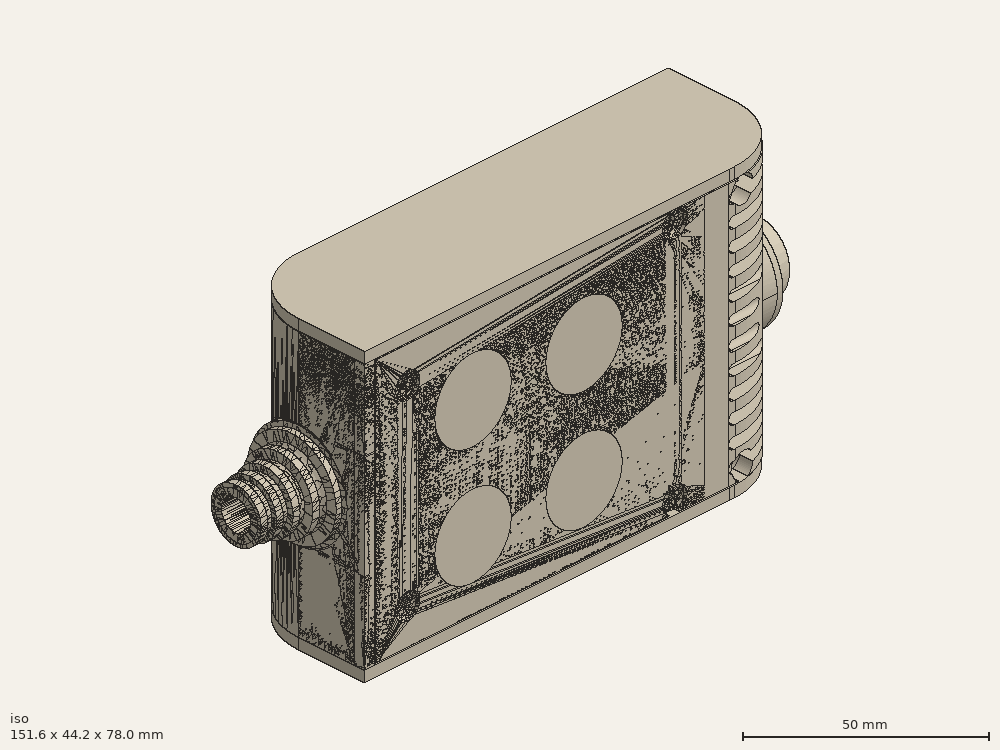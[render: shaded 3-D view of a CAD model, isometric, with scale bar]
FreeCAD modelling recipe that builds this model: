
FCSTD DOCUMENT  (FreeCAD 0.19R0.19.2)
Label: enclosure_203FCStd
License: All rights reserved
LicenseURL: http://en.wikipedia.org/wiki/All_rights_reserved
objects: Part::Revolution×152, Part::MultiFuse×146, Part::Feature×146, Sketcher::SketchObject×84, Part::Cut×70, Part::Cylinder×70, Part::Extrusion×67, Part::Fillet×58, Part::Box×36, App::MeasureDistance×4, PartDesign::Body×2, Image::ImagePlane×1
note: 831 computed .brp shape members not serialized (recipe doc carries the construction recipe); baked Part::Feature solids carry a one-line shape summary decoded from their .brp

FEATURE [Sketcher::SketchObject] Sketch  label="topSketch"
  FullyConstrained = true
  sketch-geometry (20):
    g0: LineSegment StartX=5.21097e-06 StartY=3 StartZ=0 EndX=5.21097e-06 EndY=19 EndZ=0
    g1: ArcOfCircle CenterX=19 CenterY=19 CenterZ=0 NormalX=0 NormalY=0 NormalZ=1 AngleXU=0 Radius=19 StartAngle=1.5708 EndAngle=3.14159
    g2: ArcOfCircle CenterX=19 CenterY=19 CenterZ=0 NormalX=0 NormalY=0 NormalZ=1 AngleXU=0 Radius=16 StartAngle=1.5708 EndAngle=3.14159
    g3: LineSegment StartX=114 StartY=35 StartZ=0 EndX=19 EndY=35 EndZ=0
    g4: LineSegment StartX=5.21097e-06 StartY=3 StartZ=0 EndX=5.21097e-06 EndY=0 EndZ=0
    g5: LineSegment StartX=3 StartY=0 StartZ=0 EndX=5.21097e-06 EndY=0 EndZ=0
    g6: LineSegment StartX=3 StartY=19 StartZ=0 EndX=3 EndY=0 EndZ=0
    g7: LineSegment StartX=19 StartY=38 StartZ=0 EndX=124 EndY=38 EndZ=0
    g8: Circle CenterX=119 CenterY=35 CenterZ=0 NormalX=0 NormalY=0 NormalZ=1 AngleXU=0 Radius=1
    g9: Circle CenterX=121 CenterY=35 CenterZ=0 NormalX=0 NormalY=0 NormalZ=1 AngleXU=0 Radius=1
    g10: Circle CenterX=121 CenterY=33 CenterZ=0 NormalX=0 NormalY=0 NormalZ=1 AngleXU=0 Radius=1
    g11: BSplineCurve PolesCount=3 KnotsCount=2 Degree=2 IsPeriodic=0
    g12: GeomPoint X=119 Y=35 Z=0
    g13: GeomPoint X=121 Y=33 Z=0
    g14: LineSegment StartX=119 StartY=35 StartZ=0 EndX=114 EndY=35 EndZ=0
    g15: ArcOfCircle CenterX=105 CenterY=19 CenterZ=0 NormalX=0 NormalY=0 NormalZ=1 AngleXU=0 Radius=19 StartAngle=5.7297 EndAngle=6.28319
    g16: ArcOfCircle CenterX=105 CenterY=19 CenterZ=0 NormalX=0 NormalY=0 NormalZ=1 AngleXU=0 Radius=16 StartAngle=5.60905 EndAngle=6.28319
    g17: LineSegment StartX=121 StartY=33 StartZ=0 EndX=121 EndY=19 EndZ=0
    g18: LineSegment StartX=124 StartY=38 StartZ=0 EndX=124 EndY=19 EndZ=0
    g19: LineSegment StartX=117.5 StartY=9.01251 StartZ=0 EndX=121.163 EndY=9.0125 EndZ=0
  constraints (46):
    c: Vertical(g0)
    c: Block(g0)
    c: Coincident(g1,g0)
    c: Block(g1)
    c: Coincident(g2,g1)
    c: Block(g2)
    c: Coincident(g3,g2)
    c: Horizontal(g3)
    c: Tangent(g3,g2)
    c: Coincident(g4,g0)
    c: Distance(g4) = 3
    c: Vertical(g4)
    c: Coincident(g5,g4)
    c: Horizontal(g5)
    c: Coincident(g6,g2)
    c: Coincident(g6,g5)
    c: Vertical(g6)
    c: Horizontal(g7)
    c: Distance(g7) = 105
    c: Coincident(g7,g1)
    c: Block(g3)
    c: Weight(g8) = 1
    c: Equal(g8,g9)
    c: Equal(g8,g10)
    c: InternalAlignment(g8,g11)
    c: InternalAlignment(g9,g11)
    c: InternalAlignment(g10,g11)
    c: InternalAlignment(g12,g11)
    c: InternalAlignment(g13,g11)
    c: Block(g11)
    c: Coincident(g14,g11)
    c: Coincident(g14,g3)
    c: Horizontal(g14)
    c: Block(g15)
    c: Coincident(g16,g15)
    c: Block(g16)
    c: Coincident(g17,g11)
    c: Coincident(g17,g16)
    c: Vertical(g17)
    c: Distance(g17) = 14
    c: Coincident(g18,g7)
    c: Coincident(g18,g15)
    c: Vertical(g18)
    c: Distance(g18) = 19
    c: Coincident(g19,g16)
    c: Coincident(g19,g15)
FEATURE [Sketcher::SketchObject] Sketch001  label="bottomSketch"
  FullyConstrained = true
  sketch-geometry (32):
    g0: LineSegment StartX=3.3 StartY=-6.03275e-07 StartZ=0 EndX=98 EndY=-6.03275e-07 EndZ=0
    g1: ArcOfCircle CenterX=98 CenterY=19 CenterZ=0 NormalX=0 NormalY=0 NormalZ=1 AngleXU=0 Radius=19 StartAngle=4.71239 EndAngle=5.71103
    g2: LineSegment StartX=6.3 StartY=8 StartZ=0 EndX=3.3 EndY=8 EndZ=0
    g3: LineSegment StartX=3.3 StartY=8 StartZ=0 EndX=3.3 EndY=-6.03275e-07 EndZ=0
    g4: ArcOfCircle CenterX=8.3 CenterY=5 CenterZ=0 NormalX=0 NormalY=0 NormalZ=1 AngleXU=0 Radius=2 StartAngle=3.14159 EndAngle=4.71239
    g5: LineSegment StartX=6.3 StartY=8 StartZ=0 EndX=6.3 EndY=5 EndZ=0
    g6: ArcOfCircle CenterX=98 CenterY=19 CenterZ=0 NormalX=0 NormalY=0 NormalZ=1 AngleXU=0 Radius=12.7 StartAngle=4.71239 EndAngle=6.28319
    g7: LineSegment StartX=94.7 StartY=3 StartZ=0 EndX=8.3 EndY=3 EndZ=0
    g8-g12: Circle x5 (B-spline internal-alignment scaffolding for g13; pole/knot coordinates omitted)
    g13: BSplineCurve PolesCount=5 KnotsCount=3 Degree=3 IsPeriodic=0
    g14: GeomPoint X=98 Y=6.3 Z=0
    g15: GeomPoint X=96.3938 Y=4.71946 Z=0
    g16: GeomPoint X=94.7 Y=3 Z=0
    g17-g23: Circle x7 (B-spline internal-alignment scaffolding for g24; pole/knot coordinates omitted)
    g24: BSplineCurve PolesCount=7 KnotsCount=5 Degree=3 IsPeriodic=0
    g25-g29: GeomPoint x5 (B-spline internal-alignment scaffolding for g24; pole/knot coordinates omitted)
    g30: ArcOfCircle CenterX=98 CenterY=19 CenterZ=0 NormalX=0 NormalY=0 NormalZ=1 AngleXU=0 Radius=15.7 StartAngle=5.81226 EndAngle=6.28319
    g31: LineSegment StartX=110.7 StartY=19 StartZ=0 EndX=113.7 EndY=19 EndZ=0
  constraints (41):
    c: Horizontal(g0)
    c: Coincident(g1,g0)
    c: Block(g1)
    c: Horizontal(g2)
    c: Distance(g2) = 3
    c: Coincident(g3,g2)
    c: Vertical(g3)
    c: Coincident(g3,g0)
    c: Block(g4)
    c: Block(g2)
    c: Coincident(g5,g2)
    c: Coincident(g5,g4)
    c: Vertical(g5)
    c: Coincident(g6,g1)
    c: Block(g6)
    c: Coincident(g7,g4)
    c: Horizontal(g7)
    c: Block(g0)
    c: Block(g7)
    c: Block(g3)
    c: Coincident(g13,g6)
    c: Weight(g8) = 1
    c: Equal(g8, g9-g12) x4
    c: Coincident(g13,g7)
    c: InternalAlignment(g8-g12 -> g13) x5
    c: InternalAlignment(g14,g13)
    c: InternalAlignment(g15,g13)
    c: InternalAlignment(g16,g13)
    c: Block(g13)
    c: Weight(g17) = 1
    c: Equal(g17, g18-g23) x6
    c: Coincident(g24,g1)
    c: InternalAlignment(g17-g23 -> g24) x7
    c: InternalAlignment(g25-g29 -> g24) x5
    c: Block(g24)
    c: Coincident(g30,g24)
    c: Coincident(g31,g6)
    c: Coincident(g31,g30)
    c: Horizontal(g31)
    c: Block(g31)
    c: Block(g30)
FEATURE [Part::Extrusion] Extrude  label="top"
  Base = -> Sketch
  Dir = (0,0,1)
  DirMode = 2
  FaceMakerClass = Part::FaceMakerBullseye
  LengthFwd = 72
  LengthRev = 0
  Solid = true
  Symmetric = false
FEATURE [Part::Extrusion] Extrude001  label="bottom"
  Base = -> Sketch001
  Dir = (0,0,1)
  DirMode = 2
  FaceMakerClass = Part::FaceMakerBullseye
  LengthFwd = 71.4
  LengthRev = 0
  Placement = pos=(0,0,0.3) rot=(0,0,1;0rad)
  Solid = true
  Symmetric = false
FEATURE [Sketcher::SketchObject] Sketch002  label="topSketch001"
  FullyConstrained = true
  sketch-geometry (8):
    g0: ArcOfCircle CenterX=19 CenterY=19.0975 CenterZ=0 NormalX=0 NormalY=0 NormalZ=1 AngleXU=0 Radius=18.9025 StartAngle=1.5708 EndAngle=3.14674
    g1: LineSegment StartX=0.0977805 StartY=19.0003 StartZ=0 EndX=0.0977805 EndY=0.000251602 EndZ=0
    g2: LineSegment StartX=19 StartY=38 StartZ=0 EndX=124 EndY=38 EndZ=0
    g3: LineSegment StartX=0.0977805 StartY=0.000251602 StartZ=0 EndX=105.098 EndY=0.000251602 EndZ=0
    g4: LineSegment StartX=124 StartY=38 StartZ=0 EndX=125.616 EndY=38 EndZ=0
    g5: LineSegment StartX=105.098 StartY=0.000251602 StartZ=0 EndX=106.713 EndY=0.000251602 EndZ=0
    g6: ArcOfCircle CenterX=106.616 CenterY=19 CenterZ=0 NormalX=0 NormalY=0 NormalZ=1 AngleXU=0 Radius=19 StartAngle=4.71754 EndAngle=6.28319
    g7: LineSegment StartX=125.616 StartY=38 StartZ=0 EndX=125.616 EndY=19 EndZ=0
  constraints (21):
    c: Block(g0)
    c: Coincident(g1,g0)
    c: Vertical(g1)
    c: Horizontal(g2)
    c: Distance(g2) = 105
    c: Coincident(g2,g0)
    c: Distance(g1) = 19
    c: Coincident(g3,g1)
    c: Horizontal(g3)
    c: Distance(g3) = 105
    c: Coincident(g4,g2)
    c: Horizontal(g4)
    c: Distance(g4) = 1.61553
    c: Horizontal(g5)
    c: Equal(g4,g5) = 1.61553
    c: Coincident(g5,g3)
    c: Block(g6)
    c: Coincident(g6,g5)
    c: Coincident(g7,g4)
    c: Coincident(g7,g6)
    c: Vertical(g7)
FEATURE [Part::Extrusion] Extrude002  label="sideA"
  Base = -> Sketch002
  Dir = (0,0,1)
  DirMode = 2
  FaceMakerClass = Part::FaceMakerBullseye
  LengthFwd = 3
  LengthRev = 0
  Placement = pos=(0,0,-3) rot=(0,0,1;0rad)
  Solid = true
  Symmetric = false
FEATURE [Sketcher::SketchObject] Sketch003  label="topSketch002"
  FullyConstrained = true
  sketch-geometry (6):
    g0: LineSegment StartX=19 StartY=38 StartZ=0 EndX=117 EndY=38 EndZ=0
    g1: ArcOfCircle CenterX=19 CenterY=19 CenterZ=0 NormalX=0 NormalY=0 NormalZ=1 AngleXU=0 Radius=19 StartAngle=1.5708 EndAngle=3.14159
    g2: LineSegment StartX=117 StartY=38 StartZ=0 EndX=117 EndY=19 EndZ=0
    g3: LineSegment StartX=98 StartY=1.0161e-12 StartZ=0 EndX=5.22862e-06 EndY=1.0161e-12 EndZ=0
    g4: LineSegment StartX=5.22862e-06 StartY=19 StartZ=0 EndX=5.22862e-06 EndY=1.0161e-12 EndZ=0
    g5: ArcOfCircle CenterX=98 CenterY=19 CenterZ=0 NormalX=0 NormalY=0 NormalZ=1 AngleXU=0 Radius=19 StartAngle=4.71239 EndAngle=6.28319
  constraints (16):
    c: Horizontal(g0)
    c: Distance(g0) = 98
    c: Coincident(g1,g0)
    c: Block(g1)
    c: Coincident(g2,g0)
    c: Vertical(g2)
    c: Distance(g2) = 19
    c: Horizontal(g3)
    c: Coincident(g4,g1)
    c: Vertical(g4)
    c: Coincident(g3,g4)
    c: Block(g3)
    c: Coincident(g5,g2)
    c: Coincident(g5,g3)
    c: Block(g0)
    c: Block(g5)
FEATURE [Sketcher::SketchObject] Sketch004
  FullyConstrained = true
  MapMode = 3
  Placement = pos=(0,0,0) rot=(1,0,0;1.5708rad)
  Support = -> [Extrude]
  sketch-geometry (8):
    g0: Circle CenterX=80.351 CenterY=-67.6202 CenterZ=0 NormalX=0 NormalY=0 NormalZ=1 AngleXU=0 Radius=2
    g1: Circle CenterX=80.351 CenterY=-67.6202 CenterZ=0 NormalX=0 NormalY=0 NormalZ=1 AngleXU=0 Radius=3
    g2: Circle CenterX=80.351 CenterY=-4.92017 CenterZ=0 NormalX=0 NormalY=0 NormalZ=1 AngleXU=0 Radius=2
    g3: Circle CenterX=80.351 CenterY=-4.92017 CenterZ=0 NormalX=0 NormalY=0 NormalZ=1 AngleXU=0 Radius=3
    g4: Circle CenterX=23.851 CenterY=-4.92017 CenterZ=0 NormalX=0 NormalY=0 NormalZ=1 AngleXU=0 Radius=2
    g5: Circle CenterX=23.851 CenterY=-4.92017 CenterZ=0 NormalX=0 NormalY=0 NormalZ=1 AngleXU=0 Radius=3
    g6: Circle CenterX=23.851 CenterY=-67.6202 CenterZ=0 NormalX=0 NormalY=0 NormalZ=1 AngleXU=0 Radius=2
    g7: Circle CenterX=23.851 CenterY=-67.6202 CenterZ=0 NormalX=0 NormalY=0 NormalZ=1 AngleXU=0 Radius=3
  constraints (8):
    c: Block(g3)
    c: Block(g2)
    c: Block(g1)
    c: Block(g0)
    c: Block(g6)
    c: Block(g7)
    c: Block(g4)
    c: Block(g5)
FEATURE [Part::Extrusion] Extrude004
  Base = -> Sketch004
  Dir = (0,-1,2e-16)
  DirMode = 2
  FaceMakerClass = Part::FaceMakerBullseye
  LengthFwd = 6
  LengthRev = 0
  Placement = pos=(0,9,0) rot=(0,0,1;0rad)
  Solid = true
  Symmetric = false
FEATURE [Sketcher::SketchObject] Sketch005
  FullyConstrained = true
  MapMode = 3
  Placement = pos=(0,0,0) rot=(1,0,0;1.5708rad)
  Support = -> [Extrude]
  sketch-geometry (8):
    g0: Circle CenterX=80.351 CenterY=-67.6202 CenterZ=0 NormalX=0 NormalY=0 NormalZ=1 AngleXU=0 Radius=3
    g1: Circle CenterX=80.351 CenterY=-4.92017 CenterZ=0 NormalX=0 NormalY=0 NormalZ=1 AngleXU=0 Radius=3
    g2: Circle CenterX=23.851 CenterY=-4.92017 CenterZ=0 NormalX=0 NormalY=0 NormalZ=1 AngleXU=0 Radius=3
    g3: Circle CenterX=23.851 CenterY=-67.6202 CenterZ=0 NormalX=0 NormalY=0 NormalZ=1 AngleXU=0 Radius=3
    g4: Circle CenterX=23.851 CenterY=-67.6202 CenterZ=0 NormalX=0 NormalY=0 NormalZ=1 AngleXU=0 Radius=5
    g5: Circle CenterX=80.351 CenterY=-67.6202 CenterZ=0 NormalX=0 NormalY=0 NormalZ=1 AngleXU=0 Radius=5
    g6: Circle CenterX=23.851 CenterY=-4.92017 CenterZ=0 NormalX=0 NormalY=0 NormalZ=1 AngleXU=0 Radius=5
    g7: Circle CenterX=80.351 CenterY=-4.92017 CenterZ=0 NormalX=0 NormalY=0 NormalZ=1 AngleXU=0 Radius=5
  constraints (8):
    c: Block(g1)
    c: Block(g0)
    c: Block(g3)
    c: Block(g2)
    c: Block(g5)
    c: Block(g4)
    c: Block(g6)
    c: Block(g7)
FEATURE [Part::Extrusion] Extrude005
  Base = -> Sketch005
  Dir = (0,-1,2e-16)
  DirMode = 2
  FaceMakerClass = Part::FaceMakerBullseye
  LengthFwd = 2
  LengthRev = 0
  Solid = true
  Symmetric = false
FEATURE [Sketcher::SketchObject] Sketch006
  FullyConstrained = true
  MapMode = 3
  Placement = pos=(0,0,0) rot=(1,0,0;1.5708rad)
  sketch-geometry (8):
    g0: Circle CenterX=80.351 CenterY=-67.6202 CenterZ=0 NormalX=0 NormalY=0 NormalZ=1 AngleXU=0 Radius=3
    g1: Circle CenterX=80.351 CenterY=-4.92017 CenterZ=0 NormalX=0 NormalY=0 NormalZ=1 AngleXU=0 Radius=3
    g2: Circle CenterX=23.851 CenterY=-4.92017 CenterZ=0 NormalX=0 NormalY=0 NormalZ=1 AngleXU=0 Radius=3
    g3: Circle CenterX=23.851 CenterY=-67.6202 CenterZ=0 NormalX=0 NormalY=0 NormalZ=1 AngleXU=0 Radius=3
    g4: Circle CenterX=23.851 CenterY=-67.6202 CenterZ=0 NormalX=0 NormalY=0 NormalZ=1 AngleXU=0 Radius=5
    g5: Circle CenterX=80.351 CenterY=-67.6202 CenterZ=0 NormalX=0 NormalY=0 NormalZ=1 AngleXU=0 Radius=5
    g6: Circle CenterX=23.851 CenterY=-4.92017 CenterZ=0 NormalX=0 NormalY=0 NormalZ=1 AngleXU=0 Radius=5
    g7: Circle CenterX=80.351 CenterY=-4.92017 CenterZ=0 NormalX=0 NormalY=0 NormalZ=1 AngleXU=0 Radius=5
  constraints (8):
    c: Block(g1)
    c: Block(g0)
    c: Block(g3)
    c: Block(g2)
    c: Block(g5)
    c: Block(g4)
    c: Block(g6)
    c: Block(g7)
FEATURE [Part::Extrusion] Extrude007
  Base = -> Sketch006
  Dir = (0,-1,2e-16)
  DirMode = 2
  FaceMakerClass = Part::FaceMakerBullseye
  LengthFwd = 2
  LengthRev = 0
  Solid = true
  Symmetric = false
FEATURE [Part::Fillet] Fillet
  Base = -> Extrude007
  Edges = 4 edges r=1.99: [Edge6,Edge12,Edge18,Edge24]
FEATURE [Part::Cut] Cut
  Base = -> Extrude005
  Placement = pos=(0,5,0) rot=(0,0,1;0rad)
  Tool = -> Fillet
FEATURE [Part::MultiFuse] Fusion  label="pCBScrews"
  Placement = pos=(-2.5,0,72.3) rot=(0,0,1;0rad)
  Shapes = -> [Extrude004,Cut]
FEATURE [App::MeasureDistance] Distance  label="Distance: 0.69 mm"
  Distance = 0.685967
  P1 = (24.0138,2.9647,0.3)
  P2 = (23.8901,3,-0.373787)
FEATURE [App::MeasureDistance] Distance001  label="Distance: 0.53 mm"
  Distance = 0.533607
  P1 = (80.2939,3,72.2334)
  P2 = (80.281,2.99661,71.7)
FEATURE [Part::Fillet] Fillet001
  Base = -> Extrude001
  Edges = 1 edges r=2.4: [Edge17]
FEATURE [Part::Fillet] Fillet002  label="bottom001"
  Base = -> Fillet001
  Edges = 1 edges r=2.4: [Edge36]
FEATURE [Part::Fillet] Fillet003  label="top001"
  Base = -> Extrude
  Edges = 1 edges r=2: [Edge1]
FEATURE [Sketcher::SketchObject] Sketch007
  FullyConstrained = true
  sketch-geometry (16):
    g0: LineSegment StartX=4 StartY=0 StartZ=0 EndX=4 EndY=2.4 EndZ=0
    g1: LineSegment StartX=4 StartY=2.4 StartZ=0 EndX=7 EndY=2.4 EndZ=0
    g2: LineSegment StartX=4 StartY=0 StartZ=0 EndX=5.7 EndY=0 EndZ=0
    g3: LineSegment StartX=5.7 StartY=0 StartZ=0 EndX=5.7 EndY=-5.6 EndZ=0
    g4-g8: Circle x5 (B-spline internal-alignment scaffolding for g9; pole/knot coordinates omitted)
    g9: BSplineCurve PolesCount=5 KnotsCount=3 Degree=3 IsPeriodic=0
    g10: GeomPoint X=7 Y=2.4 Z=0
    g11: GeomPoint X=10.4582 Y=-1.55472 Z=0
    g12: GeomPoint X=14 Y=-5.6 Z=0
    g13: LineSegment StartX=14 StartY=-5.6 StartZ=0 EndX=14 EndY=-14.1 EndZ=0
    g14: LineSegment StartX=14 StartY=-14.1 StartZ=0 EndX=6.5 EndY=-14.1 EndZ=0
    g15: LineSegment StartX=5.7 StartY=-5.6 StartZ=0 EndX=6.5 EndY=-14.1 EndZ=0
  constraints (28):
    c: Distance(g0) = 2.4
    c: Vertical(g0)
    c: Block(g0)
    c: Coincident(g1,g0)
    c: Horizontal(g1)
    c: Distance(g1) = 3
    c: Coincident(g2,g0)
    c: Horizontal(g2)
    c: Distance(g2) = 1.7
    c: Coincident(g3,g2)
    c: Vertical(g3)
    c: Distance(g3) = 5.6
    c: Coincident(g9,g1)
    c: Weight(g4) = 1
    c: Equal(g4, g5-g8) x4
    c: InternalAlignment(g4-g8 -> g9) x5
    c: InternalAlignment(g10,g9)
    c: InternalAlignment(g11,g9)
    c: InternalAlignment(g12,g9)
    c: Block(g9)
    c: Coincident(g13,g9)
    c: Vertical(g13)
    c: Distance(g13) = 8.5
    c: Coincident(g14,g13)
    c: Horizontal(g14)
    c: Distance(g14) = 7.5
    c: Coincident(g15,g3)
    c: Coincident(g15,g14)
FEATURE [Part::Feature] Face
  shape: bbox 10 x 16.5 x 2e-07 mm, 1 faces, 0 solids (baked)
FEATURE [Part::Revolution] Revolve  label="plugHousing"
  Angle = 360
  Axis = (0,1,0)
  Base = (0,0,0)
  FaceMakerClass = Part::FaceMakerBullseye
  Placement = pos=(0,0,36.15) rot=(0,0,1;0rad)
  Solid = false
  Source = -> Face
  Symmetric = false
FEATURE [Part::Feature] Face001
  shape: bbox 10 x 16.5 x 2e-07 mm, 1 faces, 0 solids (baked)
FEATURE [Part::Revolution] Revolve001  label="plugHousing001"
  Angle = 360
  Axis = (0,1,0)
  Base = (0,0,0)
  FaceMakerClass = Part::FaceMakerBullseye
  Placement = pos=(0,0,36.15) rot=(0,0,1;0rad)
  Solid = false
  Source = -> Face001
  Symmetric = false
FEATURE [Part::MultiFuse] Fusion001  label="plugHousing002"
  Placement = pos=(0,0,0) rot=(0,0,1;1.5708rad)
  Shapes = -> [Revolve001,Revolve]
FEATURE [Part::Feature] Face002
  shape: bbox 10 x 16.5 x 2e-07 mm, 1 faces, 0 solids (baked)
FEATURE [Part::Revolution] Revolve003  label="plugHousing005"
  Angle = 360
  Axis = (0,1,0)
  Base = (0,0,0)
  FaceMakerClass = Part::FaceMakerBullseye
  Placement = pos=(0,0,36.15) rot=(0,0,1;0rad)
  Solid = false
  Source = -> Face002
  Symmetric = false
FEATURE [Part::Feature] Face003
  shape: bbox 10 x 16.5 x 2e-07 mm, 1 faces, 0 solids (baked)
FEATURE [Part::Revolution] Revolve002  label="plugHousing003"
  Angle = 360
  Axis = (0,1,0)
  Base = (0,0,0)
  FaceMakerClass = Part::FaceMakerBullseye
  Placement = pos=(0,0,36.15) rot=(0,0,1;0rad)
  Solid = false
  Source = -> Face003
  Symmetric = false
FEATURE [Part::MultiFuse] Fusion002  label="plugHousing004"
  Placement = pos=(0,0,0) rot=(0,0,1;1.5708rad)
  Shapes = -> [Revolve002,Revolve003]
FEATURE [Part::MultiFuse] Fusion003  label="plugHousing006"
  Placement = pos=(0,19,0) rot=(0,0,1;3.14159rad)
  Shapes = -> [Fusion002,Fusion001]
FEATURE [Part::Feature] Face004
  shape: bbox 10 x 16.5 x 2e-07 mm, 1 faces, 0 solids (baked)
FEATURE [Part::Revolution] Revolve006  label="plugHousing010"
  Angle = 360
  Axis = (0,1,0)
  Base = (0,0,0)
  FaceMakerClass = Part::FaceMakerBullseye
  Placement = pos=(0,0,36.15) rot=(0,0,1;0rad)
  Solid = false
  Source = -> Face004
  Symmetric = false
FEATURE [Part::Feature] Face005
  shape: bbox 10 x 16.5 x 2e-07 mm, 1 faces, 0 solids (baked)
FEATURE [Part::Revolution] Revolve007  label="plugHousing011"
  Angle = 360
  Axis = (0,1,0)
  Base = (0,0,0)
  FaceMakerClass = Part::FaceMakerBullseye
  Placement = pos=(0,0,36.15) rot=(0,0,1;0rad)
  Solid = false
  Source = -> Face005
  Symmetric = false
FEATURE [Part::Feature] Face006
  shape: bbox 10 x 16.5 x 2e-07 mm, 1 faces, 0 solids (baked)
FEATURE [Part::Revolution] Revolve004  label="plugHousing007"
  Angle = 360
  Axis = (0,1,0)
  Base = (0,0,0)
  FaceMakerClass = Part::FaceMakerBullseye
  Placement = pos=(0,0,36.15) rot=(0,0,1;0rad)
  Solid = false
  Source = -> Face006
  Symmetric = false
FEATURE [Part::MultiFuse] Fusion004  label="plugHousing009"
  Placement = pos=(0,0,0) rot=(0,0,1;1.5708rad)
  Shapes = -> [Revolve004,Revolve007]
FEATURE [Part::Feature] Face007
  shape: bbox 10 x 16.5 x 2e-07 mm, 1 faces, 0 solids (baked)
FEATURE [Part::Revolution] Revolve005  label="plugHousing008"
  Angle = 360
  Axis = (0,1,0)
  Base = (0,0,0)
  FaceMakerClass = Part::FaceMakerBullseye
  Placement = pos=(0,0,36.15) rot=(0,0,1;0rad)
  Solid = false
  Source = -> Face007
  Symmetric = false
FEATURE [Part::MultiFuse] Fusion005  label="plugHousing012"
  Placement = pos=(0,0,0) rot=(0,0,1;1.5708rad)
  Shapes = -> [Revolve006,Revolve005]
FEATURE [Part::MultiFuse] Fusion006  label="plugHousing013"
  Placement = pos=(0,19,0) rot=(0,0,1;3.14159rad)
  Shapes = -> [Fusion005,Fusion004]
FEATURE [Part::MultiFuse] Fusion007  label="plugHousing014"
  Placement = pos=(122.621,0,-0.15) rot=(0,0,1;0rad)
  Shapes = -> [Fusion003,Fusion006]
FEATURE [Part::Cylinder] Cylinder002
  Angle = 360
  AttacherType = Attacher::AttachEngine3D
  Height = 20
  Placement = pos=(0,0,36.15) rot=(0,0,1;0rad)
  Radius = 4
FEATURE [Part::Cylinder] Cylinder003
  Angle = 360
  AttacherType = Attacher::AttachEngine3D
  Height = 10
  Placement = pos=(0,0,36.15) rot=(0,0,1;0rad)
  Radius = 4
FEATURE [Part::MultiFuse] Fusion009  label="removeToCreateHoleForPlugHousing"
  Placement = pos=(70,19,36.15) rot=(0,1,0;1.5708rad)
  Shapes = -> [Cylinder002,Cylinder003]
FEATURE [Part::Cylinder] Cylinder004
  Angle = 360
  AttacherType = Attacher::AttachEngine3D
  Height = 20
  Placement = pos=(0,0,36.15) rot=(0,0,1;0rad)
  Radius = 4
FEATURE [Part::Cylinder] Cylinder005
  Angle = 360
  AttacherType = Attacher::AttachEngine3D
  Height = 10
  Placement = pos=(0,0,36.15) rot=(0,0,1;0rad)
  Radius = 4
FEATURE [Part::MultiFuse] Fusion010  label="removeToCreateHoleForPlugHousing001"
  Placement = pos=(70,19,36.15) rot=(0,1,0;1.5708rad)
  Shapes = -> [Cylinder004,Cylinder005]
FEATURE [Part::Cut] Cut001
  Base = -> Fillet003
  Tool = -> Fusion010
FEATURE [Part::Cut] Cut002  label="Bottom"
  Base = -> Fillet002
  Tool = -> Fusion009
FEATURE [Part::Feature] Face008
  shape: bbox 10 x 16.5 x 2e-07 mm, 1 faces, 0 solids (baked)
FEATURE [Part::Revolution] Revolve011  label="plugHousing021"
  Angle = 360
  Axis = (0,1,0)
  Base = (0,0,0)
  FaceMakerClass = Part::FaceMakerBullseye
  Placement = pos=(0,0,36.15) rot=(0,0,1;0rad)
  Solid = false
  Source = -> Face008
  Symmetric = false
FEATURE [Part::Feature] Face009
  shape: bbox 10 x 16.5 x 2e-07 mm, 1 faces, 0 solids (baked)
FEATURE [Part::Revolution] Revolve012  label="plugHousing022"
  Angle = 360
  Axis = (0,1,0)
  Base = (0,0,0)
  FaceMakerClass = Part::FaceMakerBullseye
  Placement = pos=(0,0,36.15) rot=(0,0,1;0rad)
  Solid = false
  Source = -> Face009
  Symmetric = false
FEATURE [Part::Feature] Face010 .. Face013  x4 (patterned run collapsed; names and placements below)
  shape: bbox 10 x 16.5 x 2e-07 mm, 1 faces, 0 solids (baked)
FEATURE [Part::Revolution] Revolve015  label="plugHousing027"
  Angle = 360
  Axis = (0,1,0)
  Base = (0,0,0)
  FaceMakerClass = Part::FaceMakerBullseye
  Placement = pos=(0,0,36.15) rot=(0,0,1;0rad)
  Solid = false
  Source = -> Face013
  Symmetric = false
FEATURE [Part::Feature] Face014
  shape: bbox 10 x 16.5 x 2e-07 mm, 1 faces, 0 solids (baked)
FEATURE [Part::Feature] Face015
  shape: bbox 10 x 16.5 x 2e-07 mm, 1 faces, 0 solids (baked)
FEATURE [Part::Feature] Face016
  shape: bbox 10 x 16.5 x 2e-07 mm, 1 faces, 0 solids (baked)
FEATURE [Part::Revolution] Revolve019  label="plugHousing033"
  Angle = 360
  Axis = (0,1,0)
  Base = (0,0,0)
  FaceMakerClass = Part::FaceMakerBullseye
  Placement = pos=(0,0,36.15) rot=(0,0,1;0rad)
  Solid = false
  Source = -> Face016
  Symmetric = false
FEATURE [Part::Feature] Face017
  shape: bbox 10 x 16.5 x 2e-07 mm, 1 faces, 0 solids (baked)
FEATURE [Part::Revolution] Revolve020  label="plugHousing034"
  Angle = 360
  Axis = (0,1,0)
  Base = (0,0,0)
  FaceMakerClass = Part::FaceMakerBullseye
  Placement = pos=(0,0,36.15) rot=(0,0,1;0rad)
  Solid = false
  Source = -> Face017
  Symmetric = false
FEATURE [Part::Feature] Face018
  shape: bbox 10 x 16.5 x 2e-07 mm, 1 faces, 0 solids (baked)
FEATURE [Part::Revolution] Revolve016  label="plugHousing030"
  Angle = 360
  Axis = (0,1,0)
  Base = (0,0,0)
  FaceMakerClass = Part::FaceMakerBullseye
  Placement = pos=(0,0,36.15) rot=(0,0,1;0rad)
  Solid = false
  Source = -> Face018
  Symmetric = false
FEATURE [Part::MultiFuse] Fusion020  label="plugHousing038"
  Placement = pos=(0,0,0) rot=(0,0,1;1.5708rad)
  Shapes = -> [Revolve016,Revolve020]
FEATURE [Part::Feature] Face019
  shape: bbox 10 x 16.5 x 2e-07 mm, 1 faces, 0 solids (baked)
FEATURE [Part::Feature] Face020
  shape: bbox 10 x 16.5 x 2e-07 mm, 1 faces, 0 solids (baked)
FEATURE [Part::Revolution] Revolve017  label="plugHousing031"
  Angle = 360
  Axis = (0,1,0)
  Base = (0,0,0)
  FaceMakerClass = Part::FaceMakerBullseye
  Placement = pos=(0,0,36.15) rot=(0,0,1;0rad)
  Solid = false
  Source = -> Face020
  Symmetric = false
FEATURE [Part::MultiFuse] Fusion021  label="plugHousing039"
  Placement = pos=(0,0,0) rot=(0,0,1;1.5708rad)
  Shapes = -> [Revolve019,Revolve017]
FEATURE [Part::MultiFuse] Fusion023  label="plugHousing041"
  Placement = pos=(0,19,0) rot=(0,0,1;3.14159rad)
  Shapes = -> [Fusion021,Fusion020]
FEATURE [Part::Revolution] Revolve022  label="plugHousing043"
  Angle = 360
  Axis = (0,1,0)
  Base = (0,0,0)
  FaceMakerClass = Part::FaceMakerBullseye
  Placement = pos=(0,0,36.15) rot=(0,0,1;0rad)
  Solid = false
  Source = -> Face019
  Symmetric = false
FEATURE [Part::Feature] Face021
  shape: bbox 10 x 16.5 x 2e-07 mm, 1 faces, 0 solids (baked)
FEATURE [Part::Revolution] Revolve023  label="plugHousing044"
  Angle = 360
  Axis = (0,1,0)
  Base = (0,0,0)
  FaceMakerClass = Part::FaceMakerBullseye
  Placement = pos=(0,0,36.15) rot=(0,0,1;0rad)
  Solid = false
  Source = -> Face021
  Symmetric = false
FEATURE [Part::Feature] Face022
  shape: bbox 10 x 16.5 x 2e-07 mm, 1 faces, 0 solids (baked)
FEATURE [Part::Revolution] Revolve018  label="plugHousing032"
  Angle = 360
  Axis = (0,1,0)
  Base = (0,0,0)
  FaceMakerClass = Part::FaceMakerBullseye
  Placement = pos=(0,0,36.15) rot=(0,0,1;0rad)
  Solid = false
  Source = -> Face022
  Symmetric = false
FEATURE [Part::MultiFuse] Fusion022  label="plugHousing040"
  Placement = pos=(0,0,0) rot=(0,0,1;1.5708rad)
  Shapes = -> [Revolve018,Revolve023]
FEATURE [Part::Feature] Face023
  shape: bbox 10 x 16.5 x 2e-07 mm, 1 faces, 0 solids (baked)
FEATURE [Part::Revolution] Revolve021  label="plugHousing035"
  Angle = 360
  Axis = (0,1,0)
  Base = (0,0,0)
  FaceMakerClass = Part::FaceMakerBullseye
  Placement = pos=(0,0,36.15) rot=(0,0,1;0rad)
  Solid = false
  Source = -> Face023
  Symmetric = false
FEATURE [Part::MultiFuse] Fusion018  label="plugHousing036"
  Placement = pos=(0,0,0) rot=(0,0,1;1.5708rad)
  Shapes = -> [Revolve022,Revolve021]
FEATURE [Part::MultiFuse] Fusion019  label="plugHousing037"
  Placement = pos=(0,19,0) rot=(0,0,1;3.14159rad)
  Shapes = -> [Fusion018,Fusion022]
FEATURE [Part::MultiFuse] Fusion024  label="plugHousing042"
  Placement = pos=(122.621,0,-0.15) rot=(0,0,1;0rad)
  Shapes = -> [Fusion023,Fusion019]
FEATURE [Part::Cylinder] Cylinder006
  Angle = 360
  AttacherType = Attacher::AttachEngine3D
  Height = 20
  Placement = pos=(0,0,36.15) rot=(0,0,1;0rad)
  Radius = 14.3
FEATURE [Part::Cylinder] Cylinder007
  Angle = 360
  AttacherType = Attacher::AttachEngine3D
  Height = 10
  Placement = pos=(0,0,36.15) rot=(0,0,1;0rad)
  Radius = 4
FEATURE [Part::MultiFuse] Fusion026  label="removeToCreteHoleForPlugHousing"
  Placement = pos=(70,19,36) rot=(0,1,0;1.5708rad)
  Shapes = -> [Cylinder006,Cylinder007]
FEATURE [Part::Box] Box001  label="Cube001"
  AttacherType = Attacher::AttachEngine3D
  Height = 28
  Length = 3
  Placement = pos=(110.7,19,22) rot=(0,0,1;0rad)
  Width = 15.7
FEATURE [Part::Cut] Cut003  label="top002"
  Base = -> Cut001
  Tool = -> Fusion007
FEATURE [Part::Revolution] Revolve008  label="plugHousing015"
  Angle = 360
  Axis = (0,1,0)
  Base = (0,0,0)
  FaceMakerClass = Part::FaceMakerBullseye
  Placement = pos=(0,0,36.15) rot=(0,0,1;0rad)
  Solid = false
  Source = -> Face010
  Symmetric = false
FEATURE [Part::MultiFuse] Fusion013  label="plugHousing020"
  Placement = pos=(0,0,0) rot=(0,0,1;1.5708rad)
  Shapes = -> [Revolve008,Revolve012]
FEATURE [Part::Cut] Cut004  label="top003"
  Base = -> Cut003
  Placement = pos=(1,0,0) rot=(0,0,1;0rad)
  Tool = -> Fusion026
FEATURE [Part::Cylinder] Cylinder008
  Angle = 360
  AttacherType = Attacher::AttachEngine3D
  Height = 20
  Placement = pos=(0,0,36.15) rot=(0,0,1;0rad)
  Radius = 10.3
FEATURE [Part::Cylinder] Cylinder009
  Angle = 360
  AttacherType = Attacher::AttachEngine3D
  Height = 10
  Placement = pos=(0,0,36.15) rot=(0,0,1;0rad)
  Radius = 4
FEATURE [Part::MultiFuse] Fusion027  label="removeToCreteHoleForPlugHousing001"
  Placement = pos=(70,19,36) rot=(0,1,0;1.5708rad)
  Shapes = -> [Cylinder008,Cylinder009]
FEATURE [Part::Cut] Cut005  label="plugHousingTab"
  Base = -> Box001
  Tool = -> Fusion027
FEATURE [Part::MultiFuse] Fusion028  label="plugHousing045"
  Shapes = -> [Fusion024,Cut005]
FEATURE [Part::Box] Box002  label="Cube002"
  AttacherType = Attacher::AttachEngine3D
  Height = 28.8
  Length = 3
  Placement = pos=(107.3,28,21.6) rot=(0,0,1;0rad)
  Width = 7
FEATURE [Part::Box] Box003  label="Cube003"
  AttacherType = Attacher::AttachEngine3D
  Height = 3
  Length = 6.4
  Placement = pos=(107.3,28,18.6) rot=(0,0,1;0rad)
  Width = 7
FEATURE [Part::Box] Box004  label="Cube004"
  AttacherType = Attacher::AttachEngine3D
  Height = 3
  Length = 6.4
  Placement = pos=(107.3,28,50.4) rot=(0,0,1;0rad)
  Width = 7
FEATURE [Part::MultiFuse] Fusion029  label="plugHousingBracketHolder"
  Shapes = -> [Box004,Box002,Box003]
FEATURE [Part::Cylinder] Cylinder010
  Angle = 360
  AttacherType = Attacher::AttachEngine3D
  Height = 20
  Placement = pos=(0,0,36.15) rot=(0,0,1;0rad)
  Radius = 14.3
FEATURE [Part::Cylinder] Cylinder011
  Angle = 360
  AttacherType = Attacher::AttachEngine3D
  Height = 10
  Placement = pos=(0,0,36.15) rot=(0,0,1;0rad)
  Radius = 4
FEATURE [Part::MultiFuse] Fusion030  label="removeToCreteHoleForPlugHousing002"
  Placement = pos=(70,19,36) rot=(0,1,0;1.5708rad)
  Shapes = -> [Cylinder010,Cylinder011]
FEATURE [Part::Cut] Cut006  label="plugHousingBracketHolder001"
  Base = -> Fusion029
  Tool = -> Fusion030
FEATURE [Part::Cylinder] Cylinder012
  Angle = 360
  AttacherType = Attacher::AttachEngine3D
  Height = 20
  Placement = pos=(0,0,36.15) rot=(0,0,1;0rad)
  Radius = 7
FEATURE [Part::Cylinder] Cylinder013
  Angle = 360
  AttacherType = Attacher::AttachEngine3D
  Height = 10
  Placement = pos=(0,0,36.15) rot=(0,0,1;0rad)
  Radius = 4
FEATURE [Part::MultiFuse] Fusion032  label="removeToCreteHoleForPlugHousing003"
  Placement = pos=(70,19,36) rot=(0,1,0;1.5708rad)
  Shapes = -> [Cylinder012,Cylinder013]
FEATURE [Part::Cut] Cut007  label="bottom002"
  Base = -> Cut002
  Tool = -> Fusion032
FEATURE [Sketcher::SketchObject] Sketch008
  FullyConstrained = true
  sketch-geometry (54):
    g0: LineSegment StartX=-4.2 StartY=0 StartZ=0 EndX=-6.2 EndY=0 EndZ=0
    g1: LineSegment StartX=-14 StartY=-18 StartZ=0 EndX=-14 EndY=-26.5 EndZ=0
    g2: LineSegment StartX=-4.2 StartY=0 StartZ=0 EndX=-4.2 EndY=-13.4877 EndZ=0
    g3: Circle CenterX=-4.2 CenterY=-13.4877 CenterZ=0 NormalX=0 NormalY=0 NormalZ=1 AngleXU=0 Radius=1
    g4: Circle CenterX=-4.2 CenterY=-26.5 CenterZ=0 NormalX=0 NormalY=0 NormalZ=1 AngleXU=0 Radius=1
    g5: Circle CenterX=-8.2 CenterY=-26.5 CenterZ=0 NormalX=0 NormalY=0 NormalZ=1 AngleXU=0 Radius=1
    g6: BSplineCurve PolesCount=3 KnotsCount=2 Degree=2 IsPeriodic=0
    g7: GeomPoint X=-4.2 Y=-13.4877 Z=0
    g8: GeomPoint X=-8.2 Y=-26.5 Z=0
    g9: LineSegment StartX=-14 StartY=-26.5 StartZ=0 EndX=-8.2 EndY=-26.5 EndZ=0
    g10: LineSegment StartX=-10.15 StartY=-12 StartZ=0 EndX=-10.15 EndY=-14 EndZ=0
    g11: LineSegment StartX=-12.8401 StartY=-16 StartZ=0 EndX=-10.1571 EndY=-16 EndZ=0
    g12: LineSegment StartX=-10.15 StartY=-14 StartZ=0 EndX=-8.70761 EndY=-14 EndZ=0
    g13: LineSegment StartX=-12.8401 StartY=-16 StartZ=0 EndX=-12.8401 EndY=-17.6958 EndZ=0
    g14: LineSegment StartX=-10.15 StartY=-12 StartZ=0 EndX=-7.79258 EndY=-12 EndZ=0
    g15: Circle CenterX=-6.2215 CenterY=-2 CenterZ=0 NormalX=0 NormalY=0 NormalZ=1 AngleXU=0 Radius=1
    g16: Circle CenterX=-6.22762 CenterY=-2.58724 CenterZ=0 NormalX=0 NormalY=0 NormalZ=1 AngleXU=0 Radius=1
    g17: Circle CenterX=-6.32538 CenterY=-4 CenterZ=0 NormalX=0 NormalY=0 NormalZ=1 AngleXU=0 Radius=1
    g18: BSplineCurve PolesCount=3 KnotsCount=2 Degree=2 IsPeriodic=0
    g19: GeomPoint X=-6.2215 Y=-2 Z=0
    g20: GeomPoint X=-6.32538 Y=-4 Z=0
    g21: Circle CenterX=-6.48644 CenterY=-5.99526 CenterZ=0 NormalX=0 NormalY=0 NormalZ=1 AngleXU=0 Radius=1
    g22: Circle CenterX=-6.58486 CenterY=-6.99526 CenterZ=0 NormalX=0 NormalY=0 NormalZ=1 AngleXU=0 Radius=1
    g23: Circle CenterX=-6.77343 CenterY=-8 CenterZ=0 NormalX=0 NormalY=0 NormalZ=1 AngleXU=0 Radius=1
    g24: BSplineCurve PolesCount=3 KnotsCount=2 Degree=2 IsPeriodic=0
    g25: GeomPoint X=-6.48644 Y=-5.99526 Z=0
    g26: GeomPoint X=-6.77343 Y=-8 Z=0
    g27: Circle CenterX=-7.19003 CenterY=-10 CenterZ=0 NormalX=0 NormalY=0 NormalZ=1 AngleXU=0 Radius=1
    g28: Circle CenterX=-7.44407 CenterY=-11.0915 CenterZ=0 NormalX=0 NormalY=0 NormalZ=1 AngleXU=0 Radius=1
    g29: Circle CenterX=-7.79258 CenterY=-12 CenterZ=0 NormalX=0 NormalY=0 NormalZ=1 AngleXU=0 Radius=1
    g30: BSplineCurve PolesCount=3 KnotsCount=2 Degree=2 IsPeriodic=0
    g31: GeomPoint X=-7.19003 Y=-10 Z=0
    g32: GeomPoint X=-7.79258 Y=-12 Z=0
    g33: Circle CenterX=-8.70761 CenterY=-14 CenterZ=0 NormalX=0 NormalY=0 NormalZ=1 AngleXU=0 Radius=1
    g34: Circle CenterX=-9.33087 CenterY=-15.1837 CenterZ=0 NormalX=0 NormalY=0 NormalZ=1 AngleXU=0 Radius=1
    g35: Circle CenterX=-10.1571 CenterY=-16 CenterZ=0 NormalX=0 NormalY=0 NormalZ=1 AngleXU=0 Radius=1
    g36: BSplineCurve PolesCount=3 KnotsCount=2 Degree=2 IsPeriodic=0
    g37: GeomPoint X=-8.70761 Y=-14 Z=0
    g38: GeomPoint X=-10.1571 Y=-16 Z=0
    g39: Circle CenterX=-12.8401 CenterY=-17.6958 CenterZ=0 NormalX=0 NormalY=0 NormalZ=1 AngleXU=0 Radius=1
    g40: Circle CenterX=-13.3521 CenterY=-17.9027 CenterZ=0 NormalX=0 NormalY=0 NormalZ=1 AngleXU=0 Radius=1
    g41: Circle CenterX=-14 CenterY=-18 CenterZ=0 NormalX=0 NormalY=0 NormalZ=1 AngleXU=0 Radius=1
    g42: BSplineCurve PolesCount=3 KnotsCount=2 Degree=2 IsPeriodic=0
    g43: GeomPoint X=-12.8401 Y=-17.6958 Z=0
    g44: GeomPoint X=-14 Y=-18 Z=0
    g45: LineSegment StartX=-6.2 StartY=0 StartZ=0 EndX=-7.2 EndY=0 EndZ=0
    g46: LineSegment StartX=-7.2 StartY=0 StartZ=0 EndX=-7.2 EndY=-2 EndZ=0
    g47: LineSegment StartX=-7.2 StartY=-2 StartZ=0 EndX=-6.2215 EndY=-2 EndZ=0
    g48: LineSegment StartX=-6.32538 StartY=-4 StartZ=0 EndX=-7.65538 EndY=-4 EndZ=0
    g49: LineSegment StartX=-7.65538 StartY=-4 StartZ=0 EndX=-7.65538 EndY=-5.99526 EndZ=0
    g50: LineSegment StartX=-7.65538 StartY=-5.99526 StartZ=0 EndX=-6.48644 EndY=-5.99526 EndZ=0
    g51: LineSegment StartX=-6.77343 StartY=-8 StartZ=0 EndX=-8.43343 EndY=-8 EndZ=0
    g52: LineSegment StartX=-8.43343 StartY=-8 StartZ=0 EndX=-8.43343 EndY=-10 EndZ=0
    g53: LineSegment StartX=-8.43343 StartY=-10 StartZ=0 EndX=-7.19003 EndY=-10 EndZ=0
  constraints (112):
    c: Horizontal(g0)
    c: Distance(g0) = 2
    c: Block(g0)
    c: Vertical(g1)
    c: Coincident(g2,g0)
    c: Vertical(g2)
    c: Block(g2)
    c: Coincident(g6,g2)
    c: Weight(g3) = 1
    c: Equal(g3,g4)
    c: Equal(g3,g5)
    c: InternalAlignment(g3,g6)
    c: InternalAlignment(g4,g6)
    c: InternalAlignment(g5,g6)
    c: InternalAlignment(g7,g6)
    c: InternalAlignment(g8,g6)
    c: Block(g6)
    c: Coincident(g9,g1)
    c: Coincident(g9,g6)
    c: Horizontal(g9)
    c: Vertical(g10)
    c: Block(g10)
    c: Horizontal(g11)
    c: Block(g11)
    c: Coincident(g12,g10)
    c: Horizontal(g12)
    c: Block(g12)
    c: Coincident(g13,g11)
    c: Vertical(g13)
    c: Block(g13)
    c: Coincident(g14,g10)
    c: Horizontal(g14)
    c: Block(g14)
    c: Block(g9)
    c: Block(g1)
    c: Weight(g15) = 1
    c: Equal(g15,g16)
    c: Equal(g15,g17)
    c: InternalAlignment(g15,g18)
    c: InternalAlignment(g16,g18)
    c: InternalAlignment(g17,g18)
    c: InternalAlignment(g19,g18)
    c: InternalAlignment(g20,g18)
    c: Weight(g21) = 1
    c: Equal(g21,g22)
    c: Equal(g21,g23)
    c: InternalAlignment(g21,g24)
    c: InternalAlignment(g22,g24)
    c: InternalAlignment(g23,g24)
    c: InternalAlignment(g25,g24)
    c: InternalAlignment(g26,g24)
    c: Weight(g27) = 1
    c: Equal(g27,g28)
    c: Equal(g27,g29)
    c: Coincident(g30,g14)
    c: InternalAlignment(g27,g30)
    c: InternalAlignment(g28,g30)
    c: InternalAlignment(g29,g30)
    c: InternalAlignment(g31,g30)
    c: InternalAlignment(g32,g30)
    c: Coincident(g36,g12)
    c: Weight(g33) = 1
    c: Equal(g33,g34)
    c: Equal(g33,g35)
    c: Coincident(g36,g11)
    c: InternalAlignment(g33,g36)
    c: InternalAlignment(g34,g36)
    c: InternalAlignment(g35,g36)
    c: InternalAlignment(g37,g36)
    c: InternalAlignment(g38,g36)
    c: Coincident(g42,g13)
    c: Weight(g39) = 1
    c: Equal(g39,g40)
    c: Equal(g39,g41)
    c: Coincident(g42,g1)
    c: InternalAlignment(g39,g42)
    c: InternalAlignment(g40,g42)
    c: InternalAlignment(g41,g42)
    c: InternalAlignment(g43,g42)
    c: InternalAlignment(g44,g42)
    c: Block(g18)
    c: Block(g24)
    c: Block(g30)
    c: Block(g36)
    c: Block(g42)
    c: Horizontal(g45)
    c: Coincident(g45,g0)
    c: Vertical(g46)
    c: Coincident(g46,g45)
    c: Coincident(g47,g46)
    c: Coincident(g47,g18)
    c: Horizontal(g47)
    c: Block(g46)
    c: Coincident(g48,g18)
    c: Horizontal(g48)
    c: Distance(g48) = 1.33
    c: Vertical(g49)
    c: Coincident(g49,g48)
    c: Coincident(g50,g49)
    c: Coincident(g50,g24)
    c: Horizontal(g50)
    c: Tangent(g50,g22)
    c: Horizontal(g51)
    c: Coincident(g51,g24)
    c: Block(g51)
    c: Vertical(g52)
    c: Block(g52)
    c: Coincident(g52,g51)
    c: Coincident(g53,g52)
    c: Coincident(g53,g30)
    c: Horizontal(g53)
    c: Distance(g1) = 8.5
FEATURE [Part::Feature] Face024
  shape: bbox 9.8 x 26.5 x 2e-07 mm, 1 faces, 0 solids (baked)
FEATURE [Part::Revolution] Revolve024
  Angle = 360
  Axis = (0,1,0)
  Base = (0,0,0)
  FaceMakerClass = Part::FaceMakerBullseye
  Placement = pos=(0,0,0) rot=(0,0,1;1.5708rad)
  Solid = false
  Source = -> Face024
  Symmetric = false
FEATURE [Part::Feature] Face025
  shape: bbox 9.8 x 26.5 x 2e-07 mm, 1 faces, 0 solids (baked)
FEATURE [Part::Revolution] Revolve025
  Angle = 360
  Axis = (0,1,0)
  Base = (0,0,0)
  FaceMakerClass = Part::FaceMakerBullseye
  Placement = pos=(0,0,0) rot=(0,0,1;1.5708rad)
  Solid = false
  Source = -> Face025
  Symmetric = false
FEATURE [Part::MultiFuse] Fusion033
  Placement = pos=(-18,19,36) rot=(0,0,1;0rad)
  Shapes = -> [Revolve025,Revolve024]
FEATURE [Part::Cylinder] Cylinder014
  Angle = 360
  AttacherType = Attacher::AttachEngine3D
  Height = 20
  Placement = pos=(0,0,36.15) rot=(0,0,1;0rad)
  Radius = 14.3
FEATURE [Part::Cylinder] Cylinder015
  Angle = 360
  AttacherType = Attacher::AttachEngine3D
  Height = 10
  Placement = pos=(0,0,36.15) rot=(0,0,1;0rad)
  Radius = 4
FEATURE [Part::MultiFuse] Fusion034  label="removeToCreteHoleForPlugHousing004"
  Placement = pos=(-42,19,36) rot=(0,1,0;1.5708rad)
  Shapes = -> [Cylinder014,Cylinder015]
FEATURE [Part::Cut] Cut008  label="top004"
  Base = -> Cut004
  Placement = pos=(-1,0,0) rot=(0,0,1;0rad)
  Tool = -> Fusion034
FEATURE [Part::Box] Box005  label="Cube005"
  AttacherType = Attacher::AttachEngine3D
  Height = 28
  Length = 3
  Placement = pos=(110.7,19,22) rot=(0,0,1;0rad)
  Width = 15.7
FEATURE [Part::Cylinder] Cylinder016
  Angle = 360
  AttacherType = Attacher::AttachEngine3D
  Height = 10
  Placement = pos=(0,0,36.15) rot=(0,0,1;0rad)
  Radius = 4
FEATURE [Part::Cylinder] Cylinder017
  Angle = 360
  AttacherType = Attacher::AttachEngine3D
  Height = 20
  Placement = pos=(0,0,36.15) rot=(0,0,1;0rad)
  Radius = 10.3
FEATURE [Part::MultiFuse] Fusion035  label="removeToCreteHoleForPlugHousing005"
  Placement = pos=(70,19,36) rot=(0,1,0;1.5708rad)
  Shapes = -> [Cylinder017,Cylinder016]
FEATURE [Part::Cut] Cut009  label="plugHousingTab001"
  Base = -> Box005
  Placement = pos=(-107.4,-14,0) rot=(0,0,1;0rad)
  Tool = -> Fusion035
FEATURE [Part::Box] Box006  label="Cube006"
  AttacherType = Attacher::AttachEngine3D
  Height = 28
  Length = 3
  Placement = pos=(110.7,19,22) rot=(0,0,1;0rad)
  Width = 15.7
FEATURE [Part::Cylinder] Cylinder018
  Angle = 360
  AttacherType = Attacher::AttachEngine3D
  Height = 10
  Placement = pos=(0,0,36.15) rot=(0,0,1;0rad)
  Radius = 4
FEATURE [Part::Cylinder] Cylinder019
  Angle = 360
  AttacherType = Attacher::AttachEngine3D
  Height = 20
  Placement = pos=(0,0,36.15) rot=(0,0,1;0rad)
  Radius = 10.3
FEATURE [Part::MultiFuse] Fusion036  label="removeToCreteHoleForPlugHousing006"
  Placement = pos=(70,19,36) rot=(0,1,0;1.5708rad)
  Shapes = -> [Cylinder019,Cylinder018]
FEATURE [Part::Cut] Cut010  label="plugHousingTab002"
  Base = -> Box006
  Placement = pos=(-107.4,-14,0) rot=(0,0,1;0rad)
  Tool = -> Fusion036
FEATURE [Part::MultiFuse] Fusion037
  Placement = pos=(9.6,23,0) rot=(0,0,1;3.14159rad)
  Shapes = -> [Cut009,Cut010]
FEATURE [Part::Box] Box  label="Cube"
  AttacherType = Attacher::AttachEngine3D
  Height = 10
  Length = 3
  Placement = pos=(3.3,4,12) rot=(0,0,1;0rad)
  Width = 10
FEATURE [Part::Fillet] Fillet004
  Base = -> Fusion028
  Edges = 1 edges r=2: [Edge25]
FEATURE [Part::Fillet] Fillet005  label="plugHousing046"
  Base = -> Fillet004
  Edges = 1 edges r=2: [Edge8]
FEATURE [Part::Fillet] Fillet006
  Base = -> Box
  Edges = 1 edges r=2: [Edge11]
FEATURE [Part::Box] Box007  label="Cube007"
  AttacherType = Attacher::AttachEngine3D
  Height = 10
  Length = 3
  Placement = pos=(3.3,4,50) rot=(0,0,1;0rad)
  Width = 10
FEATURE [Part::Fillet] Fillet007
  Base = -> Box007
  Edges = 1 edges r=2: [Edge12]
FEATURE [Part::Box] Box008  label="Cube008"
  AttacherType = Attacher::AttachEngine3D
  Height = 28
  Length = 4
  Placement = pos=(5,0,22) rot=(0,0,1;0rad)
  Width = 10
FEATURE [Part::Fillet] Fillet008
  Base = -> Box008
  Edges = 1 edges r=1: [Edge7]
FEATURE [Part::Fillet] Fillet009
  Base = -> Fillet008
  Edges = 1 edges r=2: [Edge5]
FEATURE [Part::Fillet] Fillet010
  Base = -> Fillet009
  Edges = 1 edges r=2: [Edge2]
FEATURE [Sketcher::SketchObject] Sketch009  label="topSketch003"
  FullyConstrained = true
  sketch-geometry (4):
    g0: LineSegment StartX=16.8446 StartY=31.512 StartZ=0 EndX=16.3251 EndY=34.4666 EndZ=0
    g1: ArcOfCircle CenterX=19 CenterY=19.2524 CenterZ=0 NormalX=0 NormalY=0 NormalZ=1 AngleXU=0 Radius=15.4476 StartAngle=1.74483 EndAngle=2.72717
    g2: ArcOfCircle CenterX=19 CenterY=19.2524 CenterZ=0 NormalX=0 NormalY=0 NormalZ=1 AngleXU=0 Radius=12.4476 StartAngle=1.74483 EndAngle=2.73189
    g3: LineSegment StartX=4.86004 StartY=25.4725 StartZ=0 EndX=7.58253 EndY=24.2107 EndZ=0
  constraints (7):
    c: Block(g0)
    c: Coincident(g1,g0)
    c: Coincident(g2,g0)
    c: Coincident(g3,g1)
    c: Coincident(g3,g2)
    c: Block(g1)
    c: Block(g2)
FEATURE [Part::Extrusion] Extrude008
  Base = -> Sketch009
  Dir = (0,0,1)
  DirMode = 2
  FaceMakerClass = Part::FaceMakerBullseye
  LengthFwd = 10
  LengthRev = 0
  Placement = pos=(0,0,31) rot=(0,0,1;0rad)
  Solid = true
  Symmetric = false
FEATURE [Part::Cylinder] Cylinder020
  Angle = 360
  AttacherType = Attacher::AttachEngine3D
  Height = 20
  Placement = pos=(0,0,36.15) rot=(0,0,1;0rad)
  Radius = 8.2
FEATURE [Part::Cylinder] Cylinder021
  Angle = 360
  AttacherType = Attacher::AttachEngine3D
  Height = 10
  Placement = pos=(0,0,36.15) rot=(0,0,1;0rad)
  Radius = 4
FEATURE [Part::MultiFuse] Fusion038  label="removeToCreteHoleForPlugHousing007"
  Placement = pos=(-42,19,36) rot=(0,1,0;1.5708rad)
  Shapes = -> [Cylinder020,Cylinder021]
FEATURE [Part::Cut] Cut011
  Base = -> Extrude008
  Tool = -> Fusion038
FEATURE [Part::Fillet] Fillet011
  Base = -> Cut011
  Edges = 1 edges r=2: [Edge1]
FEATURE [Part::Fillet] Fillet012
  Base = -> Fillet011
  Edges = 1 edges r=2.5: [Edge1]
FEATURE [Part::Fillet] Fillet013
  Base = -> Fillet012
  Edges = 1 edges r=2.5: [Edge2]
FEATURE [Part::Box] Box010  label="Cube010"
  AttacherType = Attacher::AttachEngine3D
  Height = 16
  Length = 8
  Placement = pos=(12.7,31.52,28) rot=(0,0,1;0rad)
  Width = 4
FEATURE [Sketcher::SketchObject] Sketch010  label="topSketch004"
  FullyConstrained = true
  sketch-geometry (4):
    g0: LineSegment StartX=16.8446 StartY=31.512 StartZ=0 EndX=16.3251 EndY=34.4666 EndZ=0
    g1: ArcOfCircle CenterX=19 CenterY=19.2524 CenterZ=0 NormalX=0 NormalY=0 NormalZ=1 AngleXU=0 Radius=15.4476 StartAngle=1.74483 EndAngle=2.72717
    g2: ArcOfCircle CenterX=19 CenterY=19.2524 CenterZ=0 NormalX=0 NormalY=0 NormalZ=1 AngleXU=0 Radius=12.4476 StartAngle=1.74483 EndAngle=2.73189
    g3: LineSegment StartX=4.86004 StartY=25.4725 StartZ=0 EndX=7.58253 EndY=24.2107 EndZ=0
  constraints (7):
    c: Block(g0)
    c: Coincident(g1,g0)
    c: Coincident(g2,g0)
    c: Coincident(g3,g1)
    c: Coincident(g3,g2)
    c: Block(g1)
    c: Block(g2)
FEATURE [Part::Cylinder] Cylinder022
  Angle = 360
  AttacherType = Attacher::AttachEngine3D
  Height = 10
  Placement = pos=(0,0,36.15) rot=(0,0,1;0rad)
  Radius = 4
FEATURE [Sketcher::SketchObject] Sketch011  label="topSketch005"
  FullyConstrained = true
  sketch-geometry (4):
    g0: LineSegment StartX=16.8446 StartY=31.512 StartZ=0 EndX=16.3251 EndY=34.4666 EndZ=0
    g1: ArcOfCircle CenterX=19 CenterY=19.2524 CenterZ=0 NormalX=0 NormalY=0 NormalZ=1 AngleXU=0 Radius=15.4476 StartAngle=1.74483 EndAngle=2.72717
    g2: ArcOfCircle CenterX=19 CenterY=19.2524 CenterZ=0 NormalX=0 NormalY=0 NormalZ=1 AngleXU=0 Radius=12.4476 StartAngle=1.74483 EndAngle=2.73189
    g3: LineSegment StartX=4.86004 StartY=25.4725 StartZ=0 EndX=7.58253 EndY=24.2107 EndZ=0
  constraints (7):
    c: Block(g0)
    c: Coincident(g1,g0)
    c: Coincident(g2,g0)
    c: Coincident(g3,g1)
    c: Coincident(g3,g2)
    c: Block(g1)
    c: Block(g2)
FEATURE [Part::Extrusion] Extrude010
  Base = -> Sketch011
  Dir = (0,0,1)
  DirMode = 2
  FaceMakerClass = Part::FaceMakerBullseye
  LengthFwd = 10.6
  LengthRev = 0
  Placement = pos=(0,0,31) rot=(0,0,1;0rad)
  Solid = true
  Symmetric = false
FEATURE [Part::Cylinder] Cylinder023
  Angle = 360
  AttacherType = Attacher::AttachEngine3D
  Height = 20
  Placement = pos=(0,0,36.15) rot=(0,0,1;0rad)
  Radius = 8.2
FEATURE [Part::MultiFuse] Fusion039  label="removeToCreteHoleForPlugHousing008"
  Placement = pos=(-42,19,36) rot=(0,1,0;1.5708rad)
  Shapes = -> [Cylinder023,Cylinder022]
FEATURE [Part::Cut] Cut012
  Base = -> Extrude010
  Placement = pos=(0,0,-0.3) rot=(0,0,1;0rad)
  Tool = -> Fusion039
FEATURE [Part::Cut] Cut013
  Base = -> Box010
  Tool = -> Cut012
FEATURE [Part::Fillet] Fillet014
  Base = -> Cut013
  Edges = 1 edges r=0.7: [Edge13]
FEATURE [Part::Fillet] Fillet015
  Base = -> Fillet014
  Edges = 1 edges r=0.7: [Edge13]
FEATURE [Part::Fillet] Fillet016
  Base = -> Fillet015
  Edges = 1 edges r=0.7: [Edge16]
FEATURE [Part::Fillet] Fillet017
  Base = -> Fillet016
  Edges = 1 edges r=0.7: [Edge11]
FEATURE [Part::Fillet] Fillet018
  Base = -> Fillet017
  Edges = 1 edges r=0.7: [Edge10]
FEATURE [Part::Fillet] Fillet019
  Base = -> Fillet018
  Edges = 1 edges r=1.2: [Edge5]
FEATURE [Part::Fillet] Fillet020
  Base = -> Fillet019
  Edges = 1 edges r=1.2: [Edge12]
FEATURE [Part::Fillet] Fillet021
  Base = -> Fillet020
  Edges = 1 edges r=2: [Edge1]
  Placement = pos=(0.3,0,0) rot=(0,0,1;0rad)
FEATURE [Part::MultiFuse] Fusion040  label="top005"
  Shapes = -> [Cut008,Fillet021]
FEATURE [Part::MultiFuse] Fusion041  label="wireHolder"
  Shapes = -> [Fusion033,Fillet013]
FEATURE [Part::MultiFuse] Fusion042
  Shapes = -> [Fillet007,Fusion041]
FEATURE [Part::MultiFuse] Fusion043  label="wireHolder001"
  Shapes = -> [Fusion042,Fillet010]
FEATURE [Part::MultiFuse] Fusion044  label="wireHolder002"
  Shapes = -> [Fillet006,Fusion037,Fusion043]
FEATURE [Part::Feature] Face026
  shape: bbox 11 x 6 x 2e-07 mm, 1 faces, 0 solids (baked)
FEATURE [Part::Revolution] Revolve026
  Angle = 360
  Axis = (0,1,0)
  Base = (0,0,0)
  FaceMakerClass = Part::FaceMakerBullseye
  Placement = pos=(30.3,-1,19.7) rot=(0,0,1;0rad)
  Solid = false
  Source = -> Face026
  Symmetric = false
FEATURE [Sketcher::SketchObject] Sketch013  label="topSketch006"
  FullyConstrained = true
  sketch-geometry (13):
    g0: LineSegment StartX=117 StartY=19 StartZ=0 EndX=117 EndY=38 EndZ=0
    g1: ArcOfCircle CenterX=98 CenterY=19 CenterZ=0 NormalX=0 NormalY=0 NormalZ=1 AngleXU=0 Radius=19 StartAngle=5.7297 EndAngle=6.28319
    g2: LineSegment StartX=0 StartY=3 StartZ=0 EndX=0 EndY=19 EndZ=0
    g3: LineSegment StartX=19 StartY=38 StartZ=0 EndX=117 EndY=38 EndZ=0
    g4: ArcOfCircle CenterX=19 CenterY=19 CenterZ=0 NormalX=0 NormalY=0 NormalZ=1 AngleXU=0 Radius=19 StartAngle=1.5708 EndAngle=3.14159
    g5: ArcOfCircle CenterX=19 CenterY=19 CenterZ=0 NormalX=0 NormalY=0 NormalZ=1 AngleXU=0 Radius=16 StartAngle=1.5708 EndAngle=3.14159
    g6: ArcOfCircle CenterX=98 CenterY=19 CenterZ=0 NormalX=0 NormalY=0 NormalZ=1 AngleXU=0 Radius=16 StartAngle=5.60905 EndAngle=6.28319
    g7: LineSegment StartX=114 StartY=19 StartZ=0 EndX=114 EndY=35 EndZ=0
    g8: LineSegment StartX=110.5 StartY=9.01251 StartZ=0 EndX=114.163 EndY=9.01251 EndZ=0
    g9: LineSegment StartX=114 StartY=35 StartZ=0 EndX=19 EndY=35 EndZ=0
    g10: LineSegment StartX=0 StartY=3 StartZ=0 EndX=0 EndY=0 EndZ=0
    g11: LineSegment StartX=3 StartY=0 StartZ=0 EndX=0 EndY=0 EndZ=0
    g12: LineSegment StartX=3 StartY=19 StartZ=0 EndX=3 EndY=0 EndZ=0
  constraints (33):
    c: Vertical(g0)
    c: Distance(g0) = 19
    c: Block(g0)
    c: Coincident(g1,g0)
    c: Block(g1)
    c: Vertical(g2)
    c: Block(g2)
    c: Coincident(g3,g0)
    c: Horizontal(g3)
    c: Distance(g3) = 98
    c: Coincident(g4,g3)
    c: Coincident(g4,g2)
    c: Block(g4)
    c: Coincident(g5,g4)
    c: Coincident(g6,g1)
    c: Block(g6)
    c: Block(g5)
    c: Coincident(g7,g6)
    c: Vertical(g7)
    c: Coincident(g8,g6)
    c: Coincident(g8,g1)
    c: Coincident(g9,g7)
    c: Coincident(g9,g5)
    c: Horizontal(g9)
    c: Tangent(g9,g5)
    c: Coincident(g10,g2)
    c: Distance(g10) = 3
    c: Vertical(g10)
    c: Coincident(g11,g10)
    c: Horizontal(g11)
    c: Coincident(g12,g5)
    c: Coincident(g12,g11)
    c: Vertical(g12)
FEATURE [Part::Extrusion] Extrude011  label="top006"
  Base = -> Sketch013
  Dir = (0,0,1)
  DirMode = 2
  FaceMakerClass = Part::FaceMakerBullseye
  LengthFwd = 72
  LengthRev = 0
  Solid = true
  Symmetric = false
FEATURE [Sketcher::SketchObject] Sketch014
  FullyConstrained = true
  MapMode = 3
  Placement = pos=(0,0,0) rot=(1,0,0;1.5708rad)
  Support = -> [Extrude011]
  sketch-geometry (8):
    g0: Circle CenterX=80.351 CenterY=-67.6202 CenterZ=0 NormalX=0 NormalY=0 NormalZ=1 AngleXU=0 Radius=2
    g1: Circle CenterX=80.351 CenterY=-67.6202 CenterZ=0 NormalX=0 NormalY=0 NormalZ=1 AngleXU=0 Radius=3
    g2: Circle CenterX=80.351 CenterY=-4.92017 CenterZ=0 NormalX=0 NormalY=0 NormalZ=1 AngleXU=0 Radius=2
    g3: Circle CenterX=80.351 CenterY=-4.92017 CenterZ=0 NormalX=0 NormalY=0 NormalZ=1 AngleXU=0 Radius=3
    g4: Circle CenterX=23.851 CenterY=-4.92017 CenterZ=0 NormalX=0 NormalY=0 NormalZ=1 AngleXU=0 Radius=2
    g5: Circle CenterX=23.851 CenterY=-4.92017 CenterZ=0 NormalX=0 NormalY=0 NormalZ=1 AngleXU=0 Radius=3
    g6: Circle CenterX=23.851 CenterY=-67.6202 CenterZ=0 NormalX=0 NormalY=0 NormalZ=1 AngleXU=0 Radius=2
    g7: Circle CenterX=23.851 CenterY=-67.6202 CenterZ=0 NormalX=0 NormalY=0 NormalZ=1 AngleXU=0 Radius=3
  constraints (8):
    c: Block(g3)
    c: Block(g2)
    c: Block(g1)
    c: Block(g0)
    c: Block(g6)
    c: Block(g7)
    c: Block(g4)
    c: Block(g5)
FEATURE [Part::Feature] Face027
  shape: bbox 11 x 6 x 2e-07 mm, 1 faces, 0 solids (baked)
FEATURE [Part::Revolution] Revolve027
  Angle = 360
  Axis = (0,1,0)
  Base = (0,0,0)
  FaceMakerClass = Part::FaceMakerBullseye
  Placement = pos=(30.3,-1,51.7) rot=(0,0,1;0rad)
  Solid = false
  Source = -> Face027
  Symmetric = false
FEATURE [Part::Feature] Face028
  shape: bbox 11 x 6 x 2e-07 mm, 1 faces, 0 solids (baked)
FEATURE [Part::Revolution] Revolve028
  Angle = 360
  Axis = (0,1,0)
  Base = (0,0,0)
  FaceMakerClass = Part::FaceMakerBullseye
  Placement = pos=(62.3,-1,19.7) rot=(0,0,1;0rad)
  Solid = false
  Source = -> Face028
  Symmetric = false
FEATURE [Part::Feature] Face029
  shape: bbox 11 x 6 x 2e-07 mm, 1 faces, 0 solids (baked)
FEATURE [Part::Revolution] Revolve029
  Angle = 360
  Axis = (0,1,0)
  Base = (0,0,0)
  FaceMakerClass = Part::FaceMakerBullseye
  Placement = pos=(62.3,-1,51.7) rot=(0,0,1;0rad)
  Solid = false
  Source = -> Face029
  Symmetric = false
FEATURE [Part::Feature] Wire
  shape: bbox 11 x 5.2 x 2e-07 mm, 0 faces, 0 solids (baked)
FEATURE [Part::Revolution] Revolve030
  Angle = 360
  Axis = (0,1,0)
  Base = (0,0,0)
  FaceMakerClass = Part::FaceMakerBullseye
  Placement = pos=(30.3,38,19.7) rot=(0,0,1;0rad)
  Solid = true
  Source = -> Wire
  Symmetric = false
FEATURE [Part::Feature] Wire001
  shape: bbox 11 x 5.2 x 2e-07 mm, 0 faces, 0 solids (baked)
FEATURE [Part::Revolution] Revolve031
  Angle = 360
  Axis = (0,1,0)
  Base = (0,0,0)
  FaceMakerClass = Part::FaceMakerBullseye
  Placement = pos=(30.3,38,51.7) rot=(0,0,1;0rad)
  Solid = true
  Source = -> Wire001
  Symmetric = false
FEATURE [Part::Feature] Wire002
  shape: bbox 11 x 5.2 x 2e-07 mm, 0 faces, 0 solids (baked)
FEATURE [Part::Revolution] Revolve032
  Angle = 360
  Axis = (0,1,0)
  Base = (0,0,0)
  FaceMakerClass = Part::FaceMakerBullseye
  Placement = pos=(62.3,38,51.7) rot=(0,0,1;0rad)
  Solid = true
  Source = -> Wire002
  Symmetric = false
FEATURE [Part::Feature] Wire003
  shape: bbox 11 x 5.2 x 2e-07 mm, 0 faces, 0 solids (baked)
FEATURE [Part::Revolution] Revolve033
  Angle = 360
  Axis = (0,1,0)
  Base = (0,0,0)
  FaceMakerClass = Part::FaceMakerBullseye
  Placement = pos=(62.3,38,19.7) rot=(0,0,1;0rad)
  Solid = true
  Source = -> Wire003
  Symmetric = false
FEATURE [Part::MultiFuse] Fusion045  label="altRandScrewHousing"
  Shapes = -> [Revolve029,Revolve027,Revolve028,Revolve026]
FEATURE [Part::MultiFuse] Fusion046  label="fanScrewHousing"
  Shapes = -> [Revolve033,Revolve032,Revolve031,Revolve030]
FEATURE [Sketcher::SketchObject] Sketch015
  FullyConstrained = true
  sketch-geometry (17):
    g0: Circle CenterX=-3.5 CenterY=23.5 CenterZ=0 NormalX=0 NormalY=0 NormalZ=1 AngleXU=0 Radius=1
    g1: Circle CenterX=-1 CenterY=15.25 CenterZ=0 NormalX=0 NormalY=0 NormalZ=1 AngleXU=0 Radius=1
    g2: Circle CenterX=-3.5 CenterY=7 CenterZ=0 NormalX=0 NormalY=0 NormalZ=1 AngleXU=0 Radius=1
    g3: BSplineCurve PolesCount=3 KnotsCount=2 Degree=2 IsPeriodic=0
    g4: GeomPoint X=-3.5 Y=23.5 Z=0
    g5: GeomPoint X=-3.5 Y=7 Z=0
    g6: Circle CenterX=-4.8 CenterY=30.5 CenterZ=0 NormalX=0 NormalY=0 NormalZ=1 AngleXU=0 Radius=1
    g7: Circle CenterX=-3.5 CenterY=30.5 CenterZ=0 NormalX=0 NormalY=0 NormalZ=1 AngleXU=0 Radius=1
    g8: Circle CenterX=-3.5 CenterY=29.2 CenterZ=0 NormalX=0 NormalY=0 NormalZ=1 AngleXU=0 Radius=1
    g9: BSplineCurve PolesCount=3 KnotsCount=2 Degree=2 IsPeriodic=0
    g10: GeomPoint X=-4.8 Y=30.5 Z=0
    g11: GeomPoint X=-3.5 Y=29.2 Z=0
    g12: LineSegment StartX=-3.5 StartY=29.2 StartZ=0 EndX=-3.5 EndY=23.5 EndZ=0
    g13: LineSegment StartX=-4.8 StartY=30.5 StartZ=0 EndX=0 EndY=30.5 EndZ=0
    g14: LineSegment StartX=-3.5 StartY=0.3 StartZ=0 EndX=0 EndY=0.3 EndZ=0
    g15: LineSegment StartX=-3.5 StartY=0.3 StartZ=0 EndX=-3.5 EndY=7 EndZ=0
    g16: LineSegment StartX=0 StartY=0.3 StartZ=0 EndX=0 EndY=30.5 EndZ=0
  constraints (33):
    c: Weight(g0) = 1
    c: Equal(g0,g1)
    c: Equal(g0,g2)
    c: InternalAlignment(g0,g3)
    c: InternalAlignment(g1,g3)
    c: InternalAlignment(g2,g3)
    c: InternalAlignment(g4,g3)
    c: InternalAlignment(g5,g3)
    c: Block(g3)
    c: Weight(g6) = 1
    c: Equal(g6,g7)
    c: Equal(g6,g8)
    c: InternalAlignment(g6,g9)
    c: InternalAlignment(g7,g9)
    c: InternalAlignment(g8,g9)
    c: InternalAlignment(g10,g9)
    c: InternalAlignment(g11,g9)
    c: Block(g9)
    c: Coincident(g12,g9)
    c: Coincident(g12,g3)
    c: Vertical(g12)
    c: Coincident(g13,g9)
    c: Horizontal(g13)
    c: Distance(g13) = 4.8
    c: Horizontal(g14)
    c: Block(g14)
    c: Coincident(g15,g14)
    c: Coincident(g15,g3)
    c: Vertical(g15)
    c: Coincident(g16,g14)
    c: Coincident(g16,g13)
    c: Vertical(g16)
    c: Tangent(g16,g1)
FEATURE [Sketcher::SketchObject] Sketch016
  FullyConstrained = true
  sketch-geometry (16):
    g0: Circle CenterX=-3.5 CenterY=23.5 CenterZ=0 NormalX=0 NormalY=0 NormalZ=1 AngleXU=0 Radius=1
    g1: Circle CenterX=-1 CenterY=15.25 CenterZ=0 NormalX=0 NormalY=0 NormalZ=1 AngleXU=0 Radius=1
    g2: Circle CenterX=-3.5 CenterY=7 CenterZ=0 NormalX=0 NormalY=0 NormalZ=1 AngleXU=0 Radius=1
    g3: BSplineCurve PolesCount=3 KnotsCount=2 Degree=2 IsPeriodic=0
    g4: GeomPoint X=-3.5 Y=23.5 Z=0
    g5: GeomPoint X=-3.5 Y=7 Z=0
    g6: LineSegment StartX=-3.5 StartY=28.2 StartZ=0 EndX=-3.5 EndY=23.5 EndZ=0
    g7: LineSegment StartX=0 StartY=29.5 StartZ=0 EndX=0 EndY=30 EndZ=0
    g8: LineSegment StartX=-3.5 StartY=28.2 StartZ=0 EndX=-3.5 EndY=30 EndZ=0
    g9: LineSegment StartX=0 StartY=30 StartZ=0 EndX=0 EndY=30.5 EndZ=0
    g10: LineSegment StartX=0 StartY=30.5 StartZ=0 EndX=-3.5 EndY=30.5 EndZ=0
    g11: LineSegment StartX=-3.5 StartY=30.5 StartZ=0 EndX=-3.5 EndY=30 EndZ=0
    g12: LineSegment StartX=0 StartY=29.5 StartZ=0 EndX=0 EndY=5 EndZ=0
    g13: LineSegment StartX=-3.5 StartY=0.3 StartZ=0 EndX=-3.5 EndY=7 EndZ=0
    g14: LineSegment StartX=-3.5 StartY=0.3 StartZ=0 EndX=0 EndY=0.3 EndZ=0
    g15: LineSegment StartX=0 StartY=5 StartZ=0 EndX=0 EndY=0.3 EndZ=0
  constraints (39):
    c: Weight(g0) = 1
    c: Equal(g0,g1)
    c: Equal(g0,g2)
    c: InternalAlignment(g0,g3)
    c: InternalAlignment(g1,g3)
    c: InternalAlignment(g2,g3)
    c: InternalAlignment(g4,g3)
    c: InternalAlignment(g5,g3)
    c: Block(g3)
    c: Coincident(g6,g3)
    c: Vertical(g6)
    c: Vertical(g7)
    c: Distance(g7) = 0.5
    c: Coincident(g8,g6)
    c: Vertical(g8)
    c: Block(g6)
    c: Block(g7)
    c: Vertical(g9)
    c: Equal(g7,g9) = 0.5
    c: Block(g9)
    c: Coincident(g9,g7)
    c: Horizontal(g10)
    c: Coincident(g10,g9)
    c: Coincident(g11,g10)
    c: Coincident(g11,g8)
    c: Vertical(g11)
    c: Block(g11)
    c: Coincident(g12,g7)
    c: Vertical(g12)
    c: Coincident(g13,g3)
    c: Vertical(g13)
    c: Distance(g13) = 6.7
    c: Coincident(g14,g13)
    c: Horizontal(g14)
    c: Block(g14)
    c: Coincident(g15,g12)
    c: Coincident(g15,g14)
    c: Vertical(g15)
    c: Block(g15)
FEATURE [Sketcher::SketchObject] Sketch017
  FullyConstrained = true
  sketch-geometry (11):
    g0: LineSegment StartX=-3.5 StartY=1e-16 StartZ=0 EndX=-1.6 EndY=1e-16 EndZ=0
    g1: LineSegment StartX=-1.6 StartY=1e-16 StartZ=0 EndX=-1.6 EndY=1.5 EndZ=0
    g2: LineSegment StartX=-3.5 StartY=1.5 StartZ=0 EndX=-1.6 EndY=1.5 EndZ=0
    g3: LineSegment StartX=-3.5 StartY=1e-16 StartZ=0 EndX=-4.8 EndY=1e-16 EndZ=0
    g4: Circle CenterX=-3.5 CenterY=1.3 CenterZ=0 NormalX=0 NormalY=0 NormalZ=1 AngleXU=0 Radius=1
    g5: Circle CenterX=-3.5 CenterY=1e-16 CenterZ=0 NormalX=0 NormalY=0 NormalZ=1 AngleXU=0 Radius=1
    g6: Circle CenterX=-4.8 CenterY=1e-16 CenterZ=0 NormalX=0 NormalY=0 NormalZ=1 AngleXU=0 Radius=1
    g7: BSplineCurve PolesCount=3 KnotsCount=2 Degree=2 IsPeriodic=0
    g8: GeomPoint X=-3.5 Y=1.3 Z=0
    g9: GeomPoint X=-4.8 Y=1e-16 Z=0
    g10: LineSegment StartX=-3.5 StartY=1.3 StartZ=0 EndX=-3.5 EndY=1.5 EndZ=0
  constraints (24):
    c: Horizontal(g0)
    c: Distance(g0) = 1.9
    c: Block(g0)
    c: Coincident(g1,g0)
    c: Vertical(g1)
    c: Coincident(g2,g1)
    c: Horizontal(g2)
    c: Coincident(g3,g0)
    c: Horizontal(g3)
    c: Distance(g3) = 1.3
    c: Weight(g4) = 1
    c: Equal(g4,g5)
    c: Coincident(g5,g0)
    c: Equal(g4,g6)
    c: Coincident(g7,g3)
    c: InternalAlignment(g4,g7)
    c: InternalAlignment(g5,g7)
    c: InternalAlignment(g6,g7)
    c: InternalAlignment(g8,g7)
    c: InternalAlignment(g9,g7)
    c: Coincident(g10,g7)
    c: Coincident(g10,g2)
    c: Vertical(g10)
    c: Block(g10)
FEATURE [Part::Feature] Face035
  shape: bbox 3.2 x 1.5 x 2e-07 mm, 1 faces, 0 solids (baked)
FEATURE [Part::Revolution] Revolve039  label="backCaseScrewRetainer"
  Angle = 360
  Axis = (0,1,0)
  Base = (0,0,0)
  FaceMakerClass = Part::FaceMakerBullseye
  Placement = pos=(12.5,3,62) rot=(0,0,1;0rad)
  Solid = false
  Source = -> Face035
  Symmetric = false
FEATURE [Part::Feature] Face036
  shape: bbox 3.2 x 1.5 x 2e-07 mm, 1 faces, 0 solids (baked)
FEATURE [Part::Feature] Face039
  shape: bbox 4.8 x 30.2 x 2e-07 mm, 1 faces, 0 solids (baked)
FEATURE [Part::Revolution] Revolve043  label="frontCaseScrewPost002"
  Angle = 360
  Axis = (0,1,0)
  Base = (0,0,0)
  FaceMakerClass = Part::FaceMakerBullseye
  Placement = pos=(89.5,4.5,3.5) rot=(0,0,1;0rad)
  Solid = false
  Source = -> Face039
  Symmetric = false
FEATURE [Part::Feature] Face042
  shape: bbox 4.8 x 30.2 x 2e-07 mm, 1 faces, 0 solids (baked)
FEATURE [Part::Revolution] Revolve046  label="frontCaseScrewPost003"
  Angle = 360
  Axis = (0,1,0)
  Base = (0,0,0)
  FaceMakerClass = Part::FaceMakerBullseye
  Placement = pos=(89.5,4.5,68.5) rot=(0,0,1;0rad)
  Solid = false
  Source = -> Face042
  Symmetric = false
FEATURE [Part::Feature] Face043
  shape: bbox 3.2 x 1.5 x 2e-07 mm, 1 faces, 0 solids (baked)
FEATURE [Part::Revolution] Revolve047  label="frontCaseScrewRetainer002"
  Angle = 360
  Axis = (0,1,0)
  Base = (0,0,0)
  FaceMakerClass = Part::FaceMakerBullseye
  Placement = pos=(89.5,3,68.5) rot=(0,0,1;0rad)
  Solid = false
  Source = -> Face043
  Symmetric = false
FEATURE [Part::Feature] Face044
  shape: bbox 3.2 x 1.5 x 2e-07 mm, 1 faces, 0 solids (baked)
FEATURE [Part::Revolution] Revolve048  label="frontCaseScrewRetainer003"
  Angle = 360
  Axis = (0,1,0)
  Base = (0,0,0)
  FaceMakerClass = Part::FaceMakerBullseye
  Placement = pos=(89.5,3,3.5) rot=(0,0,1;0rad)
  Solid = false
  Source = -> Face044
  Symmetric = false
FEATURE [App::MeasureDistance] Distance002  label="Distance: 1.67 mm"
  Distance = 1.66921
  P1 = (99.2361,4.7524,71.7)
  P2 = (99.2347,6.42161,71.7)
FEATURE [Sketcher::SketchObject] Sketch018
  FullyConstrained = true
  sketch-geometry (7):
    g0: LineSegment StartX=0 StartY=0 StartZ=0 EndX=0 EndY=6 EndZ=0
    g1: Circle CenterX=0 CenterY=0 CenterZ=0 NormalX=0 NormalY=0 NormalZ=1 AngleXU=0 Radius=1
    g2: Circle CenterX=8 CenterY=6 CenterZ=0 NormalX=0 NormalY=0 NormalZ=1 AngleXU=0 Radius=1
    g3: BSplineCurve PolesCount=3 KnotsCount=2 Degree=2 IsPeriodic=0
    g4: GeomPoint X=0 Y=0 Z=0
    g5: GeomPoint X=8 Y=6 Z=0
    g6: LineSegment StartX=0 StartY=6 StartZ=0 EndX=8 EndY=6 EndZ=0
  constraints (14):
    c: Coincident(g0,g-1)
    c: Distance(g0) = 6
    c: Vertical(g0)
    c: Coincident(g3,g0)
    c: Weight(g1) = 1
    c: Equal(g1,g2)
    c: InternalAlignment(g1,g3)
    c: InternalAlignment(g2,g3)
    c: InternalAlignment(g4,g3)
    c: InternalAlignment(g5,g3)
    c: Block(g3)
    c: Coincident(g6,g0)
    c: Coincident(g6,g3)
    c: Horizontal(g6)
FEATURE [Part::Extrusion] Extrude012  label="caseScrewPillarBracket"
  Base = -> Sketch018
  Dir = (0,0,1)
  DirMode = 2
  FaceMakerClass = Part::FaceMakerBullseye
  LengthFwd = 2.4
  LengthRev = 0
  Placement = pos=(15.76,29,8.8) rot=(0,1,0;0rad)
  Solid = true
  Symmetric = false
FEATURE [Sketcher::SketchObject] Sketch019
  FullyConstrained = true
  sketch-geometry (7):
    g0: LineSegment StartX=0 StartY=0 StartZ=0 EndX=0 EndY=6 EndZ=0
    g1: Circle CenterX=0 CenterY=0 CenterZ=0 NormalX=0 NormalY=0 NormalZ=1 AngleXU=0 Radius=1
    g2: Circle CenterX=8 CenterY=6 CenterZ=0 NormalX=0 NormalY=0 NormalZ=1 AngleXU=0 Radius=1
    g3: BSplineCurve PolesCount=3 KnotsCount=2 Degree=2 IsPeriodic=0
    g4: GeomPoint X=0 Y=0 Z=0
    g5: GeomPoint X=8 Y=6 Z=0
    g6: LineSegment StartX=0 StartY=6 StartZ=0 EndX=8 EndY=6 EndZ=0
  constraints (14):
    c: Coincident(g0,g-1)
    c: Distance(g0) = 6
    c: Vertical(g0)
    c: Coincident(g3,g0)
    c: Weight(g1) = 1
    c: Equal(g1,g2)
    c: InternalAlignment(g1,g3)
    c: InternalAlignment(g2,g3)
    c: InternalAlignment(g4,g3)
    c: InternalAlignment(g5,g3)
    c: Block(g3)
    c: Coincident(g6,g0)
    c: Coincident(g6,g3)
    c: Horizontal(g6)
FEATURE [Part::Extrusion] Extrude013  label="caseScrewPillarBracket001"
  Base = -> Sketch019
  Dir = (0,0,1)
  DirMode = 2
  FaceMakerClass = Part::FaceMakerBullseye
  LengthFwd = 2.4
  LengthRev = 0
  Placement = pos=(15.76,29,60.8) rot=(0,0,1;0rad)
  Solid = true
  Symmetric = false
FEATURE [Sketcher::SketchObject] Sketch020
  FullyConstrained = true
  sketch-geometry (7):
    g0: LineSegment StartX=0 StartY=0 StartZ=0 EndX=0 EndY=6 EndZ=0
    g1: Circle CenterX=0 CenterY=0 CenterZ=0 NormalX=0 NormalY=0 NormalZ=1 AngleXU=0 Radius=1
    g2: Circle CenterX=8 CenterY=6 CenterZ=0 NormalX=0 NormalY=0 NormalZ=1 AngleXU=0 Radius=1
    g3: BSplineCurve PolesCount=3 KnotsCount=2 Degree=2 IsPeriodic=0
    g4: GeomPoint X=0 Y=0 Z=0
    g5: GeomPoint X=8 Y=6 Z=0
    g6: LineSegment StartX=0 StartY=6 StartZ=0 EndX=8 EndY=6 EndZ=0
  constraints (14):
    c: Coincident(g0,g-1)
    c: Distance(g0) = 6
    c: Vertical(g0)
    c: Coincident(g3,g0)
    c: Weight(g1) = 1
    c: Equal(g1,g2)
    c: InternalAlignment(g1,g3)
    c: InternalAlignment(g2,g3)
    c: InternalAlignment(g4,g3)
    c: InternalAlignment(g5,g3)
    c: Block(g3)
    c: Coincident(g6,g0)
    c: Coincident(g6,g3)
    c: Horizontal(g6)
FEATURE [Part::Extrusion] Extrude014  label="caseScrewPillarBracket002"
  Base = -> Sketch020
  Dir = (0,0,1)
  DirMode = 2
  FaceMakerClass = Part::FaceMakerBullseye
  LengthFwd = 2.4
  LengthRev = 0
  Placement = pos=(13.7,29,13.26) rot=(0,-1,0;1.5708rad)
  Solid = true
  Symmetric = false
FEATURE [Sketcher::SketchObject] Sketch021
  FullyConstrained = true
  sketch-geometry (7):
    g0: LineSegment StartX=0 StartY=0 StartZ=0 EndX=0 EndY=6 EndZ=0
    g1: Circle CenterX=0 CenterY=0 CenterZ=0 NormalX=0 NormalY=0 NormalZ=1 AngleXU=0 Radius=1
    g2: Circle CenterX=8 CenterY=6 CenterZ=0 NormalX=0 NormalY=0 NormalZ=1 AngleXU=0 Radius=1
    g3: BSplineCurve PolesCount=3 KnotsCount=2 Degree=2 IsPeriodic=0
    g4: GeomPoint X=0 Y=0 Z=0
    g5: GeomPoint X=8 Y=6 Z=0
    g6: LineSegment StartX=0 StartY=6 StartZ=0 EndX=8 EndY=6 EndZ=0
  constraints (14):
    c: Coincident(g0,g-1)
    c: Distance(g0) = 6
    c: Vertical(g0)
    c: Coincident(g3,g0)
    c: Weight(g1) = 1
    c: Equal(g1,g2)
    c: InternalAlignment(g1,g3)
    c: InternalAlignment(g2,g3)
    c: InternalAlignment(g4,g3)
    c: InternalAlignment(g5,g3)
    c: Block(g3)
    c: Coincident(g6,g0)
    c: Coincident(g6,g3)
    c: Horizontal(g6)
FEATURE [Part::Extrusion] Extrude015  label="caseScrewPillarBracket003"
  Base = -> Sketch021
  Dir = (0,0,1)
  DirMode = 2
  FaceMakerClass = Part::FaceMakerBullseye
  LengthFwd = 2.4
  LengthRev = 0
  Placement = pos=(11.3,29,58.74) rot=(0,1,0;1.5708rad)
  Solid = true
  Symmetric = false
FEATURE [Sketcher::SketchObject] Sketch022
  FullyConstrained = true
  sketch-geometry (7):
    g0: LineSegment StartX=0 StartY=0 StartZ=0 EndX=0 EndY=6 EndZ=0
    g1: Circle CenterX=0 CenterY=0 CenterZ=0 NormalX=0 NormalY=0 NormalZ=1 AngleXU=0 Radius=1
    g2: Circle CenterX=8 CenterY=6 CenterZ=0 NormalX=0 NormalY=0 NormalZ=1 AngleXU=0 Radius=1
    g3: BSplineCurve PolesCount=3 KnotsCount=2 Degree=2 IsPeriodic=0
    g4: GeomPoint X=0 Y=0 Z=0
    g5: GeomPoint X=8 Y=6 Z=0
    g6: LineSegment StartX=0 StartY=6 StartZ=0 EndX=8 EndY=6 EndZ=0
  constraints (14):
    c: Coincident(g0,g-1)
    c: Distance(g0) = 6
    c: Vertical(g0)
    c: Coincident(g3,g0)
    c: Weight(g1) = 1
    c: Equal(g1,g2)
    c: InternalAlignment(g1,g3)
    c: InternalAlignment(g2,g3)
    c: InternalAlignment(g4,g3)
    c: InternalAlignment(g5,g3)
    c: Block(g3)
    c: Coincident(g6,g0)
    c: Coincident(g6,g3)
    c: Horizontal(g6)
FEATURE [Part::Extrusion] Extrude016  label="caseScrewPillarBracket004"
  Base = -> Sketch022
  Dir = (0,0,1)
  DirMode = 2
  FaceMakerClass = Part::FaceMakerBullseye
  LengthFwd = 2.4
  LengthRev = 0
  Placement = pos=(88.3,29,65.23) rot=(0,1,0;1.5708rad)
  Solid = true
  Symmetric = false
FEATURE [Sketcher::SketchObject] Sketch023
  FullyConstrained = true
  sketch-geometry (7):
    g0: LineSegment StartX=0 StartY=0 StartZ=0 EndX=0 EndY=6 EndZ=0
    g1: Circle CenterX=0 CenterY=0 CenterZ=0 NormalX=0 NormalY=0 NormalZ=1 AngleXU=0 Radius=1
    g2: Circle CenterX=8 CenterY=6 CenterZ=0 NormalX=0 NormalY=0 NormalZ=1 AngleXU=0 Radius=1
    g3: BSplineCurve PolesCount=3 KnotsCount=2 Degree=2 IsPeriodic=0
    g4: GeomPoint X=0 Y=0 Z=0
    g5: GeomPoint X=8 Y=6 Z=0
    g6: LineSegment StartX=0 StartY=6 StartZ=0 EndX=8 EndY=6 EndZ=0
  constraints (14):
    c: Coincident(g0,g-1)
    c: Distance(g0) = 6
    c: Vertical(g0)
    c: Coincident(g3,g0)
    c: Weight(g1) = 1
    c: Equal(g1,g2)
    c: InternalAlignment(g1,g3)
    c: InternalAlignment(g2,g3)
    c: InternalAlignment(g4,g3)
    c: InternalAlignment(g5,g3)
    c: Block(g3)
    c: Coincident(g6,g0)
    c: Coincident(g6,g3)
    c: Horizontal(g6)
FEATURE [Part::Extrusion] Extrude017  label="caseScrewPillarBracket005"
  Base = -> Sketch023
  Dir = (0,0,1)
  DirMode = 2
  FaceMakerClass = Part::FaceMakerBullseye
  LengthFwd = 2.4
  LengthRev = 0
  Placement = pos=(90.7,29,6.77) rot=(0,-1,0;1.5708rad)
  Solid = true
  Symmetric = false
FEATURE [Sketcher::SketchObject] Sketch024
  FullyConstrained = true
  sketch-geometry (7):
    g0: LineSegment StartX=0 StartY=0 StartZ=0 EndX=0 EndY=6 EndZ=0
    g1: Circle CenterX=0 CenterY=0 CenterZ=0 NormalX=0 NormalY=0 NormalZ=1 AngleXU=0 Radius=1
    g2: Circle CenterX=8 CenterY=6 CenterZ=0 NormalX=0 NormalY=0 NormalZ=1 AngleXU=0 Radius=1
    g3: BSplineCurve PolesCount=3 KnotsCount=2 Degree=2 IsPeriodic=0
    g4: GeomPoint X=0 Y=0 Z=0
    g5: GeomPoint X=8 Y=6 Z=0
    g6: LineSegment StartX=0 StartY=6 StartZ=0 EndX=8 EndY=6 EndZ=0
  constraints (14):
    c: Coincident(g0,g-1)
    c: Distance(g0) = 6
    c: Vertical(g0)
    c: Coincident(g3,g0)
    c: Weight(g1) = 1
    c: Equal(g1,g2)
    c: InternalAlignment(g1,g3)
    c: InternalAlignment(g2,g3)
    c: InternalAlignment(g4,g3)
    c: InternalAlignment(g5,g3)
    c: Block(g3)
    c: Coincident(g6,g0)
    c: Coincident(g6,g3)
    c: Horizontal(g6)
FEATURE [Part::Extrusion] Extrude018  label="caseScrewPillarBracket006"
  Base = -> Sketch024
  Dir = (0,0,1)
  DirMode = 2
  FaceMakerClass = Part::FaceMakerBullseye
  LengthFwd = 2.4
  LengthRev = 0
  Placement = pos=(103.7,29,6.77) rot=(0,-1,0;1.5708rad)
  Solid = true
  Symmetric = false
FEATURE [Sketcher::SketchObject] Sketch025
  FullyConstrained = true
  sketch-geometry (7):
    g0: LineSegment StartX=0 StartY=0 StartZ=0 EndX=0 EndY=6 EndZ=0
    g1: Circle CenterX=0 CenterY=0 CenterZ=0 NormalX=0 NormalY=0 NormalZ=1 AngleXU=0 Radius=1
    g2: Circle CenterX=8 CenterY=6 CenterZ=0 NormalX=0 NormalY=0 NormalZ=1 AngleXU=0 Radius=1
    g3: BSplineCurve PolesCount=3 KnotsCount=2 Degree=2 IsPeriodic=0
    g4: GeomPoint X=0 Y=0 Z=0
    g5: GeomPoint X=8 Y=6 Z=0
    g6: LineSegment StartX=0 StartY=6 StartZ=0 EndX=8 EndY=6 EndZ=0
  constraints (14):
    c: Coincident(g0,g-1)
    c: Distance(g0) = 6
    c: Vertical(g0)
    c: Coincident(g3,g0)
    c: Weight(g1) = 1
    c: Equal(g1,g2)
    c: InternalAlignment(g1,g3)
    c: InternalAlignment(g2,g3)
    c: InternalAlignment(g4,g3)
    c: InternalAlignment(g5,g3)
    c: Block(g3)
    c: Coincident(g6,g0)
    c: Coincident(g6,g3)
    c: Horizontal(g6)
FEATURE [Part::Extrusion] Extrude019  label="caseScrewPillarBracket007"
  Base = -> Sketch025
  Dir = (0,0,1)
  DirMode = 2
  FaceMakerClass = Part::FaceMakerBullseye
  LengthFwd = 2.4
  LengthRev = 0
  Placement = pos=(101.3,29,65.23) rot=(0,1,0;1.5708rad)
  Solid = true
  Symmetric = false
FEATURE [Part::Box] Box011  label="frontCaseScrewPillarBracket"
  AttacherType = Attacher::AttachEngine3D
  Height = 2.4
  Length = 16
  Placement = pos=(87,28,2.3) rot=(0,0,1;0rad)
  Width = 7
FEATURE [Part::Box] Box012  label="frontCaseScrewPillarBracket001"
  AttacherType = Attacher::AttachEngine3D
  Height = 2.4
  Length = 16
  Placement = pos=(87,28,67.3) rot=(0,0,1;0rad)
  Width = 7
FEATURE [Sketcher::SketchObject] Sketch026
  FullyConstrained = true
  sketch-geometry (17):
    g0: Circle CenterX=-3.5 CenterY=23.5 CenterZ=0 NormalX=0 NormalY=0 NormalZ=1 AngleXU=0 Radius=1
    g1: Circle CenterX=-1 CenterY=15.25 CenterZ=0 NormalX=0 NormalY=0 NormalZ=1 AngleXU=0 Radius=1
    g2: Circle CenterX=-3.5 CenterY=7 CenterZ=0 NormalX=0 NormalY=0 NormalZ=1 AngleXU=0 Radius=1
    g3: BSplineCurve PolesCount=3 KnotsCount=2 Degree=2 IsPeriodic=0
    g4: GeomPoint X=-3.5 Y=23.5 Z=0
    g5: GeomPoint X=-3.5 Y=7 Z=0
    g6: Circle CenterX=-4.8 CenterY=30.5 CenterZ=0 NormalX=0 NormalY=0 NormalZ=1 AngleXU=0 Radius=1
    g7: Circle CenterX=-3.5 CenterY=30.5 CenterZ=0 NormalX=0 NormalY=0 NormalZ=1 AngleXU=0 Radius=1
    g8: Circle CenterX=-3.5 CenterY=29.2 CenterZ=0 NormalX=0 NormalY=0 NormalZ=1 AngleXU=0 Radius=1
    g9: BSplineCurve PolesCount=3 KnotsCount=2 Degree=2 IsPeriodic=0
    g10: GeomPoint X=-4.8 Y=30.5 Z=0
    g11: GeomPoint X=-3.5 Y=29.2 Z=0
    g12: LineSegment StartX=-3.5 StartY=29.2 StartZ=0 EndX=-3.5 EndY=23.5 EndZ=0
    g13: LineSegment StartX=-4.8 StartY=30.5 StartZ=0 EndX=0 EndY=30.5 EndZ=0
    g14: LineSegment StartX=-3.5 StartY=5 StartZ=0 EndX=-3.5 EndY=7 EndZ=0
    g15: LineSegment StartX=0 StartY=5 StartZ=0 EndX=0 EndY=30.5 EndZ=0
    g16: LineSegment StartX=-3.5 StartY=5 StartZ=0 EndX=0 EndY=5 EndZ=0
  constraints (33):
    c: Weight(g0) = 1
    c: Equal(g0,g1)
    c: Equal(g0,g2)
    c: InternalAlignment(g0,g3)
    c: InternalAlignment(g1,g3)
    c: InternalAlignment(g2,g3)
    c: InternalAlignment(g4,g3)
    c: InternalAlignment(g5,g3)
    c: Block(g3)
    c: Weight(g6) = 1
    c: Equal(g6,g7)
    c: Equal(g6,g8)
    c: InternalAlignment(g6,g9)
    c: InternalAlignment(g7,g9)
    c: InternalAlignment(g8,g9)
    c: InternalAlignment(g10,g9)
    c: InternalAlignment(g11,g9)
    c: Block(g9)
    c: Coincident(g12,g9)
    c: Coincident(g12,g3)
    c: Vertical(g12)
    c: Coincident(g13,g9)
    c: Horizontal(g13)
    c: Distance(g13) = 4.8
    c: Coincident(g14,g3)
    c: Vertical(g14)
    c: Coincident(g15,g13)
    c: Vertical(g15)
    c: Tangent(g15,g1)
    c: Distance(g14) = 2
    c: Coincident(g16,g14)
    c: Horizontal(g16)
    c: Coincident(g15,g16)
FEATURE [Part::Feature] Face050
  shape: bbox 4.8 x 25.5 x 2e-07 mm, 1 faces, 0 solids (baked)
FEATURE [Part::Revolution] Revolve054  label="moreFrontCaseScrewPost001"
  Angle = 360
  Axis = (0,1,0)
  Base = (0,0,0)
  FaceMakerClass = Part::FaceMakerBullseye
  Placement = pos=(102.5,4.5,3.5) rot=(0,0,1;0rad)
  Solid = false
  Source = -> Face050
  Symmetric = false
FEATURE [Part::Feature] Face051
  shape: bbox 4.8 x 25.5 x 2e-07 mm, 1 faces, 0 solids (baked)
FEATURE [Part::Revolution] Revolve055  label="moreFrontCaseScrewPost002"
  Angle = 360
  Axis = (0,1,0)
  Base = (0,0,0)
  FaceMakerClass = Part::FaceMakerBullseye
  Placement = pos=(102.5,4.5,68.5) rot=(0,0,1;0rad)
  Solid = false
  Source = -> Face051
  Symmetric = false
FEATURE [Sketcher::SketchObject] Sketch027
  FullyConstrained = true
  sketch-geometry (10):
    g0: LineSegment StartX=-1.6 StartY=4.7 StartZ=0 EndX=-1.6 EndY=1.7 EndZ=0
    g1: LineSegment StartX=-3.5 StartY=4.7 StartZ=0 EndX=-1.6 EndY=4.7 EndZ=0
    g2: LineSegment StartX=-1.6 StartY=1.7 StartZ=0 EndX=-1.6 EndY=1.5 EndZ=0
    g3: LineSegment StartX=-1.6 StartY=1.5 StartZ=0 EndX=-5.2 EndY=1.5 EndZ=0
    g4: Circle CenterX=-3.5 CenterY=4.7 CenterZ=0 NormalX=0 NormalY=0 NormalZ=1 AngleXU=0 Radius=1
    g5: Circle CenterX=-3.59627 CenterY=2.99743 CenterZ=0 NormalX=0 NormalY=0 NormalZ=1 AngleXU=0 Radius=1
    g6: Circle CenterX=-5.2 CenterY=1.5 CenterZ=0 NormalX=0 NormalY=0 NormalZ=1 AngleXU=0 Radius=1
    g7: BSplineCurve PolesCount=3 KnotsCount=2 Degree=2 IsPeriodic=0
    g8: GeomPoint X=-3.5 Y=4.7 Z=0
    g9: GeomPoint X=-5.2 Y=1.5 Z=0
  constraints (23):
    c: Vertical(g0)
    c: Distance(g0) = 3
    c: Coincident(g1,g0)
    c: Horizontal(g1)
    c: Block(g0)
    c: Block(g1)
    c: Coincident(g2,g0)
    c: Vertical(g2)
    c: Distance(g2) = 0.2
    c: Coincident(g3,g2)
    c: Horizontal(g3)
    c: Block(g3)
    c: Coincident(g7,g1)
    c: Weight(g4) = 1
    c: Equal(g4,g5)
    c: Equal(g4,g6)
    c: Coincident(g7,g3)
    c: InternalAlignment(g4,g7)
    c: InternalAlignment(g5,g7)
    c: InternalAlignment(g6,g7)
    c: InternalAlignment(g8,g7)
    c: InternalAlignment(g9,g7)
    c: Block(g7)
FEATURE [Sketcher::SketchObject] Sketch028
  FullyConstrained = true
  sketch-geometry (18):
    g0: LineSegment StartX=0 StartY=3e-16 StartZ=0 EndX=0 EndY=1.7 EndZ=0
    g1: LineSegment StartX=-3.5 StartY=0 StartZ=0 EndX=-3.5 EndY=0.9 EndZ=0
    g2: Circle CenterX=-2.7 CenterY=1.7 CenterZ=0 NormalX=0 NormalY=0 NormalZ=1 AngleXU=0 Radius=1
    g3: Circle CenterX=-3.5 CenterY=1.7 CenterZ=0 NormalX=0 NormalY=0 NormalZ=1 AngleXU=0 Radius=1
    g4: Circle CenterX=-3.5 CenterY=0.9 CenterZ=0 NormalX=0 NormalY=0 NormalZ=1 AngleXU=0 Radius=1
    g5: BSplineCurve PolesCount=3 KnotsCount=2 Degree=2 IsPeriodic=0
    g6: GeomPoint X=-2.7 Y=1.7 Z=0
    g7: GeomPoint X=-3.5 Y=0.9 Z=0
    g8: LineSegment StartX=-3.5 StartY=0 StartZ=0 EndX=-3.5 EndY=-7 EndZ=0
    g9: LineSegment StartX=0 StartY=3e-16 StartZ=0 EndX=0 EndY=-7 EndZ=0
    g10: LineSegment StartX=-3.5 StartY=-7 StartZ=0 EndX=0 EndY=-7 EndZ=0
    g11: LineSegment StartX=-2.7 StartY=1.7 StartZ=0 EndX=-1.6 EndY=1.7 EndZ=0
    g12: LineSegment StartX=0 StartY=1.7 StartZ=0 EndX=0 EndY=4.5 EndZ=0
    g13: LineSegment StartX=0 StartY=4.5 StartZ=0 EndX=0 EndY=10.8 EndZ=0
    g14: LineSegment StartX=0 StartY=10.8 StartZ=0 EndX=-2 EndY=10.8 EndZ=0
    g15: LineSegment StartX=-1.6 StartY=4.7 StartZ=0 EndX=-1.6 EndY=1.7 EndZ=0
    g16: LineSegment StartX=-1.6 StartY=4.7 StartZ=0 EndX=-2 EndY=4.7 EndZ=0
    g17: LineSegment StartX=-2 StartY=4.7 StartZ=0 EndX=-2 EndY=10.8 EndZ=0
  constraints (44):
    c: Vertical(g0)
    c: Vertical(g1)
    c: Distance(g1) = 0.9
    c: Block(g0)
    c: Distance(g0) = 1.7
    c: Weight(g2) = 1
    c: Equal(g2,g3)
    c: Equal(g2,g4)
    c: Coincident(g5,g1)
    c: InternalAlignment(g2,g5)
    c: InternalAlignment(g3,g5)
    c: InternalAlignment(g4,g5)
    c: InternalAlignment(g6,g5)
    c: InternalAlignment(g7,g5)
    c: Block(g5)
    c: Coincident(g8,g1)
    c: Vertical(g8)
    c: Distance(g8) = 7
    c: Vertical(g9)
    c: Equal(g8,g9) = 7
    c: Coincident(g9,g0)
    c: Coincident(g10,g8)
    c: Coincident(g10,g9)
    c: Horizontal(g10)
    c: Coincident(g11,g5)
    c: Horizontal(g11)
    c: Coincident(g12,g0)
    c: Vertical(g12)
    c: Distance(g12) = 2.8
    c: Coincident(g13,g12)
    c: Vertical(g13)
    c: Distance(g13) = 6.3
    c: Coincident(g14,g13)
    c: Horizontal(g14)
    c: Distance(g14) = 2
    c: Vertical(g15)
    c: Distance(g15) = 3
    c: Block(g11)
    c: Coincident(g15,g11)
    c: Coincident(g16,g15)
    c: Horizontal(g16)
    c: Coincident(g17,g16)
    c: Coincident(g17,g14)
    c: Vertical(g17)
FEATURE [Part::Revolution] Revolve040  label="backCaseScrewRetainer001"
  Angle = 360
  Axis = (0,1,0)
  Base = (0,0,0)
  FaceMakerClass = Part::FaceMakerBullseye
  Placement = pos=(12.5,3,10) rot=(0,0,1;0rad)
  Solid = false
  Source = -> Face036
  Symmetric = false
FEATURE [Part::Feature] Face055
  shape: bbox 3.5 x 30.2 x 2e-07 mm, 1 faces, 0 solids (baked)
FEATURE [Part::Revolution] Revolve059  label="backCaseScrewPost"
  Angle = 360
  Axis = (0,1,0)
  Base = (0,0,0)
  FaceMakerClass = Part::FaceMakerBullseye
  Placement = pos=(12.5,4.5,10) rot=(0,0,1;0rad)
  Solid = false
  Source = -> Face055
  Symmetric = false
FEATURE [Part::Feature] Face056
  shape: bbox 3.5 x 30.2 x 2e-07 mm, 1 faces, 0 solids (baked)
FEATURE [Part::Revolution] Revolve060  label="backCaseScrewPost001"
  Angle = 360
  Axis = (0,1,0)
  Base = (0,0,0)
  FaceMakerClass = Part::FaceMakerBullseye
  Placement = pos=(12.5,4.5,62) rot=(0,0,1;0rad)
  Solid = false
  Source = -> Face056
  Symmetric = false
FEATURE [Part::Feature] Face057
  shape: bbox 3.5 x 17.8 x 2e-07 mm, 1 faces, 0 solids (baked)
FEATURE [Part::Revolution] Revolve061  label="removeToCreateScrewAndThreadedInsertHole"
  Angle = 360
  Axis = (0,1,0)
  Base = (0,0,0)
  FaceMakerClass = Part::FaceMakerBullseye
  Placement = pos=(12.5,0,10) rot=(0,0,1;0rad)
  Solid = false
  Source = -> Face057
  Symmetric = false
FEATURE [Part::Feature] Face058
  shape: bbox 3.5 x 17.8 x 2e-07 mm, 1 faces, 0 solids (baked)
FEATURE [Part::Revolution] Revolve062  label="removeToCreateScrewAndThreadedInsertHole001"
  Angle = 360
  Axis = (0,1,0)
  Base = (0,0,0)
  FaceMakerClass = Part::FaceMakerBullseye
  Placement = pos=(12.5,0,62) rot=(0,0,1;0rad)
  Solid = false
  Source = -> Face058
  Symmetric = false
FEATURE [Part::Feature] Face059
  shape: bbox 3.5 x 17.8 x 2e-07 mm, 1 faces, 0 solids (baked)
FEATURE [Part::Revolution] Revolve063  label="removeToCreateScrewAndThreadedInsertHole002"
  Angle = 360
  Axis = (0,1,0)
  Base = (0,0,0)
  FaceMakerClass = Part::FaceMakerBullseye
  Placement = pos=(89.5,0,68.5) rot=(0,0,1;0rad)
  Solid = false
  Source = -> Face059
  Symmetric = false
FEATURE [Part::Feature] Face060
  shape: bbox 3.5 x 17.8 x 2e-07 mm, 1 faces, 0 solids (baked)
FEATURE [Part::Revolution] Revolve064  label="removeToCreateScrewAndThreadedInsertHole003"
  Angle = 360
  Axis = (0,1,0)
  Base = (0,0,0)
  FaceMakerClass = Part::FaceMakerBullseye
  Placement = pos=(89.5,0,3.5) rot=(0,0,1;0rad)
  Solid = false
  Source = -> Face060
  Symmetric = false
FEATURE [Part::Feature] Face061
  shape: bbox 3.5 x 17.8 x 2e-07 mm, 1 faces, 0 solids (baked)
FEATURE [Part::Revolution] Revolve065  label="removeToCreateScrewAndThreadedInsertHole004"
  Angle = 360
  Axis = (0,1,0)
  Base = (0,0,0)
  FaceMakerClass = Part::FaceMakerBullseye
  Placement = pos=(102.5,4.7,3.5) rot=(0,0,1;0rad)
  Solid = false
  Source = -> Face061
  Symmetric = false
FEATURE [Part::Feature] Face062
  shape: bbox 3.5 x 17.8 x 2e-07 mm, 1 faces, 0 solids (baked)
FEATURE [Part::Revolution] Revolve066  label="removeToCreateScrewAndThreadedInsertHole005"
  Angle = 360
  Axis = (0,1,0)
  Base = (0,0,0)
  FaceMakerClass = Part::FaceMakerBullseye
  Placement = pos=(102.5,4.7,68.5) rot=(0,0,1;0rad)
  Solid = false
  Source = -> Face062
  Symmetric = false
FEATURE [Part::MultiFuse] Fusion047  label="makeHoles"
  Shapes = -> [Revolve066,Revolve065,Revolve064,Revolve063,Revolve062,Revolve061]
FEATURE [Part::Feature] Face063
  shape: bbox 3.6 x 3.2 x 2e-07 mm, 1 faces, 0 solids (baked)
FEATURE [Part::Revolution] Revolve067  label="moreFrontCaseScrewRetainer002"
  Angle = 360
  Axis = (0,1,0)
  Base = (0,0,0)
  FaceMakerClass = Part::FaceMakerBullseye
  Placement = pos=(102.5,4.5,68.5) rot=(0,0,1;0rad)
  Solid = false
  Source = -> Face063
  Symmetric = false
FEATURE [Part::Feature] Face064
  shape: bbox 3.6 x 3.2 x 2e-07 mm, 1 faces, 0 solids (baked)
FEATURE [Part::Revolution] Revolve068  label="moreFrontCaseScrewRetainer003"
  Angle = 360
  Axis = (0,1,0)
  Base = (0,0,0)
  FaceMakerClass = Part::FaceMakerBullseye
  Placement = pos=(102.5,4.5,3.5) rot=(0,0,1;0rad)
  Solid = false
  Source = -> Face064
  Symmetric = false
FEATURE [Part::Feature] Face065
  shape: bbox 3.5 x 17.8 x 2e-07 mm, 1 faces, 0 solids (baked)
FEATURE [Part::Revolution] Revolve069  label="removeToCreateScrewAndThreadedInsertHole006"
  Angle = 360
  Axis = (0,1,0)
  Base = (0,0,0)
  FaceMakerClass = Part::FaceMakerBullseye
  Placement = pos=(12.5,0,10) rot=(0,0,1;0rad)
  Solid = false
  Source = -> Face065
  Symmetric = false
FEATURE [Part::Feature] Face066
  shape: bbox 3.5 x 17.8 x 2e-07 mm, 1 faces, 0 solids (baked)
FEATURE [Part::Revolution] Revolve070  label="removeToCreateScrewAndThreadedInsertHole007"
  Angle = 360
  Axis = (0,1,0)
  Base = (0,0,0)
  FaceMakerClass = Part::FaceMakerBullseye
  Placement = pos=(12.5,0,62) rot=(0,0,1;0rad)
  Solid = false
  Source = -> Face066
  Symmetric = false
FEATURE [Part::Feature] Face067
  shape: bbox 3.5 x 17.8 x 2e-07 mm, 1 faces, 0 solids (baked)
FEATURE [Part::Revolution] Revolve071  label="removeToCreateScrewAndThreadedInsertHole008"
  Angle = 360
  Axis = (0,1,0)
  Base = (0,0,0)
  FaceMakerClass = Part::FaceMakerBullseye
  Placement = pos=(89.5,0,68.5) rot=(0,0,1;0rad)
  Solid = false
  Source = -> Face067
  Symmetric = false
FEATURE [Part::Feature] Face068
  shape: bbox 3.5 x 17.8 x 2e-07 mm, 1 faces, 0 solids (baked)
FEATURE [Part::Revolution] Revolve072  label="removeToCreateScrewAndThreadedInsertHole009"
  Angle = 360
  Axis = (0,1,0)
  Base = (0,0,0)
  FaceMakerClass = Part::FaceMakerBullseye
  Placement = pos=(89.5,0,3.5) rot=(0,0,1;0rad)
  Solid = false
  Source = -> Face068
  Symmetric = false
FEATURE [Part::Feature] Face069
  shape: bbox 3.5 x 17.8 x 2e-07 mm, 1 faces, 0 solids (baked)
FEATURE [Part::Feature] Face070
  shape: bbox 3.5 x 17.8 x 2e-07 mm, 1 faces, 0 solids (baked)
FEATURE [Part::Revolution] Revolve073  label="removeToCreateScrewAndThreadedInsertHole010"
  Angle = 360
  Axis = (0,1,0)
  Base = (0,0,0)
  FaceMakerClass = Part::FaceMakerBullseye
  Placement = pos=(102.5,4.7,3.5) rot=(0,0,1;0rad)
  Solid = false
  Source = -> Face069
  Symmetric = false
FEATURE [Part::Revolution] Revolve074  label="removeToCreateScrewAndThreadedInsertHole011"
  Angle = 360
  Axis = (0,1,0)
  Base = (0,0,0)
  FaceMakerClass = Part::FaceMakerBullseye
  Placement = pos=(102.5,4.7,68.5) rot=(0,0,1;0rad)
  Solid = false
  Source = -> Face070
  Symmetric = false
FEATURE [Part::MultiFuse] Fusion048  label="makeHoles001"
  Shapes = -> [Revolve074,Revolve073,Revolve072,Revolve071,Revolve070,Revolve069]
FEATURE [Part::MultiFuse] Fusion049  label="caseScrewRetainers"
  Shapes = -> [Revolve067,Revolve068,Revolve048,Revolve047,Revolve039,Revolve040]
FEATURE [Part::Cut] Cut015  label="caseScrewRetainers001"
  Base = -> Fusion049
  Tool = -> Fusion048
FEATURE [Part::MultiFuse] Fusion050  label="casePillars"
  Shapes = -> [Revolve055,Revolve054,Revolve043,Revolve046,Revolve059,Revolve060]
FEATURE [Part::Feature] Face071 .. Face076  x6 (patterned run collapsed; names and placements below)
  shape: bbox 3.5 x 17.8 x 2e-07 mm, 1 faces, 0 solids (baked)
FEATURE [Part::Revolution] Revolve075  label="removeToCreateScrewAndThreadedInsertHole012"
  Angle = 360
  Axis = (0,1,0)
  Base = (0,0,0)
  FaceMakerClass = Part::FaceMakerBullseye
  Placement = pos=(12.5,0,10) rot=(0,0,1;0rad)
  Solid = false
  Source = -> Face071
  Symmetric = false
FEATURE [Part::Revolution] Revolve076  label="removeToCreateScrewAndThreadedInsertHole013"
  Angle = 360
  Axis = (0,1,0)
  Base = (0,0,0)
  FaceMakerClass = Part::FaceMakerBullseye
  Placement = pos=(12.5,0,62) rot=(0,0,1;0rad)
  Solid = false
  Source = -> Face072
  Symmetric = false
FEATURE [Part::Revolution] Revolve077  label="removeToCreateScrewAndThreadedInsertHole014"
  Angle = 360
  Axis = (0,1,0)
  Base = (0,0,0)
  FaceMakerClass = Part::FaceMakerBullseye
  Placement = pos=(89.5,0,68.5) rot=(0,0,1;0rad)
  Solid = false
  Source = -> Face073
  Symmetric = false
FEATURE [Part::Revolution] Revolve078  label="removeToCreateScrewAndThreadedInsertHole015"
  Angle = 360
  Axis = (0,1,0)
  Base = (0,0,0)
  FaceMakerClass = Part::FaceMakerBullseye
  Placement = pos=(89.5,0,3.5) rot=(0,0,1;0rad)
  Solid = false
  Source = -> Face074
  Symmetric = false
FEATURE [Part::Revolution] Revolve079  label="removeToCreateScrewAndThreadedInsertHole016"
  Angle = 360
  Axis = (0,1,0)
  Base = (0,0,0)
  FaceMakerClass = Part::FaceMakerBullseye
  Placement = pos=(102.5,4.7,3.5) rot=(0,0,1;0rad)
  Solid = false
  Source = -> Face075
  Symmetric = false
FEATURE [Part::Revolution] Revolve080  label="removeToCreateScrewAndThreadedInsertHole017"
  Angle = 360
  Axis = (0,1,0)
  Base = (0,0,0)
  FaceMakerClass = Part::FaceMakerBullseye
  Placement = pos=(102.5,4.7,68.5) rot=(0,0,1;0rad)
  Solid = false
  Source = -> Face076
  Symmetric = false
FEATURE [Part::MultiFuse] Fusion051  label="makeHoles002"
  Shapes = -> [Revolve080,Revolve079,Revolve078,Revolve077,Revolve076,Revolve075]
FEATURE [Part::Cut] Cut016  label="caesPillars"
  Base = -> Fusion050
  Tool = -> Fusion051
FEATURE [Part::Revolution] Revolve009  label="plugHousing016"
  Angle = 360
  Axis = (0,1,0)
  Base = (0,0,0)
  FaceMakerClass = Part::FaceMakerBullseye
  Placement = pos=(0,0,36.15) rot=(0,0,1;0rad)
  Solid = false
  Source = -> Face012
  Symmetric = false
FEATURE [Part::MultiFuse] Fusion014  label="plugHousing023"
  Placement = pos=(0,0,0) rot=(0,0,1;1.5708rad)
  Shapes = -> [Revolve011,Revolve009]
FEATURE [Part::Revolution] Revolve010  label="plugHousing017"
  Angle = 360
  Axis = (0,1,0)
  Base = (0,0,0)
  FaceMakerClass = Part::FaceMakerBullseye
  Placement = pos=(0,0,36.15) rot=(0,0,1;0rad)
  Solid = false
  Source = -> Face014
  Symmetric = false
FEATURE [Part::MultiFuse] Fusion015  label="plugHousing024"
  Placement = pos=(0,0,0) rot=(0,0,1;1.5708rad)
  Shapes = -> [Revolve010,Revolve015]
FEATURE [Part::Revolution] Revolve014  label="plugHousing026"
  Angle = 360
  Axis = (0,1,0)
  Base = (0,0,0)
  FaceMakerClass = Part::FaceMakerBullseye
  Placement = pos=(0,0,36.15) rot=(0,0,1;0rad)
  Solid = false
  Source = -> Face011
  Symmetric = false
FEATURE [Part::Revolution] Revolve013  label="plugHousing025"
  Angle = 360
  Axis = (0,1,0)
  Base = (0,0,0)
  FaceMakerClass = Part::FaceMakerBullseye
  Placement = pos=(0,0,36.15) rot=(0,0,1;0rad)
  Solid = false
  Source = -> Face015
  Symmetric = false
FEATURE [Part::MultiFuse] Fusion016  label="plugHousing028"
  Placement = pos=(0,19,0) rot=(0,0,1;3.14159rad)
  Shapes = -> [Fusion014,Fusion013]
FEATURE [Part::MultiFuse] Fusion011  label="plugHousing018"
  Placement = pos=(0,0,0) rot=(0,0,1;1.5708rad)
  Shapes = -> [Revolve014,Revolve013]
FEATURE [Part::MultiFuse] Fusion012  label="plugHousing019"
  Placement = pos=(0,19,0) rot=(0,0,1;3.14159rad)
  Shapes = -> [Fusion011,Fusion015]
FEATURE [Part::MultiFuse] Fusion017  label="plugHousing029"
  Placement = pos=(122.621,0,-0.15) rot=(0,0,1;0rad)
  Shapes = -> [Fusion016,Fusion012]
FEATURE [Part::MultiFuse] Fusion052  label="casePillarRetainers"
  Shapes = -> [Extrude012,Extrude013,Extrude014,Extrude015,Extrude016,Extrude017,Extrude018,Extrude019,Box011,Box012]
FEATURE [Part::Feature] Face077
  shape: bbox 3.5 x 17.8 x 2e-07 mm, 1 faces, 0 solids (baked)
FEATURE [Part::Revolution] Revolve081  label="removeToCreateScrewAndThreadedInsertHole018"
  Angle = 360
  Axis = (0,1,0)
  Base = (0,0,0)
  FaceMakerClass = Part::FaceMakerBullseye
  Placement = pos=(62.3,30.3,19.7) rot=(0,0,1;0rad)
  Solid = false
  Source = -> Face077
  Symmetric = false
FEATURE [Part::Feature] Face078
  shape: bbox 3.5 x 17.8 x 2e-07 mm, 1 faces, 0 solids (baked)
FEATURE [Part::Revolution] Revolve082  label="removeToCreateScrewAndThreadedInsertHole019"
  Angle = 360
  Axis = (0,1,0)
  Base = (0,0,0)
  FaceMakerClass = Part::FaceMakerBullseye
  Placement = pos=(62.3,30.3,51.7) rot=(0,0,1;0rad)
  Solid = false
  Source = -> Face078
  Symmetric = false
FEATURE [Part::Feature] Face079
  shape: bbox 3.5 x 17.8 x 2e-07 mm, 1 faces, 0 solids (baked)
FEATURE [Part::Revolution] Revolve083  label="removeToCreateScrewAndThreadedInsertHole020"
  Angle = 360
  Axis = (0,1,0)
  Base = (0,0,0)
  FaceMakerClass = Part::FaceMakerBullseye
  Placement = pos=(30.3,30.3,19.7) rot=(0,0,1;0rad)
  Solid = false
  Source = -> Face079
  Symmetric = false
FEATURE [Part::Feature] Face080
  shape: bbox 3.5 x 17.8 x 2e-07 mm, 1 faces, 0 solids (baked)
FEATURE [Part::Revolution] Revolve084  label="removeToCreateScrewAndThreadedInsertHole021"
  Angle = 360
  Axis = (0,1,0)
  Base = (0,0,0)
  FaceMakerClass = Part::FaceMakerBullseye
  Placement = pos=(30.3,30.3,51.7) rot=(0,0,1;0rad)
  Solid = false
  Source = -> Face080
  Symmetric = false
FEATURE [Part::MultiFuse] Fusion053  label="createThreadedInsertHolesForFan"
  Shapes = -> [Revolve081,Revolve082,Revolve083,Revolve084]
FEATURE [Part::Cut] Cut017  label="fanScrewHousing001"
  Base = -> Fusion046
  Tool = -> Fusion053
FEATURE [Part::Feature] Face081
  shape: bbox 3.5 x 17.8 x 2e-07 mm, 1 faces, 0 solids (baked)
FEATURE [Part::Revolution] Revolve085  label="removeToCreateScrewAndThreadedInsertHole022"
  Angle = 360
  Axis = (0,1,0)
  Base = (0,0,0)
  FaceMakerClass = Part::FaceMakerBullseye
  Placement = pos=(62.3,30.3,19.7) rot=(0,0,1;0rad)
  Solid = false
  Source = -> Face081
  Symmetric = false
FEATURE [Part::Feature] Face082
  shape: bbox 3.5 x 17.8 x 2e-07 mm, 1 faces, 0 solids (baked)
FEATURE [Part::Revolution] Revolve086  label="removeToCreateScrewAndThreadedInsertHole023"
  Angle = 360
  Axis = (0,1,0)
  Base = (0,0,0)
  FaceMakerClass = Part::FaceMakerBullseye
  Placement = pos=(62.3,30.3,51.7) rot=(0,0,1;0rad)
  Solid = false
  Source = -> Face082
  Symmetric = false
FEATURE [Part::Feature] Face083
  shape: bbox 3.5 x 17.8 x 2e-07 mm, 1 faces, 0 solids (baked)
FEATURE [Part::Revolution] Revolve087  label="removeToCreateScrewAndThreadedInsertHole024"
  Angle = 360
  Axis = (0,1,0)
  Base = (0,0,0)
  FaceMakerClass = Part::FaceMakerBullseye
  Placement = pos=(30.3,30.3,19.7) rot=(0,0,1;0rad)
  Solid = false
  Source = -> Face083
  Symmetric = false
FEATURE [Part::Feature] Face084
  shape: bbox 3.5 x 17.8 x 2e-07 mm, 1 faces, 0 solids (baked)
FEATURE [Part::Revolution] Revolve088  label="removeToCreateScrewAndThreadedInsertHole025"
  Angle = 360
  Axis = (0,1,0)
  Base = (0,0,0)
  FaceMakerClass = Part::FaceMakerBullseye
  Placement = pos=(30.3,30.3,51.7) rot=(0,0,1;0rad)
  Solid = false
  Source = -> Face084
  Symmetric = false
FEATURE [Part::MultiFuse] Fusion054  label="createThreadedInsertHolesForFan001"
  Shapes = -> [Revolve085,Revolve086,Revolve087,Revolve088]
FEATURE [Part::Cut] Cut018  label="top007"
  Base = -> Fusion040
  Tool = -> Fusion054
FEATURE [Sketcher::SketchObject] Sketch029
  FullyConstrained = false
  Placement = pos=(0,0,0) rot=(1,0,0;1.5708rad)
  sketch-geometry (24):
    g0: ArcOfCircle CenterX=-4 CenterY=-10.5 CenterZ=0 NormalX=0 NormalY=0 NormalZ=1 AngleXU=0 Radius=1.5 StartAngle=6e-16 EndAngle=3.14159
    g1: ArcOfCircle CenterX=-34.2 CenterY=-10.5 CenterZ=0 NormalX=0 NormalY=0 NormalZ=1 AngleXU=0 Radius=1.5 StartAngle=0 EndAngle=3.14159
    g2: ArcOfCircle CenterX=-34.2 CenterY=-27.7 CenterZ=0 NormalX=0 NormalY=0 NormalZ=1 AngleXU=0 Radius=1.5 StartAngle=3.14159 EndAngle=6.28319
    g3: ArcOfCircle CenterX=-4 CenterY=-27.7 CenterZ=0 NormalX=0 NormalY=0 NormalZ=1 AngleXU=0 Radius=1.5 StartAngle=3.1416 EndAngle=6.28319
    g4: ArcOfCircle CenterX=-10 CenterY=-4.3 CenterZ=0 NormalX=0 NormalY=0 NormalZ=1 AngleXU=0 Radius=1.5 StartAngle=2e-16 EndAngle=3.14159
    g5: ArcOfCircle CenterX=-16.1 CenterY=-1.8 CenterZ=0 NormalX=0 NormalY=0 NormalZ=1 AngleXU=0 Radius=1.5 StartAngle=5e-16 EndAngle=3.14159
    g6: ArcOfCircle CenterX=-22.1 CenterY=-1.8 CenterZ=0 NormalX=0 NormalY=0 NormalZ=1 AngleXU=0 Radius=1.5 StartAngle=5e-16 EndAngle=3.14159
    g7: ArcOfCircle CenterX=-28.2 CenterY=-4.3 CenterZ=0 NormalX=0 NormalY=0 NormalZ=1 AngleXU=0 Radius=1.5 StartAngle=2e-16 EndAngle=3.14159
    g8: ArcOfCircle CenterX=-10 CenterY=-33.9 CenterZ=0 NormalX=0 NormalY=0 NormalZ=1 AngleXU=0 Radius=1.5 StartAngle=3.14159 EndAngle=6.28319
    g9: ArcOfCircle CenterX=-16.1 CenterY=-36.4 CenterZ=0 NormalX=0 NormalY=0 NormalZ=1 AngleXU=0 Radius=1.5 StartAngle=3.14159 EndAngle=6.28319
    g10: ArcOfCircle CenterX=-22.1 CenterY=-36.4 CenterZ=0 NormalX=0 NormalY=0 NormalZ=1 AngleXU=0 Radius=1.5 StartAngle=3.14159 EndAngle=6.28319
    g11: ArcOfCircle CenterX=-28.2 CenterY=-33.9 CenterZ=0 NormalX=0 NormalY=0 NormalZ=1 AngleXU=0 Radius=1.5 StartAngle=3.14159 EndAngle=6.28319
    g12: LineSegment StartX=-35.7 StartY=-10.5 StartZ=0 EndX=-35.7 EndY=-27.7 EndZ=0
    g13: LineSegment StartX=-32.7 StartY=-10.5 StartZ=0 EndX=-32.7 EndY=-27.7 EndZ=0
    g14: LineSegment StartX=-29.7 StartY=-33.9 StartZ=0 EndX=-29.7 EndY=-4.3 EndZ=0
    g15: LineSegment StartX=-26.7 StartY=-33.9 StartZ=0 EndX=-26.7 EndY=-4.3 EndZ=0
    g16: LineSegment StartX=-2.5 StartY=-10.5 StartZ=0 EndX=-2.5 EndY=-27.7 EndZ=0
    g17: LineSegment StartX=-8.5 StartY=-4.3 StartZ=0 EndX=-8.5 EndY=-33.9 EndZ=0
    g18: LineSegment StartX=-5.5 StartY=-10.5 StartZ=0 EndX=-5.5 EndY=-27.7 EndZ=0
    g19: LineSegment StartX=-11.5 StartY=-4.3 StartZ=0 EndX=-11.5 EndY=-33.9 EndZ=0
    g20: LineSegment StartX=-14.6 StartY=-1.8 StartZ=0 EndX=-14.6 EndY=-36.4 EndZ=0
    g21: LineSegment StartX=-17.6 StartY=-1.8 StartZ=0 EndX=-17.6 EndY=-36.4 EndZ=0
    g22: LineSegment StartX=-20.6 StartY=-36.4 StartZ=0 EndX=-20.6 EndY=-1.8 EndZ=0
    g23: LineSegment StartX=-23.6 StartY=-1.8 StartZ=0 EndX=-23.6 EndY=-36.4 EndZ=0
  constraints (48):
    c: Block(g0)
    c: Block(g1)
    c: Block(g2)
    c: Block(g3)
    c: Block(g4)
    c: Block(g5)
    c: Block(g6)
    c: Block(g7)
    c: Block(g8)
    c: Block(g9)
    c: Block(g10)
    c: Block(g11)
    c: Coincident(g12,g1)
    c: Coincident(g12,g2)
    c: Vertical(g12)
    c: Coincident(g13,g1)
    c: Coincident(g13,g2)
    c: Vertical(g13)
    c: Coincident(g14,g11)
    c: Coincident(g14,g7)
    c: Vertical(g14)
    c: Coincident(g15,g11)
    c: Coincident(g15,g7)
    c: Vertical(g15)
    c: Coincident(g16,g0)
    c: Coincident(g16,g3)
    c: Vertical(g16)
    c: Coincident(g17,g4)
    c: Coincident(g17,g8)
    c: Vertical(g17)
    c: Coincident(g18,g0)
    c: Coincident(g18,g3)
    c: Vertical(g18)
    c: Coincident(g19,g4)
    c: Coincident(g19,g8)
    c: Vertical(g19)
    c: Coincident(g20,g5)
    c: Coincident(g20,g9)
    c: Vertical(g20)
    c: Coincident(g21,g5)
    c: Coincident(g21,g9)
    c: Vertical(g21)
    c: Coincident(g22,g10)
    c: Coincident(g22,g6)
    c: Vertical(g22)
    c: Coincident(g23,g6)
    c: Coincident(g23,g10)
    c: Vertical(g23)
FEATURE [Part::Extrusion] Extrude020  label="removeToCreateFanGrillHoles"
  Base = -> Sketch029
  Dir = (0,-1,6e-16)
  DirMode = 2
  FaceMakerClass = Part::FaceMakerBullseye
  LengthFwd = 10
  LengthRev = 0
  Placement = pos=(65.4,44,54.82) rot=(0,0,1;0rad)
  Solid = true
  Symmetric = false
FEATURE [Part::MultiFuse] Fusion055  label="top008"
  Shapes = -> [Cut017,Cut018]
FEATURE [Part::Cut] Cut019  label="top009"
  Base = -> Fusion055
  Tool = -> Extrude020
FEATURE [App::MeasureDistance] Distance003  label="Distance: 71.95 mm"
  Distance = 71.9513
  P1 = (117,38,72)
  P2 = (117,38,0.0487319)
FEATURE [Sketcher::SketchObject] Sketch030
  FullyConstrained = true
  Placement = pos=(117,19,0) rot=(0.57735,0.57735,0.57735;2.0944rad)
  sketch-geometry (48):
    g0: LineSegment StartX=-49.19 StartY=69.25 StartZ=0 EndX=-49.19 EndY=66.25 EndZ=0
    g1: LineSegment StartX=-49.19 StartY=63.5 StartZ=0 EndX=-49.19 EndY=60.5 EndZ=0
    g2: LineSegment StartX=-49.19 StartY=57.75 StartZ=0 EndX=-49.19 EndY=54.75 EndZ=0
    g3: LineSegment StartX=-49.19 StartY=52 StartZ=0 EndX=-49.19 EndY=49 EndZ=0
    g4: LineSegment StartX=-49.19 StartY=46.25 StartZ=0 EndX=-49.19 EndY=43.25 EndZ=0
    g5: LineSegment StartX=-49.19 StartY=40.5 StartZ=0 EndX=-49.19 EndY=37.5 EndZ=0
    g6: LineSegment StartX=-49.19 StartY=34.5 StartZ=0 EndX=-49.19 EndY=31.5 EndZ=0
    g7: LineSegment StartX=-49.19 StartY=28.75 StartZ=0 EndX=-49.19 EndY=25.75 EndZ=0
    g8: LineSegment StartX=-49.19 StartY=23 StartZ=0 EndX=-49.19 EndY=20 EndZ=0
    g9: LineSegment StartX=-49.19 StartY=17.25 StartZ=0 EndX=-49.19 EndY=14.25 EndZ=0
    g10: LineSegment StartX=-49.19 StartY=11.5 StartZ=0 EndX=-49.19 EndY=8.5 EndZ=0
    g11: LineSegment StartX=-49.19 StartY=5.75 StartZ=0 EndX=-49.19 EndY=2.75 EndZ=0
    g12: ArcOfCircle CenterX=-1.5 CenterY=67.75 CenterZ=0 NormalX=0 NormalY=0 NormalZ=1 AngleXU=0 Radius=1.5 StartAngle=4.71239 EndAngle=7.85398
    g13: ArcOfCircle CenterX=-1.5 CenterY=62 CenterZ=0 NormalX=0 NormalY=0 NormalZ=1 AngleXU=0 Radius=1.5 StartAngle=4.71239 EndAngle=7.85398
    g14: ArcOfCircle CenterX=-1.5 CenterY=56.25 CenterZ=0 NormalX=0 NormalY=0 NormalZ=1 AngleXU=0 Radius=1.5 StartAngle=4.71239 EndAngle=7.85398
    g15: ArcOfCircle CenterX=-11.49 CenterY=50.5 CenterZ=0 NormalX=0 NormalY=0 NormalZ=1 AngleXU=0 Radius=1.5 StartAngle=4.71239 EndAngle=7.85398
    g16: ArcOfCircle CenterX=-16.28 CenterY=44.75 CenterZ=0 NormalX=0 NormalY=0 NormalZ=1 AngleXU=0 Radius=1.5 StartAngle=4.71239 EndAngle=7.85398
    g17: ArcOfCircle CenterX=-18.2337 CenterY=39 CenterZ=0 NormalX=0 NormalY=0 NormalZ=1 AngleXU=0 Radius=1.5 StartAngle=4.71485 EndAngle=7.85398
    g18: ArcOfCircle CenterX=-16.2837 CenterY=27.25 CenterZ=0 NormalX=0 NormalY=0 NormalZ=1 AngleXU=0 Radius=1.5 StartAngle=4.71485 EndAngle=7.85398
    g19: ArcOfCircle CenterX=-18.2337 CenterY=33 CenterZ=0 NormalX=0 NormalY=0 NormalZ=1 AngleXU=0 Radius=1.5 StartAngle=4.71485 EndAngle=7.85398
    g20: ArcOfCircle CenterX=-11.49 CenterY=21.5 CenterZ=0 NormalX=0 NormalY=0 NormalZ=1 AngleXU=0 Radius=1.5 StartAngle=4.71239 EndAngle=7.85398
    g21: ArcOfCircle CenterX=-1.5 CenterY=4.25 CenterZ=0 NormalX=0 NormalY=0 NormalZ=1 AngleXU=0 Radius=1.5 StartAngle=4.71239 EndAngle=7.85398
    g22: ArcOfCircle CenterX=-1.5 CenterY=10 CenterZ=0 NormalX=0 NormalY=0 NormalZ=1 AngleXU=0 Radius=1.5 StartAngle=4.71239 EndAngle=7.85398
    g23: ArcOfCircle CenterX=-1.5 CenterY=15.75 CenterZ=0 NormalX=0 NormalY=0 NormalZ=1 AngleXU=0 Radius=1.5 StartAngle=4.71239 EndAngle=7.85398
    g24: LineSegment StartX=-49.19 StartY=69.25 StartZ=0 EndX=-1.5 EndY=69.25 EndZ=0
    g25: LineSegment StartX=-49.19 StartY=66.25 StartZ=0 EndX=-1.5 EndY=66.25 EndZ=0
    g26: LineSegment StartX=-49.19 StartY=63.5 StartZ=0 EndX=-1.5 EndY=63.5 EndZ=0
    g27: LineSegment StartX=-49.19 StartY=60.5 StartZ=0 EndX=-1.5 EndY=60.5 EndZ=0
    g28: LineSegment StartX=-49.19 StartY=57.75 StartZ=0 EndX=-1.5 EndY=57.75 EndZ=0
    g29: LineSegment StartX=-49.19 StartY=54.75 StartZ=0 EndX=-1.5 EndY=54.75 EndZ=0
    g30: LineSegment StartX=-49.19 StartY=52 StartZ=0 EndX=-11.49 EndY=52 EndZ=0
    g31: LineSegment StartX=-49.19 StartY=49 StartZ=0 EndX=-11.49 EndY=49 EndZ=0
    g32: LineSegment StartX=-49.19 StartY=46.25 StartZ=0 EndX=-16.28 EndY=46.25 EndZ=0
    g33: LineSegment StartX=-49.19 StartY=43.25 StartZ=0 EndX=-16.28 EndY=43.25 EndZ=0
    g34: LineSegment StartX=-49.19 StartY=40.5 StartZ=0 EndX=-18.2337 EndY=40.5 EndZ=0
    g35: LineSegment StartX=-49.19 StartY=37.5 StartZ=0 EndX=-18.23 EndY=37.5 EndZ=0
    g36: LineSegment StartX=-49.19 StartY=34.5 StartZ=0 EndX=-18.2337 EndY=34.5 EndZ=0
    g37: LineSegment StartX=-49.19 StartY=31.5 StartZ=0 EndX=-18.23 EndY=31.5 EndZ=0
    g38: LineSegment StartX=-49.19 StartY=28.75 StartZ=0 EndX=-16.2837 EndY=28.75 EndZ=0
    g39: LineSegment StartX=-49.19 StartY=25.75 StartZ=0 EndX=-16.28 EndY=25.75 EndZ=0
    g40: LineSegment StartX=-49.19 StartY=23 StartZ=0 EndX=-11.49 EndY=23 EndZ=0
    g41: LineSegment StartX=-49.19 StartY=20 StartZ=0 EndX=-11.49 EndY=20 EndZ=0
    g42: LineSegment StartX=-49.19 StartY=17.25 StartZ=0 EndX=-1.5 EndY=17.25 EndZ=0
    g43: LineSegment StartX=-49.19 StartY=14.25 StartZ=0 EndX=-1.5 EndY=14.25 EndZ=0
    g44: LineSegment StartX=-49.19 StartY=11.5 StartZ=0 EndX=-1.5 EndY=11.5 EndZ=0
    g45: LineSegment StartX=-49.19 StartY=8.5 StartZ=0 EndX=-1.5 EndY=8.5 EndZ=0
    g46: LineSegment StartX=-49.19 StartY=5.75 StartZ=0 EndX=-1.5 EndY=5.75 EndZ=0
    g47: LineSegment StartX=-49.19 StartY=2.75 StartZ=0 EndX=-1.5 EndY=2.75 EndZ=0
  constraints (120):
    c: Vertical(g0)
    c: Distance(g0) = 3
    c: Block(g0)
    c: Vertical(g1)
    c: Distance(g1) = 3
    c: Vertical(g2)
    c: Equal(g0,g2) = 3
    c: Block(g2)
    c: Vertical(g3)
    c: Equal(g1,g3) = 3
    c: Vertical(g4)
    c: Equal(g0,g4) = 3
    c: Block(g4)
    c: Vertical(g5)
    c: Equal(g1,g5) = 3
    c: Vertical(g6)
    c: Equal(g0,g6) = 3
    c: Block(g6)
    c: Vertical(g7)
    c: Equal(g1,g7) = 3
    c: Vertical(g8)
    c: Equal(g0,g8) = 3
    c: Block(g8)
    c: Vertical(g9)
    c: Equal(g1,g9) = 3
    c: Vertical(g10)
    c: Equal(g0,g10) = 3
    c: Block(g10)
    c: Vertical(g11)
    c: Equal(g1,g11) = 3
    c: Block(g12)
    c: Block(g13)
    c: Block(g14)
    c: Block(g15)
    c: Block(g16)
    c: Block(g17)
    c: Block(g18)
    c: Block(g19)
    c: Block(g20)
    c: Block(g21)
    c: Block(g22)
    c: Block(g23)
    c: Block(g11)
    c: Block(g9)
    c: Block(g7)
    c: Block(g5)
    c: Block(g3)
    c: Block(g1)
    c: Coincident(g24,g0)
    c: Coincident(g24,g12)
    c: Horizontal(g24)
    c: Coincident(g25,g0)
    c: Coincident(g25,g12)
    c: Horizontal(g25)
    c: Coincident(g26,g1)
    c: Coincident(g26,g13)
    c: Horizontal(g26)
    c: Coincident(g27,g1)
    c: Coincident(g27,g13)
    c: Horizontal(g27)
    c: Coincident(g28,g2)
    c: Coincident(g28,g14)
    c: Horizontal(g28)
    c: Coincident(g29,g2)
    c: Coincident(g29,g14)
    c: Horizontal(g29)
    c: Coincident(g30,g3)
    c: Coincident(g30,g15)
    c: Horizontal(g30)
    c: Coincident(g31,g3)
    c: Coincident(g31,g15)
    c: Horizontal(g31)
    c: Coincident(g32,g4)
    c: Coincident(g32,g16)
    c: Horizontal(g32)
    c: Coincident(g33,g4)
    c: Coincident(g33,g16)
    c: Horizontal(g33)
    c: Coincident(g34,g5)
    c: Coincident(g34,g17)
    c: Horizontal(g34)
    c: Coincident(g35,g5)
    c: Coincident(g35,g17)
    c: Horizontal(g35)
    c: Coincident(g36,g6)
    c: Coincident(g36,g19)
    c: Horizontal(g36)
    c: Coincident(g37,g6)
    c: Coincident(g37,g19)
    c: Horizontal(g37)
    c: Coincident(g38,g7)
    c: Coincident(g38,g18)
    c: Horizontal(g38)
    c: Coincident(g39,g7)
    c: Coincident(g39,g18)
    c: Horizontal(g39)
    c: Coincident(g40,g8)
    c: Coincident(g40,g20)
    c: Horizontal(g40)
    c: Coincident(g41,g8)
    c: Coincident(g41,g20)
    c: Horizontal(g41)
    c: Coincident(g42,g9)
    c: Coincident(g42,g23)
    c: Horizontal(g42)
    c: Coincident(g43,g9)
    c: Coincident(g43,g23)
    c: Horizontal(g43)
    c: Coincident(g44,g10)
    c: Coincident(g44,g22)
    c: Horizontal(g44)
    c: Coincident(g45,g10)
    c: Coincident(g45,g22)
    c: Horizontal(g45)
    c: Coincident(g46,g11)
    c: Coincident(g46,g21)
    c: Horizontal(g46)
    c: Coincident(g47,g11)
    c: Coincident(g47,g21)
    c: Horizontal(g47)
FEATURE [Sketcher::SketchObject] Sketch031
  FullyConstrained = true
  Placement = pos=(117,19,0) rot=(0.57735,0.57735,0.57735;2.0944rad)
  sketch-geometry (24):
    g0: ArcOfCircle CenterX=-49.19 CenterY=67.75 CenterZ=0 NormalX=0 NormalY=0 NormalZ=1 AngleXU=0 Radius=1.5 StartAngle=1.5708 EndAngle=4.71239
    g1: ArcOfCircle CenterX=-49.19 CenterY=62 CenterZ=0 NormalX=0 NormalY=0 NormalZ=1 AngleXU=0 Radius=1.5 StartAngle=1.5708 EndAngle=4.71239
    g2: ArcOfCircle CenterX=-49.19 CenterY=56.25 CenterZ=0 NormalX=0 NormalY=0 NormalZ=1 AngleXU=0 Radius=1.5 StartAngle=1.5708 EndAngle=4.71239
    g3: ArcOfCircle CenterX=-49.19 CenterY=50.5 CenterZ=0 NormalX=0 NormalY=0 NormalZ=1 AngleXU=0 Radius=1.5 StartAngle=1.5708 EndAngle=4.71239
    g4: ArcOfCircle CenterX=-49.19 CenterY=44.75 CenterZ=0 NormalX=0 NormalY=0 NormalZ=1 AngleXU=0 Radius=1.5 StartAngle=1.5708 EndAngle=4.71239
    g5: ArcOfCircle CenterX=-49.19 CenterY=39 CenterZ=0 NormalX=0 NormalY=0 NormalZ=1 AngleXU=0 Radius=1.5 StartAngle=1.5708 EndAngle=4.71239
    g6: ArcOfCircle CenterX=-49.19 CenterY=33 CenterZ=0 NormalX=0 NormalY=0 NormalZ=1 AngleXU=0 Radius=1.5 StartAngle=1.5708 EndAngle=4.71239
    g7: ArcOfCircle CenterX=-49.19 CenterY=27.25 CenterZ=0 NormalX=0 NormalY=0 NormalZ=1 AngleXU=0 Radius=1.5 StartAngle=1.5708 EndAngle=4.71239
    g8: ArcOfCircle CenterX=-49.19 CenterY=21.5 CenterZ=0 NormalX=0 NormalY=0 NormalZ=1 AngleXU=0 Radius=1.5 StartAngle=1.5708 EndAngle=4.71239
    g9: ArcOfCircle CenterX=-49.19 CenterY=15.75 CenterZ=0 NormalX=0 NormalY=0 NormalZ=1 AngleXU=0 Radius=1.5 StartAngle=1.5708 EndAngle=4.71239
    g10: ArcOfCircle CenterX=-49.19 CenterY=10 CenterZ=0 NormalX=0 NormalY=0 NormalZ=1 AngleXU=0 Radius=1.5 StartAngle=1.5708 EndAngle=4.71239
    g11: ArcOfCircle CenterX=-49.19 CenterY=4.25 CenterZ=0 NormalX=0 NormalY=0 NormalZ=1 AngleXU=0 Radius=1.5 StartAngle=1.5708 EndAngle=4.71239
    g12: LineSegment StartX=-49.19 StartY=69.25 StartZ=0 EndX=-49.19 EndY=66.25 EndZ=0
    g13: LineSegment StartX=-49.19 StartY=63.5 StartZ=0 EndX=-49.19 EndY=60.5 EndZ=0
    g14: LineSegment StartX=-49.19 StartY=57.75 StartZ=0 EndX=-49.19 EndY=54.75 EndZ=0
    g15: LineSegment StartX=-49.19 StartY=52 StartZ=0 EndX=-49.19 EndY=49 EndZ=0
    g16: LineSegment StartX=-49.19 StartY=46.25 StartZ=0 EndX=-49.19 EndY=43.25 EndZ=0
    g17: LineSegment StartX=-49.19 StartY=40.5 StartZ=0 EndX=-49.19 EndY=37.5 EndZ=0
    g18: LineSegment StartX=-49.19 StartY=34.5 StartZ=0 EndX=-49.19 EndY=31.5 EndZ=0
    g19: LineSegment StartX=-49.19 StartY=28.75 StartZ=0 EndX=-49.19 EndY=25.75 EndZ=0
    g20: LineSegment StartX=-49.19 StartY=23 StartZ=0 EndX=-49.19 EndY=20 EndZ=0
    g21: LineSegment StartX=-49.19 StartY=17.25 StartZ=0 EndX=-49.19 EndY=14.25 EndZ=0
    g22: LineSegment StartX=-49.19 StartY=11.5 StartZ=0 EndX=-49.19 EndY=8.5 EndZ=0
    g23: LineSegment StartX=-49.19 StartY=5.75 StartZ=0 EndX=-49.19 EndY=2.75 EndZ=0
  constraints (48):
    c: Block(g0)
    c: Block(g1)
    c: Block(g2)
    c: Block(g3)
    c: Block(g4)
    c: Block(g5)
    c: Block(g6)
    c: Block(g7)
    c: Block(g8)
    c: Block(g9)
    c: Block(g10)
    c: Block(g11)
    c: Coincident(g12,g0)
    c: Coincident(g12,g0)
    c: Vertical(g12)
    c: Vertical(g13)
    c: Coincident(g13,g1)
    c: Vertical(g14)
    c: Coincident(g14,g2)
    c: Vertical(g15)
    c: Coincident(g15,g3)
    c: Vertical(g16)
    c: Coincident(g16,g4)
    c: Vertical(g17)
    c: Coincident(g17,g5)
    c: Vertical(g18)
    c: Coincident(g18,g6)
    c: Vertical(g19)
    c: Coincident(g19,g7)
    c: Vertical(g20)
    c: Coincident(g20,g8)
    c: Vertical(g21)
    c: Coincident(g21,g9)
    c: Vertical(g22)
    c: Coincident(g22,g10)
    c: Vertical(g23)
    c: Coincident(g23,g11)
    c: Block(g23)
    c: Block(g22)
    c: Block(g21)
    c: Block(g20)
    c: Block(g13)
    c: Block(g14)
    c: Block(g15)
    c: Block(g16)
    c: Block(g17)
    c: Block(g18)
    c: Block(g19)
FEATURE [Part::Extrusion] Extrude022
  Base = -> Sketch030
  Dir = (1,-2e-16,2e-16)
  DirMode = 2
  FaceMakerClass = Part::FaceMakerBullseye
  LengthFwd = 19
  LengthRev = 0
  Placement = pos=(-19,0,0) rot=(0,0,1;0rad)
  Solid = true
  Symmetric = false
FEATURE [Part::Fillet] Fillet022
  Base = -> Extrude022
  Edges = 24 edges r=1.49: [Edge6,Edge11,Edge18,Edge23,Edge30,Edge35,Edge42,Edge47,Edge54,Edge59,Edge66,Edge71,Edge78,Edge83,Edge90,Edge95,Edge102,Edge107,Edge114,Edge119,Edge126,Edge131,Edge138,Edge143]
FEATURE [Part::Cut] Cut020  label="top010"
  Base = -> Cut019
  Tool = -> Fillet022
FEATURE [Sketcher::SketchObject] Sketch032
  FullyConstrained = true
  Placement = pos=(117,19,0) rot=(0.57735,0.57735,0.57735;2.0944rad)
  sketch-geometry (48):
    g0: LineSegment StartX=-49.19 StartY=69.25 StartZ=0 EndX=-49.19 EndY=66.25 EndZ=0
    g1: LineSegment StartX=-49.19 StartY=63.5 StartZ=0 EndX=-49.19 EndY=60.5 EndZ=0
    g2: LineSegment StartX=-49.19 StartY=57.75 StartZ=0 EndX=-49.19 EndY=54.75 EndZ=0
    g3: LineSegment StartX=-49.19 StartY=52 StartZ=0 EndX=-49.19 EndY=49 EndZ=0
    g4: LineSegment StartX=-49.19 StartY=46.25 StartZ=0 EndX=-49.19 EndY=43.25 EndZ=0
    g5: LineSegment StartX=-49.19 StartY=40.5 StartZ=0 EndX=-49.19 EndY=37.5 EndZ=0
    g6: LineSegment StartX=-49.19 StartY=34.5 StartZ=0 EndX=-49.19 EndY=31.5 EndZ=0
    g7: LineSegment StartX=-49.19 StartY=28.75 StartZ=0 EndX=-49.19 EndY=25.75 EndZ=0
    g8: LineSegment StartX=-49.19 StartY=23 StartZ=0 EndX=-49.19 EndY=20 EndZ=0
    g9: LineSegment StartX=-49.19 StartY=17.25 StartZ=0 EndX=-49.19 EndY=14.25 EndZ=0
    g10: LineSegment StartX=-49.19 StartY=11.5 StartZ=0 EndX=-49.19 EndY=8.5 EndZ=0
    g11: LineSegment StartX=-49.19 StartY=5.75 StartZ=0 EndX=-49.19 EndY=2.75 EndZ=0
    g12: ArcOfCircle CenterX=-1.5 CenterY=67.75 CenterZ=0 NormalX=0 NormalY=0 NormalZ=1 AngleXU=0 Radius=1.5 StartAngle=4.71239 EndAngle=7.85398
    g13: ArcOfCircle CenterX=-1.5 CenterY=62 CenterZ=0 NormalX=0 NormalY=0 NormalZ=1 AngleXU=0 Radius=1.5 StartAngle=4.71239 EndAngle=7.85398
    g14: ArcOfCircle CenterX=-1.5 CenterY=56.25 CenterZ=0 NormalX=0 NormalY=0 NormalZ=1 AngleXU=0 Radius=1.5 StartAngle=4.71239 EndAngle=7.85398
    g15: ArcOfCircle CenterX=-11.49 CenterY=50.5 CenterZ=0 NormalX=0 NormalY=0 NormalZ=1 AngleXU=0 Radius=1.5 StartAngle=4.71239 EndAngle=7.85398
    g16: ArcOfCircle CenterX=-16.28 CenterY=44.75 CenterZ=0 NormalX=0 NormalY=0 NormalZ=1 AngleXU=0 Radius=1.5 StartAngle=4.71239 EndAngle=7.85398
    g17: ArcOfCircle CenterX=-18.2337 CenterY=39 CenterZ=0 NormalX=0 NormalY=0 NormalZ=1 AngleXU=0 Radius=1.5 StartAngle=4.71485 EndAngle=7.85398
    g18: ArcOfCircle CenterX=-16.2837 CenterY=27.25 CenterZ=0 NormalX=0 NormalY=0 NormalZ=1 AngleXU=0 Radius=1.5 StartAngle=4.71485 EndAngle=7.85398
    g19: ArcOfCircle CenterX=-18.2337 CenterY=33 CenterZ=0 NormalX=0 NormalY=0 NormalZ=1 AngleXU=0 Radius=1.5 StartAngle=4.71485 EndAngle=7.85398
    g20: ArcOfCircle CenterX=-11.49 CenterY=21.5 CenterZ=0 NormalX=0 NormalY=0 NormalZ=1 AngleXU=0 Radius=1.5 StartAngle=4.71239 EndAngle=7.85398
    g21: ArcOfCircle CenterX=-1.5 CenterY=4.25 CenterZ=0 NormalX=0 NormalY=0 NormalZ=1 AngleXU=0 Radius=1.5 StartAngle=4.71239 EndAngle=7.85398
    g22: ArcOfCircle CenterX=-1.5 CenterY=10 CenterZ=0 NormalX=0 NormalY=0 NormalZ=1 AngleXU=0 Radius=1.5 StartAngle=4.71239 EndAngle=7.85398
    g23: ArcOfCircle CenterX=-1.5 CenterY=15.75 CenterZ=0 NormalX=0 NormalY=0 NormalZ=1 AngleXU=0 Radius=1.5 StartAngle=4.71239 EndAngle=7.85398
    g24: LineSegment StartX=-49.19 StartY=69.25 StartZ=0 EndX=-1.5 EndY=69.25 EndZ=0
    g25: LineSegment StartX=-49.19 StartY=66.25 StartZ=0 EndX=-1.5 EndY=66.25 EndZ=0
    g26: LineSegment StartX=-49.19 StartY=63.5 StartZ=0 EndX=-1.5 EndY=63.5 EndZ=0
    g27: LineSegment StartX=-49.19 StartY=60.5 StartZ=0 EndX=-1.5 EndY=60.5 EndZ=0
    g28: LineSegment StartX=-49.19 StartY=57.75 StartZ=0 EndX=-1.5 EndY=57.75 EndZ=0
    g29: LineSegment StartX=-49.19 StartY=54.75 StartZ=0 EndX=-1.5 EndY=54.75 EndZ=0
    g30: LineSegment StartX=-49.19 StartY=52 StartZ=0 EndX=-11.49 EndY=52 EndZ=0
    g31: LineSegment StartX=-49.19 StartY=49 StartZ=0 EndX=-11.49 EndY=49 EndZ=0
    g32: LineSegment StartX=-49.19 StartY=46.25 StartZ=0 EndX=-16.28 EndY=46.25 EndZ=0
    g33: LineSegment StartX=-49.19 StartY=43.25 StartZ=0 EndX=-16.28 EndY=43.25 EndZ=0
    g34: LineSegment StartX=-49.19 StartY=40.5 StartZ=0 EndX=-18.2337 EndY=40.5 EndZ=0
    g35: LineSegment StartX=-49.19 StartY=37.5 StartZ=0 EndX=-18.23 EndY=37.5 EndZ=0
    g36: LineSegment StartX=-49.19 StartY=34.5 StartZ=0 EndX=-18.2337 EndY=34.5 EndZ=0
    g37: LineSegment StartX=-49.19 StartY=31.5 StartZ=0 EndX=-18.23 EndY=31.5 EndZ=0
    g38: LineSegment StartX=-49.19 StartY=28.75 StartZ=0 EndX=-16.2837 EndY=28.75 EndZ=0
    g39: LineSegment StartX=-49.19 StartY=25.75 StartZ=0 EndX=-16.28 EndY=25.75 EndZ=0
    g40: LineSegment StartX=-49.19 StartY=23 StartZ=0 EndX=-11.49 EndY=23 EndZ=0
    g41: LineSegment StartX=-49.19 StartY=20 StartZ=0 EndX=-11.49 EndY=20 EndZ=0
    g42: LineSegment StartX=-49.19 StartY=17.25 StartZ=0 EndX=-1.5 EndY=17.25 EndZ=0
    g43: LineSegment StartX=-49.19 StartY=14.25 StartZ=0 EndX=-1.5 EndY=14.25 EndZ=0
    g44: LineSegment StartX=-49.19 StartY=11.5 StartZ=0 EndX=-1.5 EndY=11.5 EndZ=0
    g45: LineSegment StartX=-49.19 StartY=8.5 StartZ=0 EndX=-1.5 EndY=8.5 EndZ=0
    g46: LineSegment StartX=-49.19 StartY=5.75 StartZ=0 EndX=-1.5 EndY=5.75 EndZ=0
    g47: LineSegment StartX=-49.19 StartY=2.75 StartZ=0 EndX=-1.5 EndY=2.75 EndZ=0
  constraints (120):
    c: Vertical(g0)
    c: Distance(g0) = 3
    c: Block(g0)
    c: Vertical(g1)
    c: Distance(g1) = 3
    c: Vertical(g2)
    c: Equal(g0,g2) = 3
    c: Block(g2)
    c: Vertical(g3)
    c: Equal(g1,g3) = 3
    c: Vertical(g4)
    c: Equal(g0,g4) = 3
    c: Block(g4)
    c: Vertical(g5)
    c: Equal(g1,g5) = 3
    c: Vertical(g6)
    c: Equal(g0,g6) = 3
    c: Block(g6)
    c: Vertical(g7)
    c: Equal(g1,g7) = 3
    c: Vertical(g8)
    c: Equal(g0,g8) = 3
    c: Block(g8)
    c: Vertical(g9)
    c: Equal(g1,g9) = 3
    c: Vertical(g10)
    c: Equal(g0,g10) = 3
    c: Block(g10)
    c: Vertical(g11)
    c: Equal(g1,g11) = 3
    c: Block(g12)
    c: Block(g13)
    c: Block(g14)
    c: Block(g15)
    c: Block(g16)
    c: Block(g17)
    c: Block(g18)
    c: Block(g19)
    c: Block(g20)
    c: Block(g21)
    c: Block(g22)
    c: Block(g23)
    c: Block(g11)
    c: Block(g9)
    c: Block(g7)
    c: Block(g5)
    c: Block(g3)
    c: Block(g1)
    c: Coincident(g24,g0)
    c: Coincident(g24,g12)
    c: Horizontal(g24)
    c: Coincident(g25,g0)
    c: Coincident(g25,g12)
    c: Horizontal(g25)
    c: Coincident(g26,g1)
    c: Coincident(g26,g13)
    c: Horizontal(g26)
    c: Coincident(g27,g1)
    c: Coincident(g27,g13)
    c: Horizontal(g27)
    c: Coincident(g28,g2)
    c: Coincident(g28,g14)
    c: Horizontal(g28)
    c: Coincident(g29,g2)
    c: Coincident(g29,g14)
    c: Horizontal(g29)
    c: Coincident(g30,g3)
    c: Coincident(g30,g15)
    c: Horizontal(g30)
    c: Coincident(g31,g3)
    c: Coincident(g31,g15)
    c: Horizontal(g31)
    c: Coincident(g32,g4)
    c: Coincident(g32,g16)
    c: Horizontal(g32)
    c: Coincident(g33,g4)
    c: Coincident(g33,g16)
    c: Horizontal(g33)
    c: Coincident(g34,g5)
    c: Coincident(g34,g17)
    c: Horizontal(g34)
    c: Coincident(g35,g5)
    c: Coincident(g35,g17)
    c: Horizontal(g35)
    c: Coincident(g36,g6)
    c: Coincident(g36,g19)
    c: Horizontal(g36)
    c: Coincident(g37,g6)
    c: Coincident(g37,g19)
    c: Horizontal(g37)
    c: Coincident(g38,g7)
    c: Coincident(g38,g18)
    c: Horizontal(g38)
    c: Coincident(g39,g7)
    c: Coincident(g39,g18)
    c: Horizontal(g39)
    c: Coincident(g40,g8)
    c: Coincident(g40,g20)
    c: Horizontal(g40)
    c: Coincident(g41,g8)
    c: Coincident(g41,g20)
    c: Horizontal(g41)
    c: Coincident(g42,g9)
    c: Coincident(g42,g23)
    c: Horizontal(g42)
    c: Coincident(g43,g9)
    c: Coincident(g43,g23)
    c: Horizontal(g43)
    c: Coincident(g44,g10)
    c: Coincident(g44,g22)
    c: Horizontal(g44)
    c: Coincident(g45,g10)
    c: Coincident(g45,g22)
    c: Horizontal(g45)
    c: Coincident(g46,g11)
    c: Coincident(g46,g21)
    c: Horizontal(g46)
    c: Coincident(g47,g11)
    c: Coincident(g47,g21)
    c: Horizontal(g47)
FEATURE [Part::Extrusion] Extrude023
  Base = -> Sketch032
  Dir = (1,-2e-16,2e-16)
  DirMode = 2
  FaceMakerClass = Part::FaceMakerBullseye
  LengthFwd = 19
  LengthRev = 0
  Placement = pos=(-19,0,0) rot=(0,0,1;0rad)
  Solid = true
  Symmetric = false
FEATURE [Part::Fillet] Fillet023
  Base = -> Extrude023
  Edges = <same value as first occurrence — deduplicated (x6 in doc)>
  Placement = pos=(0,0.05,0) rot=(0,0,1;0rad)
FEATURE [Part::Cut] Cut014  label="bottom003"
  Base = -> Cut007
  Tool = -> Fusion047
FEATURE [Part::Cut] Cut021  label="bottom004"
  Base = -> Cut014
  Tool = -> Fillet023
FEATURE [Sketcher::SketchObject] Sketch033
  FullyConstrained = true
  Placement = pos=(117,19,0) rot=(0.57735,0.57735,0.57735;2.0944rad)
  sketch-geometry (8):
    g0: LineSegment StartX=-49.19 StartY=69.25 StartZ=0 EndX=-49.19 EndY=66.25 EndZ=0
    g1: LineSegment StartX=-49.19 StartY=5.75 StartZ=0 EndX=-49.19 EndY=2.75 EndZ=0
    g2: ArcOfCircle CenterX=-1.5 CenterY=67.75 CenterZ=0 NormalX=0 NormalY=0 NormalZ=1 AngleXU=0 Radius=1.5 StartAngle=4.71239 EndAngle=7.85398
    g3: ArcOfCircle CenterX=-1.5 CenterY=4.25 CenterZ=0 NormalX=0 NormalY=0 NormalZ=1 AngleXU=0 Radius=1.5 StartAngle=4.71239 EndAngle=7.85398
    g4: LineSegment StartX=-49.19 StartY=69.25 StartZ=0 EndX=-1.5 EndY=69.25 EndZ=0
    g5: LineSegment StartX=-49.19 StartY=66.25 StartZ=0 EndX=-1.5 EndY=66.25 EndZ=0
    g6: LineSegment StartX=-49.19 StartY=5.75 StartZ=0 EndX=-1.5 EndY=5.75 EndZ=0
    g7: LineSegment StartX=-49.19 StartY=2.75 StartZ=0 EndX=-1.5 EndY=2.75 EndZ=0
  constraints (19):
    c: Vertical(g0)
    c: Distance(g0) = 3
    c: Block(g0)
    c: Vertical(g1)
    c: Block(g2)
    c: Block(g3)
    c: Block(g1)
    c: Coincident(g4,g0)
    c: Coincident(g4,g2)
    c: Horizontal(g4)
    c: Coincident(g5,g0)
    c: Coincident(g5,g2)
    c: Horizontal(g5)
    c: Coincident(g6,g1)
    c: Coincident(g6,g3)
    c: Horizontal(g6)
    c: Coincident(g7,g1)
    c: Coincident(g7,g3)
    c: Horizontal(g7)
FEATURE [Sketcher::SketchObject] Sketch034
  FullyConstrained = true
  Placement = pos=(117,19,0) rot=(0.57735,0.57735,0.57735;2.0944rad)
  sketch-geometry (8):
    g0: LineSegment StartX=-49.19 StartY=63.5 StartZ=0 EndX=-49.19 EndY=60.5 EndZ=0
    g1: LineSegment StartX=-49.19 StartY=11.5 StartZ=0 EndX=-49.19 EndY=8.5 EndZ=0
    g2: ArcOfCircle CenterX=-1.5 CenterY=62 CenterZ=0 NormalX=0 NormalY=0 NormalZ=1 AngleXU=0 Radius=1.5 StartAngle=4.71239 EndAngle=7.85398
    g3: ArcOfCircle CenterX=-1.5 CenterY=10 CenterZ=0 NormalX=0 NormalY=0 NormalZ=1 AngleXU=0 Radius=1.5 StartAngle=4.71239 EndAngle=7.85398
    g4: LineSegment StartX=-49.19 StartY=63.5 StartZ=0 EndX=-1.5 EndY=63.5 EndZ=0
    g5: LineSegment StartX=-49.19 StartY=60.5 StartZ=0 EndX=-1.5 EndY=60.5 EndZ=0
    g6: LineSegment StartX=-49.19 StartY=11.5 StartZ=0 EndX=-1.5 EndY=11.5 EndZ=0
    g7: LineSegment StartX=-49.19 StartY=8.5 StartZ=0 EndX=-1.5 EndY=8.5 EndZ=0
  constraints (19):
    c: Vertical(g0)
    c: Distance(g0) = 3
    c: Vertical(g1)
    c: Block(g1)
    c: Block(g2)
    c: Block(g3)
    c: Block(g0)
    c: Coincident(g4,g0)
    c: Coincident(g4,g2)
    c: Horizontal(g4)
    c: Coincident(g5,g0)
    c: Coincident(g5,g2)
    c: Horizontal(g5)
    c: Coincident(g6,g1)
    c: Coincident(g6,g3)
    c: Horizontal(g6)
    c: Coincident(g7,g1)
    c: Coincident(g7,g3)
    c: Horizontal(g7)
FEATURE [Part::Extrusion] Extrude024
  Base = -> Sketch033
  Dir = (1,0,0)
  DirMode = 2
  FaceMakerClass = Part::FaceMakerBullseye
  LengthFwd = 10
  LengthRev = 0
  Solid = true
  Symmetric = false
FEATURE [Part::Extrusion] Extrude025
  Base = -> Sketch034
  Dir = (1,0,0)
  DirMode = 2
  FaceMakerClass = Part::FaceMakerBullseye
  LengthFwd = 10
  LengthRev = 0
  Solid = true
  Symmetric = false
FEATURE [Part::Fillet] Fillet024  label="removeFromtMoreFrontCaseScrewRetainers"
  Base = -> Extrude024
  Edges = 4 edges r=1.49: [Edge6,Edge11,Edge18,Edge23]
  Placement = pos=(-11,0,0) rot=(0,0,1;0rad)
FEATURE [Part::Fillet] Fillet025  label="removeFromtMoreFrontCaseScrewRetainers001"
  Base = -> Extrude025
  Edges = 4 edges r=1.49: [Edge6,Edge11,Edge18,Edge23]
  Placement = pos=(-19,0,0) rot=(0,0,1;0rad)
FEATURE [Part::Cut] Cut022
  Base = -> Cut015
  Tool = -> Fillet025
FEATURE [Part::Cut] Cut023  label="screwRetainers"
  Base = -> Cut022
  Tool = -> Fillet024
FEATURE [Part::MultiFuse] Fusion056  label="bottom005"
  Shapes = -> [Fusion044,Cut021]
FEATURE [Part::MultiFuse] Fusion057  label="casePillars001"
  Shapes = -> [Cut016,Fusion052]
FEATURE [Part::MultiFuse] Fusion058  label="bottom006"
  Shapes = -> [Fusion056,Cut023]
FEATURE [Part::MultiFuse] Fusion059  label="bottom007"
  Shapes = -> [Fusion058,Fillet005]
FEATURE [Part::MultiFuse] Fusion060  label="bottom008"
  Shapes = -> [Fusion059,Fusion]
FEATURE [Part::MultiFuse] Fusion061  label="top011"
  Shapes = -> [Cut006,Cut020]
FEATURE [Part::MultiFuse] Fusion062  label="top012"
  Shapes = -> [Fusion057,Fusion061]
FEATURE [Sketcher::SketchObject] Sketch035  label="topSketch007"
  FullyConstrained = true
  sketch-geometry (6):
    g0: LineSegment StartX=19 StartY=38 StartZ=0 EndX=117 EndY=38 EndZ=0
    g1: ArcOfCircle CenterX=19 CenterY=19 CenterZ=0 NormalX=0 NormalY=0 NormalZ=1 AngleXU=0 Radius=19 StartAngle=1.5708 EndAngle=3.14159
    g2: LineSegment StartX=117 StartY=38 StartZ=0 EndX=117 EndY=19 EndZ=0
    g3: LineSegment StartX=98 StartY=1.0161e-12 StartZ=0 EndX=5.22862e-06 EndY=1.0161e-12 EndZ=0
    g4: LineSegment StartX=5.22862e-06 StartY=19 StartZ=0 EndX=5.22862e-06 EndY=1.0161e-12 EndZ=0
    g5: ArcOfCircle CenterX=98 CenterY=19 CenterZ=0 NormalX=0 NormalY=0 NormalZ=1 AngleXU=0 Radius=19 StartAngle=4.71239 EndAngle=6.28319
  constraints (16):
    c: Horizontal(g0)
    c: Distance(g0) = 98
    c: Coincident(g1,g0)
    c: Block(g1)
    c: Coincident(g2,g0)
    c: Vertical(g2)
    c: Distance(g2) = 19
    c: Horizontal(g3)
    c: Coincident(g4,g1)
    c: Vertical(g4)
    c: Coincident(g3,g4)
    c: Block(g3)
    c: Coincident(g5,g2)
    c: Coincident(g5,g3)
    c: Block(g0)
    c: Block(g5)
FEATURE [Part::Extrusion] Extrude026  label="sideA001"
  Base = -> Sketch035
  Dir = (0,0,1)
  DirMode = 2
  FaceMakerClass = Part::FaceMakerBullseye
  LengthFwd = 3
  LengthRev = 0
  Placement = pos=(0,0,-2.7) rot=(0,0,1;0rad)
  Solid = true
  Symmetric = false
FEATURE [Sketcher::SketchObject] Sketch036  label="topSketch008"
  FullyConstrained = true
  sketch-geometry (6):
    g0: LineSegment StartX=19 StartY=38 StartZ=0 EndX=117 EndY=38 EndZ=0
    g1: ArcOfCircle CenterX=19 CenterY=19 CenterZ=0 NormalX=0 NormalY=0 NormalZ=1 AngleXU=0 Radius=19 StartAngle=1.5708 EndAngle=3.14159
    g2: LineSegment StartX=117 StartY=38 StartZ=0 EndX=117 EndY=19 EndZ=0
    g3: LineSegment StartX=98 StartY=1.0161e-12 StartZ=0 EndX=5.22862e-06 EndY=1.0161e-12 EndZ=0
    g4: LineSegment StartX=5.22862e-06 StartY=19 StartZ=0 EndX=5.22862e-06 EndY=1.0161e-12 EndZ=0
    g5: ArcOfCircle CenterX=98 CenterY=19 CenterZ=0 NormalX=0 NormalY=0 NormalZ=1 AngleXU=0 Radius=19 StartAngle=4.71239 EndAngle=6.28319
  constraints (16):
    c: Horizontal(g0)
    c: Distance(g0) = 98
    c: Coincident(g1,g0)
    c: Block(g1)
    c: Coincident(g2,g0)
    c: Vertical(g2)
    c: Distance(g2) = 19
    c: Horizontal(g3)
    c: Coincident(g4,g1)
    c: Vertical(g4)
    c: Coincident(g3,g4)
    c: Block(g3)
    c: Coincident(g5,g2)
    c: Coincident(g5,g3)
    c: Block(g0)
    c: Block(g5)
FEATURE [Part::Extrusion] Extrude027  label="sideB001"
  Base = -> Sketch036
  Dir = (0,0,1)
  DirMode = 2
  FaceMakerClass = Part::FaceMakerBullseye
  LengthFwd = 3
  LengthRev = 0
  Placement = pos=(0,0,71.7) rot=(0,0,1;0rad)
  Solid = true
  Symmetric = false
FEATURE [Part::MultiFuse] Fusion064  label="removeFromBottom"
  Shapes = -> [Extrude026,Extrude027]
FEATURE [Part::Cut] Cut024  label="bottom009"
  Base = -> Fusion060
  Tool = -> Fusion064
FEATURE [Sketcher::SketchObject] Sketch037  label="topSketch009"
  FullyConstrained = true
  sketch-geometry (8):
    g0: ArcOfCircle CenterX=19 CenterY=19.1201 CenterZ=0 NormalX=0 NormalY=0 NormalZ=1 AngleXU=0 Radius=18.8799 StartAngle=1.5708 EndAngle=3.14793
    g1: LineSegment StartX=0.120501 StartY=19.0004 StartZ=0 EndX=0.120501 EndY=0.000382114 EndZ=0
    g2: LineSegment StartX=19 StartY=38 StartZ=0 EndX=124 EndY=38 EndZ=0
    g3: LineSegment StartX=0.120501 StartY=0.000382114 StartZ=0 EndX=105.121 EndY=0.000382114 EndZ=0
    g4: LineSegment StartX=124 StartY=38 StartZ=0 EndX=125.616 EndY=38 EndZ=0
    g5: LineSegment StartX=105.121 StartY=0.000382114 StartZ=0 EndX=106.736 EndY=0.000382114 EndZ=0
    g6: ArcOfCircle CenterX=106.616 CenterY=19 CenterZ=0 NormalX=0 NormalY=0 NormalZ=1 AngleXU=0 Radius=19 StartAngle=4.71873 EndAngle=6.28319
    g7: LineSegment StartX=125.616 StartY=38 StartZ=0 EndX=125.616 EndY=19 EndZ=0
  constraints (21):
    c: Block(g0)
    c: Coincident(g1,g0)
    c: Vertical(g1)
    c: Horizontal(g2)
    c: Distance(g2) = 105
    c: Coincident(g2,g0)
    c: Distance(g1) = 19
    c: Coincident(g3,g1)
    c: Horizontal(g3)
    c: Distance(g3) = 105
    c: Coincident(g4,g2)
    c: Horizontal(g4)
    c: Distance(g4) = 1.61553
    c: Horizontal(g5)
    c: Equal(g4,g5) = 1.61553
    c: Coincident(g5,g3)
    c: Block(g6)
    c: Coincident(g6,g5)
    c: Coincident(g7,g4)
    c: Coincident(g7,g6)
    c: Vertical(g7)
FEATURE [Part::Extrusion] Extrude028  label="sideB"
  Base = -> Sketch037
  Dir = (0,0,1)
  DirMode = 2
  FaceMakerClass = Part::FaceMakerBullseye
  LengthFwd = 3
  LengthRev = 0
  Placement = pos=(0,0,72) rot=(0,0,1;0rad)
  Solid = true
  Symmetric = false
FEATURE [Sketcher::SketchObject] Sketch038  label="topSketch010"
  FullyConstrained = true
  sketch-geometry (22):
    g0: LineSegment StartX=5.21097e-06 StartY=3 StartZ=0 EndX=5.21097e-06 EndY=19 EndZ=0
    g1: ArcOfCircle CenterX=19 CenterY=19 CenterZ=0 NormalX=0 NormalY=0 NormalZ=1 AngleXU=0 Radius=19 StartAngle=1.5708 EndAngle=3.14159
    g2: ArcOfCircle CenterX=19 CenterY=19 CenterZ=0 NormalX=0 NormalY=0 NormalZ=1 AngleXU=0 Radius=16 StartAngle=1.5708 EndAngle=3.14159
    g3: LineSegment StartX=114 StartY=35 StartZ=0 EndX=19 EndY=35 EndZ=0
    g4: LineSegment StartX=5.21097e-06 StartY=3 StartZ=0 EndX=5.21097e-06 EndY=0 EndZ=0
    g5: LineSegment StartX=3 StartY=0 StartZ=0 EndX=5.21097e-06 EndY=0 EndZ=0
    g6: LineSegment StartX=3 StartY=19 StartZ=0 EndX=3 EndY=0 EndZ=0
    g7: LineSegment StartX=19 StartY=38 StartZ=0 EndX=124 EndY=38 EndZ=0
    g8: Circle CenterX=119 CenterY=35 CenterZ=0 NormalX=0 NormalY=0 NormalZ=1 AngleXU=0 Radius=1
    g9: Circle CenterX=121 CenterY=35 CenterZ=0 NormalX=0 NormalY=0 NormalZ=1 AngleXU=0 Radius=1
    g10: Circle CenterX=121 CenterY=33 CenterZ=0 NormalX=0 NormalY=0 NormalZ=1 AngleXU=0 Radius=1
    g11: BSplineCurve PolesCount=3 KnotsCount=2 Degree=2 IsPeriodic=0
    g12: GeomPoint X=119 Y=35 Z=0
    g13: GeomPoint X=121 Y=33 Z=0
    g14: LineSegment StartX=119 StartY=35 StartZ=0 EndX=114 EndY=35 EndZ=0
    g15: ArcOfCircle CenterX=105 CenterY=19 CenterZ=0 NormalX=0 NormalY=0 NormalZ=1 AngleXU=0 Radius=16 StartAngle=5.60905 EndAngle=6.28319
    g16: LineSegment StartX=121 StartY=33 StartZ=0 EndX=121 EndY=19 EndZ=0
    g17: LineSegment StartX=117.5 StartY=9.01251 StartZ=0 EndX=121.163 EndY=9.0125 EndZ=0
    g18: ArcOfCircle CenterX=105 CenterY=19 CenterZ=0 NormalX=0 NormalY=0 NormalZ=1 AngleXU=0 Radius=20.6155 StartAngle=5.7297 EndAngle=6.28319
    g19: LineSegment StartX=121.163 StartY=9.0125 StartZ=0 EndX=122.538 EndY=8.16329 EndZ=0
    g20: LineSegment StartX=124 StartY=38 StartZ=0 EndX=125.616 EndY=38 EndZ=0
    g21: LineSegment StartX=125.616 StartY=19 StartZ=0 EndX=125.616 EndY=38 EndZ=0
  constraints (49):
    c: Vertical(g0)
    c: Block(g0)
    c: Coincident(g1,g0)
    c: Block(g1)
    c: Coincident(g2,g1)
    c: Block(g2)
    c: Coincident(g3,g2)
    c: Horizontal(g3)
    c: Tangent(g3,g2)
    c: Coincident(g4,g0)
    c: Distance(g4) = 3
    c: Vertical(g4)
    c: Coincident(g5,g4)
    c: Horizontal(g5)
    c: Coincident(g6,g2)
    c: Coincident(g6,g5)
    c: Vertical(g6)
    c: Horizontal(g7)
    c: Distance(g7) = 105
    c: Coincident(g7,g1)
    c: Block(g3)
    c: Weight(g8) = 1
    c: Equal(g8,g9)
    c: Equal(g8,g10)
    c: InternalAlignment(g8,g11)
    c: InternalAlignment(g9,g11)
    c: InternalAlignment(g10,g11)
    c: InternalAlignment(g12,g11)
    c: InternalAlignment(g13,g11)
    c: Block(g11)
    c: Coincident(g14,g11)
    c: Coincident(g14,g3)
    c: Horizontal(g14)
    c: Block(g15)
    c: Coincident(g16,g11)
    c: Coincident(g16,g15)
    c: Vertical(g16)
    c: Distance(g16) = 14
    c: Coincident(g17,g15)
    c: Block(g18)
    c: Coincident(g19,g18)
    c: Coincident(g20,g7)
    c: Horizontal(g20)
    c: Vertical(g21)
    c: Coincident(g20,g21)
    c: Block(g20)
    c: Block(g21)
    c: Block(g19)
    c: Block(g17)
FEATURE [Part::Extrusion] Extrude029
  Base = -> Sketch038
  Dir = (0,0,1)
  DirMode = 2
  FaceMakerClass = Part::FaceMakerBullseye
  LengthFwd = 72
  LengthRev = 0
  Solid = true
  Symmetric = false
FEATURE [Part::Feature] Face085
  shape: bbox 4.8 x 25.5 x 2e-07 mm, 1 faces, 0 solids (baked)
FEATURE [Part::Revolution] Revolve089  label="moreFrontCaseScrewPost003"
  Angle = 360
  Axis = (0,1,0)
  Base = (0,0,0)
  FaceMakerClass = Part::FaceMakerBullseye
  Placement = pos=(109.5,4.5,3.5) rot=(0,0,1;0rad)
  Solid = false
  Source = -> Face085
  Symmetric = false
FEATURE [Part::Feature] Face086
  shape: bbox 4.8 x 25.5 x 2e-07 mm, 1 faces, 0 solids (baked)
FEATURE [Part::Revolution] Revolve090  label="moreFrontCaseScrewPost004"
  Angle = 360
  Axis = (0,1,0)
  Base = (0,0,0)
  FaceMakerClass = Part::FaceMakerBullseye
  Placement = pos=(109.5,4.5,68.5) rot=(0,0,1;0rad)
  Solid = false
  Source = -> Face086
  Symmetric = false
FEATURE [Part::Fillet] Fillet026  label="top013"
  Base = -> Extrude029
  Edges = 1 edges r=2: [Edge35]
FEATURE [Sketcher::SketchObject] Sketch039
  FullyConstrained = true
  sketch-geometry (7):
    g0: LineSegment StartX=0 StartY=0 StartZ=0 EndX=0 EndY=6 EndZ=0
    g1: Circle CenterX=0 CenterY=0 CenterZ=0 NormalX=0 NormalY=0 NormalZ=1 AngleXU=0 Radius=1
    g2: Circle CenterX=8 CenterY=6 CenterZ=0 NormalX=0 NormalY=0 NormalZ=1 AngleXU=0 Radius=1
    g3: BSplineCurve PolesCount=3 KnotsCount=2 Degree=2 IsPeriodic=0
    g4: GeomPoint X=0 Y=0 Z=0
    g5: GeomPoint X=8 Y=6 Z=0
    g6: LineSegment StartX=0 StartY=6 StartZ=0 EndX=8 EndY=6 EndZ=0
  constraints (14):
    c: Coincident(g0,g-1)
    c: Distance(g0) = 6
    c: Vertical(g0)
    c: Coincident(g3,g0)
    c: Weight(g1) = 1
    c: Equal(g1,g2)
    c: InternalAlignment(g1,g3)
    c: InternalAlignment(g2,g3)
    c: InternalAlignment(g4,g3)
    c: InternalAlignment(g5,g3)
    c: Block(g3)
    c: Coincident(g6,g0)
    c: Coincident(g6,g3)
    c: Horizontal(g6)
FEATURE [Sketcher::SketchObject] Sketch040
  FullyConstrained = true
  sketch-geometry (7):
    g0: LineSegment StartX=0 StartY=0 StartZ=0 EndX=0 EndY=6 EndZ=0
    g1: Circle CenterX=0 CenterY=0 CenterZ=0 NormalX=0 NormalY=0 NormalZ=1 AngleXU=0 Radius=1
    g2: Circle CenterX=8 CenterY=6 CenterZ=0 NormalX=0 NormalY=0 NormalZ=1 AngleXU=0 Radius=1
    g3: BSplineCurve PolesCount=3 KnotsCount=2 Degree=2 IsPeriodic=0
    g4: GeomPoint X=0 Y=0 Z=0
    g5: GeomPoint X=8 Y=6 Z=0
    g6: LineSegment StartX=0 StartY=6 StartZ=0 EndX=8 EndY=6 EndZ=0
  constraints (14):
    c: Coincident(g0,g-1)
    c: Distance(g0) = 6
    c: Vertical(g0)
    c: Coincident(g3,g0)
    c: Weight(g1) = 1
    c: Equal(g1,g2)
    c: InternalAlignment(g1,g3)
    c: InternalAlignment(g2,g3)
    c: InternalAlignment(g4,g3)
    c: InternalAlignment(g5,g3)
    c: Block(g3)
    c: Coincident(g6,g0)
    c: Coincident(g6,g3)
    c: Horizontal(g6)
FEATURE [Sketcher::SketchObject] Sketch041
  FullyConstrained = true
  sketch-geometry (7):
    g0: LineSegment StartX=0 StartY=0 StartZ=0 EndX=0 EndY=6 EndZ=0
    g1: Circle CenterX=0 CenterY=0 CenterZ=0 NormalX=0 NormalY=0 NormalZ=1 AngleXU=0 Radius=1
    g2: Circle CenterX=8 CenterY=6 CenterZ=0 NormalX=0 NormalY=0 NormalZ=1 AngleXU=0 Radius=1
    g3: BSplineCurve PolesCount=3 KnotsCount=2 Degree=2 IsPeriodic=0
    g4: GeomPoint X=0 Y=0 Z=0
    g5: GeomPoint X=8 Y=6 Z=0
    g6: LineSegment StartX=0 StartY=6 StartZ=0 EndX=8 EndY=6 EndZ=0
  constraints (14):
    c: Coincident(g0,g-1)
    c: Distance(g0) = 6
    c: Vertical(g0)
    c: Coincident(g3,g0)
    c: Weight(g1) = 1
    c: Equal(g1,g2)
    c: InternalAlignment(g1,g3)
    c: InternalAlignment(g2,g3)
    c: InternalAlignment(g4,g3)
    c: InternalAlignment(g5,g3)
    c: Block(g3)
    c: Coincident(g6,g0)
    c: Coincident(g6,g3)
    c: Horizontal(g6)
FEATURE [Sketcher::SketchObject] Sketch042
  FullyConstrained = true
  sketch-geometry (7):
    g0: LineSegment StartX=0 StartY=0 StartZ=0 EndX=0 EndY=6 EndZ=0
    g1: Circle CenterX=0 CenterY=0 CenterZ=0 NormalX=0 NormalY=0 NormalZ=1 AngleXU=0 Radius=1
    g2: Circle CenterX=8 CenterY=6 CenterZ=0 NormalX=0 NormalY=0 NormalZ=1 AngleXU=0 Radius=1
    g3: BSplineCurve PolesCount=3 KnotsCount=2 Degree=2 IsPeriodic=0
    g4: GeomPoint X=0 Y=0 Z=0
    g5: GeomPoint X=8 Y=6 Z=0
    g6: LineSegment StartX=0 StartY=6 StartZ=0 EndX=8 EndY=6 EndZ=0
  constraints (14):
    c: Coincident(g0,g-1)
    c: Distance(g0) = 6
    c: Vertical(g0)
    c: Coincident(g3,g0)
    c: Weight(g1) = 1
    c: Equal(g1,g2)
    c: InternalAlignment(g1,g3)
    c: InternalAlignment(g2,g3)
    c: InternalAlignment(g4,g3)
    c: InternalAlignment(g5,g3)
    c: Block(g3)
    c: Coincident(g6,g0)
    c: Coincident(g6,g3)
    c: Horizontal(g6)
FEATURE [Part::Extrusion] Extrude030  label="caseScrewPillarBracket008"
  Base = -> Sketch039
  Dir = (0,0,1)
  DirMode = 2
  FaceMakerClass = Part::FaceMakerBullseye
  LengthFwd = 2.4
  LengthRev = 0
  Placement = pos=(15.76,29,8.8) rot=(0,1,0;0rad)
  Solid = true
  Symmetric = false
FEATURE [Part::Extrusion] Extrude031  label="caseScrewPillarBracket009"
  Base = -> Sketch040
  Dir = (0,0,1)
  DirMode = 2
  FaceMakerClass = Part::FaceMakerBullseye
  LengthFwd = 2.4
  LengthRev = 0
  Placement = pos=(15.76,29,60.8) rot=(0,0,1;0rad)
  Solid = true
  Symmetric = false
FEATURE [Part::Extrusion] Extrude032  label="caseScrewPillarBracket010"
  Base = -> Sketch041
  Dir = (0,0,1)
  DirMode = 2
  FaceMakerClass = Part::FaceMakerBullseye
  LengthFwd = 2.4
  LengthRev = 0
  Placement = pos=(13.7,29,13.26) rot=(0,-1,0;1.5708rad)
  Solid = true
  Symmetric = false
FEATURE [Part::Extrusion] Extrude033  label="caseScrewPillarBracket011"
  Base = -> Sketch042
  Dir = (0,0,1)
  DirMode = 2
  FaceMakerClass = Part::FaceMakerBullseye
  LengthFwd = 2.4
  LengthRev = 0
  Placement = pos=(11.3,29,58.74) rot=(0,1,0;1.5708rad)
  Solid = true
  Symmetric = false
FEATURE [Sketcher::SketchObject] Sketch043
  FullyConstrained = true
  sketch-geometry (7):
    g0: LineSegment StartX=0 StartY=0 StartZ=0 EndX=0 EndY=6 EndZ=0
    g1: Circle CenterX=0 CenterY=0 CenterZ=0 NormalX=0 NormalY=0 NormalZ=1 AngleXU=0 Radius=1
    g2: Circle CenterX=8 CenterY=6 CenterZ=0 NormalX=0 NormalY=0 NormalZ=1 AngleXU=0 Radius=1
    g3: BSplineCurve PolesCount=3 KnotsCount=2 Degree=2 IsPeriodic=0
    g4: GeomPoint X=0 Y=0 Z=0
    g5: GeomPoint X=8 Y=6 Z=0
    g6: LineSegment StartX=0 StartY=6 StartZ=0 EndX=8 EndY=6 EndZ=0
  constraints (14):
    c: Coincident(g0,g-1)
    c: Distance(g0) = 6
    c: Vertical(g0)
    c: Coincident(g3,g0)
    c: Weight(g1) = 1
    c: Equal(g1,g2)
    c: InternalAlignment(g1,g3)
    c: InternalAlignment(g2,g3)
    c: InternalAlignment(g4,g3)
    c: InternalAlignment(g5,g3)
    c: Block(g3)
    c: Coincident(g6,g0)
    c: Coincident(g6,g3)
    c: Horizontal(g6)
FEATURE [Part::Extrusion] Extrude034  label="caseScrewPillarBracket012"
  Base = -> Sketch043
  Dir = (0,0,1)
  DirMode = 2
  FaceMakerClass = Part::FaceMakerBullseye
  LengthFwd = 2.4
  LengthRev = 0
  Placement = pos=(88.3,29,65.23) rot=(0,1,0;1.5708rad)
  Solid = true
  Symmetric = false
FEATURE [Sketcher::SketchObject] Sketch044
  FullyConstrained = true
  sketch-geometry (7):
    g0: LineSegment StartX=0 StartY=0 StartZ=0 EndX=0 EndY=6 EndZ=0
    g1: Circle CenterX=0 CenterY=0 CenterZ=0 NormalX=0 NormalY=0 NormalZ=1 AngleXU=0 Radius=1
    g2: Circle CenterX=8 CenterY=6 CenterZ=0 NormalX=0 NormalY=0 NormalZ=1 AngleXU=0 Radius=1
    g3: BSplineCurve PolesCount=3 KnotsCount=2 Degree=2 IsPeriodic=0
    g4: GeomPoint X=0 Y=0 Z=0
    g5: GeomPoint X=8 Y=6 Z=0
    g6: LineSegment StartX=0 StartY=6 StartZ=0 EndX=8 EndY=6 EndZ=0
  constraints (14):
    c: Coincident(g0,g-1)
    c: Distance(g0) = 6
    c: Vertical(g0)
    c: Coincident(g3,g0)
    c: Weight(g1) = 1
    c: Equal(g1,g2)
    c: InternalAlignment(g1,g3)
    c: InternalAlignment(g2,g3)
    c: InternalAlignment(g4,g3)
    c: InternalAlignment(g5,g3)
    c: Block(g3)
    c: Coincident(g6,g0)
    c: Coincident(g6,g3)
    c: Horizontal(g6)
FEATURE [Part::Extrusion] Extrude035  label="caseScrewPillarBracket013"
  Base = -> Sketch044
  Dir = (0,0,1)
  DirMode = 2
  FaceMakerClass = Part::FaceMakerBullseye
  LengthFwd = 2.4
  LengthRev = 0
  Placement = pos=(90.7,29,6.77) rot=(0,-1,0;1.5708rad)
  Solid = true
  Symmetric = false
FEATURE [Sketcher::SketchObject] Sketch045
  FullyConstrained = true
  sketch-geometry (7):
    g0: LineSegment StartX=0 StartY=0 StartZ=0 EndX=0 EndY=6 EndZ=0
    g1: Circle CenterX=0 CenterY=0 CenterZ=0 NormalX=0 NormalY=0 NormalZ=1 AngleXU=0 Radius=1
    g2: Circle CenterX=8 CenterY=6 CenterZ=0 NormalX=0 NormalY=0 NormalZ=1 AngleXU=0 Radius=1
    g3: BSplineCurve PolesCount=3 KnotsCount=2 Degree=2 IsPeriodic=0
    g4: GeomPoint X=0 Y=0 Z=0
    g5: GeomPoint X=8 Y=6 Z=0
    g6: LineSegment StartX=0 StartY=6 StartZ=0 EndX=8 EndY=6 EndZ=0
  constraints (14):
    c: Coincident(g0,g-1)
    c: Distance(g0) = 6
    c: Vertical(g0)
    c: Coincident(g3,g0)
    c: Weight(g1) = 1
    c: Equal(g1,g2)
    c: InternalAlignment(g1,g3)
    c: InternalAlignment(g2,g3)
    c: InternalAlignment(g4,g3)
    c: InternalAlignment(g5,g3)
    c: Block(g3)
    c: Coincident(g6,g0)
    c: Coincident(g6,g3)
    c: Horizontal(g6)
FEATURE [Sketcher::SketchObject] Sketch046
  FullyConstrained = true
  sketch-geometry (7):
    g0: LineSegment StartX=0 StartY=0 StartZ=0 EndX=0 EndY=6 EndZ=0
    g1: Circle CenterX=0 CenterY=0 CenterZ=0 NormalX=0 NormalY=0 NormalZ=1 AngleXU=0 Radius=1
    g2: Circle CenterX=8 CenterY=6 CenterZ=0 NormalX=0 NormalY=0 NormalZ=1 AngleXU=0 Radius=1
    g3: BSplineCurve PolesCount=3 KnotsCount=2 Degree=2 IsPeriodic=0
    g4: GeomPoint X=0 Y=0 Z=0
    g5: GeomPoint X=8 Y=6 Z=0
    g6: LineSegment StartX=0 StartY=6 StartZ=0 EndX=8 EndY=6 EndZ=0
  constraints (14):
    c: Coincident(g0,g-1)
    c: Distance(g0) = 6
    c: Vertical(g0)
    c: Coincident(g3,g0)
    c: Weight(g1) = 1
    c: Equal(g1,g2)
    c: InternalAlignment(g1,g3)
    c: InternalAlignment(g2,g3)
    c: InternalAlignment(g4,g3)
    c: InternalAlignment(g5,g3)
    c: Block(g3)
    c: Coincident(g6,g0)
    c: Coincident(g6,g3)
    c: Horizontal(g6)
FEATURE [Part::Extrusion] Extrude036  label="caseScrewPillarBracket014"
  Base = -> Sketch045
  Dir = (0,0,1)
  DirMode = 2
  FaceMakerClass = Part::FaceMakerBullseye
  LengthFwd = 2.4
  LengthRev = 0
  Placement = pos=(110.7,29,6.77) rot=(0,-1,0;1.5708rad)
  Solid = true
  Symmetric = false
FEATURE [Part::Extrusion] Extrude037  label="caseScrewPillarBracket015"
  Base = -> Sketch046
  Dir = (0,0,1)
  DirMode = 2
  FaceMakerClass = Part::FaceMakerBullseye
  LengthFwd = 2.4
  LengthRev = 0
  Placement = pos=(108.3,29,65.23) rot=(0,1,0;1.5708rad)
  Solid = true
  Symmetric = false
FEATURE [Part::Box] Box013  label="frontCaseScrewPillarBracket002"
  AttacherType = Attacher::AttachEngine3D
  Height = 2.4
  Length = 22
  Placement = pos=(87,28,2.3) rot=(0,0,1;0rad)
  Width = 7
FEATURE [Part::Box] Box014  label="frontCaseScrewPillarBracket003"
  AttacherType = Attacher::AttachEngine3D
  Height = 2.4
  Length = 22
  Placement = pos=(87,28,67.3) rot=(0,0,1;0rad)
  Width = 7
FEATURE [Part::Feature] Face087
  shape: bbox 4.8 x 30.2 x 2e-07 mm, 1 faces, 0 solids (baked)
FEATURE [Part::Revolution] Revolve091  label="frontCaseScrewPost004"
  Angle = 360
  Axis = (0,1,0)
  Base = (0,0,0)
  FaceMakerClass = Part::FaceMakerBullseye
  Placement = pos=(89.5,4.5,3.5) rot=(0,0,1;0rad)
  Solid = false
  Source = -> Face087
  Symmetric = false
FEATURE [Part::Feature] Face088
  shape: bbox 4.8 x 30.2 x 2e-07 mm, 1 faces, 0 solids (baked)
FEATURE [Part::Revolution] Revolve092  label="frontCaseScrewPost005"
  Angle = 360
  Axis = (0,1,0)
  Base = (0,0,0)
  FaceMakerClass = Part::FaceMakerBullseye
  Placement = pos=(89.5,4.5,68.5) rot=(0,0,1;0rad)
  Solid = false
  Source = -> Face088
  Symmetric = false
FEATURE [Part::Feature] Face089
  shape: bbox 3.5 x 30.2 x 2e-07 mm, 1 faces, 0 solids (baked)
FEATURE [Part::Revolution] Revolve093  label="backCaseScrewPost002"
  Angle = 360
  Axis = (0,1,0)
  Base = (0,0,0)
  FaceMakerClass = Part::FaceMakerBullseye
  Placement = pos=(12.5,4.5,10) rot=(0,0,1;0rad)
  Solid = false
  Source = -> Face089
  Symmetric = false
FEATURE [Part::Feature] Face090
  shape: bbox 3.5 x 30.2 x 2e-07 mm, 1 faces, 0 solids (baked)
FEATURE [Part::Revolution] Revolve094  label="backCaseScrewPost003"
  Angle = 360
  Axis = (0,1,0)
  Base = (0,0,0)
  FaceMakerClass = Part::FaceMakerBullseye
  Placement = pos=(12.5,4.5,62) rot=(0,0,1;0rad)
  Solid = false
  Source = -> Face090
  Symmetric = false
FEATURE [Part::Box] Box015  label="Cube011"
  AttacherType = Attacher::AttachEngine3D
  Height = 28.8
  Length = 3
  Placement = pos=(107.3,28,21.6) rot=(0,0,1;0rad)
  Width = 7
FEATURE [Part::Box] Box016  label="Cube012"
  AttacherType = Attacher::AttachEngine3D
  Height = 3
  Length = 7.4
  Placement = pos=(107.3,28,18.6) rot=(0,0,1;0rad)
  Width = 7
FEATURE [Part::Box] Box017  label="Cube013"
  AttacherType = Attacher::AttachEngine3D
  Height = 3
  Length = 7.4
  Placement = pos=(107.3,28,50.4) rot=(0,0,1;0rad)
  Width = 7
FEATURE [Part::Cylinder] Cylinder024
  Angle = 360
  AttacherType = Attacher::AttachEngine3D
  Height = 20
  Placement = pos=(0,0,36.15) rot=(0,0,1;0rad)
  Radius = 14.3
FEATURE [Part::Cylinder] Cylinder025
  Angle = 360
  AttacherType = Attacher::AttachEngine3D
  Height = 10
  Placement = pos=(0,0,36.15) rot=(0,0,1;0rad)
  Radius = 4
FEATURE [Part::MultiFuse] Fusion066  label="removeToCreteHoleForPlugHousing009"
  Placement = pos=(70,19,36) rot=(0,1,0;1.5708rad)
  Shapes = -> [Cylinder024,Cylinder025]
FEATURE [Part::MultiFuse] Fusion065  label="plugHousingBracketHolder002"
  Shapes = -> [Box017,Box015,Box016]
FEATURE [Part::Cut] Cut025  label="plugHousingBracketHolder003"
  Base = -> Fusion065
  Placement = pos=(7,0,0) rot=(0,0,1;0rad)
  Tool = -> Fusion066
FEATURE [Sketcher::SketchObject] Sketch047
  FullyConstrained = false
  Placement = pos=(0,0,0) rot=(1,0,0;1.5708rad)
  sketch-geometry (24):
    g0: ArcOfCircle CenterX=-4 CenterY=-10.5 CenterZ=0 NormalX=0 NormalY=0 NormalZ=1 AngleXU=0 Radius=1.5 StartAngle=6e-16 EndAngle=3.14159
    g1: ArcOfCircle CenterX=-34.2 CenterY=-10.5 CenterZ=0 NormalX=0 NormalY=0 NormalZ=1 AngleXU=0 Radius=1.5 StartAngle=0 EndAngle=3.14159
    g2: ArcOfCircle CenterX=-34.2 CenterY=-27.7 CenterZ=0 NormalX=0 NormalY=0 NormalZ=1 AngleXU=0 Radius=1.5 StartAngle=3.14159 EndAngle=6.28319
    g3: ArcOfCircle CenterX=-4 CenterY=-27.7 CenterZ=0 NormalX=0 NormalY=0 NormalZ=1 AngleXU=0 Radius=1.5 StartAngle=3.1416 EndAngle=6.28319
    g4: ArcOfCircle CenterX=-10 CenterY=-4.3 CenterZ=0 NormalX=0 NormalY=0 NormalZ=1 AngleXU=0 Radius=1.5 StartAngle=2e-16 EndAngle=3.14159
    g5: ArcOfCircle CenterX=-16.1 CenterY=-1.8 CenterZ=0 NormalX=0 NormalY=0 NormalZ=1 AngleXU=0 Radius=1.5 StartAngle=5e-16 EndAngle=3.14159
    g6: ArcOfCircle CenterX=-22.1 CenterY=-1.8 CenterZ=0 NormalX=0 NormalY=0 NormalZ=1 AngleXU=0 Radius=1.5 StartAngle=5e-16 EndAngle=3.14159
    g7: ArcOfCircle CenterX=-28.2 CenterY=-4.3 CenterZ=0 NormalX=0 NormalY=0 NormalZ=1 AngleXU=0 Radius=1.5 StartAngle=2e-16 EndAngle=3.14159
    g8: ArcOfCircle CenterX=-10 CenterY=-33.9 CenterZ=0 NormalX=0 NormalY=0 NormalZ=1 AngleXU=0 Radius=1.5 StartAngle=3.14159 EndAngle=6.28319
    g9: ArcOfCircle CenterX=-16.1 CenterY=-36.4 CenterZ=0 NormalX=0 NormalY=0 NormalZ=1 AngleXU=0 Radius=1.5 StartAngle=3.14159 EndAngle=6.28319
    g10: ArcOfCircle CenterX=-22.1 CenterY=-36.4 CenterZ=0 NormalX=0 NormalY=0 NormalZ=1 AngleXU=0 Radius=1.5 StartAngle=3.14159 EndAngle=6.28319
    g11: ArcOfCircle CenterX=-28.2 CenterY=-33.9 CenterZ=0 NormalX=0 NormalY=0 NormalZ=1 AngleXU=0 Radius=1.5 StartAngle=3.14159 EndAngle=6.28319
    g12: LineSegment StartX=-35.7 StartY=-10.5 StartZ=0 EndX=-35.7 EndY=-27.7 EndZ=0
    g13: LineSegment StartX=-32.7 StartY=-10.5 StartZ=0 EndX=-32.7 EndY=-27.7 EndZ=0
    g14: LineSegment StartX=-29.7 StartY=-33.9 StartZ=0 EndX=-29.7 EndY=-4.3 EndZ=0
    g15: LineSegment StartX=-26.7 StartY=-33.9 StartZ=0 EndX=-26.7 EndY=-4.3 EndZ=0
    g16: LineSegment StartX=-2.5 StartY=-10.5 StartZ=0 EndX=-2.5 EndY=-27.7 EndZ=0
    g17: LineSegment StartX=-8.5 StartY=-4.3 StartZ=0 EndX=-8.5 EndY=-33.9 EndZ=0
    g18: LineSegment StartX=-5.5 StartY=-10.5 StartZ=0 EndX=-5.5 EndY=-27.7 EndZ=0
    g19: LineSegment StartX=-11.5 StartY=-4.3 StartZ=0 EndX=-11.5 EndY=-33.9 EndZ=0
    g20: LineSegment StartX=-14.6 StartY=-1.8 StartZ=0 EndX=-14.6 EndY=-36.4 EndZ=0
    g21: LineSegment StartX=-17.6 StartY=-1.8 StartZ=0 EndX=-17.6 EndY=-36.4 EndZ=0
    g22: LineSegment StartX=-20.6 StartY=-36.4 StartZ=0 EndX=-20.6 EndY=-1.8 EndZ=0
    g23: LineSegment StartX=-23.6 StartY=-1.8 StartZ=0 EndX=-23.6 EndY=-36.4 EndZ=0
  constraints (48):
    c: Block(g0)
    c: Block(g1)
    c: Block(g2)
    c: Block(g3)
    c: Block(g4)
    c: Block(g5)
    c: Block(g6)
    c: Block(g7)
    c: Block(g8)
    c: Block(g9)
    c: Block(g10)
    c: Block(g11)
    c: Coincident(g12,g1)
    c: Coincident(g12,g2)
    c: Vertical(g12)
    c: Coincident(g13,g1)
    c: Coincident(g13,g2)
    c: Vertical(g13)
    c: Coincident(g14,g11)
    c: Coincident(g14,g7)
    c: Vertical(g14)
    c: Coincident(g15,g11)
    c: Coincident(g15,g7)
    c: Vertical(g15)
    c: Coincident(g16,g0)
    c: Coincident(g16,g3)
    c: Vertical(g16)
    c: Coincident(g17,g4)
    c: Coincident(g17,g8)
    c: Vertical(g17)
    c: Coincident(g18,g0)
    c: Coincident(g18,g3)
    c: Vertical(g18)
    c: Coincident(g19,g4)
    c: Coincident(g19,g8)
    c: Vertical(g19)
    c: Coincident(g20,g5)
    c: Coincident(g20,g9)
    c: Vertical(g20)
    c: Coincident(g21,g5)
    c: Coincident(g21,g9)
    c: Vertical(g21)
    c: Coincident(g22,g10)
    c: Coincident(g22,g6)
    c: Vertical(g22)
    c: Coincident(g23,g6)
    c: Coincident(g23,g10)
    c: Vertical(g23)
FEATURE [Part::Extrusion] Extrude038  label="removeToCreateFanGrillHoles001"
  Base = -> Sketch047
  Dir = (0,-1,6e-16)
  DirMode = 2
  FaceMakerClass = Part::FaceMakerBullseye
  LengthFwd = 10
  LengthRev = 0
  Placement = pos=(65.4,44,54.82) rot=(0,0,1;0rad)
  Solid = true
  Symmetric = false
FEATURE [Part::Feature] Wire004
  shape: bbox 11 x 5.2 x 2e-07 mm, 0 faces, 0 solids (baked)
FEATURE [Part::Revolution] Revolve095
  Angle = 360
  Axis = (0,1,0)
  Base = (0,0,0)
  FaceMakerClass = Part::FaceMakerBullseye
  Placement = pos=(30.3,38,19.7) rot=(0,0,1;0rad)
  Solid = true
  Source = -> Wire004
  Symmetric = false
FEATURE [Part::Feature] Wire005
  shape: bbox 11 x 5.2 x 2e-07 mm, 0 faces, 0 solids (baked)
FEATURE [Part::Revolution] Revolve096
  Angle = 360
  Axis = (0,1,0)
  Base = (0,0,0)
  FaceMakerClass = Part::FaceMakerBullseye
  Placement = pos=(30.3,38,51.7) rot=(0,0,1;0rad)
  Solid = true
  Source = -> Wire005
  Symmetric = false
FEATURE [Part::Feature] Wire006
  shape: bbox 11 x 5.2 x 2e-07 mm, 0 faces, 0 solids (baked)
FEATURE [Part::Revolution] Revolve097
  Angle = 360
  Axis = (0,1,0)
  Base = (0,0,0)
  FaceMakerClass = Part::FaceMakerBullseye
  Placement = pos=(62.3,38,51.7) rot=(0,0,1;0rad)
  Solid = true
  Source = -> Wire006
  Symmetric = false
FEATURE [Part::Feature] Wire007
  shape: bbox 11 x 5.2 x 2e-07 mm, 0 faces, 0 solids (baked)
FEATURE [Part::Revolution] Revolve098
  Angle = 360
  Axis = (0,1,0)
  Base = (0,0,0)
  FaceMakerClass = Part::FaceMakerBullseye
  Placement = pos=(62.3,38,19.7) rot=(0,0,1;0rad)
  Solid = true
  Source = -> Wire007
  Symmetric = false
FEATURE [Part::MultiFuse] Fusion067  label="fanScrewHousing002"
  Shapes = -> [Revolve098,Revolve097,Revolve096,Revolve095]
FEATURE [Part::Feature] Face091 .. Face094  x4 (patterned run collapsed; names and placements below)
  shape: bbox 3.5 x 17.8 x 2e-07 mm, 1 faces, 0 solids (baked)
FEATURE [Part::Revolution] Revolve099  label="removeToCreateScrewAndThreadedInsertHole026"
  Angle = 360
  Axis = (0,1,0)
  Base = (0,0,0)
  FaceMakerClass = Part::FaceMakerBullseye
  Placement = pos=(62.3,30.3,19.7) rot=(0,0,1;0rad)
  Solid = false
  Source = -> Face091
  Symmetric = false
FEATURE [Part::Revolution] Revolve100  label="removeToCreateScrewAndThreadedInsertHole027"
  Angle = 360
  Axis = (0,1,0)
  Base = (0,0,0)
  FaceMakerClass = Part::FaceMakerBullseye
  Placement = pos=(62.3,30.3,51.7) rot=(0,0,1;0rad)
  Solid = false
  Source = -> Face092
  Symmetric = false
FEATURE [Part::Revolution] Revolve101  label="removeToCreateScrewAndThreadedInsertHole028"
  Angle = 360
  Axis = (0,1,0)
  Base = (0,0,0)
  FaceMakerClass = Part::FaceMakerBullseye
  Placement = pos=(30.3,30.3,19.7) rot=(0,0,1;0rad)
  Solid = false
  Source = -> Face093
  Symmetric = false
FEATURE [Part::Revolution] Revolve102  label="removeToCreateScrewAndThreadedInsertHole029"
  Angle = 360
  Axis = (0,1,0)
  Base = (0,0,0)
  FaceMakerClass = Part::FaceMakerBullseye
  Placement = pos=(30.3,30.3,51.7) rot=(0,0,1;0rad)
  Solid = false
  Source = -> Face094
  Symmetric = false
FEATURE [Part::MultiFuse] Fusion068  label="createThreadedInsertHolesForFan002"
  Shapes = -> [Revolve099,Revolve100,Revolve101,Revolve102]
FEATURE [Part::Cut] Cut026  label="fanScrewHousing003"
  Base = -> Fusion067
  Tool = -> Fusion068
FEATURE [Sketcher::SketchObject] Sketch048
  FullyConstrained = false
  Placement = pos=(0,0,0) rot=(1,0,0;1.5708rad)
  sketch-geometry (24):
    g0: ArcOfCircle CenterX=-4 CenterY=-10.5 CenterZ=0 NormalX=0 NormalY=0 NormalZ=1 AngleXU=0 Radius=1.5 StartAngle=6e-16 EndAngle=3.14159
    g1: ArcOfCircle CenterX=-34.2 CenterY=-10.5 CenterZ=0 NormalX=0 NormalY=0 NormalZ=1 AngleXU=0 Radius=1.5 StartAngle=0 EndAngle=3.14159
    g2: ArcOfCircle CenterX=-34.2 CenterY=-27.7 CenterZ=0 NormalX=0 NormalY=0 NormalZ=1 AngleXU=0 Radius=1.5 StartAngle=3.14159 EndAngle=6.28319
    g3: ArcOfCircle CenterX=-4 CenterY=-27.7 CenterZ=0 NormalX=0 NormalY=0 NormalZ=1 AngleXU=0 Radius=1.5 StartAngle=3.1416 EndAngle=6.28319
    g4: ArcOfCircle CenterX=-10 CenterY=-4.3 CenterZ=0 NormalX=0 NormalY=0 NormalZ=1 AngleXU=0 Radius=1.5 StartAngle=2e-16 EndAngle=3.14159
    g5: ArcOfCircle CenterX=-16.1 CenterY=-1.8 CenterZ=0 NormalX=0 NormalY=0 NormalZ=1 AngleXU=0 Radius=1.5 StartAngle=5e-16 EndAngle=3.14159
    g6: ArcOfCircle CenterX=-22.1 CenterY=-1.8 CenterZ=0 NormalX=0 NormalY=0 NormalZ=1 AngleXU=0 Radius=1.5 StartAngle=5e-16 EndAngle=3.14159
    g7: ArcOfCircle CenterX=-28.2 CenterY=-4.3 CenterZ=0 NormalX=0 NormalY=0 NormalZ=1 AngleXU=0 Radius=1.5 StartAngle=2e-16 EndAngle=3.14159
    g8: ArcOfCircle CenterX=-10 CenterY=-33.9 CenterZ=0 NormalX=0 NormalY=0 NormalZ=1 AngleXU=0 Radius=1.5 StartAngle=3.14159 EndAngle=6.28319
    g9: ArcOfCircle CenterX=-16.1 CenterY=-36.4 CenterZ=0 NormalX=0 NormalY=0 NormalZ=1 AngleXU=0 Radius=1.5 StartAngle=3.14159 EndAngle=6.28319
    g10: ArcOfCircle CenterX=-22.1 CenterY=-36.4 CenterZ=0 NormalX=0 NormalY=0 NormalZ=1 AngleXU=0 Radius=1.5 StartAngle=3.14159 EndAngle=6.28319
    g11: ArcOfCircle CenterX=-28.2 CenterY=-33.9 CenterZ=0 NormalX=0 NormalY=0 NormalZ=1 AngleXU=0 Radius=1.5 StartAngle=3.14159 EndAngle=6.28319
    g12: LineSegment StartX=-35.7 StartY=-10.5 StartZ=0 EndX=-35.7 EndY=-27.7 EndZ=0
    g13: LineSegment StartX=-32.7 StartY=-10.5 StartZ=0 EndX=-32.7 EndY=-27.7 EndZ=0
    g14: LineSegment StartX=-29.7 StartY=-33.9 StartZ=0 EndX=-29.7 EndY=-4.3 EndZ=0
    g15: LineSegment StartX=-26.7 StartY=-33.9 StartZ=0 EndX=-26.7 EndY=-4.3 EndZ=0
    g16: LineSegment StartX=-2.5 StartY=-10.5 StartZ=0 EndX=-2.5 EndY=-27.7 EndZ=0
    g17: LineSegment StartX=-8.5 StartY=-4.3 StartZ=0 EndX=-8.5 EndY=-33.9 EndZ=0
    g18: LineSegment StartX=-5.5 StartY=-10.5 StartZ=0 EndX=-5.5 EndY=-27.7 EndZ=0
    g19: LineSegment StartX=-11.5 StartY=-4.3 StartZ=0 EndX=-11.5 EndY=-33.9 EndZ=0
    g20: LineSegment StartX=-14.6 StartY=-1.8 StartZ=0 EndX=-14.6 EndY=-36.4 EndZ=0
    g21: LineSegment StartX=-17.6 StartY=-1.8 StartZ=0 EndX=-17.6 EndY=-36.4 EndZ=0
    g22: LineSegment StartX=-20.6 StartY=-36.4 StartZ=0 EndX=-20.6 EndY=-1.8 EndZ=0
    g23: LineSegment StartX=-23.6 StartY=-1.8 StartZ=0 EndX=-23.6 EndY=-36.4 EndZ=0
  constraints (48):
    c: Block(g0)
    c: Block(g1)
    c: Block(g2)
    c: Block(g3)
    c: Block(g4)
    c: Block(g5)
    c: Block(g6)
    c: Block(g7)
    c: Block(g8)
    c: Block(g9)
    c: Block(g10)
    c: Block(g11)
    c: Coincident(g12,g1)
    c: Coincident(g12,g2)
    c: Vertical(g12)
    c: Coincident(g13,g1)
    c: Coincident(g13,g2)
    c: Vertical(g13)
    c: Coincident(g14,g11)
    c: Coincident(g14,g7)
    c: Vertical(g14)
    c: Coincident(g15,g11)
    c: Coincident(g15,g7)
    c: Vertical(g15)
    c: Coincident(g16,g0)
    c: Coincident(g16,g3)
    c: Vertical(g16)
    c: Coincident(g17,g4)
    c: Coincident(g17,g8)
    c: Vertical(g17)
    c: Coincident(g18,g0)
    c: Coincident(g18,g3)
    c: Vertical(g18)
    c: Coincident(g19,g4)
    c: Coincident(g19,g8)
    c: Vertical(g19)
    c: Coincident(g20,g5)
    c: Coincident(g20,g9)
    c: Vertical(g20)
    c: Coincident(g21,g5)
    c: Coincident(g21,g9)
    c: Vertical(g21)
    c: Coincident(g22,g10)
    c: Coincident(g22,g6)
    c: Vertical(g22)
    c: Coincident(g23,g6)
    c: Coincident(g23,g10)
    c: Vertical(g23)
FEATURE [Part::Extrusion] Extrude039  label="removeToCreateFanGrillHoles002"
  Base = -> Sketch048
  Dir = (0,-1,6e-16)
  DirMode = 2
  FaceMakerClass = Part::FaceMakerBullseye
  LengthFwd = 10
  LengthRev = 0
  Placement = pos=(65.4,44,54.82) rot=(0,0,1;0rad)
  Solid = true
  Symmetric = false
FEATURE [Part::Cut] Cut027  label="fanScrewHousing004"
  Base = -> Cut026
  Tool = -> Extrude038
FEATURE [Part::Cut] Cut028  label="top014"
  Base = -> Fillet026
  Tool = -> Extrude039
FEATURE [Part::Feature] Face095 .. Face098  x4 (patterned run collapsed; names and placements below)
  shape: bbox 3.5 x 17.8 x 2e-07 mm, 1 faces, 0 solids (baked)
FEATURE [Part::Revolution] Revolve103  label="removeToCreateScrewAndThreadedInsertHole030"
  Angle = 360
  Axis = (0,1,0)
  Base = (0,0,0)
  FaceMakerClass = Part::FaceMakerBullseye
  Placement = pos=(62.3,30.3,19.7) rot=(0,0,1;0rad)
  Solid = false
  Source = -> Face095
  Symmetric = false
FEATURE [Part::Revolution] Revolve104  label="removeToCreateScrewAndThreadedInsertHole031"
  Angle = 360
  Axis = (0,1,0)
  Base = (0,0,0)
  FaceMakerClass = Part::FaceMakerBullseye
  Placement = pos=(62.3,30.3,51.7) rot=(0,0,1;0rad)
  Solid = false
  Source = -> Face096
  Symmetric = false
FEATURE [Part::Revolution] Revolve105  label="removeToCreateScrewAndThreadedInsertHole032"
  Angle = 360
  Axis = (0,1,0)
  Base = (0,0,0)
  FaceMakerClass = Part::FaceMakerBullseye
  Placement = pos=(30.3,30.3,19.7) rot=(0,0,1;0rad)
  Solid = false
  Source = -> Face097
  Symmetric = false
FEATURE [Part::Revolution] Revolve106  label="removeToCreateScrewAndThreadedInsertHole033"
  Angle = 360
  Axis = (0,1,0)
  Base = (0,0,0)
  FaceMakerClass = Part::FaceMakerBullseye
  Placement = pos=(30.3,30.3,51.7) rot=(0,0,1;0rad)
  Solid = false
  Source = -> Face098
  Symmetric = false
FEATURE [Part::MultiFuse] Fusion069  label="createThreadedInsertHolesForFan003"
  Shapes = -> [Revolve103,Revolve104,Revolve105,Revolve106]
FEATURE [Part::Cut] Cut029  label="top015"
  Base = -> Cut028
  Tool = -> Fusion054
FEATURE [Part::Cut] Cut030  label="fanScrewHousing005"
  Base = -> Cut027
  Tool = -> Fusion069
FEATURE [Part::Cylinder] Cylinder026  label="removeToCreteHoleForPlugHousing010"
  Angle = 360
  AttacherType = Attacher::AttachEngine3D
  Height = 20
  Placement = pos=(-2,19,36) rot=(0,1,0;1.5708rad)
  Radius = 14.3
FEATURE [Part::Box] Box018  label="removeToCreteHoleForPlugHousing011"
  AttacherType = Attacher::AttachEngine3D
  Height = 28.6
  Length = 10
  Placement = pos=(-2,0,21.7) rot=(0,0,1;0rad)
  Width = 19
FEATURE [Part::Box] Box019  label="wireHolderBottomCaseBit"
  AttacherType = Attacher::AttachEngine3D
  Height = 28
  Length = 3
  Placement = pos=(0,0,22) rot=(0,0,1;0rad)
  Width = 21
FEATURE [Part::Cylinder] Cylinder027  label="removeToCreteHoleForPlugHousing012"
  Angle = 360
  AttacherType = Attacher::AttachEngine3D
  Height = 20
  Placement = pos=(-2,19,36) rot=(0,1,0;1.5708rad)
  Radius = 14.3
FEATURE [Part::Cut] Cut031  label="wireHolderBottomCaseBit001"
  Base = -> Box019
  Tool = -> Cylinder027
FEATURE [Part::MultiFuse] Fusion070  label="removeToCreteHoleForPlugHousing013"
  Shapes = -> [Box018,Cylinder026]
FEATURE [Part::Cut] Cut032  label="top016"
  Base = -> Cut029
  Tool = -> Fusion070
FEATURE [Part::Cylinder] Cylinder028
  Angle = 360
  AttacherType = Attacher::AttachEngine3D
  Height = 20
  Placement = pos=(0,0,36.15) rot=(0,0,1;0rad)
  Radius = 14.3
FEATURE [Part::Cylinder] Cylinder029
  Angle = 360
  AttacherType = Attacher::AttachEngine3D
  Height = 10
  Placement = pos=(0,0,36.15) rot=(0,0,1;0rad)
  Radius = 4
FEATURE [Part::MultiFuse] Fusion071  label="removeToCreteHoleForPlugHousing014"
  Placement = pos=(70,19,36) rot=(0,1,0;1.5708rad)
  Shapes = -> [Cylinder028,Cylinder029]
FEATURE [Sketcher::SketchObject] Sketch049  label="topSketch011"
  FullyConstrained = true
  sketch-geometry (4):
    g0: ArcOfCircle CenterX=105 CenterY=19 CenterZ=0 NormalX=0 NormalY=0 NormalZ=1 AngleXU=0 Radius=20.6155 StartAngle=5.54125 EndAngle=6.28319
    g1: ArcOfCircle CenterX=105 CenterY=19 CenterZ=0 NormalX=0 NormalY=0 NormalZ=1 AngleXU=0 Radius=13 StartAngle=5.54125 EndAngle=6.28319
    g2: LineSegment StartX=118 StartY=19 StartZ=0 EndX=125.616 EndY=19 EndZ=0
    g3: LineSegment StartX=114.583 StartY=10.2157 StartZ=0 EndX=120.197 EndY=5.06982 EndZ=0
  constraints (7):
    c: Block(g0)
    c: Block(g1)
    c: Coincident(g2,g1)
    c: Coincident(g2,g0)
    c: Horizontal(g2)
    c: Coincident(g3,g1)
    c: Coincident(g3,g0)
FEATURE [Part::Box] Box020  label="removeToCreteHoleForPlugHousing015"
  AttacherType = Attacher::AttachEngine3D
  Height = 28.6
  Length = 20
  Placement = pos=(106.15,0,21.7) rot=(0,0,1;0rad)
  Width = 19
FEATURE [Part::MultiFuse] Fusion072  label="removeToCreteHoleForPlugHousing016"
  Shapes = -> [Box020,Fusion071]
FEATURE [Part::Cut] Cut033  label="removeToCreteHoleForPlugHousing017"
  Base = -> Cut032
  Tool = -> Fusion072
FEATURE [Part::Cylinder] Cylinder030
  Angle = 360
  AttacherType = Attacher::AttachEngine3D
  Height = 20
  Placement = pos=(0,0,36.15) rot=(0,0,1;0rad)
  Radius = 14.3
FEATURE [Part::Cylinder] Cylinder031
  Angle = 360
  AttacherType = Attacher::AttachEngine3D
  Height = 10
  Placement = pos=(0,0,36.15) rot=(0,0,1;0rad)
  Radius = 4
FEATURE [Part::Box] Box021  label="removeToCreteHoleForPlugHousing019"
  AttacherType = Attacher::AttachEngine3D
  Height = 28.6
  Length = 20
  Placement = pos=(106.15,0,21.7) rot=(0,0,1;0rad)
  Width = 19
FEATURE [Part::MultiFuse] Fusion074  label="removeToCreteHoleForPlugHousing020"
  Placement = pos=(70,19,36) rot=(0,1,0;1.5708rad)
  Shapes = -> [Cylinder030,Cylinder031]
FEATURE [Part::MultiFuse] Fusion073  label="removeToCreteHoleForPlugHousing018"
  Placement = pos=(0,0,28.3) rot=(0,0,1;0rad)
  Shapes = -> [Box021,Fusion074]
FEATURE [Part::Cylinder] Cylinder032
  Angle = 360
  AttacherType = Attacher::AttachEngine3D
  Height = 20
  Placement = pos=(0,0,36.15) rot=(0,0,1;0rad)
  Radius = 14.3
FEATURE [Part::Cylinder] Cylinder033
  Angle = 360
  AttacherType = Attacher::AttachEngine3D
  Height = 10
  Placement = pos=(0,0,36.15) rot=(0,0,1;0rad)
  Radius = 4
FEATURE [Part::Box] Box022  label="removeToCreteHoleForPlugHousing021"
  AttacherType = Attacher::AttachEngine3D
  Height = 28.6
  Length = 20
  Placement = pos=(106.15,0,21.7) rot=(0,0,1;0rad)
  Width = 19
FEATURE [Part::MultiFuse] Fusion076  label="removeToCreteHoleForPlugHousing023"
  Placement = pos=(70,19,36) rot=(0,1,0;1.5708rad)
  Shapes = -> [Cylinder032,Cylinder033]
FEATURE [Part::MultiFuse] Fusion075  label="removeToCreteHoleForPlugHousing022"
  Placement = pos=(0,0,-28.3) rot=(0,0,1;0rad)
  Shapes = -> [Box022,Fusion076]
FEATURE [Part::MultiFuse] Fusion077  label="removeToCreatePlugHousingBottomBit"
  Shapes = -> [Fusion075,Fusion073]
FEATURE [Part::Cylinder] Cylinder034
  Angle = 360
  AttacherType = Attacher::AttachEngine3D
  Height = 20
  Placement = pos=(0,0,36.15) rot=(0,0,1;0rad)
  Radius = 14
FEATURE [Part::Cylinder] Cylinder035
  Angle = 360
  AttacherType = Attacher::AttachEngine3D
  Height = 10
  Placement = pos=(0,0,36.15) rot=(0,0,1;0rad)
  Radius = 4
FEATURE [Part::MultiFuse] Fusion078  label="removeToCreteHoleForPlugHousing024"
  Placement = pos=(70,19,36) rot=(0,1,0;1.5708rad)
  Shapes = -> [Cylinder034,Cylinder035]
FEATURE [Part::MultiFuse] Fusion079  label="removeToCreatePlugHousingBottomBit001"
  Shapes = -> [Fusion078,Fusion077]
FEATURE [Part::Extrusion] Extrude040  label="bottomPlugHousingBit"
  Base = -> Sketch049
  Dir = (0,0,1)
  DirMode = 2
  FaceMakerClass = Part::FaceMakerBullseye
  LengthFwd = 72
  LengthRev = 0
  Solid = true
  Symmetric = false
FEATURE [Part::Cut] Cut034  label="bottomPlugHousingBit001"
  Base = -> Extrude040
  Placement = pos=(-0.09,0,0) rot=(0,0,1;0rad)
  Tool = -> Fusion079
FEATURE [Part::Box] Box023  label="Cube014"
  AttacherType = Attacher::AttachEngine3D
  Height = 16
  Length = 8
  Placement = pos=(12.7,31.52,28) rot=(0,0,1;0rad)
  Width = 4
FEATURE [Part::Cylinder] Cylinder036
  Angle = 360
  AttacherType = Attacher::AttachEngine3D
  Height = 10
  Placement = pos=(0,0,36.15) rot=(0,0,1;0rad)
  Radius = 4
FEATURE [Part::Cylinder] Cylinder037
  Angle = 360
  AttacherType = Attacher::AttachEngine3D
  Height = 20
  Placement = pos=(0,0,36.15) rot=(0,0,1;0rad)
  Radius = 8.2
FEATURE [Part::MultiFuse] Fusion080  label="removeToCreteHoleForPlugHousing025"
  Placement = pos=(-42,19,36) rot=(0,1,0;1.5708rad)
  Shapes = -> [Cylinder037,Cylinder036]
FEATURE [Sketcher::SketchObject] Sketch050  label="topSketch012"
  FullyConstrained = true
  sketch-geometry (4):
    g0: LineSegment StartX=16.8446 StartY=31.512 StartZ=0 EndX=16.3251 EndY=34.4666 EndZ=0
    g1: ArcOfCircle CenterX=19 CenterY=19.2524 CenterZ=0 NormalX=0 NormalY=0 NormalZ=1 AngleXU=0 Radius=15.4476 StartAngle=1.74483 EndAngle=2.72717
    g2: ArcOfCircle CenterX=19 CenterY=19.2524 CenterZ=0 NormalX=0 NormalY=0 NormalZ=1 AngleXU=0 Radius=12.4476 StartAngle=1.74483 EndAngle=2.73189
    g3: LineSegment StartX=4.86004 StartY=25.4725 StartZ=0 EndX=7.58253 EndY=24.2107 EndZ=0
  constraints (7):
    c: Block(g0)
    c: Coincident(g1,g0)
    c: Coincident(g2,g0)
    c: Coincident(g3,g1)
    c: Coincident(g3,g2)
    c: Block(g1)
    c: Block(g2)
FEATURE [Part::Extrusion] Extrude041
  Base = -> Sketch050
  Dir = (0,0,1)
  DirMode = 2
  FaceMakerClass = Part::FaceMakerBullseye
  LengthFwd = 10.6
  LengthRev = 0
  Placement = pos=(0,0,31) rot=(0,0,1;0rad)
  Solid = true
  Symmetric = false
FEATURE [Part::Cut] Cut035
  Base = -> Extrude041
  Placement = pos=(0,0,-0.3) rot=(0,0,1;0rad)
  Tool = -> Fusion080
FEATURE [Part::Cut] Cut036
  Base = -> Box023
  Tool = -> Cut035
FEATURE [Part::Fillet] Fillet027
  Base = -> Cut036
  Edges = 1 edges r=0.7: [Edge13]
FEATURE [Part::Fillet] Fillet028
  Base = -> Fillet027
  Edges = 1 edges r=0.7: [Edge13]
FEATURE [Part::Fillet] Fillet029
  Base = -> Fillet028
  Edges = 1 edges r=0.7: [Edge16]
FEATURE [Part::Fillet] Fillet030
  Base = -> Fillet029
  Edges = 1 edges r=0.7: [Edge11]
FEATURE [Part::Fillet] Fillet031
  Base = -> Fillet030
  Edges = 1 edges r=0.7: [Edge10]
FEATURE [Part::Fillet] Fillet032
  Base = -> Fillet031
  Edges = 1 edges r=1.2: [Edge5]
FEATURE [Part::Fillet] Fillet033
  Base = -> Fillet032
  Edges = 1 edges r=1.2: [Edge12]
FEATURE [Part::Fillet] Fillet034  label="wireHousingRetainer"
  Base = -> Fillet033
  Edges = 1 edges r=2: [Edge1]
  Placement = pos=(0.3,0,0) rot=(0,0,1;0rad)
FEATURE [Part::Feature] Face099
  shape: bbox 3.5 x 17.8 x 2e-07 mm, 1 faces, 0 solids (baked)
FEATURE [Part::Revolution] Revolve107  label="removeToCreateScrewAndThreadedInsertHole034"
  Angle = 360
  Axis = (0,1,0)
  Base = (0,0,0)
  FaceMakerClass = Part::FaceMakerBullseye
  Placement = pos=(12.5,0,10) rot=(0,0,1;0rad)
  Solid = false
  Source = -> Face099
  Symmetric = false
FEATURE [Part::Feature] Face100
  shape: bbox 3.5 x 17.8 x 2e-07 mm, 1 faces, 0 solids (baked)
FEATURE [Part::Revolution] Revolve108  label="removeToCreateScrewAndThreadedInsertHole035"
  Angle = 360
  Axis = (0,1,0)
  Base = (0,0,0)
  FaceMakerClass = Part::FaceMakerBullseye
  Placement = pos=(12.5,0,62) rot=(0,0,1;0rad)
  Solid = false
  Source = -> Face100
  Symmetric = false
FEATURE [Part::Feature] Face101
  shape: bbox 3.5 x 17.8 x 2e-07 mm, 1 faces, 0 solids (baked)
FEATURE [Part::Revolution] Revolve109  label="removeToCreateScrewAndThreadedInsertHole036"
  Angle = 360
  Axis = (0,1,0)
  Base = (0,0,0)
  FaceMakerClass = Part::FaceMakerBullseye
  Placement = pos=(89.5,0,68.5) rot=(0,0,1;0rad)
  Solid = false
  Source = -> Face101
  Symmetric = false
FEATURE [Part::Feature] Face102
  shape: bbox 3.5 x 17.8 x 2e-07 mm, 1 faces, 0 solids (baked)
FEATURE [Part::Revolution] Revolve110  label="removeToCreateScrewAndThreadedInsertHole037"
  Angle = 360
  Axis = (0,1,0)
  Base = (0,0,0)
  FaceMakerClass = Part::FaceMakerBullseye
  Placement = pos=(89.5,0,3.5) rot=(0,0,1;0rad)
  Solid = false
  Source = -> Face102
  Symmetric = false
FEATURE [Part::Feature] Face103
  shape: bbox 3.5 x 17.8 x 2e-07 mm, 1 faces, 0 solids (baked)
FEATURE [Part::Revolution] Revolve111  label="removeToCreateScrewAndThreadedInsertHole038"
  Angle = 360
  Axis = (0,1,0)
  Base = (0,0,0)
  FaceMakerClass = Part::FaceMakerBullseye
  Placement = pos=(109.5,4.7,3.5) rot=(0,0,1;0rad)
  Solid = false
  Source = -> Face103
  Symmetric = false
FEATURE [Part::Feature] Face104
  shape: bbox 3.5 x 17.8 x 2e-07 mm, 1 faces, 0 solids (baked)
FEATURE [Part::Revolution] Revolve112  label="removeToCreateScrewAndThreadedInsertHole039"
  Angle = 360
  Axis = (0,1,0)
  Base = (0,0,0)
  FaceMakerClass = Part::FaceMakerBullseye
  Placement = pos=(109.5,4.7,68.5) rot=(0,0,1;0rad)
  Solid = false
  Source = -> Face104
  Symmetric = false
FEATURE [Part::MultiFuse] Fusion081  label="removeToCreateScrewAndThreadedInsertHole040"
  Shapes = -> [Revolve107,Revolve108,Revolve109,Revolve110,Revolve111,Revolve112]
FEATURE [Part::MultiFuse] Fusion082  label="casePillars002"
  Shapes = -> [Revolve094,Revolve092,Revolve090,Revolve089,Revolve091,Revolve093]
FEATURE [Part::Cut] Cut037  label="casePillars003"
  Base = -> Fusion082
  Tool = -> Fusion081
FEATURE [Sketcher::SketchObject] Sketch051
  FullyConstrained = true
  Placement = pos=(117,19,0) rot=(0.57735,0.57735,0.57735;2.0944rad)
  sketch-geometry (48):
    g0: LineSegment StartX=-49.19 StartY=69.25 StartZ=0 EndX=-49.19 EndY=66.25 EndZ=0
    g1: LineSegment StartX=-49.19 StartY=63.5 StartZ=0 EndX=-49.19 EndY=60.5 EndZ=0
    g2: LineSegment StartX=-49.19 StartY=57.75 StartZ=0 EndX=-49.19 EndY=54.75 EndZ=0
    g3: LineSegment StartX=-49.19 StartY=52 StartZ=0 EndX=-49.19 EndY=49 EndZ=0
    g4: LineSegment StartX=-49.19 StartY=46.25 StartZ=0 EndX=-49.19 EndY=43.25 EndZ=0
    g5: LineSegment StartX=-49.19 StartY=40.5 StartZ=0 EndX=-49.19 EndY=37.5 EndZ=0
    g6: LineSegment StartX=-49.19 StartY=34.5 StartZ=0 EndX=-49.19 EndY=31.5 EndZ=0
    g7: LineSegment StartX=-49.19 StartY=28.75 StartZ=0 EndX=-49.19 EndY=25.75 EndZ=0
    g8: LineSegment StartX=-49.19 StartY=23 StartZ=0 EndX=-49.19 EndY=20 EndZ=0
    g9: LineSegment StartX=-49.19 StartY=17.25 StartZ=0 EndX=-49.19 EndY=14.25 EndZ=0
    g10: LineSegment StartX=-49.19 StartY=11.5 StartZ=0 EndX=-49.19 EndY=8.5 EndZ=0
    g11: LineSegment StartX=-49.19 StartY=5.75 StartZ=0 EndX=-49.19 EndY=2.75 EndZ=0
    g12: ArcOfCircle CenterX=-1.5 CenterY=67.75 CenterZ=0 NormalX=0 NormalY=0 NormalZ=1 AngleXU=0 Radius=1.5 StartAngle=4.71239 EndAngle=7.85398
    g13: ArcOfCircle CenterX=-1.5 CenterY=62 CenterZ=0 NormalX=0 NormalY=0 NormalZ=1 AngleXU=0 Radius=1.5 StartAngle=4.71239 EndAngle=7.85398
    g14: ArcOfCircle CenterX=-1.5 CenterY=56.25 CenterZ=0 NormalX=0 NormalY=0 NormalZ=1 AngleXU=0 Radius=1.5 StartAngle=4.71239 EndAngle=7.85398
    g15: ArcOfCircle CenterX=-11.49 CenterY=50.5 CenterZ=0 NormalX=0 NormalY=0 NormalZ=1 AngleXU=0 Radius=1.5 StartAngle=4.71239 EndAngle=7.85398
    g16: ArcOfCircle CenterX=-16.28 CenterY=44.75 CenterZ=0 NormalX=0 NormalY=0 NormalZ=1 AngleXU=0 Radius=1.5 StartAngle=4.71239 EndAngle=7.85398
    g17: ArcOfCircle CenterX=-18.2337 CenterY=39 CenterZ=0 NormalX=0 NormalY=0 NormalZ=1 AngleXU=0 Radius=1.5 StartAngle=4.71485 EndAngle=7.85398
    g18: ArcOfCircle CenterX=-16.2837 CenterY=27.25 CenterZ=0 NormalX=0 NormalY=0 NormalZ=1 AngleXU=0 Radius=1.5 StartAngle=4.71485 EndAngle=7.85398
    g19: ArcOfCircle CenterX=-18.2337 CenterY=33 CenterZ=0 NormalX=0 NormalY=0 NormalZ=1 AngleXU=0 Radius=1.5 StartAngle=4.71485 EndAngle=7.85398
    g20: ArcOfCircle CenterX=-11.49 CenterY=21.5 CenterZ=0 NormalX=0 NormalY=0 NormalZ=1 AngleXU=0 Radius=1.5 StartAngle=4.71239 EndAngle=7.85398
    g21: ArcOfCircle CenterX=-1.5 CenterY=4.25 CenterZ=0 NormalX=0 NormalY=0 NormalZ=1 AngleXU=0 Radius=1.5 StartAngle=4.71239 EndAngle=7.85398
    g22: ArcOfCircle CenterX=-1.5 CenterY=10 CenterZ=0 NormalX=0 NormalY=0 NormalZ=1 AngleXU=0 Radius=1.5 StartAngle=4.71239 EndAngle=7.85398
    g23: ArcOfCircle CenterX=-1.5 CenterY=15.75 CenterZ=0 NormalX=0 NormalY=0 NormalZ=1 AngleXU=0 Radius=1.5 StartAngle=4.71239 EndAngle=7.85398
    g24: LineSegment StartX=-49.19 StartY=69.25 StartZ=0 EndX=-1.5 EndY=69.25 EndZ=0
    g25: LineSegment StartX=-49.19 StartY=66.25 StartZ=0 EndX=-1.5 EndY=66.25 EndZ=0
    g26: LineSegment StartX=-49.19 StartY=63.5 StartZ=0 EndX=-1.5 EndY=63.5 EndZ=0
    g27: LineSegment StartX=-49.19 StartY=60.5 StartZ=0 EndX=-1.5 EndY=60.5 EndZ=0
    g28: LineSegment StartX=-49.19 StartY=57.75 StartZ=0 EndX=-1.5 EndY=57.75 EndZ=0
    g29: LineSegment StartX=-49.19 StartY=54.75 StartZ=0 EndX=-1.5 EndY=54.75 EndZ=0
    g30: LineSegment StartX=-49.19 StartY=52 StartZ=0 EndX=-11.49 EndY=52 EndZ=0
    g31: LineSegment StartX=-49.19 StartY=49 StartZ=0 EndX=-11.49 EndY=49 EndZ=0
    g32: LineSegment StartX=-49.19 StartY=46.25 StartZ=0 EndX=-16.28 EndY=46.25 EndZ=0
    g33: LineSegment StartX=-49.19 StartY=43.25 StartZ=0 EndX=-16.28 EndY=43.25 EndZ=0
    g34: LineSegment StartX=-49.19 StartY=40.5 StartZ=0 EndX=-18.2337 EndY=40.5 EndZ=0
    g35: LineSegment StartX=-49.19 StartY=37.5 StartZ=0 EndX=-18.23 EndY=37.5 EndZ=0
    g36: LineSegment StartX=-49.19 StartY=34.5 StartZ=0 EndX=-18.2337 EndY=34.5 EndZ=0
    g37: LineSegment StartX=-49.19 StartY=31.5 StartZ=0 EndX=-18.23 EndY=31.5 EndZ=0
    g38: LineSegment StartX=-49.19 StartY=28.75 StartZ=0 EndX=-16.2837 EndY=28.75 EndZ=0
    g39: LineSegment StartX=-49.19 StartY=25.75 StartZ=0 EndX=-16.28 EndY=25.75 EndZ=0
    g40: LineSegment StartX=-49.19 StartY=23 StartZ=0 EndX=-11.49 EndY=23 EndZ=0
    g41: LineSegment StartX=-49.19 StartY=20 StartZ=0 EndX=-11.49 EndY=20 EndZ=0
    g42: LineSegment StartX=-49.19 StartY=17.25 StartZ=0 EndX=-1.5 EndY=17.25 EndZ=0
    g43: LineSegment StartX=-49.19 StartY=14.25 StartZ=0 EndX=-1.5 EndY=14.25 EndZ=0
    g44: LineSegment StartX=-49.19 StartY=11.5 StartZ=0 EndX=-1.5 EndY=11.5 EndZ=0
    g45: LineSegment StartX=-49.19 StartY=8.5 StartZ=0 EndX=-1.5 EndY=8.5 EndZ=0
    g46: LineSegment StartX=-49.19 StartY=5.75 StartZ=0 EndX=-1.5 EndY=5.75 EndZ=0
    g47: LineSegment StartX=-49.19 StartY=2.75 StartZ=0 EndX=-1.5 EndY=2.75 EndZ=0
  constraints (120):
    c: Vertical(g0)
    c: Distance(g0) = 3
    c: Block(g0)
    c: Vertical(g1)
    c: Distance(g1) = 3
    c: Vertical(g2)
    c: Equal(g0,g2) = 3
    c: Block(g2)
    c: Vertical(g3)
    c: Equal(g1,g3) = 3
    c: Vertical(g4)
    c: Equal(g0,g4) = 3
    c: Block(g4)
    c: Vertical(g5)
    c: Equal(g1,g5) = 3
    c: Vertical(g6)
    c: Equal(g0,g6) = 3
    c: Block(g6)
    c: Vertical(g7)
    c: Equal(g1,g7) = 3
    c: Vertical(g8)
    c: Equal(g0,g8) = 3
    c: Block(g8)
    c: Vertical(g9)
    c: Equal(g1,g9) = 3
    c: Vertical(g10)
    c: Equal(g0,g10) = 3
    c: Block(g10)
    c: Vertical(g11)
    c: Equal(g1,g11) = 3
    c: Block(g12)
    c: Block(g13)
    c: Block(g14)
    c: Block(g15)
    c: Block(g16)
    c: Block(g17)
    c: Block(g18)
    c: Block(g19)
    c: Block(g20)
    c: Block(g21)
    c: Block(g22)
    c: Block(g23)
    c: Block(g11)
    c: Block(g9)
    c: Block(g7)
    c: Block(g5)
    c: Block(g3)
    c: Block(g1)
    c: Coincident(g24,g0)
    c: Coincident(g24,g12)
    c: Horizontal(g24)
    c: Coincident(g25,g0)
    c: Coincident(g25,g12)
    c: Horizontal(g25)
    c: Coincident(g26,g1)
    c: Coincident(g26,g13)
    c: Horizontal(g26)
    c: Coincident(g27,g1)
    c: Coincident(g27,g13)
    c: Horizontal(g27)
    c: Coincident(g28,g2)
    c: Coincident(g28,g14)
    c: Horizontal(g28)
    c: Coincident(g29,g2)
    c: Coincident(g29,g14)
    c: Horizontal(g29)
    c: Coincident(g30,g3)
    c: Coincident(g30,g15)
    c: Horizontal(g30)
    c: Coincident(g31,g3)
    c: Coincident(g31,g15)
    c: Horizontal(g31)
    c: Coincident(g32,g4)
    c: Coincident(g32,g16)
    c: Horizontal(g32)
    c: Coincident(g33,g4)
    c: Coincident(g33,g16)
    c: Horizontal(g33)
    c: Coincident(g34,g5)
    c: Coincident(g34,g17)
    c: Horizontal(g34)
    c: Coincident(g35,g5)
    c: Coincident(g35,g17)
    c: Horizontal(g35)
    c: Coincident(g36,g6)
    c: Coincident(g36,g19)
    c: Horizontal(g36)
    c: Coincident(g37,g6)
    c: Coincident(g37,g19)
    c: Horizontal(g37)
    c: Coincident(g38,g7)
    c: Coincident(g38,g18)
    c: Horizontal(g38)
    c: Coincident(g39,g7)
    c: Coincident(g39,g18)
    c: Horizontal(g39)
    c: Coincident(g40,g8)
    c: Coincident(g40,g20)
    c: Horizontal(g40)
    c: Coincident(g41,g8)
    c: Coincident(g41,g20)
    c: Horizontal(g41)
    c: Coincident(g42,g9)
    c: Coincident(g42,g23)
    c: Horizontal(g42)
    c: Coincident(g43,g9)
    c: Coincident(g43,g23)
    c: Horizontal(g43)
    c: Coincident(g44,g10)
    c: Coincident(g44,g22)
    c: Horizontal(g44)
    c: Coincident(g45,g10)
    c: Coincident(g45,g22)
    c: Horizontal(g45)
    c: Coincident(g46,g11)
    c: Coincident(g46,g21)
    c: Horizontal(g46)
    c: Coincident(g47,g11)
    c: Coincident(g47,g21)
    c: Horizontal(g47)
FEATURE [Part::Extrusion] Extrude042
  Base = -> Sketch051
  Dir = (1,-2e-16,2e-16)
  DirMode = 2
  FaceMakerClass = Part::FaceMakerBullseye
  LengthFwd = 19
  LengthRev = 0
  Placement = pos=(-19,0,0) rot=(0,0,1;0rad)
  Solid = true
  Symmetric = false
FEATURE [Part::Fillet] Fillet035  label="removeToCreateVentalationHoles"
  Base = -> Extrude042
  Edges = <same value as first occurrence — deduplicated (x6 in doc)>
  Placement = pos=(7,0,0) rot=(0,0,1;0rad)
FEATURE [Part::Cut] Cut038  label="top017"
  Base = -> Cut033
  Tool = -> Fillet035
FEATURE [Sketcher::SketchObject] Sketch052  label="bottomSketch001"
  FullyConstrained = true
  sketch-geometry (45):
    g0: LineSegment StartX=6.29999 StartY=8 StartZ=0 EndX=3.29999 EndY=8 EndZ=0
    g1: LineSegment StartX=3.29999 StartY=8 StartZ=0 EndX=3.29999 EndY=-6.03275e-07 EndZ=0
    g2: ArcOfCircle CenterX=8.29999 CenterY=5 CenterZ=0 NormalX=0 NormalY=0 NormalZ=1 AngleXU=0 Radius=2 StartAngle=3.14159 EndAngle=4.71239
    g3: LineSegment StartX=6.29999 StartY=8 StartZ=0 EndX=6.29999 EndY=5 EndZ=0
    g4: ArcOfCircle CenterX=105 CenterY=19 CenterZ=0 NormalX=0 NormalY=0 NormalZ=1 AngleXU=0 Radius=12.7 StartAngle=4.71239 EndAngle=5.94289
    g5-g11: Circle x7 (B-spline internal-alignment scaffolding for g12; pole/knot coordinates omitted)
    g12: BSplineCurve PolesCount=7 KnotsCount=5 Degree=3 IsPeriodic=0
    g13-g17: GeomPoint x5 (B-spline internal-alignment scaffolding for g12; pole/knot coordinates omitted)
    g18: ArcOfCircle CenterX=105 CenterY=19 CenterZ=0 NormalX=0 NormalY=0 NormalZ=1 AngleXU=0 Radius=15.7 StartAngle=5.81226 EndAngle=6.28319
    g19: BSplineCurve PolesCount=5 KnotsCount=3 Degree=3 IsPeriodic=0
    g20: LineSegment StartX=8.29999 StartY=3 StartZ=0 EndX=101.7 EndY=3 EndZ=0
    g21: LineSegment StartX=3.29999 StartY=-6.03275e-07 StartZ=0 EndX=105 EndY=-6.03275e-07 EndZ=0
    g22: LineSegment StartX=120.974 StartY=8.71251 StartZ=0 EndX=122.332 EndY=7.83778 EndZ=0
    g23: LineSegment StartX=105 StartY=-6.03274e-07 StartZ=0 EndX=113 EndY=-6.03274e-07 EndZ=0
    g24: ArcOfCircle CenterX=105 CenterY=19 CenterZ=0 NormalX=0 NormalY=0 NormalZ=1 AngleXU=0 Radius=20.6155 StartAngle=5.11091 EndAngle=5.71103
    g25: ArcOfCircle CenterX=117.7 CenterY=19 CenterZ=0 NormalX=0 NormalY=0 NormalZ=1 AngleXU=0 Radius=3 StartAngle=1.2e-15 EndAngle=2.10468
    g26: Circle CenterX=116.345 CenterY=16.3232 CenterZ=0 NormalX=0 NormalY=0 NormalZ=1 AngleXU=0 Radius=1
    g27: Circle CenterX=117.24 CenterY=15.7584 CenterZ=0 NormalX=0 NormalY=0 NormalZ=1 AngleXU=0 Radius=1
    g28: Circle CenterX=116.972 CenterY=14.7612 CenterZ=0 NormalX=0 NormalY=0 NormalZ=1 AngleXU=0 Radius=1
    g29: BSplineCurve PolesCount=3 KnotsCount=2 Degree=2 IsPeriodic=0
    g30: GeomPoint X=116.345 Y=16.3232 Z=0
    g31: GeomPoint X=116.972 Y=14.7612 Z=0
    g32: Circle CenterX=115.828 CenterY=17.157 CenterZ=0 NormalX=0 NormalY=0 NormalZ=1 AngleXU=0 Radius=1
    g33: Circle CenterX=115.841 CenterY=16.639 CenterZ=0 NormalX=0 NormalY=0 NormalZ=1 AngleXU=0 Radius=1
    g34: Circle CenterX=116.345 CenterY=16.3232 CenterZ=0 NormalX=0 NormalY=0 NormalZ=1 AngleXU=0 Radius=1
    g35: BSplineCurve PolesCount=3 KnotsCount=2 Degree=2 IsPeriodic=0
    g36: GeomPoint X=115.828 Y=17.157 Z=0
    g37: GeomPoint X=116.345 Y=16.3232 Z=0
    g38: LineSegment StartX=115.828 StartY=17.157 StartZ=0 EndX=115.828 EndY=20.8307 EndZ=0
    g39: Circle CenterX=115.828 CenterY=20.8307 CenterZ=0 NormalX=0 NormalY=0 NormalZ=1 AngleXU=0 Radius=1
    g40: Circle CenterX=115.831 CenterY=21.3396 CenterZ=0 NormalX=0 NormalY=0 NormalZ=1 AngleXU=0 Radius=1
    g41: Circle CenterX=116.173 CenterY=21.5825 CenterZ=0 NormalX=0 NormalY=0 NormalZ=1 AngleXU=0 Radius=1
    g42: BSplineCurve PolesCount=3 KnotsCount=2 Degree=2 IsPeriodic=0
    g43: GeomPoint X=115.828 Y=20.8307 Z=0
    g44: GeomPoint X=116.173 Y=21.5825 Z=0
  constraints (70):
    c: Horizontal(g0)
    c: Distance(g0) = 3
    c: Coincident(g1,g0)
    c: Vertical(g1)
    c: Block(g2)
    c: Block(g0)
    c: Coincident(g3,g0)
    c: Coincident(g3,g2)
    c: Vertical(g3)
    c: Block(g1)
    c: Block(g4)
    c: Coincident(g19,g4)
    c: Block(g19)
    c: Equal(g5, g6-g11) x6
    c: InternalAlignment(g5-g11 -> g12) x7
    c: InternalAlignment(g13-g17 -> g12) x5
    c: Block(g12)
    c: Coincident(g18,g12)
    c: Block(g18)
    c: Coincident(g20,g2)
    c: Coincident(g20,g19)
    c: Horizontal(g20)
    c: Distance(g20) = 93.4
    c: Coincident(g21,g1)
    c: Horizontal(g21)
    c: Distance(g21) = 101.7
    c: Horizontal(g23)
    c: Distance(g23) = 8
    c: Coincident(g24,g23)
    c: Block(g23)
    c: Coincident(g22,g24)
    c: Block(g24)
    c: Block(g22)
    c: Distance(g22) = 1.61553
    c: Coincident(g25,g18)
    c: Block(g25)
    c: Weight(g26) = 1
    c: Equal(g26,g27)
    c: Equal(g26,g28)
    c: Coincident(g29,g4)
    c: InternalAlignment(g26,g29)
    c: InternalAlignment(g27,g29)
    c: InternalAlignment(g28,g29)
    c: InternalAlignment(g30,g29)
    c: InternalAlignment(g31,g29)
    c: Block(g29)
    c: Weight(g32) = 1
    c: Equal(g32,g33)
    c: Equal(g32,g34)
    c: Coincident(g35,g29)
    c: InternalAlignment(g32,g35)
    c: InternalAlignment(g33,g35)
    c: InternalAlignment(g34,g35)
    c: InternalAlignment(g36,g35)
    c: InternalAlignment(g37,g35)
    c: Block(g35)
    c: Coincident(g38,g35)
    c: Vertical(g38)
    c: Block(g38)
    c: Coincident(g42,g38)
    c: Weight(g39) = 1
    c: Equal(g39,g40)
    c: Equal(g39,g41)
    c: Coincident(g42,g25)
    c: InternalAlignment(g39,g42)
    c: InternalAlignment(g40,g42)
    c: InternalAlignment(g41,g42)
    c: InternalAlignment(g43,g42)
    c: InternalAlignment(g44,g42)
    c: Block(g42)
FEATURE [Part::Extrusion] Extrude043  label="bottom010"
  Base = -> Sketch052
  Dir = (0,0,1)
  DirMode = 2
  FaceMakerClass = Part::FaceMakerBullseye
  LengthFwd = 71.4
  LengthRev = 0
  Placement = pos=(0,0,0.3) rot=(0,0,1;0rad)
  Solid = true
  Symmetric = false
FEATURE [Sketcher::SketchObject] Sketch053  label="topSketch013"
  FullyConstrained = true
  sketch-geometry (22):
    g0: LineSegment StartX=5.21097e-06 StartY=3 StartZ=0 EndX=5.21097e-06 EndY=19 EndZ=0
    g1: ArcOfCircle CenterX=19 CenterY=19 CenterZ=0 NormalX=0 NormalY=0 NormalZ=1 AngleXU=0 Radius=19 StartAngle=1.5708 EndAngle=3.14159
    g2: ArcOfCircle CenterX=19 CenterY=19 CenterZ=0 NormalX=0 NormalY=0 NormalZ=1 AngleXU=0 Radius=16 StartAngle=1.5708 EndAngle=3.14159
    g3: LineSegment StartX=114 StartY=35 StartZ=0 EndX=19 EndY=35 EndZ=0
    g4: LineSegment StartX=5.21097e-06 StartY=3 StartZ=0 EndX=5.21097e-06 EndY=0 EndZ=0
    g5: LineSegment StartX=3 StartY=0 StartZ=0 EndX=5.21097e-06 EndY=0 EndZ=0
    g6: LineSegment StartX=3 StartY=19 StartZ=0 EndX=3 EndY=0 EndZ=0
    g7: LineSegment StartX=19 StartY=38 StartZ=0 EndX=124 EndY=38 EndZ=0
    g8: Circle CenterX=119 CenterY=35 CenterZ=0 NormalX=0 NormalY=0 NormalZ=1 AngleXU=0 Radius=1
    g9: Circle CenterX=121 CenterY=35 CenterZ=0 NormalX=0 NormalY=0 NormalZ=1 AngleXU=0 Radius=1
    g10: Circle CenterX=121 CenterY=33 CenterZ=0 NormalX=0 NormalY=0 NormalZ=1 AngleXU=0 Radius=1
    g11: BSplineCurve PolesCount=3 KnotsCount=2 Degree=2 IsPeriodic=0
    g12: GeomPoint X=119 Y=35 Z=0
    g13: GeomPoint X=121 Y=33 Z=0
    g14: LineSegment StartX=119 StartY=35 StartZ=0 EndX=114 EndY=35 EndZ=0
    g15: ArcOfCircle CenterX=105 CenterY=19 CenterZ=0 NormalX=0 NormalY=0 NormalZ=1 AngleXU=0 Radius=16 StartAngle=5.60905 EndAngle=6.28319
    g16: LineSegment StartX=121 StartY=33 StartZ=0 EndX=121 EndY=19 EndZ=0
    g17: LineSegment StartX=117.5 StartY=9.01251 StartZ=0 EndX=121.163 EndY=9.0125 EndZ=0
    g18: ArcOfCircle CenterX=105 CenterY=19 CenterZ=0 NormalX=0 NormalY=0 NormalZ=1 AngleXU=0 Radius=20.6155 StartAngle=5.7297 EndAngle=6.28319
    g19: LineSegment StartX=121.163 StartY=9.0125 StartZ=0 EndX=122.538 EndY=8.16329 EndZ=0
    g20: LineSegment StartX=124 StartY=38 StartZ=0 EndX=125.616 EndY=38 EndZ=0
    g21: LineSegment StartX=125.616 StartY=19 StartZ=0 EndX=125.616 EndY=38 EndZ=0
  constraints (50):
    c: Vertical(g0)
    c: Block(g0)
    c: Coincident(g1,g0)
    c: Block(g1)
    c: Coincident(g2,g1)
    c: Block(g2)
    c: Coincident(g3,g2)
    c: Horizontal(g3)
    c: Tangent(g3,g2)
    c: Coincident(g4,g0)
    c: Distance(g4) = 3
    c: Vertical(g4)
    c: Coincident(g5,g4)
    c: Horizontal(g5)
    c: Coincident(g6,g2)
    c: Coincident(g6,g5)
    c: Vertical(g6)
    c: Horizontal(g7)
    c: Distance(g7) = 105
    c: Coincident(g7,g1)
    c: Block(g3)
    c: Weight(g8) = 1
    c: Equal(g8,g9)
    c: Equal(g8,g10)
    c: InternalAlignment(g8,g11)
    c: InternalAlignment(g9,g11)
    c: InternalAlignment(g10,g11)
    c: InternalAlignment(g12,g11)
    c: InternalAlignment(g13,g11)
    c: Block(g11)
    c: Coincident(g14,g11)
    c: Coincident(g14,g3)
    c: Horizontal(g14)
    c: Block(g15)
    c: Coincident(g16,g11)
    c: Coincident(g16,g15)
    c: Vertical(g16)
    c: Distance(g16) = 14
    c: Coincident(g17,g15)
    c: Block(g18)
    c: Coincident(g19,g18)
    c: Coincident(g20,g7)
    c: Horizontal(g20)
    c: Vertical(g21)
    c: Coincident(g20,g21)
    c: Block(g20)
    c: Block(g21)
    c: Block(g19)
    c: Block(g17)
    c: Distance(g20) = 1.61553
FEATURE [Part::Extrusion] Extrude044
  Base = -> Sketch053
  Dir = (0,0,1)
  DirMode = 2
  FaceMakerClass = Part::FaceMakerBullseye
  LengthFwd = 72
  LengthRev = 0
  Solid = true
  Symmetric = false
FEATURE [Part::Fillet] Fillet036  label="top018"
  Base = -> Extrude044
  Edges = 1 edges r=2: [Edge41]
FEATURE [Sketcher::SketchObject] Sketch054
  FullyConstrained = false
  Placement = pos=(0,0,0) rot=(1,0,0;1.5708rad)
  sketch-geometry (24):
    g0: ArcOfCircle CenterX=-4 CenterY=-10.5 CenterZ=0 NormalX=0 NormalY=0 NormalZ=1 AngleXU=0 Radius=1.5 StartAngle=6e-16 EndAngle=3.14159
    g1: ArcOfCircle CenterX=-34.2 CenterY=-10.5 CenterZ=0 NormalX=0 NormalY=0 NormalZ=1 AngleXU=0 Radius=1.5 StartAngle=0 EndAngle=3.14159
    g2: ArcOfCircle CenterX=-34.2 CenterY=-27.7 CenterZ=0 NormalX=0 NormalY=0 NormalZ=1 AngleXU=0 Radius=1.5 StartAngle=3.14159 EndAngle=6.28319
    g3: ArcOfCircle CenterX=-4 CenterY=-27.7 CenterZ=0 NormalX=0 NormalY=0 NormalZ=1 AngleXU=0 Radius=1.5 StartAngle=3.1416 EndAngle=6.28319
    g4: ArcOfCircle CenterX=-10 CenterY=-4.3 CenterZ=0 NormalX=0 NormalY=0 NormalZ=1 AngleXU=0 Radius=1.5 StartAngle=2e-16 EndAngle=3.14159
    g5: ArcOfCircle CenterX=-16.1 CenterY=-1.8 CenterZ=0 NormalX=0 NormalY=0 NormalZ=1 AngleXU=0 Radius=1.5 StartAngle=5e-16 EndAngle=3.14159
    g6: ArcOfCircle CenterX=-22.1 CenterY=-1.8 CenterZ=0 NormalX=0 NormalY=0 NormalZ=1 AngleXU=0 Radius=1.5 StartAngle=5e-16 EndAngle=3.14159
    g7: ArcOfCircle CenterX=-28.2 CenterY=-4.3 CenterZ=0 NormalX=0 NormalY=0 NormalZ=1 AngleXU=0 Radius=1.5 StartAngle=2e-16 EndAngle=3.14159
    g8: ArcOfCircle CenterX=-10 CenterY=-33.9 CenterZ=0 NormalX=0 NormalY=0 NormalZ=1 AngleXU=0 Radius=1.5 StartAngle=3.14159 EndAngle=6.28319
    g9: ArcOfCircle CenterX=-16.1 CenterY=-36.4 CenterZ=0 NormalX=0 NormalY=0 NormalZ=1 AngleXU=0 Radius=1.5 StartAngle=3.14159 EndAngle=6.28319
    g10: ArcOfCircle CenterX=-22.1 CenterY=-36.4 CenterZ=0 NormalX=0 NormalY=0 NormalZ=1 AngleXU=0 Radius=1.5 StartAngle=3.14159 EndAngle=6.28319
    g11: ArcOfCircle CenterX=-28.2 CenterY=-33.9 CenterZ=0 NormalX=0 NormalY=0 NormalZ=1 AngleXU=0 Radius=1.5 StartAngle=3.14159 EndAngle=6.28319
    g12: LineSegment StartX=-35.7 StartY=-10.5 StartZ=0 EndX=-35.7 EndY=-27.7 EndZ=0
    g13: LineSegment StartX=-32.7 StartY=-10.5 StartZ=0 EndX=-32.7 EndY=-27.7 EndZ=0
    g14: LineSegment StartX=-29.7 StartY=-33.9 StartZ=0 EndX=-29.7 EndY=-4.3 EndZ=0
    g15: LineSegment StartX=-26.7 StartY=-33.9 StartZ=0 EndX=-26.7 EndY=-4.3 EndZ=0
    g16: LineSegment StartX=-2.5 StartY=-10.5 StartZ=0 EndX=-2.5 EndY=-27.7 EndZ=0
    g17: LineSegment StartX=-8.5 StartY=-4.3 StartZ=0 EndX=-8.5 EndY=-33.9 EndZ=0
    g18: LineSegment StartX=-5.5 StartY=-10.5 StartZ=0 EndX=-5.5 EndY=-27.7 EndZ=0
    g19: LineSegment StartX=-11.5 StartY=-4.3 StartZ=0 EndX=-11.5 EndY=-33.9 EndZ=0
    g20: LineSegment StartX=-14.6 StartY=-1.8 StartZ=0 EndX=-14.6 EndY=-36.4 EndZ=0
    g21: LineSegment StartX=-17.6 StartY=-1.8 StartZ=0 EndX=-17.6 EndY=-36.4 EndZ=0
    g22: LineSegment StartX=-20.6 StartY=-36.4 StartZ=0 EndX=-20.6 EndY=-1.8 EndZ=0
    g23: LineSegment StartX=-23.6 StartY=-1.8 StartZ=0 EndX=-23.6 EndY=-36.4 EndZ=0
  constraints (48):
    c: Block(g0)
    c: Block(g1)
    c: Block(g2)
    c: Block(g3)
    c: Block(g4)
    c: Block(g5)
    c: Block(g6)
    c: Block(g7)
    c: Block(g8)
    c: Block(g9)
    c: Block(g10)
    c: Block(g11)
    c: Coincident(g12,g1)
    c: Coincident(g12,g2)
    c: Vertical(g12)
    c: Coincident(g13,g1)
    c: Coincident(g13,g2)
    c: Vertical(g13)
    c: Coincident(g14,g11)
    c: Coincident(g14,g7)
    c: Vertical(g14)
    c: Coincident(g15,g11)
    c: Coincident(g15,g7)
    c: Vertical(g15)
    c: Coincident(g16,g0)
    c: Coincident(g16,g3)
    c: Vertical(g16)
    c: Coincident(g17,g4)
    c: Coincident(g17,g8)
    c: Vertical(g17)
    c: Coincident(g18,g0)
    c: Coincident(g18,g3)
    c: Vertical(g18)
    c: Coincident(g19,g4)
    c: Coincident(g19,g8)
    c: Vertical(g19)
    c: Coincident(g20,g5)
    c: Coincident(g20,g9)
    c: Vertical(g20)
    c: Coincident(g21,g5)
    c: Coincident(g21,g9)
    c: Vertical(g21)
    c: Coincident(g22,g10)
    c: Coincident(g22,g6)
    c: Vertical(g22)
    c: Coincident(g23,g6)
    c: Coincident(g23,g10)
    c: Vertical(g23)
FEATURE [Part::Extrusion] Extrude045  label="removeToCreateFanGrillHoles003"
  Base = -> Sketch054
  Dir = (0,-1,6e-16)
  DirMode = 2
  FaceMakerClass = Part::FaceMakerBullseye
  LengthFwd = 10
  LengthRev = 0
  Placement = pos=(65.4,44,54.82) rot=(0,0,1;0rad)
  Solid = true
  Symmetric = false
FEATURE [Part::Feature] Face105 .. Face108  x4 (patterned run collapsed; names and placements below)
  shape: bbox 3.5 x 17.8 x 2e-07 mm, 1 faces, 0 solids (baked)
FEATURE [Part::Revolution] Revolve113  label="removeToCreateScrewAndThreadedInsertHole041"
  Angle = 360
  Axis = (0,1,0)
  Base = (0,0,0)
  FaceMakerClass = Part::FaceMakerBullseye
  Placement = pos=(62.3,30.3,19.7) rot=(0,0,1;0rad)
  Solid = false
  Source = -> Face105
  Symmetric = false
FEATURE [Part::Revolution] Revolve114  label="removeToCreateScrewAndThreadedInsertHole042"
  Angle = 360
  Axis = (0,1,0)
  Base = (0,0,0)
  FaceMakerClass = Part::FaceMakerBullseye
  Placement = pos=(62.3,30.3,51.7) rot=(0,0,1;0rad)
  Solid = false
  Source = -> Face106
  Symmetric = false
FEATURE [Part::Revolution] Revolve115  label="removeToCreateScrewAndThreadedInsertHole043"
  Angle = 360
  Axis = (0,1,0)
  Base = (0,0,0)
  FaceMakerClass = Part::FaceMakerBullseye
  Placement = pos=(30.3,30.3,19.7) rot=(0,0,1;0rad)
  Solid = false
  Source = -> Face107
  Symmetric = false
FEATURE [Part::Revolution] Revolve116  label="removeToCreateScrewAndThreadedInsertHole044"
  Angle = 360
  Axis = (0,1,0)
  Base = (0,0,0)
  FaceMakerClass = Part::FaceMakerBullseye
  Placement = pos=(30.3,30.3,51.7) rot=(0,0,1;0rad)
  Solid = false
  Source = -> Face108
  Symmetric = false
FEATURE [Part::MultiFuse] Fusion083  label="createThreadedInsertHolesForFan004"
  Shapes = -> [Revolve113,Revolve114,Revolve115,Revolve116]
FEATURE [Part::Box] Box024  label="removeToCreteHoleForPlugHousing026"
  AttacherType = Attacher::AttachEngine3D
  Height = 28.6
  Length = 10
  Placement = pos=(-2,0,21.7) rot=(0,0,1;0rad)
  Width = 19
FEATURE [Part::Cylinder] Cylinder038  label="removeToCreteHoleForPlugHousing027"
  Angle = 360
  AttacherType = Attacher::AttachEngine3D
  Height = 20
  Placement = pos=(-2,19,36) rot=(0,1,0;1.5708rad)
  Radius = 14.3
FEATURE [Part::MultiFuse] Fusion084  label="removeToCreteHoleForPlugHousing028"
  Shapes = -> [Box024,Cylinder038]
FEATURE [Part::Cylinder] Cylinder039
  Angle = 360
  AttacherType = Attacher::AttachEngine3D
  Height = 20
  Placement = pos=(0,0,36.15) rot=(0,0,1;0rad)
  Radius = 14.3
FEATURE [Part::Cylinder] Cylinder040
  Angle = 360
  AttacherType = Attacher::AttachEngine3D
  Height = 10
  Placement = pos=(0,0,36.15) rot=(0,0,1;0rad)
  Radius = 4
FEATURE [Part::Box] Box025  label="removeToCreteHoleForPlugHousing030"
  AttacherType = Attacher::AttachEngine3D
  Height = 28.6
  Length = 20
  Placement = pos=(106.15,0,21.7) rot=(0,0,1;0rad)
  Width = 19
FEATURE [Part::MultiFuse] Fusion086  label="removeToCreteHoleForPlugHousing031"
  Placement = pos=(70,19,36) rot=(0,1,0;1.5708rad)
  Shapes = -> [Cylinder039,Cylinder040]
FEATURE [Part::MultiFuse] Fusion085  label="removeToCreteHoleForPlugHousing029"
  Shapes = -> [Box025,Fusion086]
FEATURE [Sketcher::SketchObject] Sketch055
  FullyConstrained = true
  Placement = pos=(117,19,0) rot=(0.57735,0.57735,0.57735;2.0944rad)
  sketch-geometry (48):
    g0: LineSegment StartX=-49.19 StartY=69.25 StartZ=0 EndX=-49.19 EndY=66.25 EndZ=0
    g1: LineSegment StartX=-49.19 StartY=63.5 StartZ=0 EndX=-49.19 EndY=60.5 EndZ=0
    g2: LineSegment StartX=-49.19 StartY=57.75 StartZ=0 EndX=-49.19 EndY=54.75 EndZ=0
    g3: LineSegment StartX=-49.19 StartY=52 StartZ=0 EndX=-49.19 EndY=49 EndZ=0
    g4: LineSegment StartX=-49.19 StartY=46.25 StartZ=0 EndX=-49.19 EndY=43.25 EndZ=0
    g5: LineSegment StartX=-49.19 StartY=40.5 StartZ=0 EndX=-49.19 EndY=37.5 EndZ=0
    g6: LineSegment StartX=-49.19 StartY=34.5 StartZ=0 EndX=-49.19 EndY=31.5 EndZ=0
    g7: LineSegment StartX=-49.19 StartY=28.75 StartZ=0 EndX=-49.19 EndY=25.75 EndZ=0
    g8: LineSegment StartX=-49.19 StartY=23 StartZ=0 EndX=-49.19 EndY=20 EndZ=0
    g9: LineSegment StartX=-49.19 StartY=17.25 StartZ=0 EndX=-49.19 EndY=14.25 EndZ=0
    g10: LineSegment StartX=-49.19 StartY=11.5 StartZ=0 EndX=-49.19 EndY=8.5 EndZ=0
    g11: LineSegment StartX=-49.19 StartY=5.75 StartZ=0 EndX=-49.19 EndY=2.75 EndZ=0
    g12: ArcOfCircle CenterX=-1.5 CenterY=67.75 CenterZ=0 NormalX=0 NormalY=0 NormalZ=1 AngleXU=0 Radius=1.5 StartAngle=4.71239 EndAngle=7.85398
    g13: ArcOfCircle CenterX=-1.5 CenterY=62 CenterZ=0 NormalX=0 NormalY=0 NormalZ=1 AngleXU=0 Radius=1.5 StartAngle=4.71239 EndAngle=7.85398
    g14: ArcOfCircle CenterX=-1.5 CenterY=56.25 CenterZ=0 NormalX=0 NormalY=0 NormalZ=1 AngleXU=0 Radius=1.5 StartAngle=4.71239 EndAngle=7.85398
    g15: ArcOfCircle CenterX=-11.49 CenterY=50.5 CenterZ=0 NormalX=0 NormalY=0 NormalZ=1 AngleXU=0 Radius=1.5 StartAngle=4.71239 EndAngle=7.85398
    g16: ArcOfCircle CenterX=-16.28 CenterY=44.75 CenterZ=0 NormalX=0 NormalY=0 NormalZ=1 AngleXU=0 Radius=1.5 StartAngle=4.71239 EndAngle=7.85398
    g17: ArcOfCircle CenterX=-18.2337 CenterY=39 CenterZ=0 NormalX=0 NormalY=0 NormalZ=1 AngleXU=0 Radius=1.5 StartAngle=4.71485 EndAngle=7.85398
    g18: ArcOfCircle CenterX=-16.2837 CenterY=27.25 CenterZ=0 NormalX=0 NormalY=0 NormalZ=1 AngleXU=0 Radius=1.5 StartAngle=4.71485 EndAngle=7.85398
    g19: ArcOfCircle CenterX=-18.2337 CenterY=33 CenterZ=0 NormalX=0 NormalY=0 NormalZ=1 AngleXU=0 Radius=1.5 StartAngle=4.71485 EndAngle=7.85398
    g20: ArcOfCircle CenterX=-11.49 CenterY=21.5 CenterZ=0 NormalX=0 NormalY=0 NormalZ=1 AngleXU=0 Radius=1.5 StartAngle=4.71239 EndAngle=7.85398
    g21: ArcOfCircle CenterX=-1.5 CenterY=4.25 CenterZ=0 NormalX=0 NormalY=0 NormalZ=1 AngleXU=0 Radius=1.5 StartAngle=4.71239 EndAngle=7.85398
    g22: ArcOfCircle CenterX=-1.5 CenterY=10 CenterZ=0 NormalX=0 NormalY=0 NormalZ=1 AngleXU=0 Radius=1.5 StartAngle=4.71239 EndAngle=7.85398
    g23: ArcOfCircle CenterX=-1.5 CenterY=15.75 CenterZ=0 NormalX=0 NormalY=0 NormalZ=1 AngleXU=0 Radius=1.5 StartAngle=4.71239 EndAngle=7.85398
    g24: LineSegment StartX=-49.19 StartY=69.25 StartZ=0 EndX=-1.5 EndY=69.25 EndZ=0
    g25: LineSegment StartX=-49.19 StartY=66.25 StartZ=0 EndX=-1.5 EndY=66.25 EndZ=0
    g26: LineSegment StartX=-49.19 StartY=63.5 StartZ=0 EndX=-1.5 EndY=63.5 EndZ=0
    g27: LineSegment StartX=-49.19 StartY=60.5 StartZ=0 EndX=-1.5 EndY=60.5 EndZ=0
    g28: LineSegment StartX=-49.19 StartY=57.75 StartZ=0 EndX=-1.5 EndY=57.75 EndZ=0
    g29: LineSegment StartX=-49.19 StartY=54.75 StartZ=0 EndX=-1.5 EndY=54.75 EndZ=0
    g30: LineSegment StartX=-49.19 StartY=52 StartZ=0 EndX=-11.49 EndY=52 EndZ=0
    g31: LineSegment StartX=-49.19 StartY=49 StartZ=0 EndX=-11.49 EndY=49 EndZ=0
    g32: LineSegment StartX=-49.19 StartY=46.25 StartZ=0 EndX=-16.28 EndY=46.25 EndZ=0
    g33: LineSegment StartX=-49.19 StartY=43.25 StartZ=0 EndX=-16.28 EndY=43.25 EndZ=0
    g34: LineSegment StartX=-49.19 StartY=40.5 StartZ=0 EndX=-18.2337 EndY=40.5 EndZ=0
    g35: LineSegment StartX=-49.19 StartY=37.5 StartZ=0 EndX=-18.23 EndY=37.5 EndZ=0
    g36: LineSegment StartX=-49.19 StartY=34.5 StartZ=0 EndX=-18.2337 EndY=34.5 EndZ=0
    g37: LineSegment StartX=-49.19 StartY=31.5 StartZ=0 EndX=-18.23 EndY=31.5 EndZ=0
    g38: LineSegment StartX=-49.19 StartY=28.75 StartZ=0 EndX=-16.2837 EndY=28.75 EndZ=0
    g39: LineSegment StartX=-49.19 StartY=25.75 StartZ=0 EndX=-16.28 EndY=25.75 EndZ=0
    g40: LineSegment StartX=-49.19 StartY=23 StartZ=0 EndX=-11.49 EndY=23 EndZ=0
    g41: LineSegment StartX=-49.19 StartY=20 StartZ=0 EndX=-11.49 EndY=20 EndZ=0
    g42: LineSegment StartX=-49.19 StartY=17.25 StartZ=0 EndX=-1.5 EndY=17.25 EndZ=0
    g43: LineSegment StartX=-49.19 StartY=14.25 StartZ=0 EndX=-1.5 EndY=14.25 EndZ=0
    g44: LineSegment StartX=-49.19 StartY=11.5 StartZ=0 EndX=-1.5 EndY=11.5 EndZ=0
    g45: LineSegment StartX=-49.19 StartY=8.5 StartZ=0 EndX=-1.5 EndY=8.5 EndZ=0
    g46: LineSegment StartX=-49.19 StartY=5.75 StartZ=0 EndX=-1.5 EndY=5.75 EndZ=0
    g47: LineSegment StartX=-49.19 StartY=2.75 StartZ=0 EndX=-1.5 EndY=2.75 EndZ=0
  constraints (120):
    c: Vertical(g0)
    c: Distance(g0) = 3
    c: Block(g0)
    c: Vertical(g1)
    c: Distance(g1) = 3
    c: Vertical(g2)
    c: Equal(g0,g2) = 3
    c: Block(g2)
    c: Vertical(g3)
    c: Equal(g1,g3) = 3
    c: Vertical(g4)
    c: Equal(g0,g4) = 3
    c: Block(g4)
    c: Vertical(g5)
    c: Equal(g1,g5) = 3
    c: Vertical(g6)
    c: Equal(g0,g6) = 3
    c: Block(g6)
    c: Vertical(g7)
    c: Equal(g1,g7) = 3
    c: Vertical(g8)
    c: Equal(g0,g8) = 3
    c: Block(g8)
    c: Vertical(g9)
    c: Equal(g1,g9) = 3
    c: Vertical(g10)
    c: Equal(g0,g10) = 3
    c: Block(g10)
    c: Vertical(g11)
    c: Equal(g1,g11) = 3
    c: Block(g12)
    c: Block(g13)
    c: Block(g14)
    c: Block(g15)
    c: Block(g16)
    c: Block(g17)
    c: Block(g18)
    c: Block(g19)
    c: Block(g20)
    c: Block(g21)
    c: Block(g22)
    c: Block(g23)
    c: Block(g11)
    c: Block(g9)
    c: Block(g7)
    c: Block(g5)
    c: Block(g3)
    c: Block(g1)
    c: Coincident(g24,g0)
    c: Coincident(g24,g12)
    c: Horizontal(g24)
    c: Coincident(g25,g0)
    c: Coincident(g25,g12)
    c: Horizontal(g25)
    c: Coincident(g26,g1)
    c: Coincident(g26,g13)
    c: Horizontal(g26)
    c: Coincident(g27,g1)
    c: Coincident(g27,g13)
    c: Horizontal(g27)
    c: Coincident(g28,g2)
    c: Coincident(g28,g14)
    c: Horizontal(g28)
    c: Coincident(g29,g2)
    c: Coincident(g29,g14)
    c: Horizontal(g29)
    c: Coincident(g30,g3)
    c: Coincident(g30,g15)
    c: Horizontal(g30)
    c: Coincident(g31,g3)
    c: Coincident(g31,g15)
    c: Horizontal(g31)
    c: Coincident(g32,g4)
    c: Coincident(g32,g16)
    c: Horizontal(g32)
    c: Coincident(g33,g4)
    c: Coincident(g33,g16)
    c: Horizontal(g33)
    c: Coincident(g34,g5)
    c: Coincident(g34,g17)
    c: Horizontal(g34)
    c: Coincident(g35,g5)
    c: Coincident(g35,g17)
    c: Horizontal(g35)
    c: Coincident(g36,g6)
    c: Coincident(g36,g19)
    c: Horizontal(g36)
    c: Coincident(g37,g6)
    c: Coincident(g37,g19)
    c: Horizontal(g37)
    c: Coincident(g38,g7)
    c: Coincident(g38,g18)
    c: Horizontal(g38)
    c: Coincident(g39,g7)
    c: Coincident(g39,g18)
    c: Horizontal(g39)
    c: Coincident(g40,g8)
    c: Coincident(g40,g20)
    c: Horizontal(g40)
    c: Coincident(g41,g8)
    c: Coincident(g41,g20)
    c: Horizontal(g41)
    c: Coincident(g42,g9)
    c: Coincident(g42,g23)
    c: Horizontal(g42)
    c: Coincident(g43,g9)
    c: Coincident(g43,g23)
    c: Horizontal(g43)
    c: Coincident(g44,g10)
    c: Coincident(g44,g22)
    c: Horizontal(g44)
    c: Coincident(g45,g10)
    c: Coincident(g45,g22)
    c: Horizontal(g45)
    c: Coincident(g46,g11)
    c: Coincident(g46,g21)
    c: Horizontal(g46)
    c: Coincident(g47,g11)
    c: Coincident(g47,g21)
    c: Horizontal(g47)
FEATURE [Part::Extrusion] Extrude046
  Base = -> Sketch055
  Dir = (1,0,0)
  DirMode = 2
  FaceMakerClass = Part::FaceMakerBullseye
  LengthFwd = 23
  LengthRev = 0
  Placement = pos=(-19,0,0) rot=(0,0,1;0rad)
  Solid = true
  Symmetric = false
FEATURE [Part::Fillet] Fillet038  label="removeToCreateVentalationHoles001"
  Base = -> Extrude046
  Edges = <same value as first occurrence — deduplicated (x6 in doc)>
  Placement = pos=(7,0,0) rot=(0,0,1;0rad)
FEATURE [Sketcher::SketchObject] Sketch056  label="topSketch014"
  FullyConstrained = true
  sketch-geometry (22):
    g0: LineSegment StartX=5.21097e-06 StartY=3 StartZ=0 EndX=5.21097e-06 EndY=19 EndZ=0
    g1: ArcOfCircle CenterX=19 CenterY=19 CenterZ=0 NormalX=0 NormalY=0 NormalZ=1 AngleXU=0 Radius=19 StartAngle=1.5708 EndAngle=3.14159
    g2: ArcOfCircle CenterX=19 CenterY=19 CenterZ=0 NormalX=0 NormalY=0 NormalZ=1 AngleXU=0 Radius=16 StartAngle=1.5708 EndAngle=3.14159
    g3: LineSegment StartX=114 StartY=35 StartZ=0 EndX=19 EndY=35 EndZ=0
    g4: LineSegment StartX=5.21097e-06 StartY=3 StartZ=0 EndX=5.21097e-06 EndY=0 EndZ=0
    g5: LineSegment StartX=3 StartY=0 StartZ=0 EndX=5.21097e-06 EndY=0 EndZ=0
    g6: LineSegment StartX=3 StartY=19 StartZ=0 EndX=3 EndY=0 EndZ=0
    g7: LineSegment StartX=19 StartY=38 StartZ=0 EndX=124 EndY=38 EndZ=0
    g8: Circle CenterX=119 CenterY=35 CenterZ=0 NormalX=0 NormalY=0 NormalZ=1 AngleXU=0 Radius=1
    g9: Circle CenterX=121 CenterY=35 CenterZ=0 NormalX=0 NormalY=0 NormalZ=1 AngleXU=0 Radius=1
    g10: Circle CenterX=121 CenterY=33 CenterZ=0 NormalX=0 NormalY=0 NormalZ=1 AngleXU=0 Radius=1
    g11: BSplineCurve PolesCount=3 KnotsCount=2 Degree=2 IsPeriodic=0
    g12: GeomPoint X=119 Y=35 Z=0
    g13: GeomPoint X=121 Y=33 Z=0
    g14: LineSegment StartX=119 StartY=35 StartZ=0 EndX=114 EndY=35 EndZ=0
    g15: ArcOfCircle CenterX=105 CenterY=19 CenterZ=0 NormalX=0 NormalY=0 NormalZ=1 AngleXU=0 Radius=16 StartAngle=5.60905 EndAngle=6.28319
    g16: LineSegment StartX=121 StartY=33 StartZ=0 EndX=121 EndY=19 EndZ=0
    g17: LineSegment StartX=117.5 StartY=9.01251 StartZ=0 EndX=121.163 EndY=9.0125 EndZ=0
    g18: ArcOfCircle CenterX=105 CenterY=19 CenterZ=0 NormalX=0 NormalY=0 NormalZ=1 AngleXU=0 Radius=20.6155 StartAngle=5.7297 EndAngle=6.28319
    g19: LineSegment StartX=121.163 StartY=9.0125 StartZ=0 EndX=122.538 EndY=8.16329 EndZ=0
    g20: LineSegment StartX=124 StartY=38 StartZ=0 EndX=125.616 EndY=38 EndZ=0
    g21: LineSegment StartX=125.616 StartY=19 StartZ=0 EndX=125.616 EndY=38 EndZ=0
  constraints (49):
    c: Vertical(g0)
    c: Block(g0)
    c: Coincident(g1,g0)
    c: Block(g1)
    c: Coincident(g2,g1)
    c: Block(g2)
    c: Coincident(g3,g2)
    c: Horizontal(g3)
    c: Tangent(g3,g2)
    c: Coincident(g4,g0)
    c: Distance(g4) = 3
    c: Vertical(g4)
    c: Coincident(g5,g4)
    c: Horizontal(g5)
    c: Coincident(g6,g2)
    c: Coincident(g6,g5)
    c: Vertical(g6)
    c: Horizontal(g7)
    c: Distance(g7) = 105
    c: Coincident(g7,g1)
    c: Block(g3)
    c: Weight(g8) = 1
    c: Equal(g8,g9)
    c: Equal(g8,g10)
    c: InternalAlignment(g8,g11)
    c: InternalAlignment(g9,g11)
    c: InternalAlignment(g10,g11)
    c: InternalAlignment(g12,g11)
    c: InternalAlignment(g13,g11)
    c: Block(g11)
    c: Coincident(g14,g11)
    c: Coincident(g14,g3)
    c: Horizontal(g14)
    c: Block(g15)
    c: Coincident(g16,g11)
    c: Coincident(g16,g15)
    c: Vertical(g16)
    c: Distance(g16) = 14
    c: Coincident(g17,g15)
    c: Block(g18)
    c: Coincident(g19,g18)
    c: Coincident(g20,g7)
    c: Horizontal(g20)
    c: Vertical(g21)
    c: Coincident(g20,g21)
    c: Block(g20)
    c: Block(g21)
    c: Block(g19)
    c: Block(g17)
FEATURE [Part::Box] Box026  label="removeToCreteHoleForPlugHousing032"
  AttacherType = Attacher::AttachEngine3D
  Height = 28.6
  Length = 10
  Placement = pos=(-2,0,21.7) rot=(0,0,1;0rad)
  Width = 19
FEATURE [Part::Feature] Face109 .. Face112  x4 (patterned run collapsed; names and placements below)
  shape: bbox 3.5 x 17.8 x 2e-07 mm, 1 faces, 0 solids (baked)
FEATURE [Part::Revolution] Revolve117  label="removeToCreateScrewAndThreadedInsertHole045"
  Angle = 360
  Axis = (0,1,0)
  Base = (0,0,0)
  FaceMakerClass = Part::FaceMakerBullseye
  Placement = pos=(62.3,30.3,19.7) rot=(0,0,1;0rad)
  Solid = false
  Source = -> Face109
  Symmetric = false
FEATURE [Part::Revolution] Revolve118  label="removeToCreateScrewAndThreadedInsertHole046"
  Angle = 360
  Axis = (0,1,0)
  Base = (0,0,0)
  FaceMakerClass = Part::FaceMakerBullseye
  Placement = pos=(62.3,30.3,51.7) rot=(0,0,1;0rad)
  Solid = false
  Source = -> Face110
  Symmetric = false
FEATURE [Part::Revolution] Revolve119  label="removeToCreateScrewAndThreadedInsertHole047"
  Angle = 360
  Axis = (0,1,0)
  Base = (0,0,0)
  FaceMakerClass = Part::FaceMakerBullseye
  Placement = pos=(30.3,30.3,19.7) rot=(0,0,1;0rad)
  Solid = false
  Source = -> Face111
  Symmetric = false
FEATURE [Part::Revolution] Revolve120  label="removeToCreateScrewAndThreadedInsertHole048"
  Angle = 360
  Axis = (0,1,0)
  Base = (0,0,0)
  FaceMakerClass = Part::FaceMakerBullseye
  Placement = pos=(30.3,30.3,51.7) rot=(0,0,1;0rad)
  Solid = false
  Source = -> Face112
  Symmetric = false
FEATURE [Part::MultiFuse] Fusion087  label="createThreadedInsertHolesForFan005"
  Shapes = -> [Revolve117,Revolve118,Revolve119,Revolve120]
FEATURE [Part::Extrusion] Extrude047
  Base = -> Sketch056
  Dir = (0,0,1)
  DirMode = 2
  FaceMakerClass = Part::FaceMakerBullseye
  LengthFwd = 72
  LengthRev = 0
  Solid = true
  Symmetric = false
FEATURE [Part::Fillet] Fillet039  label="top019"
  Base = -> Extrude047
  Edges = 1 edges r=2: [Edge35]
FEATURE [Sketcher::SketchObject] Sketch057
  FullyConstrained = false
  Placement = pos=(0,0,0) rot=(1,0,0;1.5708rad)
  sketch-geometry (24):
    g0: ArcOfCircle CenterX=-4 CenterY=-10.5 CenterZ=0 NormalX=0 NormalY=0 NormalZ=1 AngleXU=0 Radius=1.5 StartAngle=6e-16 EndAngle=3.14159
    g1: ArcOfCircle CenterX=-34.2 CenterY=-10.5 CenterZ=0 NormalX=0 NormalY=0 NormalZ=1 AngleXU=0 Radius=1.5 StartAngle=0 EndAngle=3.14159
    g2: ArcOfCircle CenterX=-34.2 CenterY=-27.7 CenterZ=0 NormalX=0 NormalY=0 NormalZ=1 AngleXU=0 Radius=1.5 StartAngle=3.14159 EndAngle=6.28319
    g3: ArcOfCircle CenterX=-4 CenterY=-27.7 CenterZ=0 NormalX=0 NormalY=0 NormalZ=1 AngleXU=0 Radius=1.5 StartAngle=3.1416 EndAngle=6.28319
    g4: ArcOfCircle CenterX=-10 CenterY=-4.3 CenterZ=0 NormalX=0 NormalY=0 NormalZ=1 AngleXU=0 Radius=1.5 StartAngle=2e-16 EndAngle=3.14159
    g5: ArcOfCircle CenterX=-16.1 CenterY=-1.8 CenterZ=0 NormalX=0 NormalY=0 NormalZ=1 AngleXU=0 Radius=1.5 StartAngle=5e-16 EndAngle=3.14159
    g6: ArcOfCircle CenterX=-22.1 CenterY=-1.8 CenterZ=0 NormalX=0 NormalY=0 NormalZ=1 AngleXU=0 Radius=1.5 StartAngle=5e-16 EndAngle=3.14159
    g7: ArcOfCircle CenterX=-28.2 CenterY=-4.3 CenterZ=0 NormalX=0 NormalY=0 NormalZ=1 AngleXU=0 Radius=1.5 StartAngle=2e-16 EndAngle=3.14159
    g8: ArcOfCircle CenterX=-10 CenterY=-33.9 CenterZ=0 NormalX=0 NormalY=0 NormalZ=1 AngleXU=0 Radius=1.5 StartAngle=3.14159 EndAngle=6.28319
    g9: ArcOfCircle CenterX=-16.1 CenterY=-36.4 CenterZ=0 NormalX=0 NormalY=0 NormalZ=1 AngleXU=0 Radius=1.5 StartAngle=3.14159 EndAngle=6.28319
    g10: ArcOfCircle CenterX=-22.1 CenterY=-36.4 CenterZ=0 NormalX=0 NormalY=0 NormalZ=1 AngleXU=0 Radius=1.5 StartAngle=3.14159 EndAngle=6.28319
    g11: ArcOfCircle CenterX=-28.2 CenterY=-33.9 CenterZ=0 NormalX=0 NormalY=0 NormalZ=1 AngleXU=0 Radius=1.5 StartAngle=3.14159 EndAngle=6.28319
    g12: LineSegment StartX=-35.7 StartY=-10.5 StartZ=0 EndX=-35.7 EndY=-27.7 EndZ=0
    g13: LineSegment StartX=-32.7 StartY=-10.5 StartZ=0 EndX=-32.7 EndY=-27.7 EndZ=0
    g14: LineSegment StartX=-29.7 StartY=-33.9 StartZ=0 EndX=-29.7 EndY=-4.3 EndZ=0
    g15: LineSegment StartX=-26.7 StartY=-33.9 StartZ=0 EndX=-26.7 EndY=-4.3 EndZ=0
    g16: LineSegment StartX=-2.5 StartY=-10.5 StartZ=0 EndX=-2.5 EndY=-27.7 EndZ=0
    g17: LineSegment StartX=-8.5 StartY=-4.3 StartZ=0 EndX=-8.5 EndY=-33.9 EndZ=0
    g18: LineSegment StartX=-5.5 StartY=-10.5 StartZ=0 EndX=-5.5 EndY=-27.7 EndZ=0
    g19: LineSegment StartX=-11.5 StartY=-4.3 StartZ=0 EndX=-11.5 EndY=-33.9 EndZ=0
    g20: LineSegment StartX=-14.6 StartY=-1.8 StartZ=0 EndX=-14.6 EndY=-36.4 EndZ=0
    g21: LineSegment StartX=-17.6 StartY=-1.8 StartZ=0 EndX=-17.6 EndY=-36.4 EndZ=0
    g22: LineSegment StartX=-20.6 StartY=-36.4 StartZ=0 EndX=-20.6 EndY=-1.8 EndZ=0
    g23: LineSegment StartX=-23.6 StartY=-1.8 StartZ=0 EndX=-23.6 EndY=-36.4 EndZ=0
  constraints (48):
    c: Block(g0)
    c: Block(g1)
    c: Block(g2)
    c: Block(g3)
    c: Block(g4)
    c: Block(g5)
    c: Block(g6)
    c: Block(g7)
    c: Block(g8)
    c: Block(g9)
    c: Block(g10)
    c: Block(g11)
    c: Coincident(g12,g1)
    c: Coincident(g12,g2)
    c: Vertical(g12)
    c: Coincident(g13,g1)
    c: Coincident(g13,g2)
    c: Vertical(g13)
    c: Coincident(g14,g11)
    c: Coincident(g14,g7)
    c: Vertical(g14)
    c: Coincident(g15,g11)
    c: Coincident(g15,g7)
    c: Vertical(g15)
    c: Coincident(g16,g0)
    c: Coincident(g16,g3)
    c: Vertical(g16)
    c: Coincident(g17,g4)
    c: Coincident(g17,g8)
    c: Vertical(g17)
    c: Coincident(g18,g0)
    c: Coincident(g18,g3)
    c: Vertical(g18)
    c: Coincident(g19,g4)
    c: Coincident(g19,g8)
    c: Vertical(g19)
    c: Coincident(g20,g5)
    c: Coincident(g20,g9)
    c: Vertical(g20)
    c: Coincident(g21,g5)
    c: Coincident(g21,g9)
    c: Vertical(g21)
    c: Coincident(g22,g10)
    c: Coincident(g22,g6)
    c: Vertical(g22)
    c: Coincident(g23,g6)
    c: Coincident(g23,g10)
    c: Vertical(g23)
FEATURE [Part::Extrusion] Extrude048  label="removeToCreateFanGrillHoles004"
  Base = -> Sketch057
  Dir = (0,-1,6e-16)
  DirMode = 2
  FaceMakerClass = Part::FaceMakerBullseye
  LengthFwd = 10
  LengthRev = 0
  Placement = pos=(65.4,44,54.82) rot=(0,0,1;0rad)
  Solid = true
  Symmetric = false
FEATURE [Part::Cut] Cut040  label="top021"
  Base = -> Fillet039
  Tool = -> Extrude048
FEATURE [Part::Cylinder] Cylinder041  label="removeToCreteHoleForPlugHousing034"
  Angle = 360
  AttacherType = Attacher::AttachEngine3D
  Height = 20
  Placement = pos=(-2,19,36) rot=(0,1,0;1.5708rad)
  Radius = 14.3
FEATURE [Part::MultiFuse] Fusion089  label="removeToCreteHoleForPlugHousing035"
  Shapes = -> [Box026,Cylinder041]
FEATURE [Part::Cylinder] Cylinder042
  Angle = 360
  AttacherType = Attacher::AttachEngine3D
  Height = 20
  Placement = pos=(0,0,36.15) rot=(0,0,1;0rad)
  Radius = 14.3
FEATURE [Part::Cylinder] Cylinder043
  Angle = 360
  AttacherType = Attacher::AttachEngine3D
  Height = 10
  Placement = pos=(0,0,36.15) rot=(0,0,1;0rad)
  Radius = 4
FEATURE [Part::Box] Box027  label="removeToCreteHoleForPlugHousing036"
  AttacherType = Attacher::AttachEngine3D
  Height = 28.6
  Length = 20
  Placement = pos=(106.15,0,21.7) rot=(0,0,1;0rad)
  Width = 19
FEATURE [Part::Cut] Cut041  label="top022"
  Base = -> Cut040
  Tool = -> Fusion087
FEATURE [Part::Cut] Cut039  label="top020"
  Base = -> Cut041
  Tool = -> Fusion089
FEATURE [Part::MultiFuse] Fusion090  label="removeToCreteHoleForPlugHousing037"
  Placement = pos=(70,19,36) rot=(0,1,0;1.5708rad)
  Shapes = -> [Cylinder042,Cylinder043]
FEATURE [Part::MultiFuse] Fusion088  label="removeToCreteHoleForPlugHousing033"
  Shapes = -> [Box027,Fusion090]
FEATURE [Part::Cut] Cut042  label="removeToCreteHoleForPlugHousing038"
  Base = -> Cut039
  Tool = -> Fusion088
FEATURE [Part::MultiFuse] Fusion091  label="removeFromTop"
  Shapes = -> [Fillet038,Fusion085,Fusion084,Fusion083,Extrude045]
FEATURE [Part::Cut] Cut043  label="REAL TOP ====="
  Base = -> Fillet036
  Tool = -> Fusion091
FEATURE [Part::MultiFuse] Fusion092  label="caseScrewPillarBracket016"
  Shapes = -> [Extrude030,Extrude031,Extrude032,Extrude033,Extrude034,Extrude035,Extrude036,Extrude037,Box013,Box014]
FEATURE [Sketcher::SketchObject] Sketch058  label="topSketch015"
  FullyConstrained = true
  sketch-geometry (20):
    g0: LineSegment StartX=5.21097e-06 StartY=3 StartZ=0 EndX=5.21097e-06 EndY=19 EndZ=0
    g1: ArcOfCircle CenterX=19 CenterY=19 CenterZ=0 NormalX=0 NormalY=0 NormalZ=1 AngleXU=0 Radius=19 StartAngle=1.5708 EndAngle=3.14159
    g2: ArcOfCircle CenterX=19 CenterY=19 CenterZ=0 NormalX=0 NormalY=0 NormalZ=1 AngleXU=0 Radius=16 StartAngle=1.5708 EndAngle=3.14159
    g3: LineSegment StartX=114 StartY=35 StartZ=0 EndX=19 EndY=35 EndZ=0
    g4: LineSegment StartX=5.21097e-06 StartY=3 StartZ=0 EndX=5.21097e-06 EndY=0 EndZ=0
    g5: LineSegment StartX=3 StartY=0 StartZ=0 EndX=5.21097e-06 EndY=0 EndZ=0
    g6: LineSegment StartX=3 StartY=19 StartZ=0 EndX=3 EndY=0 EndZ=0
    g7: LineSegment StartX=19 StartY=38 StartZ=0 EndX=124 EndY=38 EndZ=0
    g8: Circle CenterX=119 CenterY=35 CenterZ=0 NormalX=0 NormalY=0 NormalZ=1 AngleXU=0 Radius=1
    g9: Circle CenterX=121 CenterY=35 CenterZ=0 NormalX=0 NormalY=0 NormalZ=1 AngleXU=0 Radius=1
    g10: Circle CenterX=121 CenterY=33 CenterZ=0 NormalX=0 NormalY=0 NormalZ=1 AngleXU=0 Radius=1
    g11: BSplineCurve PolesCount=3 KnotsCount=2 Degree=2 IsPeriodic=0
    g12: GeomPoint X=119 Y=35 Z=0
    g13: GeomPoint X=121 Y=33 Z=0
    g14: LineSegment StartX=119 StartY=35 StartZ=0 EndX=114 EndY=35 EndZ=0
    g15: ArcOfCircle CenterX=105 CenterY=19 CenterZ=0 NormalX=0 NormalY=0 NormalZ=1 AngleXU=0 Radius=19 StartAngle=5.7297 EndAngle=6.28319
    g16: ArcOfCircle CenterX=105 CenterY=19 CenterZ=0 NormalX=0 NormalY=0 NormalZ=1 AngleXU=0 Radius=16 StartAngle=5.60905 EndAngle=6.28319
    g17: LineSegment StartX=121 StartY=33 StartZ=0 EndX=121 EndY=19 EndZ=0
    g18: LineSegment StartX=124 StartY=38 StartZ=0 EndX=124 EndY=19 EndZ=0
    g19: LineSegment StartX=117.5 StartY=9.01251 StartZ=0 EndX=121.163 EndY=9.0125 EndZ=0
  constraints (46):
    c: Vertical(g0)
    c: Block(g0)
    c: Coincident(g1,g0)
    c: Block(g1)
    c: Coincident(g2,g1)
    c: Block(g2)
    c: Coincident(g3,g2)
    c: Horizontal(g3)
    c: Tangent(g3,g2)
    c: Coincident(g4,g0)
    c: Distance(g4) = 3
    c: Vertical(g4)
    c: Coincident(g5,g4)
    c: Horizontal(g5)
    c: Coincident(g6,g2)
    c: Coincident(g6,g5)
    c: Vertical(g6)
    c: Horizontal(g7)
    c: Distance(g7) = 105
    c: Coincident(g7,g1)
    c: Block(g3)
    c: Weight(g8) = 1
    c: Equal(g8,g9)
    c: Equal(g8,g10)
    c: InternalAlignment(g8,g11)
    c: InternalAlignment(g9,g11)
    c: InternalAlignment(g10,g11)
    c: InternalAlignment(g12,g11)
    c: InternalAlignment(g13,g11)
    c: Block(g11)
    c: Coincident(g14,g11)
    c: Coincident(g14,g3)
    c: Horizontal(g14)
    c: Block(g15)
    c: Coincident(g16,g15)
    c: Block(g16)
    c: Coincident(g17,g11)
    c: Coincident(g17,g16)
    c: Vertical(g17)
    c: Distance(g17) = 14
    c: Coincident(g18,g7)
    c: Coincident(g18,g15)
    c: Vertical(g18)
    c: Distance(g18) = 19
    c: Coincident(g19,g16)
    c: Coincident(g19,g15)
FEATURE [Part::Extrusion] Extrude049  label="top023"
  Base = -> Sketch058
  Dir = (0,0,1)
  DirMode = 2
  FaceMakerClass = Part::FaceMakerBullseye
  LengthFwd = 72
  LengthRev = 0
  Solid = true
  Symmetric = false
FEATURE [Sketcher::SketchObject] Sketch059
  FullyConstrained = true
  MapMode = 3
  Placement = pos=(0,0,0) rot=(1,0,0;1.5708rad)
  Support = -> [Extrude049]
  sketch-geometry (8):
    g0: Circle CenterX=80.351 CenterY=-67.6202 CenterZ=0 NormalX=0 NormalY=0 NormalZ=1 AngleXU=0 Radius=2
    g1: Circle CenterX=80.351 CenterY=-67.6202 CenterZ=0 NormalX=0 NormalY=0 NormalZ=1 AngleXU=0 Radius=3
    g2: Circle CenterX=80.351 CenterY=-4.92017 CenterZ=0 NormalX=0 NormalY=0 NormalZ=1 AngleXU=0 Radius=2
    g3: Circle CenterX=80.351 CenterY=-4.92017 CenterZ=0 NormalX=0 NormalY=0 NormalZ=1 AngleXU=0 Radius=3
    g4: Circle CenterX=23.851 CenterY=-4.92017 CenterZ=0 NormalX=0 NormalY=0 NormalZ=1 AngleXU=0 Radius=2
    g5: Circle CenterX=23.851 CenterY=-4.92017 CenterZ=0 NormalX=0 NormalY=0 NormalZ=1 AngleXU=0 Radius=3
    g6: Circle CenterX=23.851 CenterY=-67.6202 CenterZ=0 NormalX=0 NormalY=0 NormalZ=1 AngleXU=0 Radius=2
    g7: Circle CenterX=23.851 CenterY=-67.6202 CenterZ=0 NormalX=0 NormalY=0 NormalZ=1 AngleXU=0 Radius=3
  constraints (8):
    c: Block(g3)
    c: Block(g2)
    c: Block(g1)
    c: Block(g0)
    c: Block(g6)
    c: Block(g7)
    c: Block(g4)
    c: Block(g5)
FEATURE [Sketcher::SketchObject] Sketch060
  FullyConstrained = true
  MapMode = 3
  Placement = pos=(0,0,0) rot=(1,0,0;1.5708rad)
  Support = -> [Extrude049]
  sketch-geometry (8):
    g0: Circle CenterX=80.351 CenterY=-67.6202 CenterZ=0 NormalX=0 NormalY=0 NormalZ=1 AngleXU=0 Radius=3
    g1: Circle CenterX=80.351 CenterY=-4.92017 CenterZ=0 NormalX=0 NormalY=0 NormalZ=1 AngleXU=0 Radius=3
    g2: Circle CenterX=23.851 CenterY=-4.92017 CenterZ=0 NormalX=0 NormalY=0 NormalZ=1 AngleXU=0 Radius=3
    g3: Circle CenterX=23.851 CenterY=-67.6202 CenterZ=0 NormalX=0 NormalY=0 NormalZ=1 AngleXU=0 Radius=3
    g4: Circle CenterX=23.851 CenterY=-67.6202 CenterZ=0 NormalX=0 NormalY=0 NormalZ=1 AngleXU=0 Radius=5
    g5: Circle CenterX=80.351 CenterY=-67.6202 CenterZ=0 NormalX=0 NormalY=0 NormalZ=1 AngleXU=0 Radius=5
    g6: Circle CenterX=23.851 CenterY=-4.92017 CenterZ=0 NormalX=0 NormalY=0 NormalZ=1 AngleXU=0 Radius=5
    g7: Circle CenterX=80.351 CenterY=-4.92017 CenterZ=0 NormalX=0 NormalY=0 NormalZ=1 AngleXU=0 Radius=5
  constraints (8):
    c: Block(g1)
    c: Block(g0)
    c: Block(g3)
    c: Block(g2)
    c: Block(g5)
    c: Block(g4)
    c: Block(g6)
    c: Block(g7)
FEATURE [Sketcher::SketchObject] Sketch061
  FullyConstrained = true
  MapMode = 3
  Placement = pos=(0,0,0) rot=(1,0,0;1.5708rad)
  sketch-geometry (8):
    g0: Circle CenterX=80.351 CenterY=-67.6202 CenterZ=0 NormalX=0 NormalY=0 NormalZ=1 AngleXU=0 Radius=3
    g1: Circle CenterX=80.351 CenterY=-4.92017 CenterZ=0 NormalX=0 NormalY=0 NormalZ=1 AngleXU=0 Radius=3
    g2: Circle CenterX=23.851 CenterY=-4.92017 CenterZ=0 NormalX=0 NormalY=0 NormalZ=1 AngleXU=0 Radius=3
    g3: Circle CenterX=23.851 CenterY=-67.6202 CenterZ=0 NormalX=0 NormalY=0 NormalZ=1 AngleXU=0 Radius=3
    g4: Circle CenterX=23.851 CenterY=-67.6202 CenterZ=0 NormalX=0 NormalY=0 NormalZ=1 AngleXU=0 Radius=5
    g5: Circle CenterX=80.351 CenterY=-67.6202 CenterZ=0 NormalX=0 NormalY=0 NormalZ=1 AngleXU=0 Radius=5
    g6: Circle CenterX=23.851 CenterY=-4.92017 CenterZ=0 NormalX=0 NormalY=0 NormalZ=1 AngleXU=0 Radius=5
    g7: Circle CenterX=80.351 CenterY=-4.92017 CenterZ=0 NormalX=0 NormalY=0 NormalZ=1 AngleXU=0 Radius=5
  constraints (8):
    c: Block(g1)
    c: Block(g0)
    c: Block(g3)
    c: Block(g2)
    c: Block(g5)
    c: Block(g4)
    c: Block(g6)
    c: Block(g7)
FEATURE [Sketcher::SketchObject] Sketch062  label="topSketch016"
  FullyConstrained = true
  sketch-geometry (20):
    g0: LineSegment StartX=5.21097e-06 StartY=3 StartZ=0 EndX=5.21097e-06 EndY=19 EndZ=0
    g1: ArcOfCircle CenterX=19 CenterY=19 CenterZ=0 NormalX=0 NormalY=0 NormalZ=1 AngleXU=0 Radius=19 StartAngle=1.5708 EndAngle=3.14159
    g2: ArcOfCircle CenterX=19 CenterY=19 CenterZ=0 NormalX=0 NormalY=0 NormalZ=1 AngleXU=0 Radius=16 StartAngle=1.5708 EndAngle=3.14159
    g3: LineSegment StartX=114 StartY=35 StartZ=0 EndX=19 EndY=35 EndZ=0
    g4: LineSegment StartX=5.21097e-06 StartY=3 StartZ=0 EndX=5.21097e-06 EndY=0 EndZ=0
    g5: LineSegment StartX=3 StartY=0 StartZ=0 EndX=5.21097e-06 EndY=0 EndZ=0
    g6: LineSegment StartX=3 StartY=19 StartZ=0 EndX=3 EndY=0 EndZ=0
    g7: LineSegment StartX=19 StartY=38 StartZ=0 EndX=124 EndY=38 EndZ=0
    g8: Circle CenterX=119 CenterY=35 CenterZ=0 NormalX=0 NormalY=0 NormalZ=1 AngleXU=0 Radius=1
    g9: Circle CenterX=121 CenterY=35 CenterZ=0 NormalX=0 NormalY=0 NormalZ=1 AngleXU=0 Radius=1
    g10: Circle CenterX=121 CenterY=33 CenterZ=0 NormalX=0 NormalY=0 NormalZ=1 AngleXU=0 Radius=1
    g11: BSplineCurve PolesCount=3 KnotsCount=2 Degree=2 IsPeriodic=0
    g12: GeomPoint X=119 Y=35 Z=0
    g13: GeomPoint X=121 Y=33 Z=0
    g14: LineSegment StartX=119 StartY=35 StartZ=0 EndX=114 EndY=35 EndZ=0
    g15: ArcOfCircle CenterX=105 CenterY=19 CenterZ=0 NormalX=0 NormalY=0 NormalZ=1 AngleXU=0 Radius=19 StartAngle=5.7297 EndAngle=6.28319
    g16: ArcOfCircle CenterX=105 CenterY=19 CenterZ=0 NormalX=0 NormalY=0 NormalZ=1 AngleXU=0 Radius=16 StartAngle=5.60905 EndAngle=6.28319
    g17: LineSegment StartX=121 StartY=33 StartZ=0 EndX=121 EndY=19 EndZ=0
    g18: LineSegment StartX=124 StartY=38 StartZ=0 EndX=124 EndY=19 EndZ=0
    g19: LineSegment StartX=117.5 StartY=9.01251 StartZ=0 EndX=121.163 EndY=9.0125 EndZ=0
  constraints (46):
    c: Vertical(g0)
    c: Block(g0)
    c: Coincident(g1,g0)
    c: Block(g1)
    c: Coincident(g2,g1)
    c: Block(g2)
    c: Coincident(g3,g2)
    c: Horizontal(g3)
    c: Tangent(g3,g2)
    c: Coincident(g4,g0)
    c: Distance(g4) = 3
    c: Vertical(g4)
    c: Coincident(g5,g4)
    c: Horizontal(g5)
    c: Coincident(g6,g2)
    c: Coincident(g6,g5)
    c: Vertical(g6)
    c: Horizontal(g7)
    c: Distance(g7) = 105
    c: Coincident(g7,g1)
    c: Block(g3)
    c: Weight(g8) = 1
    c: Equal(g8,g9)
    c: Equal(g8,g10)
    c: InternalAlignment(g8,g11)
    c: InternalAlignment(g9,g11)
    c: InternalAlignment(g10,g11)
    c: InternalAlignment(g12,g11)
    c: InternalAlignment(g13,g11)
    c: Block(g11)
    c: Coincident(g14,g11)
    c: Coincident(g14,g3)
    c: Horizontal(g14)
    c: Block(g15)
    c: Coincident(g16,g15)
    c: Block(g16)
    c: Coincident(g17,g11)
    c: Coincident(g17,g16)
    c: Vertical(g17)
    c: Distance(g17) = 14
    c: Coincident(g18,g7)
    c: Coincident(g18,g15)
    c: Vertical(g18)
    c: Distance(g18) = 19
    c: Coincident(g19,g16)
    c: Coincident(g19,g15)
FEATURE [Part::Extrusion] Extrude053  label="top024"
  Base = -> Sketch062
  Dir = (0,0,1)
  DirMode = 2
  FaceMakerClass = Part::FaceMakerBullseye
  LengthFwd = 72
  LengthRev = 0
  Solid = true
  Symmetric = false
FEATURE [Sketcher::SketchObject] Sketch063
  FullyConstrained = true
  MapMode = 3
  Placement = pos=(0,0,0) rot=(1,0,0;1.5708rad)
  Support = -> [Extrude053]
  sketch-geometry (8):
    g0: Circle CenterX=80.351 CenterY=-67.6202 CenterZ=0 NormalX=0 NormalY=0 NormalZ=1 AngleXU=0 Radius=2
    g1: Circle CenterX=80.351 CenterY=-67.6202 CenterZ=0 NormalX=0 NormalY=0 NormalZ=1 AngleXU=0 Radius=3
    g2: Circle CenterX=80.351 CenterY=-4.92017 CenterZ=0 NormalX=0 NormalY=0 NormalZ=1 AngleXU=0 Radius=2
    g3: Circle CenterX=80.351 CenterY=-4.92017 CenterZ=0 NormalX=0 NormalY=0 NormalZ=1 AngleXU=0 Radius=3
    g4: Circle CenterX=23.851 CenterY=-4.92017 CenterZ=0 NormalX=0 NormalY=0 NormalZ=1 AngleXU=0 Radius=2
    g5: Circle CenterX=23.851 CenterY=-4.92017 CenterZ=0 NormalX=0 NormalY=0 NormalZ=1 AngleXU=0 Radius=3
    g6: Circle CenterX=23.851 CenterY=-67.6202 CenterZ=0 NormalX=0 NormalY=0 NormalZ=1 AngleXU=0 Radius=2
    g7: Circle CenterX=23.851 CenterY=-67.6202 CenterZ=0 NormalX=0 NormalY=0 NormalZ=1 AngleXU=0 Radius=3
  constraints (8):
    c: Block(g3)
    c: Block(g2)
    c: Block(g1)
    c: Block(g0)
    c: Block(g6)
    c: Block(g7)
    c: Block(g4)
    c: Block(g5)
FEATURE [Part::Extrusion] Extrude054
  Base = -> Sketch063
  Dir = (0,-1,2e-16)
  DirMode = 2
  FaceMakerClass = Part::FaceMakerBullseye
  LengthFwd = 6
  LengthRev = 0
  Placement = pos=(0,9,0) rot=(0,0,1;0rad)
  Solid = true
  Symmetric = false
FEATURE [Sketcher::SketchObject] Sketch064  label="topSketch017"
  FullyConstrained = true
  sketch-geometry (20):
    g0: LineSegment StartX=5.21097e-06 StartY=3 StartZ=0 EndX=5.21097e-06 EndY=19 EndZ=0
    g1: ArcOfCircle CenterX=19 CenterY=19 CenterZ=0 NormalX=0 NormalY=0 NormalZ=1 AngleXU=0 Radius=19 StartAngle=1.5708 EndAngle=3.14159
    g2: ArcOfCircle CenterX=19 CenterY=19 CenterZ=0 NormalX=0 NormalY=0 NormalZ=1 AngleXU=0 Radius=16 StartAngle=1.5708 EndAngle=3.14159
    g3: LineSegment StartX=114 StartY=35 StartZ=0 EndX=19 EndY=35 EndZ=0
    g4: LineSegment StartX=5.21097e-06 StartY=3 StartZ=0 EndX=5.21097e-06 EndY=0 EndZ=0
    g5: LineSegment StartX=3 StartY=0 StartZ=0 EndX=5.21097e-06 EndY=0 EndZ=0
    g6: LineSegment StartX=3 StartY=19 StartZ=0 EndX=3 EndY=0 EndZ=0
    g7: LineSegment StartX=19 StartY=38 StartZ=0 EndX=124 EndY=38 EndZ=0
    g8: Circle CenterX=119 CenterY=35 CenterZ=0 NormalX=0 NormalY=0 NormalZ=1 AngleXU=0 Radius=1
    g9: Circle CenterX=121 CenterY=35 CenterZ=0 NormalX=0 NormalY=0 NormalZ=1 AngleXU=0 Radius=1
    g10: Circle CenterX=121 CenterY=33 CenterZ=0 NormalX=0 NormalY=0 NormalZ=1 AngleXU=0 Radius=1
    g11: BSplineCurve PolesCount=3 KnotsCount=2 Degree=2 IsPeriodic=0
    g12: GeomPoint X=119 Y=35 Z=0
    g13: GeomPoint X=121 Y=33 Z=0
    g14: LineSegment StartX=119 StartY=35 StartZ=0 EndX=114 EndY=35 EndZ=0
    g15: ArcOfCircle CenterX=105 CenterY=19 CenterZ=0 NormalX=0 NormalY=0 NormalZ=1 AngleXU=0 Radius=19 StartAngle=5.7297 EndAngle=6.28319
    g16: ArcOfCircle CenterX=105 CenterY=19 CenterZ=0 NormalX=0 NormalY=0 NormalZ=1 AngleXU=0 Radius=16 StartAngle=5.60905 EndAngle=6.28319
    g17: LineSegment StartX=121 StartY=33 StartZ=0 EndX=121 EndY=19 EndZ=0
    g18: LineSegment StartX=124 StartY=38 StartZ=0 EndX=124 EndY=19 EndZ=0
    g19: LineSegment StartX=117.5 StartY=9.01251 StartZ=0 EndX=121.163 EndY=9.0125 EndZ=0
  constraints (46):
    c: Vertical(g0)
    c: Block(g0)
    c: Coincident(g1,g0)
    c: Block(g1)
    c: Coincident(g2,g1)
    c: Block(g2)
    c: Coincident(g3,g2)
    c: Horizontal(g3)
    c: Tangent(g3,g2)
    c: Coincident(g4,g0)
    c: Distance(g4) = 3
    c: Vertical(g4)
    c: Coincident(g5,g4)
    c: Horizontal(g5)
    c: Coincident(g6,g2)
    c: Coincident(g6,g5)
    c: Vertical(g6)
    c: Horizontal(g7)
    c: Distance(g7) = 105
    c: Coincident(g7,g1)
    c: Block(g3)
    c: Weight(g8) = 1
    c: Equal(g8,g9)
    c: Equal(g8,g10)
    c: InternalAlignment(g8,g11)
    c: InternalAlignment(g9,g11)
    c: InternalAlignment(g10,g11)
    c: InternalAlignment(g12,g11)
    c: InternalAlignment(g13,g11)
    c: Block(g11)
    c: Coincident(g14,g11)
    c: Coincident(g14,g3)
    c: Horizontal(g14)
    c: Block(g15)
    c: Coincident(g16,g15)
    c: Block(g16)
    c: Coincident(g17,g11)
    c: Coincident(g17,g16)
    c: Vertical(g17)
    c: Distance(g17) = 14
    c: Coincident(g18,g7)
    c: Coincident(g18,g15)
    c: Vertical(g18)
    c: Distance(g18) = 19
    c: Coincident(g19,g16)
    c: Coincident(g19,g15)
FEATURE [Sketcher::SketchObject] Sketch065
  FullyConstrained = true
  MapMode = 3
  Placement = pos=(0,0,0) rot=(1,0,0;1.5708rad)
  sketch-geometry (8):
    g0: Circle CenterX=80.351 CenterY=-67.6202 CenterZ=0 NormalX=0 NormalY=0 NormalZ=1 AngleXU=0 Radius=3
    g1: Circle CenterX=80.351 CenterY=-4.92017 CenterZ=0 NormalX=0 NormalY=0 NormalZ=1 AngleXU=0 Radius=3
    g2: Circle CenterX=23.851 CenterY=-4.92017 CenterZ=0 NormalX=0 NormalY=0 NormalZ=1 AngleXU=0 Radius=3
    g3: Circle CenterX=23.851 CenterY=-67.6202 CenterZ=0 NormalX=0 NormalY=0 NormalZ=1 AngleXU=0 Radius=3
    g4: Circle CenterX=23.851 CenterY=-67.6202 CenterZ=0 NormalX=0 NormalY=0 NormalZ=1 AngleXU=0 Radius=5
    g5: Circle CenterX=80.351 CenterY=-67.6202 CenterZ=0 NormalX=0 NormalY=0 NormalZ=1 AngleXU=0 Radius=5
    g6: Circle CenterX=23.851 CenterY=-4.92017 CenterZ=0 NormalX=0 NormalY=0 NormalZ=1 AngleXU=0 Radius=5
    g7: Circle CenterX=80.351 CenterY=-4.92017 CenterZ=0 NormalX=0 NormalY=0 NormalZ=1 AngleXU=0 Radius=5
  constraints (8):
    c: Block(g1)
    c: Block(g0)
    c: Block(g3)
    c: Block(g2)
    c: Block(g5)
    c: Block(g4)
    c: Block(g6)
    c: Block(g7)
FEATURE [Part::Extrusion] Extrude056
  Base = -> Sketch065
  Dir = (0,-1,2e-16)
  DirMode = 2
  FaceMakerClass = Part::FaceMakerBullseye
  LengthFwd = 2
  LengthRev = 0
  Solid = true
  Symmetric = false
FEATURE [Part::Extrusion] Extrude057  label="top025"
  Base = -> Sketch064
  Dir = (0,0,1)
  DirMode = 2
  FaceMakerClass = Part::FaceMakerBullseye
  LengthFwd = 72
  LengthRev = 0
  Solid = true
  Symmetric = false
FEATURE [Sketcher::SketchObject] Sketch066
  FullyConstrained = true
  MapMode = 3
  Placement = pos=(0,0,0) rot=(1,0,0;1.5708rad)
  Support = -> [Extrude057]
  sketch-geometry (8):
    g0: Circle CenterX=80.351 CenterY=-67.6202 CenterZ=0 NormalX=0 NormalY=0 NormalZ=1 AngleXU=0 Radius=3
    g1: Circle CenterX=80.351 CenterY=-4.92017 CenterZ=0 NormalX=0 NormalY=0 NormalZ=1 AngleXU=0 Radius=3
    g2: Circle CenterX=23.851 CenterY=-4.92017 CenterZ=0 NormalX=0 NormalY=0 NormalZ=1 AngleXU=0 Radius=3
    g3: Circle CenterX=23.851 CenterY=-67.6202 CenterZ=0 NormalX=0 NormalY=0 NormalZ=1 AngleXU=0 Radius=3
    g4: Circle CenterX=23.851 CenterY=-67.6202 CenterZ=0 NormalX=0 NormalY=0 NormalZ=1 AngleXU=0 Radius=5
    g5: Circle CenterX=80.351 CenterY=-67.6202 CenterZ=0 NormalX=0 NormalY=0 NormalZ=1 AngleXU=0 Radius=5
    g6: Circle CenterX=23.851 CenterY=-4.92017 CenterZ=0 NormalX=0 NormalY=0 NormalZ=1 AngleXU=0 Radius=5
    g7: Circle CenterX=80.351 CenterY=-4.92017 CenterZ=0 NormalX=0 NormalY=0 NormalZ=1 AngleXU=0 Radius=5
  constraints (8):
    c: Block(g1)
    c: Block(g0)
    c: Block(g3)
    c: Block(g2)
    c: Block(g5)
    c: Block(g4)
    c: Block(g6)
    c: Block(g7)
FEATURE [Part::Extrusion] Extrude055
  Base = -> Sketch066
  Dir = (0,-1,2e-16)
  DirMode = 2
  FaceMakerClass = Part::FaceMakerBullseye
  LengthFwd = 2
  LengthRev = 0
  Solid = true
  Symmetric = false
FEATURE [Part::Fillet] Fillet041
  Base = -> Extrude056
  Edges = 4 edges r=1.99: [Edge6,Edge12,Edge18,Edge24]
FEATURE [Part::Cut] Cut045
  Base = -> Extrude055
  Placement = pos=(0,6,0) rot=(0,0,1;0rad)
  Tool = -> Fillet041
FEATURE [Part::MultiFuse] Fusion095  label="pcbScrewPillars"
  Placement = pos=(-3.2,-1,72.3) rot=(0,0,1;0rad)
  Shapes = -> [Cut045,Extrude054]
FEATURE [Part::Feature] Face113
  shape: bbox 3.2 x 1.5 x 2e-07 mm, 1 faces, 0 solids (baked)
FEATURE [Part::Revolution] Revolve121  label="backCaseScrewRetainer002"
  Angle = 360
  Axis = (0,1,0)
  Base = (0,0,0)
  FaceMakerClass = Part::FaceMakerBullseye
  Placement = pos=(12.5,3,62) rot=(0,0,1;0rad)
  Solid = false
  Source = -> Face113
  Symmetric = false
FEATURE [Part::Feature] Face114
  shape: bbox 3.2 x 1.5 x 2e-07 mm, 1 faces, 0 solids (baked)
FEATURE [Part::Feature] Face115
  shape: bbox 3.2 x 1.5 x 2e-07 mm, 1 faces, 0 solids (baked)
FEATURE [Part::Feature] Face116
  shape: bbox 3.2 x 1.5 x 2e-07 mm, 1 faces, 0 solids (baked)
FEATURE [Part::Revolution] Revolve122  label="frontCaseScrewRetainer004"
  Angle = 360
  Axis = (0,1,0)
  Base = (0,0,0)
  FaceMakerClass = Part::FaceMakerBullseye
  Placement = pos=(89.5,3,68.5) rot=(0,0,1;0rad)
  Solid = false
  Source = -> Face115
  Symmetric = false
FEATURE [Part::Revolution] Revolve123  label="frontCaseScrewRetainer005"
  Angle = 360
  Axis = (0,1,0)
  Base = (0,0,0)
  FaceMakerClass = Part::FaceMakerBullseye
  Placement = pos=(89.5,3,3.5) rot=(0,0,1;0rad)
  Solid = false
  Source = -> Face116
  Symmetric = false
FEATURE [Part::Revolution] Revolve124  label="backCaseScrewRetainer003"
  Angle = 360
  Axis = (0,1,0)
  Base = (0,0,0)
  FaceMakerClass = Part::FaceMakerBullseye
  Placement = pos=(12.5,3,10) rot=(0,0,1;0rad)
  Solid = false
  Source = -> Face114
  Symmetric = false
FEATURE [Part::Feature] Face117
  shape: bbox 3.6 x 3.2 x 2e-07 mm, 1 faces, 0 solids (baked)
FEATURE [Part::Revolution] Revolve125  label="moreFrontCaseScrewRetainer004"
  Angle = 360
  Axis = (0,1,0)
  Base = (0,0,0)
  FaceMakerClass = Part::FaceMakerBullseye
  Placement = pos=(109.5,4.5,68.5) rot=(0,0,1;0rad)
  Solid = false
  Source = -> Face117
  Symmetric = false
FEATURE [Part::Feature] Face118
  shape: bbox 3.6 x 3.2 x 2e-07 mm, 1 faces, 0 solids (baked)
FEATURE [Part::Revolution] Revolve126  label="moreFrontCaseScrewRetainer005"
  Angle = 360
  Axis = (0,1,0)
  Base = (0,0,0)
  FaceMakerClass = Part::FaceMakerBullseye
  Placement = pos=(109.5,4.5,3.5) rot=(0,0,1;0rad)
  Solid = false
  Source = -> Face118
  Symmetric = false
FEATURE [Part::MultiFuse] Fusion096  label="screwRetainers001"
  Shapes = -> [Revolve126,Revolve125,Revolve124,Revolve123,Revolve122,Revolve121]
FEATURE [Part::Feature] Face119
  shape: bbox 10 x 16.5 x 2e-07 mm, 1 faces, 0 solids (baked)
FEATURE [Part::Revolution] Revolve130  label="plugHousing050"
  Angle = 360
  Axis = (0,1,0)
  Base = (0,0,0)
  FaceMakerClass = Part::FaceMakerBullseye
  Placement = pos=(0,0,36.15) rot=(0,0,1;0rad)
  Solid = false
  Source = -> Face119
  Symmetric = false
FEATURE [Part::Feature] Face120
  shape: bbox 10 x 16.5 x 2e-07 mm, 1 faces, 0 solids (baked)
FEATURE [Part::Feature] Face121
  shape: bbox 10 x 16.5 x 2e-07 mm, 1 faces, 0 solids (baked)
FEATURE [Part::Revolution] Revolve127  label="plugHousing047"
  Angle = 360
  Axis = (0,1,0)
  Base = (0,0,0)
  FaceMakerClass = Part::FaceMakerBullseye
  Placement = pos=(0,0,36.15) rot=(0,0,1;0rad)
  Solid = false
  Source = -> Face121
  Symmetric = false
FEATURE [Part::Feature] Face122
  shape: bbox 10 x 16.5 x 2e-07 mm, 1 faces, 0 solids (baked)
FEATURE [Part::Feature] Face123
  shape: bbox 10 x 16.5 x 2e-07 mm, 1 faces, 0 solids (baked)
FEATURE [Part::Revolution] Revolve128  label="plugHousing048"
  Angle = 360
  Axis = (0,1,0)
  Base = (0,0,0)
  FaceMakerClass = Part::FaceMakerBullseye
  Placement = pos=(0,0,36.15) rot=(0,0,1;0rad)
  Solid = false
  Source = -> Face123
  Symmetric = false
FEATURE [Part::MultiFuse] Fusion100  label="plugHousing054"
  Placement = pos=(0,0,0) rot=(0,0,1;1.5708rad)
  Shapes = -> [Revolve130,Revolve128]
FEATURE [Part::Feature] Face124
  shape: bbox 10 x 16.5 x 2e-07 mm, 1 faces, 0 solids (baked)
FEATURE [Part::Feature] Face125
  shape: bbox 10 x 16.5 x 2e-07 mm, 1 faces, 0 solids (baked)
FEATURE [Part::Revolution] Revolve129  label="plugHousing049"
  Angle = 360
  Axis = (0,1,0)
  Base = (0,0,0)
  FaceMakerClass = Part::FaceMakerBullseye
  Placement = pos=(0,0,36.15) rot=(0,0,1;0rad)
  Solid = false
  Source = -> Face125
  Symmetric = false
FEATURE [Part::Feature] Face126
  shape: bbox 10 x 16.5 x 2e-07 mm, 1 faces, 0 solids (baked)
FEATURE [Part::Revolution] Revolve131  label="plugHousing058"
  Angle = 360
  Axis = (0,1,0)
  Base = (0,0,0)
  FaceMakerClass = Part::FaceMakerBullseye
  Placement = pos=(0,0,36.15) rot=(0,0,1;0rad)
  Solid = false
  Source = -> Face120
  Symmetric = false
FEATURE [Part::MultiFuse] Fusion099  label="plugHousing053"
  Placement = pos=(0,0,0) rot=(0,0,1;1.5708rad)
  Shapes = -> [Revolve127,Revolve131]
FEATURE [Part::MultiFuse] Fusion102  label="plugHousing056"
  Placement = pos=(0,19,0) rot=(0,0,1;3.14159rad)
  Shapes = -> [Fusion100,Fusion099]
FEATURE [Part::Revolution] Revolve132  label="plugHousing059"
  Angle = 360
  Axis = (0,1,0)
  Base = (0,0,0)
  FaceMakerClass = Part::FaceMakerBullseye
  Placement = pos=(0,0,36.15) rot=(0,0,1;0rad)
  Solid = false
  Source = -> Face126
  Symmetric = false
FEATURE [Part::Revolution] Revolve133  label="plugHousing060"
  Angle = 360
  Axis = (0,1,0)
  Base = (0,0,0)
  FaceMakerClass = Part::FaceMakerBullseye
  Placement = pos=(0,0,36.15) rot=(0,0,1;0rad)
  Solid = false
  Source = -> Face122
  Symmetric = false
FEATURE [Part::MultiFuse] Fusion097  label="plugHousing051"
  Placement = pos=(0,0,0) rot=(0,0,1;1.5708rad)
  Shapes = -> [Revolve133,Revolve132]
FEATURE [Part::Revolution] Revolve134  label="plugHousing061"
  Angle = 360
  Axis = (0,1,0)
  Base = (0,0,0)
  FaceMakerClass = Part::FaceMakerBullseye
  Placement = pos=(0,0,36.15) rot=(0,0,1;0rad)
  Solid = false
  Source = -> Face124
  Symmetric = false
FEATURE [Part::MultiFuse] Fusion101  label="plugHousing055"
  Placement = pos=(0,0,0) rot=(0,0,1;1.5708rad)
  Shapes = -> [Revolve129,Revolve134]
FEATURE [Part::MultiFuse] Fusion098  label="plugHousing052"
  Placement = pos=(0,19,0) rot=(0,0,1;3.14159rad)
  Shapes = -> [Fusion097,Fusion101]
FEATURE [Part::MultiFuse] Fusion103  label="plugHousing057"
  Placement = pos=(122.621,0,-0.15) rot=(0,0,1;0rad)
  Shapes = -> [Fusion102,Fusion098]
FEATURE [Part::Box] Box028  label="Cube015"
  AttacherType = Attacher::AttachEngine3D
  Height = 28
  Length = 3
  Placement = pos=(110.7,19,22) rot=(0,0,1;0rad)
  Width = 15.7
FEATURE [Part::Cylinder] Cylinder044
  Angle = 360
  AttacherType = Attacher::AttachEngine3D
  Height = 20
  Placement = pos=(0,0,36.15) rot=(0,0,1;0rad)
  Radius = 10.3
FEATURE [Part::Cylinder] Cylinder045
  Angle = 360
  AttacherType = Attacher::AttachEngine3D
  Height = 10
  Placement = pos=(0,0,36.15) rot=(0,0,1;0rad)
  Radius = 4
FEATURE [Part::MultiFuse] Fusion104  label="removeToCreteHoleForPlugHousing040"
  Placement = pos=(70,19,36) rot=(0,1,0;1.5708rad)
  Shapes = -> [Cylinder044,Cylinder045]
FEATURE [Part::Cut] Cut046  label="plugHousingTab003"
  Base = -> Box028
  Tool = -> Fusion104
FEATURE [Part::MultiFuse] Fusion105  label="plugHousing062"
  Shapes = -> [Fusion103,Cut046]
FEATURE [Part::Fillet] Fillet042
  Base = -> Fusion105
  Edges = 1 edges r=2: [Edge25]
FEATURE [Part::Fillet] Fillet043  label="plugHousing063"
  Base = -> Fillet042
  Edges = 1 edges r=2: [Edge8]
  Placement = pos=(7,0,0) rot=(0,0,1;0rad)
FEATURE [Part::Feature] Face127
  shape: bbox 10 x 16.5 x 2e-07 mm, 1 faces, 0 solids (baked)
FEATURE [Part::Feature] Face128
  shape: bbox 10 x 16.5 x 2e-07 mm, 1 faces, 0 solids (baked)
FEATURE [Part::Revolution] Revolve137  label="plugHousing070"
  Angle = 360
  Axis = (0,1,0)
  Base = (0,0,0)
  FaceMakerClass = Part::FaceMakerBullseye
  Placement = pos=(0,0,36.15) rot=(0,0,1;0rad)
  Solid = false
  Source = -> Face127
  Symmetric = false
FEATURE [Part::Revolution] Revolve140  label="plugHousing073"
  Angle = 360
  Axis = (0,1,0)
  Base = (0,0,0)
  FaceMakerClass = Part::FaceMakerBullseye
  Placement = pos=(0,0,36.15) rot=(0,0,1;0rad)
  Solid = false
  Source = -> Face128
  Symmetric = false
FEATURE [Part::Feature] Face129
  shape: bbox 10 x 16.5 x 2e-07 mm, 1 faces, 0 solids (baked)
FEATURE [Part::Revolution] Revolve138  label="plugHousing071"
  Angle = 360
  Axis = (0,1,0)
  Base = (0,0,0)
  FaceMakerClass = Part::FaceMakerBullseye
  Placement = pos=(0,0,36.15) rot=(0,0,1;0rad)
  Solid = false
  Source = -> Face129
  Symmetric = false
FEATURE [Part::Feature] Face130
  shape: bbox 10 x 16.5 x 2e-07 mm, 1 faces, 0 solids (baked)
FEATURE [Part::Revolution] Revolve139  label="plugHousing072"
  Angle = 360
  Axis = (0,1,0)
  Base = (0,0,0)
  FaceMakerClass = Part::FaceMakerBullseye
  Placement = pos=(0,0,36.15) rot=(0,0,1;0rad)
  Solid = false
  Source = -> Face130
  Symmetric = false
FEATURE [Part::Feature] Face131
  shape: bbox 10 x 16.5 x 2e-07 mm, 1 faces, 0 solids (baked)
FEATURE [Part::Revolution] Revolve135  label="plugHousing068"
  Angle = 360
  Axis = (0,1,0)
  Base = (0,0,0)
  FaceMakerClass = Part::FaceMakerBullseye
  Placement = pos=(0,0,36.15) rot=(0,0,1;0rad)
  Solid = false
  Source = -> Face131
  Symmetric = false
FEATURE [Part::MultiFuse] Fusion112  label="plugHousing078"
  Placement = pos=(0,0,0) rot=(0,0,1;1.5708rad)
  Shapes = -> [Revolve135,Revolve139]
FEATURE [Part::Feature] Face132
  shape: bbox 10 x 16.5 x 2e-07 mm, 1 faces, 0 solids (baked)
FEATURE [Part::Revolution] Revolve141  label="plugHousing074"
  Angle = 360
  Axis = (0,1,0)
  Base = (0,0,0)
  FaceMakerClass = Part::FaceMakerBullseye
  Placement = pos=(0,0,36.15) rot=(0,0,1;0rad)
  Solid = false
  Source = -> Face132
  Symmetric = false
FEATURE [Part::MultiFuse] Fusion110  label="plugHousing076"
  Placement = pos=(0,0,0) rot=(0,0,1;1.5708rad)
  Shapes = -> [Revolve141,Revolve140]
FEATURE [Part::Feature] Face133
  shape: bbox 10 x 16.5 x 2e-07 mm, 1 faces, 0 solids (baked)
FEATURE [Part::Revolution] Revolve136  label="plugHousing069"
  Angle = 360
  Axis = (0,1,0)
  Base = (0,0,0)
  FaceMakerClass = Part::FaceMakerBullseye
  Placement = pos=(0,0,36.15) rot=(0,0,1;0rad)
  Solid = false
  Source = -> Face133
  Symmetric = false
FEATURE [Part::MultiFuse] Fusion106  label="plugHousing064"
  Placement = pos=(0,0,0) rot=(0,0,1;1.5708rad)
  Shapes = -> [Revolve138,Revolve136]
FEATURE [Part::MultiFuse] Fusion108  label="plugHousing066"
  Placement = pos=(0,19,0) rot=(0,0,1;3.14159rad)
  Shapes = -> [Fusion106,Fusion112]
FEATURE [Part::Feature] Face134
  shape: bbox 10 x 16.5 x 2e-07 mm, 1 faces, 0 solids (baked)
FEATURE [Part::Revolution] Revolve142  label="plugHousing075"
  Angle = 360
  Axis = (0,1,0)
  Base = (0,0,0)
  FaceMakerClass = Part::FaceMakerBullseye
  Placement = pos=(0,0,36.15) rot=(0,0,1;0rad)
  Solid = false
  Source = -> Face134
  Symmetric = false
FEATURE [Part::MultiFuse] Fusion107  label="plugHousing065"
  Placement = pos=(0,0,0) rot=(0,0,1;1.5708rad)
  Shapes = -> [Revolve137,Revolve142]
FEATURE [Part::MultiFuse] Fusion111  label="plugHousing077"
  Placement = pos=(0,19,0) rot=(0,0,1;3.14159rad)
  Shapes = -> [Fusion110,Fusion107]
FEATURE [Part::MultiFuse] Fusion109  label="plugHousing067"
  Placement = pos=(131.236,0,-0.15) rot=(0,0,1;0rad)
  Shapes = -> [Fusion108,Fusion111]
FEATURE [Part::MultiFuse] Fusion113  label="plugHousing079"
  Shapes = -> [Fillet043,Fusion109]
FEATURE [Part::Feature] Face135
  shape: bbox 3.5 x 17.8 x 2e-07 mm, 1 faces, 0 solids (baked)
FEATURE [Part::Revolution] Revolve143  label="removeToCreateScrewAndThreadedInsertHole049"
  Angle = 360
  Axis = (0,1,0)
  Base = (0,0,0)
  FaceMakerClass = Part::FaceMakerBullseye
  Placement = pos=(12.5,0,10) rot=(0,0,1;0rad)
  Solid = false
  Source = -> Face135
  Symmetric = false
FEATURE [Part::Feature] Face136
  shape: bbox 3.5 x 17.8 x 2e-07 mm, 1 faces, 0 solids (baked)
FEATURE [Part::Revolution] Revolve144  label="removeToCreateScrewAndThreadedInsertHole050"
  Angle = 360
  Axis = (0,1,0)
  Base = (0,0,0)
  FaceMakerClass = Part::FaceMakerBullseye
  Placement = pos=(12.5,0,62) rot=(0,0,1;0rad)
  Solid = false
  Source = -> Face136
  Symmetric = false
FEATURE [Part::Feature] Face137
  shape: bbox 3.5 x 17.8 x 2e-07 mm, 1 faces, 0 solids (baked)
FEATURE [Part::Revolution] Revolve145  label="removeToCreateScrewAndThreadedInsertHole051"
  Angle = 360
  Axis = (0,1,0)
  Base = (0,0,0)
  FaceMakerClass = Part::FaceMakerBullseye
  Placement = pos=(89.5,0,68.5) rot=(0,0,1;0rad)
  Solid = false
  Source = -> Face137
  Symmetric = false
FEATURE [Part::Feature] Face138
  shape: bbox 3.5 x 17.8 x 2e-07 mm, 1 faces, 0 solids (baked)
FEATURE [Part::Revolution] Revolve146  label="removeToCreateScrewAndThreadedInsertHole052"
  Angle = 360
  Axis = (0,1,0)
  Base = (0,0,0)
  FaceMakerClass = Part::FaceMakerBullseye
  Placement = pos=(89.5,0,3.5) rot=(0,0,1;0rad)
  Solid = false
  Source = -> Face138
  Symmetric = false
FEATURE [Part::Feature] Face139
  shape: bbox 3.5 x 17.8 x 2e-07 mm, 1 faces, 0 solids (baked)
FEATURE [Part::Revolution] Revolve147  label="removeToCreateScrewAndThreadedInsertHole053"
  Angle = 360
  Axis = (0,1,0)
  Base = (0,0,0)
  FaceMakerClass = Part::FaceMakerBullseye
  Placement = pos=(109.5,4.7,3.5) rot=(0,0,1;0rad)
  Solid = false
  Source = -> Face139
  Symmetric = false
FEATURE [Part::Feature] Face140
  shape: bbox 3.5 x 17.8 x 2e-07 mm, 1 faces, 0 solids (baked)
FEATURE [Part::Revolution] Revolve148  label="removeToCreateScrewAndThreadedInsertHole054"
  Angle = 360
  Axis = (0,1,0)
  Base = (0,0,0)
  FaceMakerClass = Part::FaceMakerBullseye
  Placement = pos=(109.5,4.7,68.5) rot=(0,0,1;0rad)
  Solid = false
  Source = -> Face140
  Symmetric = false
FEATURE [Part::MultiFuse] Fusion114  label="removeToCreateScrewAndThreadedInsertHole055"
  Shapes = -> [Revolve148,Revolve147,Revolve146,Revolve145,Revolve144,Revolve143]
FEATURE [Part::Cut] Cut047  label="casePillars004"
  Base = -> Cut037
  Tool = -> Fusion114
FEATURE [Part::Feature] Face141
  shape: bbox 3.5 x 17.8 x 2e-07 mm, 1 faces, 0 solids (baked)
FEATURE [Part::Feature] Face142
  shape: bbox 3.5 x 17.8 x 2e-07 mm, 1 faces, 0 solids (baked)
FEATURE [Part::Feature] Face143
  shape: bbox 3.5 x 17.8 x 2e-07 mm, 1 faces, 0 solids (baked)
FEATURE [Part::Revolution] Revolve149  label="removeToCreateScrewAndThreadedInsertHole057"
  Angle = 360
  Axis = (0,1,0)
  Base = (0,0,0)
  FaceMakerClass = Part::FaceMakerBullseye
  Placement = pos=(12.5,0,10) rot=(0,0,1;0rad)
  Solid = false
  Source = -> Face141
  Symmetric = false
FEATURE [Part::Feature] Face144
  shape: bbox 3.5 x 17.8 x 2e-07 mm, 1 faces, 0 solids (baked)
FEATURE [Part::Feature] Face145
  shape: bbox 3.5 x 17.8 x 2e-07 mm, 1 faces, 0 solids (baked)
FEATURE [Part::Feature] Face146
  shape: bbox 3.5 x 17.8 x 2e-07 mm, 1 faces, 0 solids (baked)
FEATURE [Part::Revolution] Revolve150  label="removeToCreateScrewAndThreadedInsertHole058"
  Angle = 360
  Axis = (0,1,0)
  Base = (0,0,0)
  FaceMakerClass = Part::FaceMakerBullseye
  Placement = pos=(12.5,0,62) rot=(0,0,1;0rad)
  Solid = false
  Source = -> Face146
  Symmetric = false
FEATURE [Part::Revolution] Revolve151  label="removeToCreateScrewAndThreadedInsertHole059"
  Angle = 360
  Axis = (0,1,0)
  Base = (0,0,0)
  FaceMakerClass = Part::FaceMakerBullseye
  Placement = pos=(89.5,0,68.5) rot=(0,0,1;0rad)
  Solid = false
  Source = -> Face143
  Symmetric = false
FEATURE [Part::Revolution] Revolve152  label="removeToCreateScrewAndThreadedInsertHole060"
  Angle = 360
  Axis = (0,1,0)
  Base = (0,0,0)
  FaceMakerClass = Part::FaceMakerBullseye
  Placement = pos=(89.5,0,3.5) rot=(0,0,1;0rad)
  Solid = false
  Source = -> Face142
  Symmetric = false
FEATURE [Part::Revolution] Revolve153  label="removeToCreateScrewAndThreadedInsertHole061"
  Angle = 360
  Axis = (0,1,0)
  Base = (0,0,0)
  FaceMakerClass = Part::FaceMakerBullseye
  Placement = pos=(109.5,4.7,3.5) rot=(0,0,1;0rad)
  Solid = false
  Source = -> Face145
  Symmetric = false
FEATURE [Part::Revolution] Revolve154  label="removeToCreateScrewAndThreadedInsertHole062"
  Angle = 360
  Axis = (0,1,0)
  Base = (0,0,0)
  FaceMakerClass = Part::FaceMakerBullseye
  Placement = pos=(109.5,4.7,68.5) rot=(0,0,1;0rad)
  Solid = false
  Source = -> Face144
  Symmetric = false
FEATURE [Part::MultiFuse] Fusion115  label="removeToCreateScrewAndThreadedInsertHole056"
  Shapes = -> [Revolve154,Revolve153,Revolve152,Revolve151,Revolve150,Revolve149]
FEATURE [Part::Feature] Face147
  shape: bbox 9.8 x 26.5 x 2e-07 mm, 1 faces, 0 solids (baked)
FEATURE [Part::Revolution] Revolve155
  Angle = 360
  Axis = (0,1,0)
  Base = (0,0,0)
  FaceMakerClass = Part::FaceMakerBullseye
  Placement = pos=(0,0,0) rot=(0,0,1;1.5708rad)
  Solid = false
  Source = -> Face147
  Symmetric = false
FEATURE [Part::Feature] Face148
  shape: bbox 9.8 x 26.5 x 2e-07 mm, 1 faces, 0 solids (baked)
FEATURE [Part::Revolution] Revolve156
  Angle = 360
  Axis = (0,1,0)
  Base = (0,0,0)
  FaceMakerClass = Part::FaceMakerBullseye
  Placement = pos=(0,0,0) rot=(0,0,1;1.5708rad)
  Solid = false
  Source = -> Face148
  Symmetric = false
FEATURE [Part::MultiFuse] Fusion116
  Placement = pos=(-18,19,36) rot=(0,0,1;0rad)
  Shapes = -> [Revolve156,Revolve155]
FEATURE [Part::Box] Box029  label="Cube016"
  AttacherType = Attacher::AttachEngine3D
  Height = 28
  Length = 3
  Placement = pos=(110.7,19,22) rot=(0,0,1;0rad)
  Width = 15.7
FEATURE [Part::Cylinder] Cylinder046
  Angle = 360
  AttacherType = Attacher::AttachEngine3D
  Height = 10
  Placement = pos=(0,0,36.15) rot=(0,0,1;0rad)
  Radius = 4
FEATURE [Part::Cylinder] Cylinder047
  Angle = 360
  AttacherType = Attacher::AttachEngine3D
  Height = 20
  Placement = pos=(0,0,36.15) rot=(0,0,1;0rad)
  Radius = 10.3
FEATURE [Part::MultiFuse] Fusion117  label="removeToCreteHoleForPlugHousing041"
  Placement = pos=(70,19,36) rot=(0,1,0;1.5708rad)
  Shapes = -> [Cylinder047,Cylinder046]
FEATURE [Part::Cut] Cut049  label="plugHousingTab004"
  Base = -> Box029
  Placement = pos=(-107.4,-14,0) rot=(0,0,1;0rad)
  Tool = -> Fusion117
FEATURE [Part::Box] Box030  label="Cube017"
  AttacherType = Attacher::AttachEngine3D
  Height = 28
  Length = 3
  Placement = pos=(110.7,19,22) rot=(0,0,1;0rad)
  Width = 15.7
FEATURE [Part::Cylinder] Cylinder048
  Angle = 360
  AttacherType = Attacher::AttachEngine3D
  Height = 10
  Placement = pos=(0,0,36.15) rot=(0,0,1;0rad)
  Radius = 4
FEATURE [Part::Cylinder] Cylinder049
  Angle = 360
  AttacherType = Attacher::AttachEngine3D
  Height = 20
  Placement = pos=(0,0,36.15) rot=(0,0,1;0rad)
  Radius = 10.3
FEATURE [Part::MultiFuse] Fusion118  label="removeToCreteHoleForPlugHousing042"
  Placement = pos=(70,19,36) rot=(0,1,0;1.5708rad)
  Shapes = -> [Cylinder049,Cylinder048]
FEATURE [Part::Cut] Cut050  label="plugHousingTab005"
  Base = -> Box030
  Placement = pos=(-107.4,-14,0) rot=(0,0,1;0rad)
  Tool = -> Fusion118
FEATURE [Part::MultiFuse] Fusion119
  Placement = pos=(9.6,23,0) rot=(0,0,1;3.14159rad)
  Shapes = -> [Cut049,Cut050]
FEATURE [Part::Box] Box031  label="Cube018"
  AttacherType = Attacher::AttachEngine3D
  Height = 10
  Length = 3
  Placement = pos=(3.3,4,12) rot=(0,0,1;0rad)
  Width = 10
FEATURE [Part::Fillet] Fillet044
  Base = -> Box031
  Edges = 1 edges r=2: [Edge11]
FEATURE [Part::Box] Box032  label="Cube019"
  AttacherType = Attacher::AttachEngine3D
  Height = 10
  Length = 3
  Placement = pos=(3.3,4,50) rot=(0,0,1;0rad)
  Width = 10
FEATURE [Part::Fillet] Fillet045
  Base = -> Box032
  Edges = 1 edges r=2: [Edge12]
FEATURE [Part::Box] Box033  label="Cube020"
  AttacherType = Attacher::AttachEngine3D
  Height = 28
  Length = 4
  Placement = pos=(5,0,22) rot=(0,0,1;0rad)
  Width = 10
FEATURE [Part::Fillet] Fillet046
  Base = -> Box033
  Edges = 1 edges r=1: [Edge7]
FEATURE [Part::Fillet] Fillet047
  Base = -> Fillet046
  Edges = 1 edges r=2: [Edge5]
FEATURE [Part::Fillet] Fillet048
  Base = -> Fillet047
  Edges = 1 edges r=2: [Edge2]
FEATURE [Part::Cylinder] Cylinder050
  Angle = 360
  AttacherType = Attacher::AttachEngine3D
  Height = 20
  Placement = pos=(0,0,36.15) rot=(0,0,1;0rad)
  Radius = 8.2
FEATURE [Part::Cylinder] Cylinder051
  Angle = 360
  AttacherType = Attacher::AttachEngine3D
  Height = 10
  Placement = pos=(0,0,36.15) rot=(0,0,1;0rad)
  Radius = 4
FEATURE [Part::MultiFuse] Fusion120  label="removeToCreteHoleForPlugHousing043"
  Placement = pos=(-42,19,36) rot=(0,1,0;1.5708rad)
  Shapes = -> [Cylinder050,Cylinder051]
FEATURE [Sketcher::SketchObject] Sketch067  label="topSketch018"
  FullyConstrained = true
  sketch-geometry (4):
    g0: LineSegment StartX=16.8446 StartY=31.512 StartZ=0 EndX=16.3251 EndY=34.4666 EndZ=0
    g1: ArcOfCircle CenterX=19 CenterY=19.2524 CenterZ=0 NormalX=0 NormalY=0 NormalZ=1 AngleXU=0 Radius=15.4476 StartAngle=1.74483 EndAngle=2.72717
    g2: ArcOfCircle CenterX=19 CenterY=19.2524 CenterZ=0 NormalX=0 NormalY=0 NormalZ=1 AngleXU=0 Radius=12.4476 StartAngle=1.74483 EndAngle=2.73189
    g3: LineSegment StartX=4.86004 StartY=25.4725 StartZ=0 EndX=7.58253 EndY=24.2107 EndZ=0
  constraints (7):
    c: Block(g0)
    c: Coincident(g1,g0)
    c: Coincident(g2,g0)
    c: Coincident(g3,g1)
    c: Coincident(g3,g2)
    c: Block(g1)
    c: Block(g2)
FEATURE [Part::Extrusion] Extrude058
  Base = -> Sketch067
  Dir = (0,0,1)
  DirMode = 2
  FaceMakerClass = Part::FaceMakerBullseye
  LengthFwd = 10
  LengthRev = 0
  Placement = pos=(0,0,31) rot=(0,0,1;0rad)
  Solid = true
  Symmetric = false
FEATURE [Part::Cut] Cut051
  Base = -> Extrude058
  Tool = -> Fusion120
FEATURE [Part::Fillet] Fillet049
  Base = -> Cut051
  Edges = 1 edges r=2: [Edge1]
FEATURE [Part::Fillet] Fillet050
  Base = -> Fillet049
  Edges = 1 edges r=2.5: [Edge1]
FEATURE [Part::Fillet] Fillet051
  Base = -> Fillet050
  Edges = 1 edges r=2.5: [Edge2]
FEATURE [Part::MultiFuse] Fusion121  label="wireHolder003"
  Shapes = -> [Fusion116,Fillet051]
FEATURE [Part::MultiFuse] Fusion122
  Shapes = -> [Fillet045,Fusion121]
FEATURE [Part::MultiFuse] Fusion123  label="wireHolder004"
  Shapes = -> [Fusion122,Fillet048]
FEATURE [Part::MultiFuse] Fusion124  label="wireHolder005"
  Shapes = -> [Fillet044,Fusion119,Fusion123]
FEATURE [Sketcher::SketchObject] Sketch068  label="topSketch019"
  FullyConstrained = true
  sketch-geometry (6):
    g0: LineSegment StartX=19 StartY=38 StartZ=0 EndX=117 EndY=38 EndZ=0
    g1: ArcOfCircle CenterX=19 CenterY=19 CenterZ=0 NormalX=0 NormalY=0 NormalZ=1 AngleXU=0 Radius=19 StartAngle=1.5708 EndAngle=3.14159
    g2: LineSegment StartX=117 StartY=38 StartZ=0 EndX=117 EndY=19 EndZ=0
    g3: LineSegment StartX=98 StartY=1.0161e-12 StartZ=0 EndX=5.22862e-06 EndY=1.0161e-12 EndZ=0
    g4: LineSegment StartX=5.22862e-06 StartY=19 StartZ=0 EndX=5.22862e-06 EndY=1.0161e-12 EndZ=0
    g5: ArcOfCircle CenterX=98 CenterY=19 CenterZ=0 NormalX=0 NormalY=0 NormalZ=1 AngleXU=0 Radius=19 StartAngle=4.71239 EndAngle=6.28319
  constraints (16):
    c: Horizontal(g0)
    c: Distance(g0) = 98
    c: Coincident(g1,g0)
    c: Block(g1)
    c: Coincident(g2,g0)
    c: Vertical(g2)
    c: Distance(g2) = 19
    c: Horizontal(g3)
    c: Coincident(g4,g1)
    c: Vertical(g4)
    c: Coincident(g3,g4)
    c: Block(g3)
    c: Coincident(g5,g2)
    c: Coincident(g5,g3)
    c: Block(g0)
    c: Block(g5)
FEATURE [Part::Extrusion] Extrude059  label="sideA002"
  Base = -> Sketch068
  Dir = (0,0,1)
  DirMode = 2
  FaceMakerClass = Part::FaceMakerBullseye
  LengthFwd = 3
  LengthRev = 0
  Placement = pos=(0,0,-2.7) rot=(0,0,1;0rad)
  Solid = true
  Symmetric = false
FEATURE [Sketcher::SketchObject] Sketch069  label="topSketch020"
  FullyConstrained = true
  sketch-geometry (6):
    g0: LineSegment StartX=19 StartY=38 StartZ=0 EndX=117 EndY=38 EndZ=0
    g1: ArcOfCircle CenterX=19 CenterY=19 CenterZ=0 NormalX=0 NormalY=0 NormalZ=1 AngleXU=0 Radius=19 StartAngle=1.5708 EndAngle=3.14159
    g2: LineSegment StartX=117 StartY=38 StartZ=0 EndX=117 EndY=19 EndZ=0
    g3: LineSegment StartX=98 StartY=1.0161e-12 StartZ=0 EndX=5.22862e-06 EndY=1.0161e-12 EndZ=0
    g4: LineSegment StartX=5.22862e-06 StartY=19 StartZ=0 EndX=5.22862e-06 EndY=1.0161e-12 EndZ=0
    g5: ArcOfCircle CenterX=98 CenterY=19 CenterZ=0 NormalX=0 NormalY=0 NormalZ=1 AngleXU=0 Radius=19 StartAngle=4.71239 EndAngle=6.28319
  constraints (16):
    c: Horizontal(g0)
    c: Distance(g0) = 98
    c: Coincident(g1,g0)
    c: Block(g1)
    c: Coincident(g2,g0)
    c: Vertical(g2)
    c: Distance(g2) = 19
    c: Horizontal(g3)
    c: Coincident(g4,g1)
    c: Vertical(g4)
    c: Coincident(g3,g4)
    c: Block(g3)
    c: Coincident(g5,g2)
    c: Coincident(g5,g3)
    c: Block(g0)
    c: Block(g5)
FEATURE [Part::Extrusion] Extrude060  label="sideB002"
  Base = -> Sketch069
  Dir = (0,0,1)
  DirMode = 2
  FaceMakerClass = Part::FaceMakerBullseye
  LengthFwd = 3
  LengthRev = 0
  Placement = pos=(0,0,71.7) rot=(0,0,1;0rad)
  Solid = true
  Symmetric = false
FEATURE [Part::MultiFuse] Fusion127  label="removeFromBottom001"
  Placement = pos=(2,0,0) rot=(0,0,1;0rad)
  Shapes = -> [Extrude059,Extrude060]
FEATURE [Part::Cylinder] Cylinder052
  Angle = 360
  AttacherType = Attacher::AttachEngine3D
  Height = 20
  Placement = pos=(0,0,36.15) rot=(0,0,1;0rad)
  Radius = 14
FEATURE [Part::Cylinder] Cylinder053
  Angle = 360
  AttacherType = Attacher::AttachEngine3D
  Height = 10
  Placement = pos=(0,0,36.15) rot=(0,0,1;0rad)
  Radius = 4
FEATURE [Part::MultiFuse] Fusion128  label="removeToCreteHoleForPlugHousing044"
  Placement = pos=(70,19,36) rot=(0,1,0;1.5708rad)
  Shapes = -> [Cylinder052,Cylinder053]
FEATURE [Part::Cut] Cut052  label="bottom011"
  Base = -> Extrude043
  Tool = -> Fusion128
FEATURE [Part::Cut] Cut054  label="bottom012"
  Base = -> Cut052
  Tool = -> Fusion115
FEATURE [Sketcher::SketchObject] Sketch070
  FullyConstrained = true
  Placement = pos=(117,19,0) rot=(0.57735,0.57735,0.57735;2.0944rad)
  sketch-geometry (48):
    g0: LineSegment StartX=-49.19 StartY=69.25 StartZ=0 EndX=-49.19 EndY=66.25 EndZ=0
    g1: LineSegment StartX=-49.19 StartY=63.5 StartZ=0 EndX=-49.19 EndY=60.5 EndZ=0
    g2: LineSegment StartX=-49.19 StartY=57.75 StartZ=0 EndX=-49.19 EndY=54.75 EndZ=0
    g3: LineSegment StartX=-49.19 StartY=52 StartZ=0 EndX=-49.19 EndY=49 EndZ=0
    g4: LineSegment StartX=-49.19 StartY=46.25 StartZ=0 EndX=-49.19 EndY=43.25 EndZ=0
    g5: LineSegment StartX=-49.19 StartY=40.5 StartZ=0 EndX=-49.19 EndY=37.5 EndZ=0
    g6: LineSegment StartX=-49.19 StartY=34.5 StartZ=0 EndX=-49.19 EndY=31.5 EndZ=0
    g7: LineSegment StartX=-49.19 StartY=28.75 StartZ=0 EndX=-49.19 EndY=25.75 EndZ=0
    g8: LineSegment StartX=-49.19 StartY=23 StartZ=0 EndX=-49.19 EndY=20 EndZ=0
    g9: LineSegment StartX=-49.19 StartY=17.25 StartZ=0 EndX=-49.19 EndY=14.25 EndZ=0
    g10: LineSegment StartX=-49.19 StartY=11.5 StartZ=0 EndX=-49.19 EndY=8.5 EndZ=0
    g11: LineSegment StartX=-49.19 StartY=5.75 StartZ=0 EndX=-49.19 EndY=2.75 EndZ=0
    g12: ArcOfCircle CenterX=-1.5 CenterY=67.75 CenterZ=0 NormalX=0 NormalY=0 NormalZ=1 AngleXU=0 Radius=1.5 StartAngle=4.71239 EndAngle=7.85398
    g13: ArcOfCircle CenterX=-1.5 CenterY=62 CenterZ=0 NormalX=0 NormalY=0 NormalZ=1 AngleXU=0 Radius=1.5 StartAngle=4.71239 EndAngle=7.85398
    g14: ArcOfCircle CenterX=-1.5 CenterY=56.25 CenterZ=0 NormalX=0 NormalY=0 NormalZ=1 AngleXU=0 Radius=1.5 StartAngle=4.71239 EndAngle=7.85398
    g15: ArcOfCircle CenterX=-11.49 CenterY=50.5 CenterZ=0 NormalX=0 NormalY=0 NormalZ=1 AngleXU=0 Radius=1.5 StartAngle=4.71239 EndAngle=7.85398
    g16: ArcOfCircle CenterX=-16.28 CenterY=44.75 CenterZ=0 NormalX=0 NormalY=0 NormalZ=1 AngleXU=0 Radius=1.5 StartAngle=4.71239 EndAngle=7.85398
    g17: ArcOfCircle CenterX=-18.2337 CenterY=39 CenterZ=0 NormalX=0 NormalY=0 NormalZ=1 AngleXU=0 Radius=1.5 StartAngle=4.71485 EndAngle=7.85398
    g18: ArcOfCircle CenterX=-16.2837 CenterY=27.25 CenterZ=0 NormalX=0 NormalY=0 NormalZ=1 AngleXU=0 Radius=1.5 StartAngle=4.71485 EndAngle=7.85398
    g19: ArcOfCircle CenterX=-18.2337 CenterY=33 CenterZ=0 NormalX=0 NormalY=0 NormalZ=1 AngleXU=0 Radius=1.5 StartAngle=4.71485 EndAngle=7.85398
    g20: ArcOfCircle CenterX=-11.49 CenterY=21.5 CenterZ=0 NormalX=0 NormalY=0 NormalZ=1 AngleXU=0 Radius=1.5 StartAngle=4.71239 EndAngle=7.85398
    g21: ArcOfCircle CenterX=-1.5 CenterY=4.25 CenterZ=0 NormalX=0 NormalY=0 NormalZ=1 AngleXU=0 Radius=1.5 StartAngle=4.71239 EndAngle=7.85398
    g22: ArcOfCircle CenterX=-1.5 CenterY=10 CenterZ=0 NormalX=0 NormalY=0 NormalZ=1 AngleXU=0 Radius=1.5 StartAngle=4.71239 EndAngle=7.85398
    g23: ArcOfCircle CenterX=-1.5 CenterY=15.75 CenterZ=0 NormalX=0 NormalY=0 NormalZ=1 AngleXU=0 Radius=1.5 StartAngle=4.71239 EndAngle=7.85398
    g24: LineSegment StartX=-49.19 StartY=69.25 StartZ=0 EndX=-1.5 EndY=69.25 EndZ=0
    g25: LineSegment StartX=-49.19 StartY=66.25 StartZ=0 EndX=-1.5 EndY=66.25 EndZ=0
    g26: LineSegment StartX=-49.19 StartY=63.5 StartZ=0 EndX=-1.5 EndY=63.5 EndZ=0
    g27: LineSegment StartX=-49.19 StartY=60.5 StartZ=0 EndX=-1.5 EndY=60.5 EndZ=0
    g28: LineSegment StartX=-49.19 StartY=57.75 StartZ=0 EndX=-1.5 EndY=57.75 EndZ=0
    g29: LineSegment StartX=-49.19 StartY=54.75 StartZ=0 EndX=-1.5 EndY=54.75 EndZ=0
    g30: LineSegment StartX=-49.19 StartY=52 StartZ=0 EndX=-11.49 EndY=52 EndZ=0
    g31: LineSegment StartX=-49.19 StartY=49 StartZ=0 EndX=-11.49 EndY=49 EndZ=0
    g32: LineSegment StartX=-49.19 StartY=46.25 StartZ=0 EndX=-16.28 EndY=46.25 EndZ=0
    g33: LineSegment StartX=-49.19 StartY=43.25 StartZ=0 EndX=-16.28 EndY=43.25 EndZ=0
    g34: LineSegment StartX=-49.19 StartY=40.5 StartZ=0 EndX=-18.2337 EndY=40.5 EndZ=0
    g35: LineSegment StartX=-49.19 StartY=37.5 StartZ=0 EndX=-18.23 EndY=37.5 EndZ=0
    g36: LineSegment StartX=-49.19 StartY=34.5 StartZ=0 EndX=-18.2337 EndY=34.5 EndZ=0
    g37: LineSegment StartX=-49.19 StartY=31.5 StartZ=0 EndX=-18.23 EndY=31.5 EndZ=0
    g38: LineSegment StartX=-49.19 StartY=28.75 StartZ=0 EndX=-16.2837 EndY=28.75 EndZ=0
    g39: LineSegment StartX=-49.19 StartY=25.75 StartZ=0 EndX=-16.28 EndY=25.75 EndZ=0
    g40: LineSegment StartX=-49.19 StartY=23 StartZ=0 EndX=-11.49 EndY=23 EndZ=0
    g41: LineSegment StartX=-49.19 StartY=20 StartZ=0 EndX=-11.49 EndY=20 EndZ=0
    g42: LineSegment StartX=-49.19 StartY=17.25 StartZ=0 EndX=-1.5 EndY=17.25 EndZ=0
    g43: LineSegment StartX=-49.19 StartY=14.25 StartZ=0 EndX=-1.5 EndY=14.25 EndZ=0
    g44: LineSegment StartX=-49.19 StartY=11.5 StartZ=0 EndX=-1.5 EndY=11.5 EndZ=0
    g45: LineSegment StartX=-49.19 StartY=8.5 StartZ=0 EndX=-1.5 EndY=8.5 EndZ=0
    g46: LineSegment StartX=-49.19 StartY=5.75 StartZ=0 EndX=-1.5 EndY=5.75 EndZ=0
    g47: LineSegment StartX=-49.19 StartY=2.75 StartZ=0 EndX=-1.5 EndY=2.75 EndZ=0
  constraints (120):
    c: Vertical(g0)
    c: Distance(g0) = 3
    c: Block(g0)
    c: Vertical(g1)
    c: Distance(g1) = 3
    c: Vertical(g2)
    c: Equal(g0,g2) = 3
    c: Block(g2)
    c: Vertical(g3)
    c: Equal(g1,g3) = 3
    c: Vertical(g4)
    c: Equal(g0,g4) = 3
    c: Block(g4)
    c: Vertical(g5)
    c: Equal(g1,g5) = 3
    c: Vertical(g6)
    c: Equal(g0,g6) = 3
    c: Block(g6)
    c: Vertical(g7)
    c: Equal(g1,g7) = 3
    c: Vertical(g8)
    c: Equal(g0,g8) = 3
    c: Block(g8)
    c: Vertical(g9)
    c: Equal(g1,g9) = 3
    c: Vertical(g10)
    c: Equal(g0,g10) = 3
    c: Block(g10)
    c: Vertical(g11)
    c: Equal(g1,g11) = 3
    c: Block(g12)
    c: Block(g13)
    c: Block(g14)
    c: Block(g15)
    c: Block(g16)
    c: Block(g17)
    c: Block(g18)
    c: Block(g19)
    c: Block(g20)
    c: Block(g21)
    c: Block(g22)
    c: Block(g23)
    c: Block(g11)
    c: Block(g9)
    c: Block(g7)
    c: Block(g5)
    c: Block(g3)
    c: Block(g1)
    c: Coincident(g24,g0)
    c: Coincident(g24,g12)
    c: Horizontal(g24)
    c: Coincident(g25,g0)
    c: Coincident(g25,g12)
    c: Horizontal(g25)
    c: Coincident(g26,g1)
    c: Coincident(g26,g13)
    c: Horizontal(g26)
    c: Coincident(g27,g1)
    c: Coincident(g27,g13)
    c: Horizontal(g27)
    c: Coincident(g28,g2)
    c: Coincident(g28,g14)
    c: Horizontal(g28)
    c: Coincident(g29,g2)
    c: Coincident(g29,g14)
    c: Horizontal(g29)
    c: Coincident(g30,g3)
    c: Coincident(g30,g15)
    c: Horizontal(g30)
    c: Coincident(g31,g3)
    c: Coincident(g31,g15)
    c: Horizontal(g31)
    c: Coincident(g32,g4)
    c: Coincident(g32,g16)
    c: Horizontal(g32)
    c: Coincident(g33,g4)
    c: Coincident(g33,g16)
    c: Horizontal(g33)
    c: Coincident(g34,g5)
    c: Coincident(g34,g17)
    c: Horizontal(g34)
    c: Coincident(g35,g5)
    c: Coincident(g35,g17)
    c: Horizontal(g35)
    c: Coincident(g36,g6)
    c: Coincident(g36,g19)
    c: Horizontal(g36)
    c: Coincident(g37,g6)
    c: Coincident(g37,g19)
    c: Horizontal(g37)
    c: Coincident(g38,g7)
    c: Coincident(g38,g18)
    c: Horizontal(g38)
    c: Coincident(g39,g7)
    c: Coincident(g39,g18)
    c: Horizontal(g39)
    c: Coincident(g40,g8)
    c: Coincident(g40,g20)
    c: Horizontal(g40)
    c: Coincident(g41,g8)
    c: Coincident(g41,g20)
    c: Horizontal(g41)
    c: Coincident(g42,g9)
    c: Coincident(g42,g23)
    c: Horizontal(g42)
    c: Coincident(g43,g9)
    c: Coincident(g43,g23)
    c: Horizontal(g43)
    c: Coincident(g44,g10)
    c: Coincident(g44,g22)
    c: Horizontal(g44)
    c: Coincident(g45,g10)
    c: Coincident(g45,g22)
    c: Horizontal(g45)
    c: Coincident(g46,g11)
    c: Coincident(g46,g21)
    c: Horizontal(g46)
    c: Coincident(g47,g11)
    c: Coincident(g47,g21)
    c: Horizontal(g47)
FEATURE [Part::Extrusion] Extrude061
  Base = -> Sketch070
  Dir = (1,0,0)
  DirMode = 2
  FaceMakerClass = Part::FaceMakerBullseye
  LengthFwd = 23
  LengthRev = 0
  Placement = pos=(-19,0,0) rot=(0,0,1;0rad)
  Solid = true
  Symmetric = false
FEATURE [Part::Fillet] Fillet052  label="removeToCreateVentalationHoles002"
  Base = -> Extrude061
  Edges = <same value as first occurrence — deduplicated (x6 in doc)>
  Placement = pos=(7,0.02,0) rot=(0,0,1;0rad)
FEATURE [Part::MultiFuse] Fusion130  label="bottom013"
  Shapes = -> [Cut054,Cut034]
FEATURE [Part::Cut] Cut055
  Base = -> Fusion130
  Tool = -> Fillet052
FEATURE [Part::Cylinder] Cylinder054
  Angle = 360
  AttacherType = Attacher::AttachEngine3D
  Height = 20
  Placement = pos=(0,0,36.15) rot=(0,0,1;0rad)
  Radius = 4
FEATURE [Sketcher::SketchObject] Sketch071  label="bottomSketch002"
  FullyConstrained = true
  sketch-geometry (32):
    g0: LineSegment StartX=3.3 StartY=-6.03275e-07 StartZ=0 EndX=98 EndY=-6.03275e-07 EndZ=0
    g1: ArcOfCircle CenterX=98 CenterY=19 CenterZ=0 NormalX=0 NormalY=0 NormalZ=1 AngleXU=0 Radius=19 StartAngle=4.71239 EndAngle=5.71103
    g2: LineSegment StartX=6.3 StartY=8 StartZ=0 EndX=3.3 EndY=8 EndZ=0
    g3: LineSegment StartX=3.3 StartY=8 StartZ=0 EndX=3.3 EndY=-6.03275e-07 EndZ=0
    g4: ArcOfCircle CenterX=8.3 CenterY=5 CenterZ=0 NormalX=0 NormalY=0 NormalZ=1 AngleXU=0 Radius=2 StartAngle=3.14159 EndAngle=4.71239
    g5: LineSegment StartX=6.3 StartY=8 StartZ=0 EndX=6.3 EndY=5 EndZ=0
    g6: ArcOfCircle CenterX=98 CenterY=19 CenterZ=0 NormalX=0 NormalY=0 NormalZ=1 AngleXU=0 Radius=12.7 StartAngle=4.71239 EndAngle=6.28319
    g7: LineSegment StartX=94.7 StartY=3 StartZ=0 EndX=8.3 EndY=3 EndZ=0
    g8-g12: Circle x5 (B-spline internal-alignment scaffolding for g13; pole/knot coordinates omitted)
    g13: BSplineCurve PolesCount=5 KnotsCount=3 Degree=3 IsPeriodic=0
    g14: GeomPoint X=98 Y=6.3 Z=0
    g15: GeomPoint X=96.3938 Y=4.71946 Z=0
    g16: GeomPoint X=94.7 Y=3 Z=0
    g17-g23: Circle x7 (B-spline internal-alignment scaffolding for g24; pole/knot coordinates omitted)
    g24: BSplineCurve PolesCount=7 KnotsCount=5 Degree=3 IsPeriodic=0
    g25-g29: GeomPoint x5 (B-spline internal-alignment scaffolding for g24; pole/knot coordinates omitted)
    g30: ArcOfCircle CenterX=98 CenterY=19 CenterZ=0 NormalX=0 NormalY=0 NormalZ=1 AngleXU=0 Radius=15.7 StartAngle=5.81226 EndAngle=6.28319
    g31: LineSegment StartX=110.7 StartY=19 StartZ=0 EndX=113.7 EndY=19 EndZ=0
  constraints (41):
    c: Horizontal(g0)
    c: Coincident(g1,g0)
    c: Block(g1)
    c: Horizontal(g2)
    c: Distance(g2) = 3
    c: Coincident(g3,g2)
    c: Vertical(g3)
    c: Coincident(g3,g0)
    c: Block(g4)
    c: Block(g2)
    c: Coincident(g5,g2)
    c: Coincident(g5,g4)
    c: Vertical(g5)
    c: Coincident(g6,g1)
    c: Block(g6)
    c: Coincident(g7,g4)
    c: Horizontal(g7)
    c: Block(g0)
    c: Block(g7)
    c: Block(g3)
    c: Coincident(g13,g6)
    c: Weight(g8) = 1
    c: Equal(g8, g9-g12) x4
    c: Coincident(g13,g7)
    c: InternalAlignment(g8-g12 -> g13) x5
    c: InternalAlignment(g14,g13)
    c: InternalAlignment(g15,g13)
    c: InternalAlignment(g16,g13)
    c: Block(g13)
    c: Weight(g17) = 1
    c: Equal(g17, g18-g23) x6
    c: Coincident(g24,g1)
    c: InternalAlignment(g17-g23 -> g24) x7
    c: InternalAlignment(g25-g29 -> g24) x5
    c: Block(g24)
    c: Coincident(g30,g24)
    c: Coincident(g31,g6)
    c: Coincident(g31,g30)
    c: Horizontal(g31)
    c: Block(g31)
    c: Block(g30)
FEATURE [Part::Extrusion] Extrude062  label="bottom014"
  Base = -> Sketch071
  Dir = (0,0,1)
  DirMode = 2
  FaceMakerClass = Part::FaceMakerBullseye
  LengthFwd = 71.4
  LengthRev = 0
  Placement = pos=(0,0,0.3) rot=(0,0,1;0rad)
  Solid = true
  Symmetric = false
FEATURE [Part::Fillet] Fillet054
  Base = -> Extrude062
  Edges = 1 edges r=2.4: [Edge17]
FEATURE [Part::Fillet] Fillet055  label="bottom015"
  Base = -> Fillet054
  Edges = 1 edges r=2.4: [Edge36]
FEATURE [Part::Cylinder] Cylinder055
  Angle = 360
  AttacherType = Attacher::AttachEngine3D
  Height = 10
  Placement = pos=(0,0,36.15) rot=(0,0,1;0rad)
  Radius = 4
FEATURE [Part::MultiFuse] Fusion131  label="removeToCreateHoleForPlugHousing002"
  Placement = pos=(70,19,36.15) rot=(0,1,0;1.5708rad)
  Shapes = -> [Cylinder054,Cylinder055]
FEATURE [Part::Cut] Cut056  label="Bottom001"
  Base = -> Fillet055
  Placement = pos=(9,0,0) rot=(0,0,1;0rad)
  Tool = -> Fusion131
FEATURE [Part::Cut] Cut057
  Base = -> Cut055
  Tool = -> Cut056
FEATURE [Sketcher::SketchObject] Sketch072  label="topSketch021"
  FullyConstrained = true
  sketch-geometry (4):
    g0: ArcOfCircle CenterX=105 CenterY=19 CenterZ=0 NormalX=0 NormalY=0 NormalZ=1 AngleXU=0 Radius=20.6155 StartAngle=5.54125 EndAngle=6.28319
    g1: ArcOfCircle CenterX=105 CenterY=19 CenterZ=0 NormalX=0 NormalY=0 NormalZ=1 AngleXU=0 Radius=13 StartAngle=5.54125 EndAngle=6.28319
    g2: LineSegment StartX=118 StartY=19 StartZ=0 EndX=125.616 EndY=19 EndZ=0
    g3: LineSegment StartX=114.583 StartY=10.2157 StartZ=0 EndX=120.197 EndY=5.06982 EndZ=0
  constraints (7):
    c: Block(g0)
    c: Block(g1)
    c: Coincident(g2,g1)
    c: Coincident(g2,g0)
    c: Horizontal(g2)
    c: Coincident(g3,g1)
    c: Coincident(g3,g0)
FEATURE [Part::Extrusion] Extrude063  label="bottomPlugHousingBit003"
  Base = -> Sketch072
  Dir = (0,0,1)
  DirMode = 2
  FaceMakerClass = Part::FaceMakerBullseye
  LengthFwd = 72
  LengthRev = 0
  Solid = true
  Symmetric = false
FEATURE [Part::Cylinder] Cylinder056
  Angle = 360
  AttacherType = Attacher::AttachEngine3D
  Height = 20
  Placement = pos=(0,0,36.15) rot=(0,0,1;0rad)
  Radius = 14.3
FEATURE [Part::Cylinder] Cylinder057
  Angle = 360
  AttacherType = Attacher::AttachEngine3D
  Height = 10
  Placement = pos=(0,0,36.15) rot=(0,0,1;0rad)
  Radius = 4
FEATURE [Part::Box] Box034  label="removeToCreteHoleForPlugHousing047"
  AttacherType = Attacher::AttachEngine3D
  Height = 28.6
  Length = 20
  Placement = pos=(106.15,0,21.7) rot=(0,0,1;0rad)
  Width = 19
FEATURE [Part::Cylinder] Cylinder058
  Angle = 360
  AttacherType = Attacher::AttachEngine3D
  Height = 20
  Placement = pos=(0,0,36.15) rot=(0,0,1;0rad)
  Radius = 14.3
FEATURE [Part::Cylinder] Cylinder059
  Angle = 360
  AttacherType = Attacher::AttachEngine3D
  Height = 10
  Placement = pos=(0,0,36.15) rot=(0,0,1;0rad)
  Radius = 4
FEATURE [Part::MultiFuse] Fusion134  label="removeToCreteHoleForPlugHousing046"
  Placement = pos=(70,19,36) rot=(0,1,0;1.5708rad)
  Shapes = -> [Cylinder058,Cylinder059]
FEATURE [Part::Cylinder] Cylinder060
  Angle = 360
  AttacherType = Attacher::AttachEngine3D
  Height = 20
  Placement = pos=(0,0,36.15) rot=(0,0,1;0rad)
  Radius = 14
FEATURE [Part::Cylinder] Cylinder061
  Angle = 360
  AttacherType = Attacher::AttachEngine3D
  Height = 10
  Placement = pos=(0,0,36.15) rot=(0,0,1;0rad)
  Radius = 4
FEATURE [Part::MultiFuse] Fusion135  label="removeToCreteHoleForPlugHousing048"
  Placement = pos=(70,19,36) rot=(0,1,0;1.5708rad)
  Shapes = -> [Cylinder060,Cylinder061]
FEATURE [Part::Box] Box035  label="removeToCreteHoleForPlugHousing049"
  AttacherType = Attacher::AttachEngine3D
  Height = 28.6
  Length = 20
  Placement = pos=(106.15,0,21.7) rot=(0,0,1;0rad)
  Width = 19
FEATURE [Part::MultiFuse] Fusion133  label="removeToCreteHoleForPlugHousing045"
  Placement = pos=(0,0,-28.3) rot=(0,0,1;0rad)
  Shapes = -> [Box035,Fusion134]
FEATURE [Part::MultiFuse] Fusion138  label="removeToCreteHoleForPlugHousing051"
  Placement = pos=(70,19,36) rot=(0,1,0;1.5708rad)
  Shapes = -> [Cylinder056,Cylinder057]
FEATURE [Part::MultiFuse] Fusion137  label="removeToCreteHoleForPlugHousing050"
  Placement = pos=(0,0,28.3) rot=(0,0,1;0rad)
  Shapes = -> [Box034,Fusion138]
FEATURE [Part::MultiFuse] Fusion132  label="removeToCreatePlugHousingBottomBit002"
  Shapes = -> [Fusion133,Fusion137]
FEATURE [Part::MultiFuse] Fusion136  label="removeToCreatePlugHousingBottomBit003"
  Shapes = -> [Fusion135,Fusion132]
FEATURE [Part::Cut] Cut058  label="bottomPlugHousingBit002"
  Base = -> Extrude063
  Placement = pos=(-0.09,0,0) rot=(0,0,1;0rad)
  Tool = -> Fusion136
FEATURE [Sketcher::SketchObject] Sketch073  label="bottomSketch003"
  FullyConstrained = true
  sketch-geometry (45):
    g0: LineSegment StartX=6.29999 StartY=8 StartZ=0 EndX=3.29999 EndY=8 EndZ=0
    g1: LineSegment StartX=3.29999 StartY=8 StartZ=0 EndX=3.29999 EndY=-6.03275e-07 EndZ=0
    g2: ArcOfCircle CenterX=8.29999 CenterY=5 CenterZ=0 NormalX=0 NormalY=0 NormalZ=1 AngleXU=0 Radius=2 StartAngle=3.14159 EndAngle=4.71239
    g3: LineSegment StartX=6.29999 StartY=8 StartZ=0 EndX=6.29999 EndY=5 EndZ=0
    g4: ArcOfCircle CenterX=105 CenterY=19 CenterZ=0 NormalX=0 NormalY=0 NormalZ=1 AngleXU=0 Radius=12.7 StartAngle=4.71239 EndAngle=5.94289
    g5-g11: Circle x7 (B-spline internal-alignment scaffolding for g12; pole/knot coordinates omitted)
    g12: BSplineCurve PolesCount=7 KnotsCount=5 Degree=3 IsPeriodic=0
    g13-g17: GeomPoint x5 (B-spline internal-alignment scaffolding for g12; pole/knot coordinates omitted)
    g18: ArcOfCircle CenterX=105 CenterY=19 CenterZ=0 NormalX=0 NormalY=0 NormalZ=1 AngleXU=0 Radius=15.7 StartAngle=5.81226 EndAngle=6.28319
    g19: BSplineCurve PolesCount=5 KnotsCount=3 Degree=3 IsPeriodic=0
    g20: LineSegment StartX=8.29999 StartY=3 StartZ=0 EndX=101.7 EndY=3 EndZ=0
    g21: LineSegment StartX=3.29999 StartY=-6.03275e-07 StartZ=0 EndX=105 EndY=-6.03275e-07 EndZ=0
    g22: LineSegment StartX=120.974 StartY=8.71251 StartZ=0 EndX=122.332 EndY=7.83778 EndZ=0
    g23: LineSegment StartX=105 StartY=-6.03274e-07 StartZ=0 EndX=113 EndY=-6.03274e-07 EndZ=0
    g24: ArcOfCircle CenterX=105 CenterY=19 CenterZ=0 NormalX=0 NormalY=0 NormalZ=1 AngleXU=0 Radius=20.6155 StartAngle=5.11091 EndAngle=5.71103
    g25: ArcOfCircle CenterX=117.7 CenterY=19 CenterZ=0 NormalX=0 NormalY=0 NormalZ=1 AngleXU=0 Radius=3 StartAngle=1.2e-15 EndAngle=2.10468
    g26: Circle CenterX=116.345 CenterY=16.3232 CenterZ=0 NormalX=0 NormalY=0 NormalZ=1 AngleXU=0 Radius=1
    g27: Circle CenterX=117.24 CenterY=15.7584 CenterZ=0 NormalX=0 NormalY=0 NormalZ=1 AngleXU=0 Radius=1
    g28: Circle CenterX=116.972 CenterY=14.7612 CenterZ=0 NormalX=0 NormalY=0 NormalZ=1 AngleXU=0 Radius=1
    g29: BSplineCurve PolesCount=3 KnotsCount=2 Degree=2 IsPeriodic=0
    g30: GeomPoint X=116.345 Y=16.3232 Z=0
    g31: GeomPoint X=116.972 Y=14.7612 Z=0
    g32: Circle CenterX=115.828 CenterY=17.157 CenterZ=0 NormalX=0 NormalY=0 NormalZ=1 AngleXU=0 Radius=1
    g33: Circle CenterX=115.841 CenterY=16.639 CenterZ=0 NormalX=0 NormalY=0 NormalZ=1 AngleXU=0 Radius=1
    g34: Circle CenterX=116.345 CenterY=16.3232 CenterZ=0 NormalX=0 NormalY=0 NormalZ=1 AngleXU=0 Radius=1
    g35: BSplineCurve PolesCount=3 KnotsCount=2 Degree=2 IsPeriodic=0
    g36: GeomPoint X=115.828 Y=17.157 Z=0
    g37: GeomPoint X=116.345 Y=16.3232 Z=0
    g38: LineSegment StartX=115.828 StartY=17.157 StartZ=0 EndX=115.828 EndY=20.8307 EndZ=0
    g39: Circle CenterX=115.828 CenterY=20.8307 CenterZ=0 NormalX=0 NormalY=0 NormalZ=1 AngleXU=0 Radius=1
    g40: Circle CenterX=115.831 CenterY=21.3396 CenterZ=0 NormalX=0 NormalY=0 NormalZ=1 AngleXU=0 Radius=1
    g41: Circle CenterX=116.173 CenterY=21.5825 CenterZ=0 NormalX=0 NormalY=0 NormalZ=1 AngleXU=0 Radius=1
    g42: BSplineCurve PolesCount=3 KnotsCount=2 Degree=2 IsPeriodic=0
    g43: GeomPoint X=115.828 Y=20.8307 Z=0
    g44: GeomPoint X=116.173 Y=21.5825 Z=0
  constraints (70):
    c: Horizontal(g0)
    c: Distance(g0) = 3
    c: Coincident(g1,g0)
    c: Vertical(g1)
    c: Block(g2)
    c: Block(g0)
    c: Coincident(g3,g0)
    c: Coincident(g3,g2)
    c: Vertical(g3)
    c: Block(g1)
    c: Block(g4)
    c: Coincident(g19,g4)
    c: Block(g19)
    c: Equal(g5, g6-g11) x6
    c: InternalAlignment(g5-g11 -> g12) x7
    c: InternalAlignment(g13-g17 -> g12) x5
    c: Block(g12)
    c: Coincident(g18,g12)
    c: Block(g18)
    c: Coincident(g20,g2)
    c: Coincident(g20,g19)
    c: Horizontal(g20)
    c: Distance(g20) = 93.4
    c: Coincident(g21,g1)
    c: Horizontal(g21)
    c: Distance(g21) = 101.7
    c: Horizontal(g23)
    c: Distance(g23) = 8
    c: Coincident(g24,g23)
    c: Block(g23)
    c: Coincident(g22,g24)
    c: Block(g24)
    c: Block(g22)
    c: Distance(g22) = 1.61553
    c: Coincident(g25,g18)
    c: Block(g25)
    c: Weight(g26) = 1
    c: Equal(g26,g27)
    c: Equal(g26,g28)
    c: Coincident(g29,g4)
    c: InternalAlignment(g26,g29)
    c: InternalAlignment(g27,g29)
    c: InternalAlignment(g28,g29)
    c: InternalAlignment(g30,g29)
    c: InternalAlignment(g31,g29)
    c: Block(g29)
    c: Weight(g32) = 1
    c: Equal(g32,g33)
    c: Equal(g32,g34)
    c: Coincident(g35,g29)
    c: InternalAlignment(g32,g35)
    c: InternalAlignment(g33,g35)
    c: InternalAlignment(g34,g35)
    c: InternalAlignment(g36,g35)
    c: InternalAlignment(g37,g35)
    c: Block(g35)
    c: Coincident(g38,g35)
    c: Vertical(g38)
    c: Block(g38)
    c: Coincident(g42,g38)
    c: Weight(g39) = 1
    c: Equal(g39,g40)
    c: Equal(g39,g41)
    c: Coincident(g42,g25)
    c: InternalAlignment(g39,g42)
    c: InternalAlignment(g40,g42)
    c: InternalAlignment(g41,g42)
    c: InternalAlignment(g43,g42)
    c: InternalAlignment(g44,g42)
    c: Block(g42)
FEATURE [Part::Extrusion] Extrude064  label="bottom016"
  Base = -> Sketch073
  Dir = (0,0,1)
  DirMode = 2
  FaceMakerClass = Part::FaceMakerBullseye
  LengthFwd = 71.4
  LengthRev = 0
  Placement = pos=(0,0,0.3) rot=(0,0,1;0rad)
  Solid = true
  Symmetric = false
FEATURE [Part::Revolution] Revolve157  label="removeToCreateScrewAndThreadedInsertHole063"
  Angle = 360
  Axis = (0,1,0)
  Base = (0,0,0)
  FaceMakerClass = Part::FaceMakerBullseye
  Placement = pos=(12.5,0,10) rot=(0,0,1;0rad)
  Solid = false
  Source = -> Face141
  Symmetric = false
FEATURE [Sketcher::SketchObject] Sketch074
  FullyConstrained = true
  Placement = pos=(117,19,0) rot=(0.57735,0.57735,0.57735;2.0944rad)
  sketch-geometry (48):
    g0: LineSegment StartX=-49.19 StartY=69.25 StartZ=0 EndX=-49.19 EndY=66.25 EndZ=0
    g1: LineSegment StartX=-49.19 StartY=63.5 StartZ=0 EndX=-49.19 EndY=60.5 EndZ=0
    g2: LineSegment StartX=-49.19 StartY=57.75 StartZ=0 EndX=-49.19 EndY=54.75 EndZ=0
    g3: LineSegment StartX=-49.19 StartY=52 StartZ=0 EndX=-49.19 EndY=49 EndZ=0
    g4: LineSegment StartX=-49.19 StartY=46.25 StartZ=0 EndX=-49.19 EndY=43.25 EndZ=0
    g5: LineSegment StartX=-49.19 StartY=40.5 StartZ=0 EndX=-49.19 EndY=37.5 EndZ=0
    g6: LineSegment StartX=-49.19 StartY=34.5 StartZ=0 EndX=-49.19 EndY=31.5 EndZ=0
    g7: LineSegment StartX=-49.19 StartY=28.75 StartZ=0 EndX=-49.19 EndY=25.75 EndZ=0
    g8: LineSegment StartX=-49.19 StartY=23 StartZ=0 EndX=-49.19 EndY=20 EndZ=0
    g9: LineSegment StartX=-49.19 StartY=17.25 StartZ=0 EndX=-49.19 EndY=14.25 EndZ=0
    g10: LineSegment StartX=-49.19 StartY=11.5 StartZ=0 EndX=-49.19 EndY=8.5 EndZ=0
    g11: LineSegment StartX=-49.19 StartY=5.75 StartZ=0 EndX=-49.19 EndY=2.75 EndZ=0
    g12: ArcOfCircle CenterX=-1.5 CenterY=67.75 CenterZ=0 NormalX=0 NormalY=0 NormalZ=1 AngleXU=0 Radius=1.5 StartAngle=4.71239 EndAngle=7.85398
    g13: ArcOfCircle CenterX=-1.5 CenterY=62 CenterZ=0 NormalX=0 NormalY=0 NormalZ=1 AngleXU=0 Radius=1.5 StartAngle=4.71239 EndAngle=7.85398
    g14: ArcOfCircle CenterX=-1.5 CenterY=56.25 CenterZ=0 NormalX=0 NormalY=0 NormalZ=1 AngleXU=0 Radius=1.5 StartAngle=4.71239 EndAngle=7.85398
    g15: ArcOfCircle CenterX=-11.49 CenterY=50.5 CenterZ=0 NormalX=0 NormalY=0 NormalZ=1 AngleXU=0 Radius=1.5 StartAngle=4.71239 EndAngle=7.85398
    g16: ArcOfCircle CenterX=-16.28 CenterY=44.75 CenterZ=0 NormalX=0 NormalY=0 NormalZ=1 AngleXU=0 Radius=1.5 StartAngle=4.71239 EndAngle=7.85398
    g17: ArcOfCircle CenterX=-18.2337 CenterY=39 CenterZ=0 NormalX=0 NormalY=0 NormalZ=1 AngleXU=0 Radius=1.5 StartAngle=4.71485 EndAngle=7.85398
    g18: ArcOfCircle CenterX=-16.2837 CenterY=27.25 CenterZ=0 NormalX=0 NormalY=0 NormalZ=1 AngleXU=0 Radius=1.5 StartAngle=4.71485 EndAngle=7.85398
    g19: ArcOfCircle CenterX=-18.2337 CenterY=33 CenterZ=0 NormalX=0 NormalY=0 NormalZ=1 AngleXU=0 Radius=1.5 StartAngle=4.71485 EndAngle=7.85398
    g20: ArcOfCircle CenterX=-11.49 CenterY=21.5 CenterZ=0 NormalX=0 NormalY=0 NormalZ=1 AngleXU=0 Radius=1.5 StartAngle=4.71239 EndAngle=7.85398
    g21: ArcOfCircle CenterX=-1.5 CenterY=4.25 CenterZ=0 NormalX=0 NormalY=0 NormalZ=1 AngleXU=0 Radius=1.5 StartAngle=4.71239 EndAngle=7.85398
    g22: ArcOfCircle CenterX=-1.5 CenterY=10 CenterZ=0 NormalX=0 NormalY=0 NormalZ=1 AngleXU=0 Radius=1.5 StartAngle=4.71239 EndAngle=7.85398
    g23: ArcOfCircle CenterX=-1.5 CenterY=15.75 CenterZ=0 NormalX=0 NormalY=0 NormalZ=1 AngleXU=0 Radius=1.5 StartAngle=4.71239 EndAngle=7.85398
    g24: LineSegment StartX=-49.19 StartY=69.25 StartZ=0 EndX=-1.5 EndY=69.25 EndZ=0
    g25: LineSegment StartX=-49.19 StartY=66.25 StartZ=0 EndX=-1.5 EndY=66.25 EndZ=0
    g26: LineSegment StartX=-49.19 StartY=63.5 StartZ=0 EndX=-1.5 EndY=63.5 EndZ=0
    g27: LineSegment StartX=-49.19 StartY=60.5 StartZ=0 EndX=-1.5 EndY=60.5 EndZ=0
    g28: LineSegment StartX=-49.19 StartY=57.75 StartZ=0 EndX=-1.5 EndY=57.75 EndZ=0
    g29: LineSegment StartX=-49.19 StartY=54.75 StartZ=0 EndX=-1.5 EndY=54.75 EndZ=0
    g30: LineSegment StartX=-49.19 StartY=52 StartZ=0 EndX=-11.49 EndY=52 EndZ=0
    g31: LineSegment StartX=-49.19 StartY=49 StartZ=0 EndX=-11.49 EndY=49 EndZ=0
    g32: LineSegment StartX=-49.19 StartY=46.25 StartZ=0 EndX=-16.28 EndY=46.25 EndZ=0
    g33: LineSegment StartX=-49.19 StartY=43.25 StartZ=0 EndX=-16.28 EndY=43.25 EndZ=0
    g34: LineSegment StartX=-49.19 StartY=40.5 StartZ=0 EndX=-18.2337 EndY=40.5 EndZ=0
    g35: LineSegment StartX=-49.19 StartY=37.5 StartZ=0 EndX=-18.23 EndY=37.5 EndZ=0
    g36: LineSegment StartX=-49.19 StartY=34.5 StartZ=0 EndX=-18.2337 EndY=34.5 EndZ=0
    g37: LineSegment StartX=-49.19 StartY=31.5 StartZ=0 EndX=-18.23 EndY=31.5 EndZ=0
    g38: LineSegment StartX=-49.19 StartY=28.75 StartZ=0 EndX=-16.2837 EndY=28.75 EndZ=0
    g39: LineSegment StartX=-49.19 StartY=25.75 StartZ=0 EndX=-16.28 EndY=25.75 EndZ=0
    g40: LineSegment StartX=-49.19 StartY=23 StartZ=0 EndX=-11.49 EndY=23 EndZ=0
    g41: LineSegment StartX=-49.19 StartY=20 StartZ=0 EndX=-11.49 EndY=20 EndZ=0
    g42: LineSegment StartX=-49.19 StartY=17.25 StartZ=0 EndX=-1.5 EndY=17.25 EndZ=0
    g43: LineSegment StartX=-49.19 StartY=14.25 StartZ=0 EndX=-1.5 EndY=14.25 EndZ=0
    g44: LineSegment StartX=-49.19 StartY=11.5 StartZ=0 EndX=-1.5 EndY=11.5 EndZ=0
    g45: LineSegment StartX=-49.19 StartY=8.5 StartZ=0 EndX=-1.5 EndY=8.5 EndZ=0
    g46: LineSegment StartX=-49.19 StartY=5.75 StartZ=0 EndX=-1.5 EndY=5.75 EndZ=0
    g47: LineSegment StartX=-49.19 StartY=2.75 StartZ=0 EndX=-1.5 EndY=2.75 EndZ=0
  constraints (120):
    c: Vertical(g0)
    c: Distance(g0) = 3
    c: Block(g0)
    c: Vertical(g1)
    c: Distance(g1) = 3
    c: Vertical(g2)
    c: Equal(g0,g2) = 3
    c: Block(g2)
    c: Vertical(g3)
    c: Equal(g1,g3) = 3
    c: Vertical(g4)
    c: Equal(g0,g4) = 3
    c: Block(g4)
    c: Vertical(g5)
    c: Equal(g1,g5) = 3
    c: Vertical(g6)
    c: Equal(g0,g6) = 3
    c: Block(g6)
    c: Vertical(g7)
    c: Equal(g1,g7) = 3
    c: Vertical(g8)
    c: Equal(g0,g8) = 3
    c: Block(g8)
    c: Vertical(g9)
    c: Equal(g1,g9) = 3
    c: Vertical(g10)
    c: Equal(g0,g10) = 3
    c: Block(g10)
    c: Vertical(g11)
    c: Equal(g1,g11) = 3
    c: Block(g12)
    c: Block(g13)
    c: Block(g14)
    c: Block(g15)
    c: Block(g16)
    c: Block(g17)
    c: Block(g18)
    c: Block(g19)
    c: Block(g20)
    c: Block(g21)
    c: Block(g22)
    c: Block(g23)
    c: Block(g11)
    c: Block(g9)
    c: Block(g7)
    c: Block(g5)
    c: Block(g3)
    c: Block(g1)
    c: Coincident(g24,g0)
    c: Coincident(g24,g12)
    c: Horizontal(g24)
    c: Coincident(g25,g0)
    c: Coincident(g25,g12)
    c: Horizontal(g25)
    c: Coincident(g26,g1)
    c: Coincident(g26,g13)
    c: Horizontal(g26)
    c: Coincident(g27,g1)
    c: Coincident(g27,g13)
    c: Horizontal(g27)
    c: Coincident(g28,g2)
    c: Coincident(g28,g14)
    c: Horizontal(g28)
    c: Coincident(g29,g2)
    c: Coincident(g29,g14)
    c: Horizontal(g29)
    c: Coincident(g30,g3)
    c: Coincident(g30,g15)
    c: Horizontal(g30)
    c: Coincident(g31,g3)
    c: Coincident(g31,g15)
    c: Horizontal(g31)
    c: Coincident(g32,g4)
    c: Coincident(g32,g16)
    c: Horizontal(g32)
    c: Coincident(g33,g4)
    c: Coincident(g33,g16)
    c: Horizontal(g33)
    c: Coincident(g34,g5)
    c: Coincident(g34,g17)
    c: Horizontal(g34)
    c: Coincident(g35,g5)
    c: Coincident(g35,g17)
    c: Horizontal(g35)
    c: Coincident(g36,g6)
    c: Coincident(g36,g19)
    c: Horizontal(g36)
    c: Coincident(g37,g6)
    c: Coincident(g37,g19)
    c: Horizontal(g37)
    c: Coincident(g38,g7)
    c: Coincident(g38,g18)
    c: Horizontal(g38)
    c: Coincident(g39,g7)
    c: Coincident(g39,g18)
    c: Horizontal(g39)
    c: Coincident(g40,g8)
    c: Coincident(g40,g20)
    c: Horizontal(g40)
    c: Coincident(g41,g8)
    c: Coincident(g41,g20)
    c: Horizontal(g41)
    c: Coincident(g42,g9)
    c: Coincident(g42,g23)
    c: Horizontal(g42)
    c: Coincident(g43,g9)
    c: Coincident(g43,g23)
    c: Horizontal(g43)
    c: Coincident(g44,g10)
    c: Coincident(g44,g22)
    c: Horizontal(g44)
    c: Coincident(g45,g10)
    c: Coincident(g45,g22)
    c: Horizontal(g45)
    c: Coincident(g46,g11)
    c: Coincident(g46,g21)
    c: Horizontal(g46)
    c: Coincident(g47,g11)
    c: Coincident(g47,g21)
    c: Horizontal(g47)
FEATURE [Part::Extrusion] Extrude065
  Base = -> Sketch074
  Dir = (1,0,0)
  DirMode = 2
  FaceMakerClass = Part::FaceMakerBullseye
  LengthFwd = 23
  LengthRev = 0
  Placement = pos=(-19,0,0) rot=(0,0,1;0rad)
  Solid = true
  Symmetric = false
FEATURE [Part::Fillet] Fillet056  label="removeToCreateVentalationHoles003"
  Base = -> Extrude065
  Edges = <same value as first occurrence — deduplicated (x6 in doc)>
  Placement = pos=(7,0.02,0) rot=(0,0,1;0rad)
FEATURE [Part::Revolution] Revolve158  label="removeToCreateScrewAndThreadedInsertHole065"
  Angle = 360
  Axis = (0,1,0)
  Base = (0,0,0)
  FaceMakerClass = Part::FaceMakerBullseye
  Placement = pos=(12.5,0,62) rot=(0,0,1;0rad)
  Solid = false
  Source = -> Face146
  Symmetric = false
FEATURE [Part::Revolution] Revolve159  label="removeToCreateScrewAndThreadedInsertHole066"
  Angle = 360
  Axis = (0,1,0)
  Base = (0,0,0)
  FaceMakerClass = Part::FaceMakerBullseye
  Placement = pos=(89.5,0,68.5) rot=(0,0,1;0rad)
  Solid = false
  Source = -> Face143
  Symmetric = false
FEATURE [Part::Revolution] Revolve160  label="removeToCreateScrewAndThreadedInsertHole067"
  Angle = 360
  Axis = (0,1,0)
  Base = (0,0,0)
  FaceMakerClass = Part::FaceMakerBullseye
  Placement = pos=(89.5,0,3.5) rot=(0,0,1;0rad)
  Solid = false
  Source = -> Face142
  Symmetric = false
FEATURE [Part::Revolution] Revolve161  label="removeToCreateScrewAndThreadedInsertHole068"
  Angle = 360
  Axis = (0,1,0)
  Base = (0,0,0)
  FaceMakerClass = Part::FaceMakerBullseye
  Placement = pos=(109.5,4.7,3.5) rot=(0,0,1;0rad)
  Solid = false
  Source = -> Face145
  Symmetric = false
FEATURE [Part::Revolution] Revolve162  label="removeToCreateScrewAndThreadedInsertHole069"
  Angle = 360
  Axis = (0,1,0)
  Base = (0,0,0)
  FaceMakerClass = Part::FaceMakerBullseye
  Placement = pos=(109.5,4.7,68.5) rot=(0,0,1;0rad)
  Solid = false
  Source = -> Face144
  Symmetric = false
FEATURE [Part::MultiFuse] Fusion141  label="removeToCreateScrewAndThreadedInsertHole064"
  Shapes = -> [Revolve162,Revolve161,Revolve160,Revolve159,Revolve158,Revolve157]
FEATURE [Part::Cylinder] Cylinder062
  Angle = 360
  AttacherType = Attacher::AttachEngine3D
  Height = 20
  Placement = pos=(0,0,36.15) rot=(0,0,1;0rad)
  Radius = 14
FEATURE [Part::Cylinder] Cylinder063
  Angle = 360
  AttacherType = Attacher::AttachEngine3D
  Height = 10
  Placement = pos=(0,0,36.15) rot=(0,0,1;0rad)
  Radius = 4
FEATURE [Part::MultiFuse] Fusion139  label="removeToCreteHoleForPlugHousing052"
  Placement = pos=(70,19,36) rot=(0,1,0;1.5708rad)
  Shapes = -> [Cylinder062,Cylinder063]
FEATURE [Part::Cut] Cut060  label="bottom017"
  Base = -> Extrude064
  Tool = -> Fusion139
FEATURE [Part::Cut] Cut061  label="bottom019"
  Base = -> Cut060
  Tool = -> Fusion141
FEATURE [Part::MultiFuse] Fusion140  label="bottom018"
  Shapes = -> [Cut061,Cut058]
FEATURE [Part::Cut] Cut059  label="bottom020"
  Base = -> Fusion140
  Tool = -> Fillet056
FEATURE [Part::Box] Box036  label="Cube021"
  AttacherType = Attacher::AttachEngine3D
  Height = 80
  Length = 26
  Placement = pos=(0,-1,-5) rot=(0,0,1;0rad)
  Width = 11
FEATURE [Part::Cut] Cut062  label="removeFromBottom002"
  Base = -> Cut057
  Tool = -> Box036
FEATURE [Part::Cut] Cut063
  Base = -> Cut059
  Tool = -> Cut062
FEATURE [Part::Cut] Cut064  label="pcbStands"
  Base = -> Fusion095
  Tool = -> Fusion127
FEATURE [Sketcher::SketchObject] Sketch075  label="topSketch022"
  FullyConstrained = true
  sketch-geometry (6):
    g0: LineSegment StartX=19 StartY=38 StartZ=0 EndX=117 EndY=38 EndZ=0
    g1: ArcOfCircle CenterX=19 CenterY=19 CenterZ=0 NormalX=0 NormalY=0 NormalZ=1 AngleXU=0 Radius=19 StartAngle=1.5708 EndAngle=3.14159
    g2: LineSegment StartX=117 StartY=38 StartZ=0 EndX=117 EndY=19 EndZ=0
    g3: LineSegment StartX=98 StartY=1.0161e-12 StartZ=0 EndX=5.22862e-06 EndY=1.0161e-12 EndZ=0
    g4: LineSegment StartX=5.22862e-06 StartY=19 StartZ=0 EndX=5.22862e-06 EndY=1.0161e-12 EndZ=0
    g5: ArcOfCircle CenterX=98 CenterY=19 CenterZ=0 NormalX=0 NormalY=0 NormalZ=1 AngleXU=0 Radius=19 StartAngle=4.71239 EndAngle=6.28319
  constraints (16):
    c: Horizontal(g0)
    c: Distance(g0) = 98
    c: Coincident(g1,g0)
    c: Block(g1)
    c: Coincident(g2,g0)
    c: Vertical(g2)
    c: Distance(g2) = 19
    c: Horizontal(g3)
    c: Coincident(g4,g1)
    c: Vertical(g4)
    c: Coincident(g3,g4)
    c: Block(g3)
    c: Coincident(g5,g2)
    c: Coincident(g5,g3)
    c: Block(g0)
    c: Block(g5)
FEATURE [Part::Extrusion] Extrude067  label="sideB003"
  Base = -> Sketch075
  Dir = (0,0,1)
  DirMode = 2
  FaceMakerClass = Part::FaceMakerBullseye
  LengthFwd = 3
  LengthRev = 0
  Placement = pos=(0,0,71.7) rot=(0,0,1;0rad)
  Solid = true
  Symmetric = false
FEATURE [Sketcher::SketchObject] Sketch076  label="topSketch023"
  FullyConstrained = true
  sketch-geometry (6):
    g0: LineSegment StartX=19 StartY=38 StartZ=0 EndX=117 EndY=38 EndZ=0
    g1: ArcOfCircle CenterX=19 CenterY=19 CenterZ=0 NormalX=0 NormalY=0 NormalZ=1 AngleXU=0 Radius=19 StartAngle=1.5708 EndAngle=3.14159
    g2: LineSegment StartX=117 StartY=38 StartZ=0 EndX=117 EndY=19 EndZ=0
    g3: LineSegment StartX=98 StartY=1.0161e-12 StartZ=0 EndX=5.22862e-06 EndY=1.0161e-12 EndZ=0
    g4: LineSegment StartX=5.22862e-06 StartY=19 StartZ=0 EndX=5.22862e-06 EndY=1.0161e-12 EndZ=0
    g5: ArcOfCircle CenterX=98 CenterY=19 CenterZ=0 NormalX=0 NormalY=0 NormalZ=1 AngleXU=0 Radius=19 StartAngle=4.71239 EndAngle=6.28319
  constraints (16):
    c: Horizontal(g0)
    c: Distance(g0) = 98
    c: Coincident(g1,g0)
    c: Block(g1)
    c: Coincident(g2,g0)
    c: Vertical(g2)
    c: Distance(g2) = 19
    c: Horizontal(g3)
    c: Coincident(g4,g1)
    c: Vertical(g4)
    c: Coincident(g3,g4)
    c: Block(g3)
    c: Coincident(g5,g2)
    c: Coincident(g5,g3)
    c: Block(g0)
    c: Block(g5)
FEATURE [Part::Extrusion] Extrude066  label="sideA003"
  Base = -> Sketch076
  Dir = (0,0,1)
  DirMode = 2
  FaceMakerClass = Part::FaceMakerBullseye
  LengthFwd = 3
  LengthRev = 0
  Placement = pos=(0,0,-2.7) rot=(0,0,1;0rad)
  Solid = true
  Symmetric = false
FEATURE [Part::MultiFuse] Fusion142  label="removeFromBottom003"
  Placement = pos=(2,0,0) rot=(0,0,1;0rad)
  Shapes = -> [Extrude066,Extrude067]
FEATURE [Part::Cut] Cut065  label="screwRetainers002"
  Base = -> Fusion096
  Tool = -> Fusion142
FEATURE [Sketcher::SketchObject] Sketch077
  FullyConstrained = true
  Placement = pos=(117,19,0) rot=(0.57735,0.57735,0.57735;2.0944rad)
  sketch-geometry (8):
    g0: LineSegment StartX=-49.19 StartY=63.5 StartZ=0 EndX=-49.19 EndY=60.5 EndZ=0
    g1: LineSegment StartX=-49.19 StartY=11.5 StartZ=0 EndX=-49.19 EndY=8.5 EndZ=0
    g2: ArcOfCircle CenterX=-1.5 CenterY=62 CenterZ=0 NormalX=0 NormalY=0 NormalZ=1 AngleXU=0 Radius=1.5 StartAngle=4.71239 EndAngle=7.85398
    g3: ArcOfCircle CenterX=-1.5 CenterY=10 CenterZ=0 NormalX=0 NormalY=0 NormalZ=1 AngleXU=0 Radius=1.5 StartAngle=4.71239 EndAngle=7.85398
    g4: LineSegment StartX=-49.19 StartY=63.5 StartZ=0 EndX=-1.5 EndY=63.5 EndZ=0
    g5: LineSegment StartX=-49.19 StartY=60.5 StartZ=0 EndX=-1.5 EndY=60.5 EndZ=0
    g6: LineSegment StartX=-49.19 StartY=11.5 StartZ=0 EndX=-1.5 EndY=11.5 EndZ=0
    g7: LineSegment StartX=-49.19 StartY=8.5 StartZ=0 EndX=-1.5 EndY=8.5 EndZ=0
  constraints (19):
    c: Vertical(g0)
    c: Distance(g0) = 3
    c: Vertical(g1)
    c: Block(g1)
    c: Block(g2)
    c: Block(g3)
    c: Block(g0)
    c: Coincident(g4,g0)
    c: Coincident(g4,g2)
    c: Horizontal(g4)
    c: Coincident(g5,g0)
    c: Coincident(g5,g2)
    c: Horizontal(g5)
    c: Coincident(g6,g1)
    c: Coincident(g6,g3)
    c: Horizontal(g6)
    c: Coincident(g7,g1)
    c: Coincident(g7,g3)
    c: Horizontal(g7)
FEATURE [Part::Extrusion] Extrude068
  Base = -> Sketch077
  Dir = (1,0,0)
  DirMode = 2
  FaceMakerClass = Part::FaceMakerBullseye
  LengthFwd = 10
  LengthRev = 0
  Solid = true
  Symmetric = false
FEATURE [Part::Fillet] Fillet057  label="removeFromtMoreFrontCaseScrewRetainers002"
  Base = -> Extrude068
  Edges = 4 edges r=1.49: [Edge6,Edge11,Edge18,Edge23]
  Placement = pos=(-12,0,0) rot=(0,0,1;0rad)
FEATURE [Sketcher::SketchObject] Sketch078
  FullyConstrained = true
  Placement = pos=(117,19,0) rot=(0.57735,0.57735,0.57735;2.0944rad)
  sketch-geometry (8):
    g0: LineSegment StartX=-49.19 StartY=69.25 StartZ=0 EndX=-49.19 EndY=66.25 EndZ=0
    g1: LineSegment StartX=-49.19 StartY=5.75 StartZ=0 EndX=-49.19 EndY=2.75 EndZ=0
    g2: ArcOfCircle CenterX=-1.5 CenterY=67.75 CenterZ=0 NormalX=0 NormalY=0 NormalZ=1 AngleXU=0 Radius=1.5 StartAngle=4.71239 EndAngle=7.85398
    g3: ArcOfCircle CenterX=-1.5 CenterY=4.25 CenterZ=0 NormalX=0 NormalY=0 NormalZ=1 AngleXU=0 Radius=1.5 StartAngle=4.71239 EndAngle=7.85398
    g4: LineSegment StartX=-49.19 StartY=69.25 StartZ=0 EndX=-1.5 EndY=69.25 EndZ=0
    g5: LineSegment StartX=-49.19 StartY=66.25 StartZ=0 EndX=-1.5 EndY=66.25 EndZ=0
    g6: LineSegment StartX=-49.19 StartY=5.75 StartZ=0 EndX=-1.5 EndY=5.75 EndZ=0
    g7: LineSegment StartX=-49.19 StartY=2.75 StartZ=0 EndX=-1.5 EndY=2.75 EndZ=0
  constraints (19):
    c: Vertical(g0)
    c: Distance(g0) = 3
    c: Block(g0)
    c: Vertical(g1)
    c: Block(g2)
    c: Block(g3)
    c: Block(g1)
    c: Coincident(g4,g0)
    c: Coincident(g4,g2)
    c: Horizontal(g4)
    c: Coincident(g5,g0)
    c: Coincident(g5,g2)
    c: Horizontal(g5)
    c: Coincident(g6,g1)
    c: Coincident(g6,g3)
    c: Horizontal(g6)
    c: Coincident(g7,g1)
    c: Coincident(g7,g3)
    c: Horizontal(g7)
FEATURE [Part::Extrusion] Extrude069
  Base = -> Sketch078
  Dir = (1,0,0)
  DirMode = 2
  FaceMakerClass = Part::FaceMakerBullseye
  LengthFwd = 10
  LengthRev = 0
  Solid = true
  Symmetric = false
FEATURE [Part::Fillet] Fillet058  label="removeFromtMoreFrontCaseScrewRetainers003"
  Base = -> Extrude069
  Edges = 4 edges r=1.49: [Edge6,Edge11,Edge18,Edge23]
  Placement = pos=(-4,0,0) rot=(0,0,1;0rad)
FEATURE [Part::Cut] Cut066
  Base = -> Cut065
  Tool = -> Fillet058
FEATURE [Part::Cut] Cut067  label="screwPillars"
  Base = -> Cut066
  Tool = -> Fillet057
FEATURE [Part::MultiFuse] Fusion143  label="bottom021"
  Shapes = -> [Cut031,Cut063]
FEATURE [Part::Cylinder] Cylinder
  Angle = 360
  AttacherType = Attacher::AttachEngine3D
  Height = 10
  Placement = pos=(20.65,12,4.68) rot=(1,0,0;1.5708rad)
  Radius = 2
FEATURE [Part::Cylinder] Cylinder064
  Angle = 360
  AttacherType = Attacher::AttachEngine3D
  Height = 10
  Placement = pos=(20.65,12,67.38) rot=(1,0,0;1.5708rad)
  Radius = 2
FEATURE [Part::Cylinder] Cylinder065
  Angle = 360
  AttacherType = Attacher::AttachEngine3D
  Height = 10
  Placement = pos=(77.15,12,67.38) rot=(1,0,0;1.5708rad)
  Radius = 2
FEATURE [Part::Cylinder] Cylinder066
  Angle = 360
  AttacherType = Attacher::AttachEngine3D
  Height = 10
  Placement = pos=(77.15,12,4.68) rot=(1,0,0;1.5708rad)
  Radius = 2
FEATURE [Part::MultiFuse] Fusion144  label="removeFromThreadedInsertHousing"
  Shapes = -> [Cylinder065,Cylinder064,Cylinder,Cylinder066]
FEATURE [Part::Cut] Cut068  label="pcbStands001"
  Base = -> Cut064
  Tool = -> Fusion144
FEATURE [Part::MultiFuse] Fusion145
  Shapes = -> [Cut068,Fusion143]
FEATURE [Part::MultiFuse] Fusion146
  Shapes = -> [Fusion145]
FEATURE [Part::MultiFuse] Fusion147  label="bottom022"
  Shapes = -> [Cut067,Fusion146]
FEATURE [Part::MultiFuse] Fusion148  label="casePillars005"
  Shapes = -> [Cut047,Fusion092]
FEATURE [Part::MultiFuse] Fusion149  label="bottom023"
  Shapes = -> [Fusion124,Fusion113,Fusion147]
FEATURE [Part::MultiFuse] Fusion150  label="topBits"
  Shapes = -> [Cut025,Fusion148,Cut030,Fillet034]
FEATURE [Part::Feature] Face149 .. Face152  x4 (patterned run collapsed; names and placements below)
  shape: bbox 3.2 x 1.5 x 2e-07 mm, 1 faces, 0 solids (baked)
FEATURE [Part::Feature] Face153
  shape: bbox 3.6 x 3.2 x 2e-07 mm, 1 faces, 0 solids (baked)
FEATURE [Part::Feature] Face154
  shape: bbox 3.6 x 3.2 x 2e-07 mm, 1 faces, 0 solids (baked)
FEATURE [Sketcher::SketchObject] Sketch079  label="topSketch024"
  FullyConstrained = true
  sketch-geometry (6):
    g0: LineSegment StartX=19 StartY=38 StartZ=0 EndX=117 EndY=38 EndZ=0
    g1: ArcOfCircle CenterX=19 CenterY=19 CenterZ=0 NormalX=0 NormalY=0 NormalZ=1 AngleXU=0 Radius=19 StartAngle=1.5708 EndAngle=3.14159
    g2: LineSegment StartX=117 StartY=38 StartZ=0 EndX=117 EndY=19 EndZ=0
    g3: LineSegment StartX=98 StartY=1.0161e-12 StartZ=0 EndX=5.22862e-06 EndY=1.0161e-12 EndZ=0
    g4: LineSegment StartX=5.22862e-06 StartY=19 StartZ=0 EndX=5.22862e-06 EndY=1.0161e-12 EndZ=0
    g5: ArcOfCircle CenterX=98 CenterY=19 CenterZ=0 NormalX=0 NormalY=0 NormalZ=1 AngleXU=0 Radius=19 StartAngle=4.71239 EndAngle=6.28319
  constraints (16):
    c: Horizontal(g0)
    c: Distance(g0) = 98
    c: Coincident(g1,g0)
    c: Block(g1)
    c: Coincident(g2,g0)
    c: Vertical(g2)
    c: Distance(g2) = 19
    c: Horizontal(g3)
    c: Coincident(g4,g1)
    c: Vertical(g4)
    c: Coincident(g3,g4)
    c: Block(g3)
    c: Coincident(g5,g2)
    c: Coincident(g5,g3)
    c: Block(g0)
    c: Block(g5)
FEATURE [Sketcher::SketchObject] Sketch080  label="topSketch025"
  FullyConstrained = true
  sketch-geometry (6):
    g0: LineSegment StartX=19 StartY=38 StartZ=0 EndX=117 EndY=38 EndZ=0
    g1: ArcOfCircle CenterX=19 CenterY=19 CenterZ=0 NormalX=0 NormalY=0 NormalZ=1 AngleXU=0 Radius=19 StartAngle=1.5708 EndAngle=3.14159
    g2: LineSegment StartX=117 StartY=38 StartZ=0 EndX=117 EndY=19 EndZ=0
    g3: LineSegment StartX=98 StartY=1.0161e-12 StartZ=0 EndX=5.22862e-06 EndY=1.0161e-12 EndZ=0
    g4: LineSegment StartX=5.22862e-06 StartY=19 StartZ=0 EndX=5.22862e-06 EndY=1.0161e-12 EndZ=0
    g5: ArcOfCircle CenterX=98 CenterY=19 CenterZ=0 NormalX=0 NormalY=0 NormalZ=1 AngleXU=0 Radius=19 StartAngle=4.71239 EndAngle=6.28319
  constraints (16):
    c: Horizontal(g0)
    c: Distance(g0) = 98
    c: Coincident(g1,g0)
    c: Block(g1)
    c: Coincident(g2,g0)
    c: Vertical(g2)
    c: Distance(g2) = 19
    c: Horizontal(g3)
    c: Coincident(g4,g1)
    c: Vertical(g4)
    c: Coincident(g3,g4)
    c: Block(g3)
    c: Coincident(g5,g2)
    c: Coincident(g5,g3)
    c: Block(g0)
    c: Block(g5)
FEATURE [Part::Extrusion] Extrude070  label="sideA004"
  Base = -> Sketch080
  Dir = (0,0,1)
  DirMode = 2
  FaceMakerClass = Part::FaceMakerBullseye
  LengthFwd = 3
  LengthRev = 0
  Placement = pos=(0,0,-2.7) rot=(0,0,1;0rad)
  Solid = true
  Symmetric = false
FEATURE [Sketcher::SketchObject] Sketch081
  FullyConstrained = true
  Placement = pos=(117,19,0) rot=(0.57735,0.57735,0.57735;2.0944rad)
  sketch-geometry (8):
    g0: LineSegment StartX=-49.19 StartY=63.5 StartZ=0 EndX=-49.19 EndY=60.5 EndZ=0
    g1: LineSegment StartX=-49.19 StartY=11.5 StartZ=0 EndX=-49.19 EndY=8.5 EndZ=0
    g2: ArcOfCircle CenterX=-1.5 CenterY=62 CenterZ=0 NormalX=0 NormalY=0 NormalZ=1 AngleXU=0 Radius=1.5 StartAngle=4.71239 EndAngle=7.85398
    g3: ArcOfCircle CenterX=-1.5 CenterY=10 CenterZ=0 NormalX=0 NormalY=0 NormalZ=1 AngleXU=0 Radius=1.5 StartAngle=4.71239 EndAngle=7.85398
    g4: LineSegment StartX=-49.19 StartY=63.5 StartZ=0 EndX=-1.5 EndY=63.5 EndZ=0
    g5: LineSegment StartX=-49.19 StartY=60.5 StartZ=0 EndX=-1.5 EndY=60.5 EndZ=0
    g6: LineSegment StartX=-49.19 StartY=11.5 StartZ=0 EndX=-1.5 EndY=11.5 EndZ=0
    g7: LineSegment StartX=-49.19 StartY=8.5 StartZ=0 EndX=-1.5 EndY=8.5 EndZ=0
  constraints (19):
    c: Vertical(g0)
    c: Distance(g0) = 3
    c: Vertical(g1)
    c: Block(g1)
    c: Block(g2)
    c: Block(g3)
    c: Block(g0)
    c: Coincident(g4,g0)
    c: Coincident(g4,g2)
    c: Horizontal(g4)
    c: Coincident(g5,g0)
    c: Coincident(g5,g2)
    c: Horizontal(g5)
    c: Coincident(g6,g1)
    c: Coincident(g6,g3)
    c: Horizontal(g6)
    c: Coincident(g7,g1)
    c: Coincident(g7,g3)
    c: Horizontal(g7)
FEATURE [Part::Extrusion] Extrude071  label="sideB004"
  Base = -> Sketch079
  Dir = (0,0,1)
  DirMode = 2
  FaceMakerClass = Part::FaceMakerBullseye
  LengthFwd = 3
  LengthRev = 0
  Placement = pos=(0,0,71.7) rot=(0,0,1;0rad)
  Solid = true
  Symmetric = false
FEATURE [Part::MultiFuse] Fusion152  label="removeFromBottom004"
  Placement = pos=(2,0,0) rot=(0,0,1;0rad)
  Shapes = -> [Extrude070,Extrude071]
FEATURE [Part::Extrusion] Extrude072
  Base = -> Sketch081
  Dir = (1,0,0)
  DirMode = 2
  FaceMakerClass = Part::FaceMakerBullseye
  LengthFwd = 10
  LengthRev = 0
  Solid = true
  Symmetric = false
FEATURE [Part::Fillet] Fillet059  label="removeFromtMoreFrontCaseScrewRetainers004"
  Base = -> Extrude072
  Edges = 4 edges r=1.49: [Edge6,Edge11,Edge18,Edge23]
  Placement = pos=(-12,0,0) rot=(0,0,1;0rad)
FEATURE [Sketcher::SketchObject] Sketch082
  FullyConstrained = true
  Placement = pos=(117,19,0) rot=(0.57735,0.57735,0.57735;2.0944rad)
  sketch-geometry (8):
    g0: LineSegment StartX=-49.19 StartY=69.25 StartZ=0 EndX=-49.19 EndY=66.25 EndZ=0
    g1: LineSegment StartX=-49.19 StartY=5.75 StartZ=0 EndX=-49.19 EndY=2.75 EndZ=0
    g2: ArcOfCircle CenterX=-1.5 CenterY=67.75 CenterZ=0 NormalX=0 NormalY=0 NormalZ=1 AngleXU=0 Radius=1.5 StartAngle=4.71239 EndAngle=7.85398
    g3: ArcOfCircle CenterX=-1.5 CenterY=4.25 CenterZ=0 NormalX=0 NormalY=0 NormalZ=1 AngleXU=0 Radius=1.5 StartAngle=4.71239 EndAngle=7.85398
    g4: LineSegment StartX=-49.19 StartY=69.25 StartZ=0 EndX=-1.5 EndY=69.25 EndZ=0
    g5: LineSegment StartX=-49.19 StartY=66.25 StartZ=0 EndX=-1.5 EndY=66.25 EndZ=0
    g6: LineSegment StartX=-49.19 StartY=5.75 StartZ=0 EndX=-1.5 EndY=5.75 EndZ=0
    g7: LineSegment StartX=-49.19 StartY=2.75 StartZ=0 EndX=-1.5 EndY=2.75 EndZ=0
  constraints (19):
    c: Vertical(g0)
    c: Distance(g0) = 3
    c: Block(g0)
    c: Vertical(g1)
    c: Block(g2)
    c: Block(g3)
    c: Block(g1)
    c: Coincident(g4,g0)
    c: Coincident(g4,g2)
    c: Horizontal(g4)
    c: Coincident(g5,g0)
    c: Coincident(g5,g2)
    c: Horizontal(g5)
    c: Coincident(g6,g1)
    c: Coincident(g6,g3)
    c: Horizontal(g6)
    c: Coincident(g7,g1)
    c: Coincident(g7,g3)
    c: Horizontal(g7)
FEATURE [Part::Extrusion] Extrude073
  Base = -> Sketch082
  Dir = (1,0,0)
  DirMode = 2
  FaceMakerClass = Part::FaceMakerBullseye
  LengthFwd = 10
  LengthRev = 0
  Solid = true
  Symmetric = false
FEATURE [Part::Fillet] Fillet060  label="removeFromtMoreFrontCaseScrewRetainers005"
  Base = -> Extrude073
  Edges = 4 edges r=1.49: [Edge6,Edge11,Edge18,Edge23]
  Placement = pos=(-4,0,0) rot=(0,0,1;0rad)
FEATURE [Part::Revolution] Revolve163  label="backCaseScrewRetainer004"
  Angle = 360
  Axis = (0,1,0)
  Base = (0,0,0)
  FaceMakerClass = Part::FaceMakerBullseye
  Placement = pos=(12.5,3,62) rot=(0,0,1;0rad)
  Solid = false
  Source = -> Face149
  Symmetric = false
FEATURE [Part::Revolution] Revolve164  label="frontCaseScrewRetainer006"
  Angle = 360
  Axis = (0,1,0)
  Base = (0,0,0)
  FaceMakerClass = Part::FaceMakerBullseye
  Placement = pos=(89.5,3,68.5) rot=(0,0,1;0rad)
  Solid = false
  Source = -> Face151
  Symmetric = false
FEATURE [Part::Revolution] Revolve165  label="frontCaseScrewRetainer007"
  Angle = 360
  Axis = (0,1,0)
  Base = (0,0,0)
  FaceMakerClass = Part::FaceMakerBullseye
  Placement = pos=(89.5,3,3.5) rot=(0,0,1;0rad)
  Solid = false
  Source = -> Face152
  Symmetric = false
FEATURE [Part::Revolution] Revolve166  label="backCaseScrewRetainer005"
  Angle = 360
  Axis = (0,1,0)
  Base = (0,0,0)
  FaceMakerClass = Part::FaceMakerBullseye
  Placement = pos=(12.5,3,10) rot=(0,0,1;0rad)
  Solid = false
  Source = -> Face150
  Symmetric = false
FEATURE [Part::Revolution] Revolve167  label="moreFrontCaseScrewRetainer006"
  Angle = 360
  Axis = (0,1,0)
  Base = (0,0,0)
  FaceMakerClass = Part::FaceMakerBullseye
  Placement = pos=(109.5,4.5,68.5) rot=(0,0,1;0rad)
  Solid = false
  Source = -> Face153
  Symmetric = false
FEATURE [Part::Revolution] Revolve168  label="moreFrontCaseScrewRetainer007"
  Angle = 360
  Axis = (0,1,0)
  Base = (0,0,0)
  FaceMakerClass = Part::FaceMakerBullseye
  Placement = pos=(109.5,4.5,3.5) rot=(0,0,1;0rad)
  Solid = false
  Source = -> Face154
  Symmetric = false
FEATURE [Part::MultiFuse] Fusion151  label="screwRetainers003"
  Shapes = -> [Revolve168,Revolve167,Revolve166,Revolve165,Revolve164,Revolve163]
FEATURE [Part::Cut] Cut069  label="screwRetainers004"
  Base = -> Fusion151
  Tool = -> Fusion152
FEATURE [Part::Cut] Cut070
  Base = -> Cut069
  Tool = -> Fillet060
FEATURE [Part::Cut] Cut071  label="screwPillars001"
  Base = -> Cut070
  Tool = -> Fillet059
FEATURE [Part::MultiFuse] Fusion153  label="bottom024"
  Shapes = -> [Fusion149,Cut071]
FEATURE [Part::Cylinder] Cylinder067
  Angle = 360
  AttacherType = Attacher::AttachEngine3D
  Height = 10
  Placement = pos=(20.65,12,4.68) rot=(1,0,0;1.5708rad)
  Radius = 2
FEATURE [Part::Cylinder] Cylinder068
  Angle = 360
  AttacherType = Attacher::AttachEngine3D
  Height = 10
  Placement = pos=(20.65,12,67.38) rot=(1,0,0;1.5708rad)
  Radius = 2
FEATURE [Part::Cylinder] Cylinder069
  Angle = 360
  AttacherType = Attacher::AttachEngine3D
  Height = 10
  Placement = pos=(77.15,12,67.38) rot=(1,0,0;1.5708rad)
  Radius = 2
FEATURE [Part::Cylinder] Cylinder070
  Angle = 360
  AttacherType = Attacher::AttachEngine3D
  Height = 10
  Placement = pos=(77.15,12,4.68) rot=(1,0,0;1.5708rad)
  Radius = 2
FEATURE [Part::MultiFuse] Fusion154  label="removeFromThreadedInsertHousing001"
  Shapes = -> [Cylinder069,Cylinder068,Cylinder067,Cylinder070]
FEATURE [Part::Cut] Cut072  label="bottom025"
  Base = -> Fusion153
  Tool = -> Fusion154
FEATURE [Image::ImagePlane] ImagePlane
  XSize = 339
  YSize = 72
FEATURE [Sketcher::SketchObject] Sketch083
  FullyConstrained = true
  MapMode = 5
  Support = -> [XY_Plane]
  sketch-geometry (338):
    g0: LineSegment StartX=-151.619 StartY=28.8932 StartZ=0 EndX=-140.819 EndY=28.8932 EndZ=0
    g1: LineSegment StartX=-151.619 StartY=24.0313 StartZ=0 EndX=-151.619 EndY=28.8932 EndZ=0
    g2: LineSegment StartX=-140.819 StartY=17.7713 StartZ=0 EndX=-151.619 EndY=17.7713 EndZ=0
    g3: LineSegment StartX=-151.619 StartY=17.7713 StartZ=0 EndX=-151.619 EndY=22.6313 EndZ=0
    g4: LineSegment StartX=-151.619 StartY=22.6313 StartZ=0 EndX=-145.128 EndY=22.6313 EndZ=0
    g5: LineSegment StartX=-145.128 StartY=24.0313 StartZ=0 EndX=-140.819 EndY=28.8932 EndZ=0
    g6: LineSegment StartX=-145.128 StartY=22.6313 StartZ=0 EndX=-140.819 EndY=17.7713 EndZ=0
    g7: ArcOfCircle CenterX=-155.157 CenterY=23.3323 CenterZ=0 NormalX=0 NormalY=0 NormalZ=1 AngleXU=0 Radius=6.92354 StartAngle=1.03434 EndAngle=5.24885
    g8: ArcOfCircle CenterX=-155.157 CenterY=23.3323 CenterZ=0 NormalX=0 NormalY=0 NormalZ=1 AngleXU=0 Radius=12.6269 StartAngle=1.28675 EndAngle=4.99643
    g9: LineSegment StartX=-151.619 StartY=35.4532 StartZ=0 EndX=-151.619 EndY=29.2832 EndZ=0
    g10: LineSegment StartX=-151.619 StartY=17.3813 StartZ=0 EndX=-151.619 EndY=11.2113 EndZ=0
    g11-g21: Circle x11 (B-spline internal-alignment scaffolding for g22; pole/knot coordinates omitted)
    g22: BSplineCurve PolesCount=11 KnotsCount=9 Degree=3 IsPeriodic=0
    g23-g31: GeomPoint x9 (B-spline internal-alignment scaffolding for g22; pole/knot coordinates omitted)
    g32-g49: Circle x18 (B-spline internal-alignment scaffolding for g50; pole/knot coordinates omitted)
    g50: BSplineCurve PolesCount=18 KnotsCount=16 Degree=3 IsPeriodic=0
    g51-g66: GeomPoint x16 (B-spline internal-alignment scaffolding for g50; pole/knot coordinates omitted)
    g67: LineSegment StartX=-117.124 StartY=30.093 StartZ=0 EndX=-117.603 EndY=26.5272 EndZ=0
    g68: LineSegment StartX=-117.603 StartY=17.8472 StartZ=0 EndX=-117.124 EndY=14.2659 EndZ=0
    g69: Ellipse CenterX=-109.671 CenterY=20.025 CenterZ=0 NormalX=0 NormalY=0 NormalZ=1 MajorRadius=3.34798 MinorRadius=2.71052 AngleXU=-1.56793
    g70: GeomPoint X=-109.666 Y=18.0598 Z=0
    g71: GeomPoint X=-109.677 Y=21.9902 Z=0
    g72: Ellipse CenterX=-109.671 CenterY=20.0123 CenterZ=0 NormalX=0 NormalY=0 NormalZ=1 MajorRadius=6.93002 MinorRadius=6.36273 AngleXU=-3.13976
    g73: GeomPoint X=-112.417 Y=20.0073 Z=0
    g74: GeomPoint X=-106.925 Y=20.0173 Z=0
    g75: Ellipse CenterX=-51.7682 CenterY=20.1463 CenterZ=0 NormalX=0 NormalY=0 NormalZ=1 MajorRadius=3.19279 MinorRadius=2.71052 AngleXU=-1.52774
    g76: GeomPoint X=-51.6955 Y=18.4606 Z=0
    g77: GeomPoint X=-51.8408 Y=21.832 Z=0
    g78: GeomPoint X=-54.5142 Y=20.1413 Z=0
    g79: GeomPoint X=-49.0221 Y=20.1513 Z=0
    g80: Ellipse CenterX=-51.7682 CenterY=20.1463 CenterZ=0 NormalX=0 NormalY=0 NormalZ=1 MajorRadius=6.93002 MinorRadius=6.36273 AngleXU=-3.13976
    g81: Ellipse CenterX=-22.8436 CenterY=20.1783 CenterZ=0 NormalX=0 NormalY=0 NormalZ=1 MajorRadius=3.31512 MinorRadius=2.71052 AngleXU=-1.60214
    g82: GeomPoint X=-22.9034 Y=18.2706 Z=0
    g83: GeomPoint X=-22.7838 Y=22.0861 Z=0
    g84: GeomPoint X=-25.5897 Y=20.1733 Z=0
    g85: GeomPoint X=-20.0976 Y=20.1833 Z=0
    g86: Ellipse CenterX=-22.8436 CenterY=20.1783 CenterZ=0 NormalX=0 NormalY=0 NormalZ=1 MajorRadius=6.93002 MinorRadius=6.36273 AngleXU=-3.13976
    g87: LineSegment StartX=-101.889 StartY=14.1107 StartZ=0 EndX=-97.7455 EndY=14.1107 EndZ=0
    g88: LineSegment StartX=-93.8155 StartY=14.1107 StartZ=0 EndX=-89.6755 EndY=14.1107 EndZ=0
    g89: LineSegment StartX=-85.7455 StartY=14.1107 StartZ=0 EndX=-81.6055 EndY=14.1107 EndZ=0
    g90: LineSegment StartX=-101.889 StartY=14.1107 StartZ=0 EndX=-101.889 EndY=25.9907 EndZ=0
    g91: LineSegment StartX=-101.889 StartY=25.9907 StartZ=0 EndX=-97.8594 EndY=25.9907 EndZ=0
    g92: LineSegment StartX=-97.8594 StartY=25.9907 StartZ=0 EndX=-97.8594 EndY=24.0907 EndZ=0
    g93: LineSegment StartX=-97.7455 StartY=14.1107 StartZ=0 EndX=-97.7455 EndY=19.9107 EndZ=0
    g94: LineSegment StartX=-89.6755 StartY=14.1107 StartZ=0 EndX=-89.6755 EndY=19.9107 EndZ=0
    g95: LineSegment StartX=-93.8155 StartY=14.1107 StartZ=0 EndX=-93.8155 EndY=21.0107 EndZ=0
    g96-g106: Circle x11 (B-spline internal-alignment scaffolding for g107; pole/knot coordinates omitted)
    g107: BSplineCurve PolesCount=11 KnotsCount=9 Degree=3 IsPeriodic=0
    g108-g116: GeomPoint x9 (B-spline internal-alignment scaffolding for g107; pole/knot coordinates omitted)
    g117: BSplineCurve PolesCount=11 KnotsCount=9 Degree=3 IsPeriodic=0
    g118-g125: Circle x8 (B-spline internal-alignment scaffolding for g126; pole/knot coordinates omitted)
    g126: BSplineCurve PolesCount=8 KnotsCount=6 Degree=3 IsPeriodic=0
    g127-g132: GeomPoint x6 (B-spline internal-alignment scaffolding for g126; pole/knot coordinates omitted)
    g133: BSplineCurve PolesCount=8 KnotsCount=6 Degree=3 IsPeriodic=0
    g134: LineSegment StartX=-85.7455 StartY=21.0107 StartZ=0 EndX=-85.7455 EndY=14.1107 EndZ=0
    g135: LineSegment StartX=-80.0879 StartY=14.1107 StartZ=0 EndX=-75.944 EndY=14.1107 EndZ=0
    g136: LineSegment StartX=-72.014 StartY=14.1107 StartZ=0 EndX=-67.874 EndY=14.1107 EndZ=0
    g137: LineSegment StartX=-63.944 StartY=14.1107 StartZ=0 EndX=-59.804 EndY=14.1107 EndZ=0
    g138: LineSegment StartX=-80.0879 StartY=14.1107 StartZ=0 EndX=-80.0879 EndY=25.9907 EndZ=0
    g139: LineSegment StartX=-80.0879 StartY=25.9907 StartZ=0 EndX=-76.0579 EndY=25.9907 EndZ=0
    g140: LineSegment StartX=-76.0579 StartY=25.9907 StartZ=0 EndX=-76.0579 EndY=24.0907 EndZ=0
    g141: LineSegment StartX=-75.944 StartY=14.1107 StartZ=0 EndX=-75.944 EndY=19.9107 EndZ=0
    g142: LineSegment StartX=-67.874 StartY=14.1107 StartZ=0 EndX=-67.874 EndY=19.9107 EndZ=0
    g143: LineSegment StartX=-72.014 StartY=14.1107 StartZ=0 EndX=-72.014 EndY=21.0107 EndZ=0
    g144-g148: Circle x5 (B-spline internal-alignment scaffolding for g149; pole/knot coordinates omitted)
    g149: BSplineCurve PolesCount=11 KnotsCount=9 Degree=3 IsPeriodic=0
    g150-g158: GeomPoint x9 (B-spline internal-alignment scaffolding for g149; pole/knot coordinates omitted)
    g159: BSplineCurve PolesCount=11 KnotsCount=9 Degree=3 IsPeriodic=0
    g160-g167: Circle x8 (B-spline internal-alignment scaffolding for g168; pole/knot coordinates omitted)
    g168: BSplineCurve PolesCount=8 KnotsCount=6 Degree=3 IsPeriodic=0
    g169-g174: GeomPoint x6 (B-spline internal-alignment scaffolding for g168; pole/knot coordinates omitted)
    g175: BSplineCurve PolesCount=8 KnotsCount=6 Degree=3 IsPeriodic=0
    g176: LineSegment StartX=-63.944 StartY=21.0107 StartZ=0 EndX=-63.944 EndY=14.1107 EndZ=0
    g177: LineSegment StartX=-59.804 StartY=14.1107 StartZ=0 EndX=-59.804 EndY=21.5868 EndZ=0
    g178: BSplineCurve PolesCount=4 KnotsCount=2 Degree=3 IsPeriodic=0
    g179: GeomPoint X=-59.804 Y=21.5868 Z=0
    g180: GeomPoint X=-60.2379 Y=24.0907 Z=0
    g181: LineSegment StartX=-81.6055 StartY=14.1107 StartZ=0 EndX=-81.6055 EndY=21.5868 EndZ=0
    g182: LineSegment StartX=-151.619 StartY=24.0313 StartZ=0 EndX=-145.128 EndY=24.0313 EndZ=0
    g183: Circle CenterX=-82.0394 CenterY=24.0907 CenterZ=0 NormalX=0 NormalY=0 NormalZ=1 AngleXU=0 Radius=1
    g184: Circle CenterX=-81.7131 CenterY=23.2736 CenterZ=0 NormalX=0 NormalY=0 NormalZ=1 AngleXU=0 Radius=1
    g185: Circle CenterX=-81.6055 CenterY=21.5868 CenterZ=0 NormalX=0 NormalY=0 NormalZ=1 AngleXU=0 Radius=1
    g186: BSplineCurve PolesCount=3 KnotsCount=2 Degree=2 IsPeriodic=0
    g187: GeomPoint X=-82.0394 Y=24.0907 Z=0
    g188: GeomPoint X=-81.6055 Y=21.5868 Z=0
    g189: Ellipse CenterX=-37.3522 CenterY=19.9515 CenterZ=0 NormalX=0 NormalY=0 NormalZ=1 MajorRadius=2.99755 MinorRadius=2.49 AngleXU=1.5708
    g190: GeomPoint X=-37.3522 Y=21.6203 Z=0
    g191: GeomPoint X=-37.3522 Y=18.2826 Z=0
    g192: ArcOfEllipse CenterX=-38.7647 CenterY=20.06 CenterZ=0 NormalX=0 NormalY=0 NormalZ=1 MajorRadius=6.30025 MinorRadius=5.3849 AngleXU=1.57276 StartAngle=5.50632 EndAngle=10.3035
    g193: GeomPoint X=-38.7711 Y=23.3304 Z=0
    g194: GeomPoint X=-38.7583 Y=16.7895 Z=0
    g195: LineSegment StartX=-34.6109 StartY=14.1107 StartZ=0 EndX=-30.8984 EndY=14.1107 EndZ=0
    g196: LineSegment StartX=-30.8984 StartY=14.1107 StartZ=0 EndX=-30.8984 EndY=31.1784 EndZ=0
    g197: LineSegment StartX=-30.8984 StartY=31.1784 StartZ=0 EndX=-34.9984 EndY=31.1784 EndZ=0
    g198: LineSegment StartX=-34.9984 StartY=24.5602 StartZ=0 EndX=-34.9984 EndY=31.1784 EndZ=0
    g199: LineSegment StartX=-34.6109 StartY=16.0476 StartZ=0 EndX=-34.6109 EndY=14.1107 EndZ=0
    g200: LineSegment StartX=-14.8781 StartY=14.1107 StartZ=0 EndX=-10.5106 EndY=14.1107 EndZ=0
    g201: LineSegment StartX=-14.8781 StartY=14.1107 StartZ=0 EndX=-14.8781 EndY=25.8504 EndZ=0
    g202: LineSegment StartX=-14.8781 StartY=25.8504 StartZ=0 EndX=-10.8534 EndY=25.8504 EndZ=0
    g203: LineSegment StartX=-10.8534 StartY=25.8504 StartZ=0 EndX=-10.8534 EndY=24.0923 EndZ=0
    g204: LineSegment StartX=-10.5106 StartY=14.1107 StartZ=0 EndX=-10.5106 EndY=19.7752 EndZ=0
    g205: LineSegment StartX=-5.96397 StartY=25.9304 StartZ=0 EndX=-5.96397 EndY=22.574 EndZ=0
    g206-g214: Circle x9 (B-spline internal-alignment scaffolding for g215; pole/knot coordinates omitted)
    g215: BSplineCurve PolesCount=9 KnotsCount=7 Degree=3 IsPeriodic=0
    g216-g222: GeomPoint x7 (B-spline internal-alignment scaffolding for g215; pole/knot coordinates omitted)
    g223-g232: Circle x10 (B-spline internal-alignment scaffolding for g233; pole/knot coordinates omitted)
    g233: BSplineCurve PolesCount=10 KnotsCount=8 Degree=3 IsPeriodic=0
    g234-g241: GeomPoint x8 (B-spline internal-alignment scaffolding for g233; pole/knot coordinates omitted)
    g242: LineSegment StartX=-1.58923 StartY=21.0696 StartZ=0 EndX=2.62034 EndY=21.0696 EndZ=0
    g243: LineSegment StartX=-1.55856 StartY=18.7342 StartZ=0 EndX=6.45946 EndY=18.7342 EndZ=0
    g244: LineSegment StartX=5.29231 StartY=17.386 StartZ=0 EndX=5.29231 EndY=14.3674 EndZ=0
    g245-g269: Circle x25 (B-spline internal-alignment scaffolding for g270; pole/knot coordinates omitted)
    g270: BSplineCurve PolesCount=25 KnotsCount=23 Degree=3 IsPeriodic=0
    g271-g293: GeomPoint x23 (B-spline internal-alignment scaffolding for g270; pole/knot coordinates omitted)
    g294-g304: Circle x11 (B-spline internal-alignment scaffolding for g305; pole/knot coordinates omitted)
    g305: BSplineCurve PolesCount=11 KnotsCount=9 Degree=3 IsPeriodic=0
    g306-g314: GeomPoint x9 (B-spline internal-alignment scaffolding for g305; pole/knot coordinates omitted)
    g315-g326: Circle x12 (B-spline internal-alignment scaffolding for g327; pole/knot coordinates omitted)
    g327: BSplineCurve PolesCount=12 KnotsCount=10 Degree=3 IsPeriodic=0
    g328-g337: GeomPoint x10 (B-spline internal-alignment scaffolding for g327; pole/knot coordinates omitted)
  constraints (252):
    c: Coincident(g1,g0)
    c: Horizontal(g0)
    c: Vertical(g1)
    c: Coincident(g2,g3)
    c: Coincident(g3,g4)
    c: Horizontal(g4)
    c: Horizontal(g2)
    c: Vertical(g3)
    c: Block(g1)
    c: Distance(g3) = 4.86
    c: Block(g4)
    c: Distance(g0) = 10.8
    c: Distance(g2) = 10.8
    c: Coincident(g5,g0)
    c: Coincident(g6,g4)
    c: Coincident(g6,g2)
    c: Block(g8)
    c: Block(g7)
    c: Coincident(g9,g8)
    c: Coincident(g9,g7)
    c: Vertical(g9)
    c: Coincident(g10,g7)
    c: Coincident(g10,g8)
    c: Vertical(g10)
    c: Weight(g11) = 1
    c: Equal(g11, g12-g21) x10
    c: InternalAlignment(g11-g21 -> g22) x11
    c: InternalAlignment(g23-g31 -> g22) x9
    c: Block(g22)
    c: Weight(g32) = 1
    c: Equal(g32, g33-g49) x17
    c: InternalAlignment(g32-g49 -> g50) x18
    c: InternalAlignment(g51-g66 -> g50) x16
    c: Block(g50)
    c: Coincident(g67,g50)
    c: Coincident(g67,g22)
    c: Coincident(g68,g22)
    c: Coincident(g68,g50)
    c: InternalAlignment(g70,g69)
    c: InternalAlignment(g71,g69)
    c: Block(g69)
    c: InternalAlignment(g73,g72)
    c: InternalAlignment(g74,g72)
    c: Block(g72)
    c: InternalAlignment(g76,g75)
    c: InternalAlignment(g77,g75)
    c: InternalAlignment(g78,g80)
    c: InternalAlignment(g79,g80)
    c: Block(g80)
    c: Coincident(g75,g80)
    c: Block(g75)
    c: InternalAlignment(g82,g81)
    c: InternalAlignment(g83,g81)
    c: InternalAlignment(g84,g86)
    c: InternalAlignment(g85,g86)
    c: Block(g86)
    c: Coincident(g81,g86)
    c: Block(g81)
    c: Horizontal(g87)
    c: Block(g87)
    c: Horizontal(g88)
    c: Distance(g88) = 4.14
    c: Horizontal(g89)
    c: Equal(g88,g89) = 4.14
    c: Block(g89)
    c: Block(g88)
    c: Coincident(g90,g87)
    c: Vertical(g90)
    c: Distance(g90) = 11.88
    c: Coincident(g91,g90)
    c: Horizontal(g91)
    c: Coincident(g92,g91)
    c: Vertical(g92)
    c: Distance(g91) = 4.03
    c: Distance(g92) = 1.9
    c: Coincident(g93,g87)
    c: Vertical(g93)
    c: Vertical(g94)
    c: Coincident(g94,g88)
    c: Distance(g93) = 5.8
    c: Distance(g94) = 5.8
    c: Vertical(g95)
    c: Coincident(g95,g88)
    c: Distance(g95) = 6.9
    c: Coincident(g107,g92)
    c: Weight(g96) = 1
    c: Equal(g96, g97-g106) x10
    c: InternalAlignment(g96-g106 -> g107) x11
    c: InternalAlignment(g108-g116 -> g107) x9
    c: Block(g107)
    c: Block(g117)
    c: Coincident(g126,g93)
    c: Weight(g118) = 1
    c: Equal(g118, g119-g125) x7
    c: Coincident(g126,g95)
    c: InternalAlignment(g118-g125 -> g126) x8
    c: InternalAlignment(g127-g132 -> g126) x6
    c: Coincident(g133,g94)
    c: Block(g126)
    c: Block(g133)
    c: Coincident(g134,g133)
    c: Coincident(g134,g89)
    c: Vertical(g134)
    c: Horizontal(g135)
    c: Block(g135)
    c: Horizontal(g136)
    c: Equal(g88,g136) = 4.14
    c: Horizontal(g137)
    c: Equal(g136,g137) = 4.14
    c: Block(g137)
    c: Block(g136)
    c: Coincident(g138,g135)
    c: Vertical(g138)
    c: Equal(g90,g138) = 11.88
    c: Coincident(g139,g138)
    c: Horizontal(g139)
    c: Coincident(g140,g139)
    c: Vertical(g140)
    c: Equal(g91,g139) = 4.03
    c: Equal(g92,g140) = 1.9
    c: Coincident(g141,g135)
    c: Vertical(g141)
    c: Vertical(g142)
    c: Coincident(g142,g136)
    c: Equal(g93,g141) = 5.8
    c: Equal(g94,g142) = 5.8
    c: Vertical(g143)
    c: Coincident(g143,g136)
    c: Equal(g95,g143) = 6.9
    c: Coincident(g149,g140)
    c: Equal(g96,g144) = 1
    c: Equal(g144, g145-g148) x4
    c: InternalAlignment(g144-g148 -> g149) x5
    c: InternalAlignment(g150-g158 -> g149) x9
    c: Block(g149)
    c: Block(g159)
    c: Coincident(g168,g141)
    c: Equal(g118,g160) = 1
    c: Equal(g160, g161-g167) x7
    c: Coincident(g168,g143)
    c: InternalAlignment(g160-g167 -> g168) x8
    c: InternalAlignment(g169-g174 -> g168) x6
    c: Coincident(g175,g142)
    c: Block(g168)
    c: Block(g175)
    c: Coincident(g176,g175)
    c: Coincident(g176,g137)
    c: Vertical(g176)
    c: Coincident(g177,g137)
    c: Vertical(g177)
    c: Coincident(g178,g177)
    c: Coincident(g178,g159)
    c: InternalAlignment(g179,g178)
    c: InternalAlignment(g180,g178)
    c: Block(g178)
    c: Vertical(g181)
    c: Coincident(g181,g89)
    c: Block(g5)
    c: Coincident(g182,g1)
    c: Coincident(g182,g5)
    c: Horizontal(g182)
    c: Coincident(g186,g117)
    c: Weight(g183) = 1
    c: Equal(g183,g184)
    c: Equal(g183,g185)
    c: Coincident(g186,g181)
    c: InternalAlignment(g183,g186)
    c: InternalAlignment(g184,g186)
    c: InternalAlignment(g185,g186)
    c: InternalAlignment(g187,g186)
    c: InternalAlignment(g188,g186)
    c: Block(g186)
    c: InternalAlignment(g190,g189)
    c: InternalAlignment(g191,g189)
    c: Block(g189)
    c: InternalAlignment(g193,g192)
    c: InternalAlignment(g194,g192)
    c: Block(g192)
    c: Horizontal(g195)
    c: Block(g195)
    c: Coincident(g196,g195)
    c: Vertical(g196)
    c: Block(g196)
    c: Distance(g195) = 3.71244
    c: Coincident(g197,g196)
    c: Horizontal(g197)
    c: Distance(g197) = 4.1
    c: Coincident(g198,g192)
    c: Coincident(g198,g197)
    c: Vertical(g198)
    c: Block(g198)
    c: Coincident(g199,g192)
    c: Coincident(g199,g195)
    c: Vertical(g199)
    c: Block(g199)
    c: Horizontal(g200)
    c: Block(g200)
    c: Coincident(g201,g200)
    c: Vertical(g201)
    c: Block(g201)
    c: Coincident(g202,g201)
    c: Horizontal(g202)
    c: Block(g202)
    c: Coincident(g203,g202)
    c: Vertical(g203)
    c: Block(g203)
    c: Coincident(g204,g200)
    c: Vertical(g204)
    c: Block(g204)
    c: Coincident(g215,g203)
    c: Weight(g206) = 1
    c: Equal(g206, g207-g214) x8
    c: Coincident(g215,g205)
    c: InternalAlignment(g206-g214 -> g215) x9
    c: InternalAlignment(g216-g222 -> g215) x7
    c: Coincident(g233,g204)
    c: Weight(g223) = 1
    c: Equal(g223, g224-g232) x9
    c: Coincident(g233,g205)
    c: InternalAlignment(g223-g232 -> g233) x10
    c: InternalAlignment(g234-g241 -> g233) x8
    c: Vertical(g205)
    c: Block(g205)
    c: Block(g215)
    c: Block(g233)
    c: Horizontal(g242)
    c: Horizontal(g243)
    c: Block(g242)
    c: Block(g243)
    c: Vertical(g244)
    c: Block(g244)
    c: Coincident(g270,g243)
    c: Weight(g245) = 1
    c: Equal(g245, g246-g269) x24
    c: Coincident(g270,g244)
    c: InternalAlignment(g245-g269 -> g270) x25
    c: InternalAlignment(g271-g293 -> g270) x23
    c: Coincident(g305,g242)
    c: Weight(g294) = 1
    c: Equal(g294, g295-g304) x10
    c: Coincident(g305,g242)
    c: InternalAlignment(g294-g304 -> g305) x11
    c: InternalAlignment(g306-g314 -> g305) x9
    c: Block(g305)
    c: Coincident(g327,g243)
    c: Weight(g315) = 1
    c: Equal(g315, g316-g326) x11
    c: Coincident(g327,g244)
    c: InternalAlignment(g315-g326 -> g327) x12
    c: InternalAlignment(g328-g337 -> g327) x10
    c: Block(g327)
    c: Block(g270)
FEATURE [PartDesign::Body] Body
  Group = -> [Sketch083]
  Origin = -> Origin
FEATURE [Sketcher::SketchObject] Sketch084
  FullyConstrained = true
  MapMode = 5
  Support = -> [XY_Plane001]
FEATURE [PartDesign::Body] Body001
  Group = -> [Sketch084]
  Origin = -> Origin001
